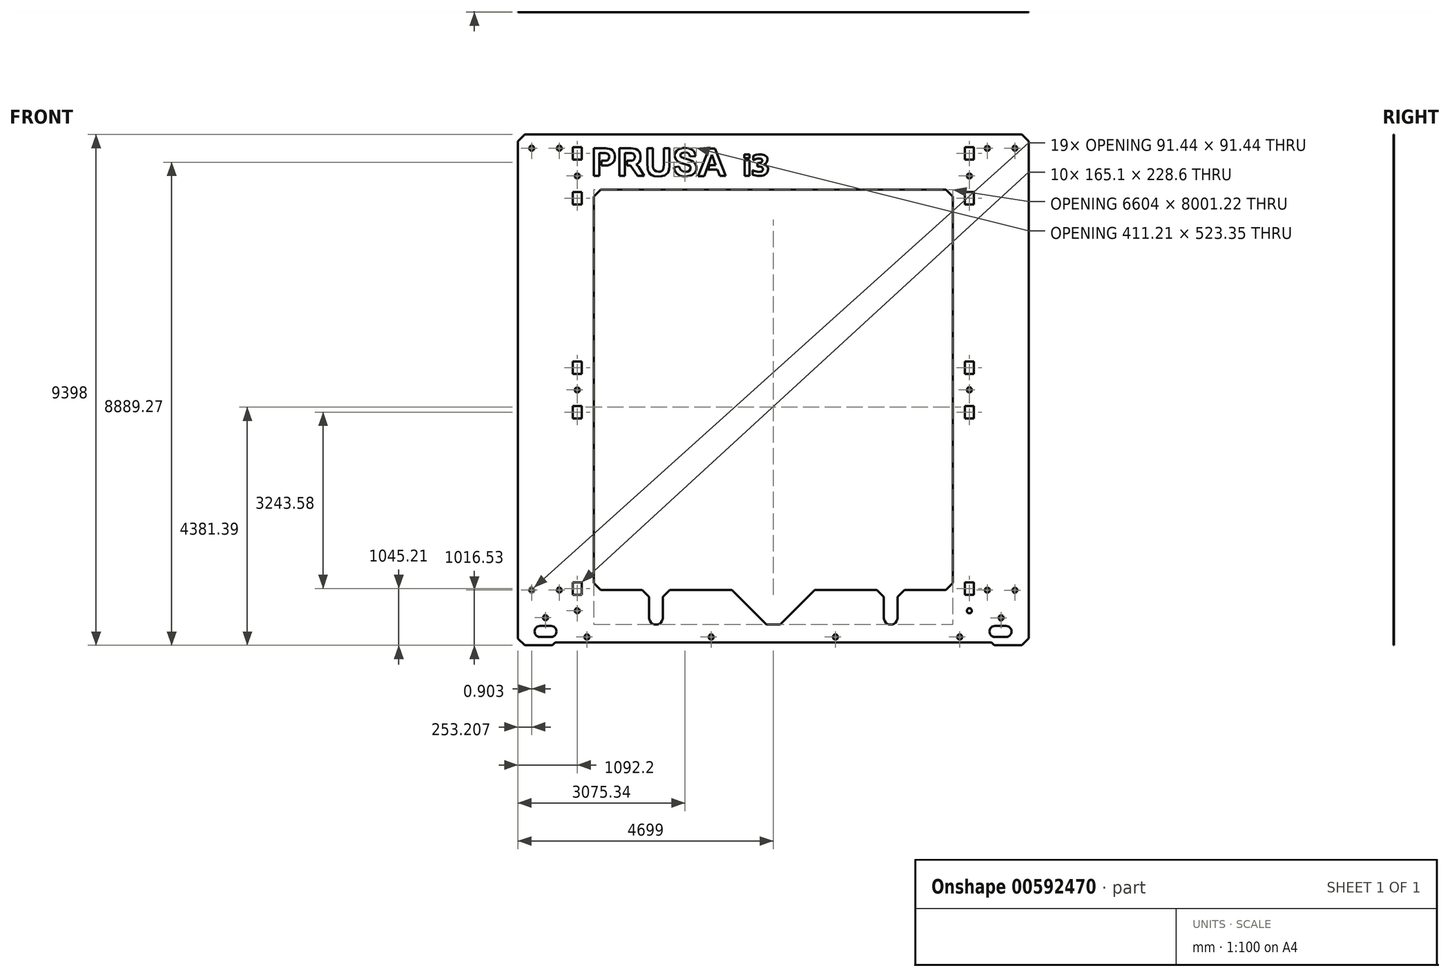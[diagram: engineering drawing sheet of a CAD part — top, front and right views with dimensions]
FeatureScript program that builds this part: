
annotation { "Feature Type Name" : "Feature", "Feature Type Description" : "" }
export const myFeature = defineFeature(function(context is Context, id is Id, definition is map)
    precondition{}
    {
        {
            var Q0;
            Q0=qCreatedBy(makeId("Front.planeOp"),FACE);
            var sketch = newSketch(context, id + "F0", { "sketchPlane" : qUnion([Q0])});
            skLineSegment(sketch, "E0", {"start": v(-2856.77, -127.8) * mm, "end": v(-2858.56, -127.8) * mm});
            skLineSegment(sketch, "E1", {"start": v(-1840.77, -1143.8) * mm, "end": v(-1842.56, -1143.8) * mm});
            skLineSegment(sketch, "E2", {"start": v(-4279.17, -127.8) * mm, "end": v(-5295.17, -1143.8) * mm});
            skLineSegment(sketch, "E3", {"start": v(-2856.77, -127.8) * mm, "end": v(-1840.77, -1143.8) * mm});
            skLineSegment(sketch, "E4", {"start": v(-2858.56, -127.8) * mm, "end": v(-1842.56, -1143.8) * mm});
            skLineSegment(sketch, "E5", {"start": v(-4280.96, -127.8) * mm, "end": v(-5296.96, -1143.8) * mm});
            skLineSegment(sketch, "E6", {"start": v(-5295.17, -1143.8) * mm, "end": v(-5296.96, -1143.8) * mm});
            skLineSegment(sketch, "E7", {"start": v(-4279.17, -127.8) * mm, "end": v(-4280.96, -127.8) * mm});
            skLineSegment(sketch, "E8", {"start": v(-7758.97, -4699.8) * mm, "end": v(-7885.97, -4577.68) * mm});
            skLineSegment(sketch, "E9", {"start": v(-7885.97, 4571.2) * mm, "end": v(-7758.97, 4698.2) * mm});
            skLineSegment(sketch, "E10", {"start": v(-7758.97, 4698.2) * mm, "end": v(1385.03, 4698.2) * mm});
            skLineSegment(sketch, "E11", {"start": v(1385.03, 4698.2) * mm, "end": v(1512.03, 4571.2) * mm});
            skLineSegment(sketch, "E12", {"start": v(1512.03, -4572.8) * mm, "end": v(1385.03, -4699.8) * mm});
            skLineSegment(sketch, "E13", {"start": v(877.03, -4699.8) * mm, "end": v(826.23, -4649) * mm});
            skLineSegment(sketch, "E14", {"start": v(826.23, -4649) * mm, "end": v(-7200.17, -4649) * mm});
            skLineSegment(sketch, "E15", {"start": v(-7200.17, -4649) * mm, "end": v(-7250.97, -4699.8) * mm});
            skLineSegment(sketch, "E16", {"start": v(-5853.97, -3683.8) * mm, "end": v(-6361.97, -3683.8) * mm});
            skLineSegment(sketch, "E17", {"start": v(-6361.97, -3683.8) * mm, "end": v(-6488.97, -3556.8) * mm});
            skLineSegment(sketch, "E18", {"start": v(-6488.97, -3556.8) * mm, "end": v(-6488.97, 3555.2) * mm});
            skLineSegment(sketch, "E19", {"start": v(-6488.97, 3555.2) * mm, "end": v(-6361.97, 3682.2) * mm});
            skLineSegment(sketch, "E20", {"start": v(-6361.97, 3682.2) * mm, "end": v(-11.97, 3682.2) * mm});
            skLineSegment(sketch, "E21", {"start": v(-11.97, 3682.2) * mm, "end": v(115.03, 3555.2) * mm});
            skLineSegment(sketch, "E22", {"start": v(115.03, 3555.2) * mm, "end": v(115.03, -3556.8) * mm});
            skLineSegment(sketch, "E23", {"start": v(115.03, -3556.8) * mm, "end": v(-11.97, -3683.8) * mm});
            skLineSegment(sketch, "E24", {"start": v(-11.97, -3683.8) * mm, "end": v(-519.97, -3683.8) * mm});
            skLineSegment(sketch, "E25", {"start": v(-3313.97, -4318.8) * mm, "end": v(-3059.97, -4318.8) * mm});
            skLineSegment(sketch, "E26", {"start": v(-3059.97, -4318.8) * mm, "end": v(-2424.97, -3683.8) * mm});
            skLineSegment(sketch, "E27", {"start": v(-3313.97, -4318.8) * mm, "end": v(-3948.97, -3683.8) * mm});
            skLineSegment(sketch, "E28", {"start": v(-5091.97, -3683.8) * mm, "end": v(-3948.97, -3683.8) * mm});
            skLineSegment(sketch, "E29", {"start": v(-2424.97, -3683.8) * mm, "end": v(-1281.97, -3683.8) * mm});
            skLineSegment(sketch, "E30", {"start": v(-2043.97, 1142.2) * mm, "end": v(-2043.97, 1140.4) * mm});
            skLineSegment(sketch, "E31", {"start": v(1004.03, -4547.4) * mm, "end": v(1011.13, -4546.47) * mm});
            skLineSegment(sketch, "E32", {"start": v(-7885.97, -4577.68) * mm, "end": v(-7885.97, 4571.2) * mm});
            skLineSegment(sketch, "E33", {"start": v(1512.03, 4571.2) * mm, "end": v(1512.03, -4572.8) * mm});
            skLineSegment(sketch, "E34", {"start": v(1385.03, -4699.8) * mm, "end": v(877.03, -4699.8) * mm});
            skLineSegment(sketch, "E35", {"start": v(-7250.97, -4699.8) * mm, "end": v(-7758.97, -4699.8) * mm});
            skLineSegment(sketch, "E36", {"start": v(803.36, -4394.07) * mm, "end": v(793.21, -4418.58) * mm});
            skLineSegment(sketch, "E37", {"start": v(789.75, -4444.87) * mm, "end": v(793.21, -4471.17) * mm});
            skLineSegment(sketch, "E38", {"start": v(865.06, -4346.74) * mm, "end": v(840.55, -4356.88) * mm});
            skLineSegment(sketch, "E39", {"start": v(1120.75, -4346.74) * mm, "end": v(1094.45, -4343.27) * mm});
            skLineSegment(sketch, "E40", {"start": v(1166.3, -4516.72) * mm, "end": v(1182.44, -4495.67) * mm});
            skLineSegment(sketch, "E41", {"start": v(1145.25, -4532.86) * mm, "end": v(1166.3, -4516.72) * mm});
            skLineSegment(sketch, "E42", {"start": v(1120.75, -4543.01) * mm, "end": v(1145.25, -4532.86) * mm});
            skLineSegment(sketch, "E43", {"start": v(840.55, -4532.86) * mm, "end": v(865.06, -4543.01) * mm});
            skLineSegment(sketch, "E44", {"start": v(865.06, -4543.01) * mm, "end": v(891.35, -4546.47) * mm});
            skLineSegment(sketch, "E45", {"start": v(793.21, -4471.17) * mm, "end": v(803.36, -4495.67) * mm});
            skLineSegment(sketch, "E46", {"start": v(1166.3, -4373.03) * mm, "end": v(1145.25, -4356.88) * mm});
            skLineSegment(sketch, "E47", {"start": v(1182.44, -4394.07) * mm, "end": v(1166.3, -4373.03) * mm});
            skLineSegment(sketch, "E48", {"start": v(891.35, -4343.27) * mm, "end": v(1094.45, -4343.27) * mm});
            skLineSegment(sketch, "E49", {"start": v(840.55, -4356.88) * mm, "end": v(819.51, -4373.03) * mm});
            skLineSegment(sketch, "E50", {"start": v(819.51, -4373.03) * mm, "end": v(803.36, -4394.07) * mm});
            skLineSegment(sketch, "E51", {"start": v(819.51, -4516.72) * mm, "end": v(840.55, -4532.86) * mm});
            skLineSegment(sketch, "E52", {"start": v(1192.59, -4418.58) * mm, "end": v(1182.44, -4394.07) * mm});
            skLineSegment(sketch, "E53", {"start": v(793.21, -4418.58) * mm, "end": v(789.75, -4444.87) * mm});
            skLineSegment(sketch, "E54", {"start": v(803.36, -4495.67) * mm, "end": v(819.51, -4516.72) * mm});
            skLineSegment(sketch, "E55", {"start": v(1192.59, -4471.17) * mm, "end": v(1196.05, -4444.87) * mm});
            skLineSegment(sketch, "E56", {"start": v(1182.44, -4495.67) * mm, "end": v(1192.59, -4471.17) * mm});
            skLineSegment(sketch, "E57", {"start": v(891.35, -4343.27) * mm, "end": v(865.06, -4346.74) * mm});
            skLineSegment(sketch, "E58", {"start": v(1096.15, -4546.47) * mm, "end": v(1120.75, -4543.01) * mm});
            skLineSegment(sketch, "E59", {"start": v(891.35, -4546.47) * mm, "end": v(996.92, -4546.47) * mm});
            skLineSegment(sketch, "E60", {"start": v(1196.05, -4444.87) * mm, "end": v(1192.59, -4418.58) * mm});
            skLineSegment(sketch, "E61", {"start": v(1145.25, -4356.88) * mm, "end": v(1120.75, -4346.74) * mm});
            skLineSegment(sketch, "E62", {"start": v(996.92, -4546.47) * mm, "end": v(1004.03, -4547.4) * mm});
            skLineSegment(sketch, "E63", {"start": v(996.92, -4546.47) * mm, "end": v(1011.13, -4546.47) * mm});
            skLineSegment(sketch, "E64", {"start": v(1011.13, -4546.47) * mm, "end": v(1096.15, -4546.47) * mm});
            skLineSegment(sketch, "E65", {"start": v(-7580.5, -4444.87) * mm, "end": v(-7577.04, -4471.17) * mm});
            skLineSegment(sketch, "E66", {"start": v(-7566.89, -4394.07) * mm, "end": v(-7577.04, -4418.58) * mm});
            skLineSegment(sketch, "E67", {"start": v(-7505.2, -4346.74) * mm, "end": v(-7529.7, -4356.88) * mm});
            skLineSegment(sketch, "E68", {"start": v(-7249.5, -4346.74) * mm, "end": v(-7275.8, -4343.27) * mm});
            skLineSegment(sketch, "E69", {"start": v(-7203.96, -4516.72) * mm, "end": v(-7187.81, -4495.67) * mm});
            skLineSegment(sketch, "E70", {"start": v(-7225, -4532.86) * mm, "end": v(-7203.96, -4516.72) * mm});
            skLineSegment(sketch, "E71", {"start": v(-7249.5, -4543.01) * mm, "end": v(-7225, -4532.86) * mm});
            skLineSegment(sketch, "E72", {"start": v(-7529.7, -4532.86) * mm, "end": v(-7505.2, -4543.01) * mm});
            skLineSegment(sketch, "E73", {"start": v(-7505.2, -4543.01) * mm, "end": v(-7478.9, -4546.47) * mm});
            skLineSegment(sketch, "E74", {"start": v(-7577.04, -4471.17) * mm, "end": v(-7566.89, -4495.67) * mm});
            skLineSegment(sketch, "E75", {"start": v(-7203.96, -4373.03) * mm, "end": v(-7225, -4356.88) * mm});
            skLineSegment(sketch, "E76", {"start": v(-7187.81, -4394.07) * mm, "end": v(-7203.96, -4373.03) * mm});
            skLineSegment(sketch, "E77", {"start": v(-7478.9, -4343.27) * mm, "end": v(-7275.8, -4343.27) * mm});
            skLineSegment(sketch, "E78", {"start": v(-7529.7, -4356.88) * mm, "end": v(-7550.74, -4373.03) * mm});
            skLineSegment(sketch, "E79", {"start": v(-7550.74, -4373.03) * mm, "end": v(-7566.89, -4394.07) * mm});
            skLineSegment(sketch, "E80", {"start": v(-7550.74, -4516.72) * mm, "end": v(-7529.7, -4532.86) * mm});
            skLineSegment(sketch, "E81", {"start": v(-7177.66, -4418.58) * mm, "end": v(-7187.81, -4394.07) * mm});
            skLineSegment(sketch, "E82", {"start": v(-7577.04, -4418.58) * mm, "end": v(-7580.5, -4444.87) * mm});
            skLineSegment(sketch, "E83", {"start": v(-7566.89, -4495.67) * mm, "end": v(-7550.74, -4516.72) * mm});
            skLineSegment(sketch, "E84", {"start": v(-7177.66, -4471.17) * mm, "end": v(-7174.2, -4444.87) * mm});
            skLineSegment(sketch, "E85", {"start": v(-7187.81, -4495.67) * mm, "end": v(-7177.66, -4471.17) * mm});
            skLineSegment(sketch, "E86", {"start": v(-7478.9, -4343.27) * mm, "end": v(-7505.2, -4346.74) * mm});
            skLineSegment(sketch, "E87", {"start": v(-7274.1, -4546.47) * mm, "end": v(-7249.5, -4543.01) * mm});
            skLineSegment(sketch, "E88", {"start": v(-7478.9, -4546.47) * mm, "end": v(-7274.1, -4546.47) * mm});
            skLineSegment(sketch, "E89", {"start": v(-7174.2, -4444.87) * mm, "end": v(-7177.66, -4418.58) * mm});
            skLineSegment(sketch, "E90", {"start": v(-7225, -4356.88) * mm, "end": v(-7249.5, -4346.74) * mm});
            skLineSegment(sketch, "E91", {"start": v(337.28, 4234.46) * mm, "end": v(337.28, 4463.06) * mm});
            skLineSegment(sketch, "E92", {"start": v(337.28, 4463.06) * mm, "end": v(502.38, 4463.06) * mm});
            skLineSegment(sketch, "E93", {"start": v(502.38, 4463.06) * mm, "end": v(502.38, 4234.46) * mm});
            skLineSegment(sketch, "E94", {"start": v(502.38, 4234.46) * mm, "end": v(337.28, 4234.46) * mm});
            skLineSegment(sketch, "E95", {"start": v(337.28, 3414.04) * mm, "end": v(337.28, 3642.64) * mm});
            skLineSegment(sketch, "E96", {"start": v(337.28, 3642.64) * mm, "end": v(502.38, 3642.64) * mm});
            skLineSegment(sketch, "E97", {"start": v(502.38, 3642.64) * mm, "end": v(502.38, 3414.04) * mm});
            skLineSegment(sketch, "E98", {"start": v(502.38, 3414.04) * mm, "end": v(337.28, 3414.04) * mm});
            skLineSegment(sketch, "E99", {"start": v(337.28, 295.1) * mm, "end": v(337.28, 523.7) * mm});
            skLineSegment(sketch, "E100", {"start": v(337.28, 523.7) * mm, "end": v(502.38, 523.7) * mm});
            skLineSegment(sketch, "E101", {"start": v(502.38, 523.7) * mm, "end": v(502.38, 295.1) * mm});
            skLineSegment(sketch, "E102", {"start": v(502.38, 295.1) * mm, "end": v(337.28, 295.1) * mm});
            skLineSegment(sketch, "E103", {"start": v(337.28, -525.32) * mm, "end": v(337.28, -296.72) * mm});
            skLineSegment(sketch, "E104", {"start": v(337.28, -296.72) * mm, "end": v(502.38, -296.72) * mm});
            skLineSegment(sketch, "E105", {"start": v(502.38, -296.72) * mm, "end": v(502.38, -525.32) * mm});
            skLineSegment(sketch, "E106", {"start": v(502.38, -525.32) * mm, "end": v(337.28, -525.32) * mm});
            skLineSegment(sketch, "E107", {"start": v(337.28, -3768.9) * mm, "end": v(337.28, -3540.3) * mm});
            skLineSegment(sketch, "E108", {"start": v(337.28, -3540.3) * mm, "end": v(502.38, -3540.3) * mm});
            skLineSegment(sketch, "E109", {"start": v(502.38, -3540.3) * mm, "end": v(502.38, -3768.9) * mm});
            skLineSegment(sketch, "E110", {"start": v(502.38, -3768.9) * mm, "end": v(337.28, -3768.9) * mm});
            skLineSegment(sketch, "E111", {"start": v(-6876.32, 4234.46) * mm, "end": v(-6876.32, 4463.06) * mm});
            skLineSegment(sketch, "E112", {"start": v(-6876.32, 4463.06) * mm, "end": v(-6711.22, 4463.06) * mm});
            skLineSegment(sketch, "E113", {"start": v(-6711.22, 4463.06) * mm, "end": v(-6711.22, 4234.46) * mm});
            skLineSegment(sketch, "E114", {"start": v(-6711.22, 4234.46) * mm, "end": v(-6876.32, 4234.46) * mm});
            skLineSegment(sketch, "E115", {"start": v(-6876.32, 3414.04) * mm, "end": v(-6876.32, 3642.64) * mm});
            skLineSegment(sketch, "E116", {"start": v(-6876.32, 3642.64) * mm, "end": v(-6711.22, 3642.64) * mm});
            skLineSegment(sketch, "E117", {"start": v(-6711.22, 3642.64) * mm, "end": v(-6711.22, 3414.04) * mm});
            skLineSegment(sketch, "E118", {"start": v(-6711.22, 3414.04) * mm, "end": v(-6876.32, 3414.04) * mm});
            skLineSegment(sketch, "E119", {"start": v(-6876.32, 295.1) * mm, "end": v(-6876.32, 523.7) * mm});
            skLineSegment(sketch, "E120", {"start": v(-6876.32, 523.7) * mm, "end": v(-6711.22, 523.7) * mm});
            skLineSegment(sketch, "E121", {"start": v(-6711.22, 523.7) * mm, "end": v(-6711.22, 295.1) * mm});
            skLineSegment(sketch, "E122", {"start": v(-6711.22, 295.1) * mm, "end": v(-6876.32, 295.1) * mm});
            skLineSegment(sketch, "E123", {"start": v(-6876.32, -525.32) * mm, "end": v(-6876.32, -296.72) * mm});
            skLineSegment(sketch, "E124", {"start": v(-6876.32, -296.72) * mm, "end": v(-6711.22, -296.72) * mm});
            skLineSegment(sketch, "E125", {"start": v(-6711.22, -296.72) * mm, "end": v(-6711.22, -525.32) * mm});
            skLineSegment(sketch, "E126", {"start": v(-6711.22, -525.32) * mm, "end": v(-6876.32, -525.32) * mm});
            skLineSegment(sketch, "E127", {"start": v(-6876.32, -3768.9) * mm, "end": v(-6876.32, -3540.3) * mm});
            skLineSegment(sketch, "E128", {"start": v(-6876.32, -3540.3) * mm, "end": v(-6711.22, -3540.3) * mm});
            skLineSegment(sketch, "E129", {"start": v(-6711.22, -3540.3) * mm, "end": v(-6711.22, -3768.9) * mm});
            skLineSegment(sketch, "E130", {"start": v(-6711.22, -3768.9) * mm, "end": v(-6876.32, -3768.9) * mm});
            skLineSegment(sketch, "E131", {"start": v(465.53, -0.8) * mm, "end": v(463.97, 11.02) * mm});
            skLineSegment(sketch, "E132", {"start": v(463.97, 11.02) * mm, "end": v(459.4, 22.05) * mm});
            skLineSegment(sketch, "E133", {"start": v(459.4, 22.05) * mm, "end": v(452.13, 31.52) * mm});
            skLineSegment(sketch, "E134", {"start": v(452.13, 31.52) * mm, "end": v(442.66, 38.78) * mm});
            skLineSegment(sketch, "E135", {"start": v(442.66, 38.78) * mm, "end": v(431.64, 43.35) * mm});
            skLineSegment(sketch, "E136", {"start": v(431.64, 43.35) * mm, "end": v(419.8, 44.9) * mm});
            skLineSegment(sketch, "E137", {"start": v(419.8, 44.9) * mm, "end": v(407.97, 43.34) * mm});
            skLineSegment(sketch, "E138", {"start": v(407.97, 43.34) * mm, "end": v(396.94, 38.78) * mm});
            skLineSegment(sketch, "E139", {"start": v(396.94, 38.78) * mm, "end": v(387.47, 31.5) * mm});
            skLineSegment(sketch, "E140", {"start": v(387.47, 31.5) * mm, "end": v(380.21, 22.04) * mm});
            skLineSegment(sketch, "E141", {"start": v(380.21, 22.04) * mm, "end": v(375.64, 11.01) * mm});
            skLineSegment(sketch, "E142", {"start": v(375.64, 11.01) * mm, "end": v(374.09, -0.82) * mm});
            skLineSegment(sketch, "E143", {"start": v(374.09, -0.82) * mm, "end": v(375.65, -12.66) * mm});
            skLineSegment(sketch, "E144", {"start": v(375.65, -12.66) * mm, "end": v(380.22, -23.68) * mm});
            skLineSegment(sketch, "E145", {"start": v(380.22, -23.68) * mm, "end": v(387.48, -33.15) * mm});
            skLineSegment(sketch, "E146", {"start": v(387.48, -33.15) * mm, "end": v(396.95, -40.41) * mm});
            skLineSegment(sketch, "E147", {"start": v(396.95, -40.41) * mm, "end": v(407.98, -44.98) * mm});
            skLineSegment(sketch, "E148", {"start": v(407.98, -44.98) * mm, "end": v(419.82, -46.54) * mm});
            skLineSegment(sketch, "E149", {"start": v(419.82, -46.54) * mm, "end": v(431.65, -44.98) * mm});
            skLineSegment(sketch, "E150", {"start": v(431.65, -44.98) * mm, "end": v(442.67, -40.4) * mm});
            skLineSegment(sketch, "E151", {"start": v(442.67, -40.4) * mm, "end": v(452.14, -33.14) * mm});
            skLineSegment(sketch, "E152", {"start": v(452.14, -33.14) * mm, "end": v(459.4, -23.67) * mm});
            skLineSegment(sketch, "E153", {"start": v(459.4, -23.67) * mm, "end": v(463.97, -12.64) * mm});
            skLineSegment(sketch, "E154", {"start": v(463.97, -12.64) * mm, "end": v(465.53, -0.8) * mm});
            skLineSegment(sketch, "E155", {"start": v(465.85, 3936.2) * mm, "end": v(464.22, 3948.02) * mm});
            skLineSegment(sketch, "E156", {"start": v(464.22, 3948.02) * mm, "end": v(459.58, 3959.01) * mm});
            skLineSegment(sketch, "E157", {"start": v(459.58, 3959.01) * mm, "end": v(452.25, 3968.43) * mm});
            skLineSegment(sketch, "E158", {"start": v(452.25, 3968.43) * mm, "end": v(442.74, 3975.64) * mm});
            skLineSegment(sketch, "E159", {"start": v(442.74, 3975.64) * mm, "end": v(431.68, 3980.13) * mm});
            skLineSegment(sketch, "E160", {"start": v(431.68, 3980.13) * mm, "end": v(419.84, 3981.62) * mm});
            skLineSegment(sketch, "E161", {"start": v(419.84, 3981.62) * mm, "end": v(408.01, 3979.98) * mm});
            skLineSegment(sketch, "E162", {"start": v(408.01, 3979.98) * mm, "end": v(397.02, 3975.34) * mm});
            skLineSegment(sketch, "E163", {"start": v(397.02, 3975.34) * mm, "end": v(387.6, 3968.02) * mm});
            skLineSegment(sketch, "E164", {"start": v(387.6, 3968.02) * mm, "end": v(380.4, 3958.5) * mm});
            skLineSegment(sketch, "E165", {"start": v(380.4, 3958.5) * mm, "end": v(375.9, 3947.44) * mm});
            skLineSegment(sketch, "E166", {"start": v(375.9, 3947.44) * mm, "end": v(374.41, 3935.6) * mm});
            skLineSegment(sketch, "E167", {"start": v(374.41, 3935.6) * mm, "end": v(376.05, 3923.78) * mm});
            skLineSegment(sketch, "E168", {"start": v(376.05, 3923.78) * mm, "end": v(380.69, 3912.78) * mm});
            skLineSegment(sketch, "E169", {"start": v(380.69, 3912.78) * mm, "end": v(388.01, 3903.36) * mm});
            skLineSegment(sketch, "E170", {"start": v(388.01, 3903.36) * mm, "end": v(397.53, 3896.15) * mm});
            skLineSegment(sketch, "E171", {"start": v(397.53, 3896.15) * mm, "end": v(408.59, 3891.66) * mm});
            skLineSegment(sketch, "E172", {"start": v(408.59, 3891.66) * mm, "end": v(420.43, 3890.18) * mm});
            skLineSegment(sketch, "E173", {"start": v(420.43, 3890.18) * mm, "end": v(432.25, 3891.81) * mm});
            skLineSegment(sketch, "E174", {"start": v(432.25, 3891.81) * mm, "end": v(443.25, 3896.45) * mm});
            skLineSegment(sketch, "E175", {"start": v(443.25, 3896.45) * mm, "end": v(452.67, 3903.78) * mm});
            skLineSegment(sketch, "E176", {"start": v(452.67, 3903.78) * mm, "end": v(459.87, 3913.3) * mm});
            skLineSegment(sketch, "E177", {"start": v(459.87, 3913.3) * mm, "end": v(464.37, 3924.35) * mm});
            skLineSegment(sketch, "E178", {"start": v(464.37, 3924.35) * mm, "end": v(465.85, 3936.2) * mm});
            skLineSegment(sketch, "E179", {"start": v(750.1, 4489.67) * mm, "end": v(738.27, 4488.1) * mm});
            skLineSegment(sketch, "E180", {"start": v(795.83, 4443.95) * mm, "end": v(794.27, 4455.79) * mm});
            skLineSegment(sketch, "E181", {"start": v(794.27, 4455.79) * mm, "end": v(789.7, 4466.81) * mm});
            skLineSegment(sketch, "E182", {"start": v(789.7, 4466.81) * mm, "end": v(782.43, 4476.28) * mm});
            skLineSegment(sketch, "E183", {"start": v(782.43, 4476.28) * mm, "end": v(772.96, 4483.54) * mm});
            skLineSegment(sketch, "E184", {"start": v(738.27, 4488.1) * mm, "end": v(727.24, 4483.54) * mm});
            skLineSegment(sketch, "E185", {"start": v(727.24, 4483.54) * mm, "end": v(717.78, 4476.27) * mm});
            skLineSegment(sketch, "E186", {"start": v(717.78, 4476.27) * mm, "end": v(710.51, 4466.8) * mm});
            skLineSegment(sketch, "E187", {"start": v(750.12, 4398.23) * mm, "end": v(761.95, 4399.79) * mm});
            skLineSegment(sketch, "E188", {"start": v(761.95, 4399.79) * mm, "end": v(772.98, 4404.35) * mm});
            skLineSegment(sketch, "E189", {"start": v(772.96, 4483.54) * mm, "end": v(761.94, 4488.1) * mm});
            skLineSegment(sketch, "E190", {"start": v(761.94, 4488.1) * mm, "end": v(750.1, 4489.67) * mm});
            skLineSegment(sketch, "E191", {"start": v(710.51, 4466.8) * mm, "end": v(705.95, 4455.77) * mm});
            skLineSegment(sketch, "E192", {"start": v(705.95, 4455.77) * mm, "end": v(704.39, 4443.94) * mm});
            skLineSegment(sketch, "E193", {"start": v(704.39, 4443.94) * mm, "end": v(705.95, 4432.1) * mm});
            skLineSegment(sketch, "E194", {"start": v(705.95, 4432.1) * mm, "end": v(710.52, 4421.08) * mm});
            skLineSegment(sketch, "E195", {"start": v(772.98, 4404.35) * mm, "end": v(782.44, 4411.62) * mm});
            skLineSegment(sketch, "E196", {"start": v(782.44, 4411.62) * mm, "end": v(789.7, 4421.1) * mm});
            skLineSegment(sketch, "E197", {"start": v(789.7, 4421.1) * mm, "end": v(794.27, 4432.12) * mm});
            skLineSegment(sketch, "E198", {"start": v(794.27, 4432.12) * mm, "end": v(795.83, 4443.95) * mm});
            skLineSegment(sketch, "E199", {"start": v(710.52, 4421.08) * mm, "end": v(717.79, 4411.61) * mm});
            skLineSegment(sketch, "E200", {"start": v(717.79, 4411.61) * mm, "end": v(727.26, 4404.35) * mm});
            skLineSegment(sketch, "E201", {"start": v(727.26, 4404.35) * mm, "end": v(738.28, 4399.78) * mm});
            skLineSegment(sketch, "E202", {"start": v(738.28, 4399.78) * mm, "end": v(750.12, 4398.23) * mm});
            skLineSegment(sketch, "E203", {"start": v(1301.62, 4456.62) * mm, "end": v(1297.05, 4467.65) * mm});
            skLineSegment(sketch, "E204", {"start": v(1234.6, 4484.38) * mm, "end": v(1225.12, 4477.1) * mm});
            skLineSegment(sketch, "E205", {"start": v(1225.12, 4477.1) * mm, "end": v(1217.86, 4467.64) * mm});
            skLineSegment(sketch, "E206", {"start": v(1225.13, 4412.45) * mm, "end": v(1234.6, 4405.19) * mm});
            skLineSegment(sketch, "E207", {"start": v(1234.6, 4405.19) * mm, "end": v(1245.63, 4400.62) * mm});
            skLineSegment(sketch, "E208", {"start": v(1245.63, 4400.62) * mm, "end": v(1257.46, 4399.06) * mm});
            skLineSegment(sketch, "E209", {"start": v(1213.3, 4432.95) * mm, "end": v(1217.87, 4421.92) * mm});
            skLineSegment(sketch, "E210", {"start": v(1217.87, 4421.92) * mm, "end": v(1225.13, 4412.45) * mm});
            skLineSegment(sketch, "E211", {"start": v(1217.86, 4467.64) * mm, "end": v(1213.3, 4456.61) * mm});
            skLineSegment(sketch, "E212", {"start": v(1213.3, 4456.61) * mm, "end": v(1211.74, 4444.78) * mm});
            skLineSegment(sketch, "E213", {"start": v(1211.74, 4444.78) * mm, "end": v(1213.3, 4432.95) * mm});
            skLineSegment(sketch, "E214", {"start": v(1280.31, 4484.38) * mm, "end": v(1269.28, 4488.95) * mm});
            skLineSegment(sketch, "E215", {"start": v(1289.78, 4477.12) * mm, "end": v(1280.31, 4484.38) * mm});
            skLineSegment(sketch, "E216", {"start": v(1297.05, 4467.65) * mm, "end": v(1289.78, 4477.12) * mm});
            skLineSegment(sketch, "E217", {"start": v(1269.28, 4488.95) * mm, "end": v(1257.45, 4490.5) * mm});
            skLineSegment(sketch, "E218", {"start": v(1257.45, 4490.5) * mm, "end": v(1245.62, 4488.95) * mm});
            skLineSegment(sketch, "E219", {"start": v(1245.62, 4488.95) * mm, "end": v(1234.6, 4484.38) * mm});
            skLineSegment(sketch, "E220", {"start": v(1303.18, 4444.8) * mm, "end": v(1301.62, 4456.62) * mm});
            skLineSegment(sketch, "E221", {"start": v(1301.62, 4432.96) * mm, "end": v(1303.18, 4444.8) * mm});
            skLineSegment(sketch, "E222", {"start": v(1257.46, 4399.06) * mm, "end": v(1269.3, 4400.62) * mm});
            skLineSegment(sketch, "E223", {"start": v(1269.3, 4400.62) * mm, "end": v(1280.32, 4405.2) * mm});
            skLineSegment(sketch, "E224", {"start": v(1280.32, 4405.2) * mm, "end": v(1289.8, 4412.46) * mm});
            skLineSegment(sketch, "E225", {"start": v(1289.8, 4412.46) * mm, "end": v(1297.06, 4421.93) * mm});
            skLineSegment(sketch, "E226", {"start": v(1297.06, 4421.93) * mm, "end": v(1301.62, 4432.96) * mm});
            skLineSegment(sketch, "E227", {"start": v(738.55, -3639.88) * mm, "end": v(727.52, -3644.44) * mm});
            skLineSegment(sketch, "E228", {"start": v(789.98, -3661.17) * mm, "end": v(782.71, -3651.7) * mm});
            skLineSegment(sketch, "E229", {"start": v(706.22, -3672.2) * mm, "end": v(704.67, -3684.04) * mm});
            skLineSegment(sketch, "E230", {"start": v(794.55, -3672.2) * mm, "end": v(789.98, -3661.17) * mm});
            skLineSegment(sketch, "E231", {"start": v(718.05, -3651.71) * mm, "end": v(710.79, -3661.18) * mm});
            skLineSegment(sketch, "E232", {"start": v(796.1, -3684.03) * mm, "end": v(794.55, -3672.2) * mm});
            skLineSegment(sketch, "E233", {"start": v(727.52, -3644.44) * mm, "end": v(718.05, -3651.71) * mm});
            skLineSegment(sketch, "E234", {"start": v(762.21, -3639.87) * mm, "end": v(750.38, -3638.32) * mm});
            skLineSegment(sketch, "E235", {"start": v(727.53, -3723.63) * mm, "end": v(738.56, -3728.2) * mm});
            skLineSegment(sketch, "E236", {"start": v(762.23, -3728.2) * mm, "end": v(773.25, -3723.63) * mm});
            skLineSegment(sketch, "E237", {"start": v(773.25, -3723.63) * mm, "end": v(782.72, -3716.36) * mm});
            skLineSegment(sketch, "E238", {"start": v(710.8, -3706.9) * mm, "end": v(718.06, -3716.37) * mm});
            skLineSegment(sketch, "E239", {"start": v(718.06, -3716.37) * mm, "end": v(727.53, -3723.63) * mm});
            skLineSegment(sketch, "E240", {"start": v(750.38, -3638.32) * mm, "end": v(738.55, -3639.88) * mm});
            skLineSegment(sketch, "E241", {"start": v(738.56, -3728.2) * mm, "end": v(750.4, -3729.76) * mm});
            skLineSegment(sketch, "E242", {"start": v(750.4, -3729.76) * mm, "end": v(762.23, -3728.2) * mm});
            skLineSegment(sketch, "E243", {"start": v(782.71, -3651.7) * mm, "end": v(773.24, -3644.44) * mm});
            skLineSegment(sketch, "E244", {"start": v(773.24, -3644.44) * mm, "end": v(762.21, -3639.87) * mm});
            skLineSegment(sketch, "E245", {"start": v(789.99, -3706.9) * mm, "end": v(794.55, -3695.86) * mm});
            skLineSegment(sketch, "E246", {"start": v(794.55, -3695.86) * mm, "end": v(796.1, -3684.03) * mm});
            skLineSegment(sketch, "E247", {"start": v(704.67, -3684.04) * mm, "end": v(706.23, -3695.88) * mm});
            skLineSegment(sketch, "E248", {"start": v(706.23, -3695.88) * mm, "end": v(710.8, -3706.9) * mm});
            skLineSegment(sketch, "E249", {"start": v(782.72, -3716.36) * mm, "end": v(789.99, -3706.9) * mm});
            skLineSegment(sketch, "E250", {"start": v(710.79, -3661.18) * mm, "end": v(706.22, -3672.2) * mm});
            skLineSegment(sketch, "E251", {"start": v(1269.69, -3729.33) * mm, "end": v(1280.72, -3724.77) * mm});
            skLineSegment(sketch, "E252", {"start": v(1280.72, -3724.77) * mm, "end": v(1290.18, -3717.5) * mm});
            skLineSegment(sketch, "E253", {"start": v(1290.18, -3717.5) * mm, "end": v(1297.45, -3708.03) * mm});
            skLineSegment(sketch, "E254", {"start": v(1246.01, -3641.01) * mm, "end": v(1234.98, -3645.58) * mm});
            skLineSegment(sketch, "E255", {"start": v(1234.98, -3645.58) * mm, "end": v(1225.52, -3652.85) * mm});
            skLineSegment(sketch, "E256", {"start": v(1218.26, -3708.04) * mm, "end": v(1225.53, -3717.5) * mm});
            skLineSegment(sketch, "E257", {"start": v(1225.53, -3717.5) * mm, "end": v(1235, -3724.77) * mm});
            skLineSegment(sketch, "E258", {"start": v(1212.13, -3685.18) * mm, "end": v(1213.69, -3697.01) * mm});
            skLineSegment(sketch, "E259", {"start": v(1213.69, -3697.01) * mm, "end": v(1218.26, -3708.04) * mm});
            skLineSegment(sketch, "E260", {"start": v(1225.52, -3652.85) * mm, "end": v(1218.25, -3662.32) * mm});
            skLineSegment(sketch, "E261", {"start": v(1218.25, -3662.32) * mm, "end": v(1213.69, -3673.35) * mm});
            skLineSegment(sketch, "E262", {"start": v(1213.69, -3673.35) * mm, "end": v(1212.13, -3685.18) * mm});
            skLineSegment(sketch, "E263", {"start": v(1235, -3724.77) * mm, "end": v(1246.02, -3729.34) * mm});
            skLineSegment(sketch, "E264", {"start": v(1246.02, -3729.34) * mm, "end": v(1257.86, -3730.9) * mm});
            skLineSegment(sketch, "E265", {"start": v(1257.86, -3730.9) * mm, "end": v(1269.69, -3729.33) * mm});
            skLineSegment(sketch, "E266", {"start": v(1269.68, -3641.01) * mm, "end": v(1257.84, -3639.45) * mm});
            skLineSegment(sketch, "E267", {"start": v(1297.44, -3662.3) * mm, "end": v(1290.17, -3652.84) * mm});
            skLineSegment(sketch, "E268", {"start": v(1302.01, -3673.33) * mm, "end": v(1297.44, -3662.3) * mm});
            skLineSegment(sketch, "E269", {"start": v(1290.17, -3652.84) * mm, "end": v(1280.7, -3645.58) * mm});
            skLineSegment(sketch, "E270", {"start": v(1280.7, -3645.58) * mm, "end": v(1269.68, -3641.01) * mm});
            skLineSegment(sketch, "E271", {"start": v(1303.57, -3685.17) * mm, "end": v(1302.01, -3673.33) * mm});
            skLineSegment(sketch, "E272", {"start": v(1257.84, -3639.45) * mm, "end": v(1246.01, -3641.01) * mm});
            skLineSegment(sketch, "E273", {"start": v(1297.45, -3708.03) * mm, "end": v(1302.01, -3697) * mm});
            skLineSegment(sketch, "E274", {"start": v(1302.01, -3697) * mm, "end": v(1303.57, -3685.17) * mm});
            skLineSegment(sketch, "E275", {"start": v(1043.71, -4169.77) * mm, "end": v(1036.44, -4160.3) * mm});
            skLineSegment(sketch, "E276", {"start": v(1048.28, -4204.46) * mm, "end": v(1049.84, -4192.63) * mm});
            skLineSegment(sketch, "E277", {"start": v(971.79, -4160.31) * mm, "end": v(964.52, -4169.78) * mm});
            skLineSegment(sketch, "E278", {"start": v(964.52, -4169.78) * mm, "end": v(959.96, -4180.8) * mm});
            skLineSegment(sketch, "E279", {"start": v(959.96, -4180.8) * mm, "end": v(958.4, -4192.64) * mm});
            skLineSegment(sketch, "E280", {"start": v(971.8, -4224.97) * mm, "end": v(981.26, -4232.23) * mm});
            skLineSegment(sketch, "E281", {"start": v(981.26, -4232.23) * mm, "end": v(992.3, -4236.8) * mm});
            skLineSegment(sketch, "E282", {"start": v(992.3, -4236.8) * mm, "end": v(1004.13, -4238.36) * mm});
            skLineSegment(sketch, "E283", {"start": v(1004.13, -4238.36) * mm, "end": v(1015.96, -4236.8) * mm});
            skLineSegment(sketch, "E284", {"start": v(1015.96, -4236.8) * mm, "end": v(1026.98, -4232.23) * mm});
            skLineSegment(sketch, "E285", {"start": v(1026.98, -4232.23) * mm, "end": v(1036.45, -4224.96) * mm});
            skLineSegment(sketch, "E286", {"start": v(1036.45, -4224.96) * mm, "end": v(1043.72, -4215.5) * mm});
            skLineSegment(sketch, "E287", {"start": v(1043.72, -4215.5) * mm, "end": v(1048.28, -4204.46) * mm});
            skLineSegment(sketch, "E288", {"start": v(1004.11, -4146.92) * mm, "end": v(992.28, -4148.48) * mm});
            skLineSegment(sketch, "E289", {"start": v(992.28, -4148.48) * mm, "end": v(981.25, -4153.05) * mm});
            skLineSegment(sketch, "E290", {"start": v(981.25, -4153.05) * mm, "end": v(971.79, -4160.31) * mm});
            skLineSegment(sketch, "E291", {"start": v(958.4, -4192.64) * mm, "end": v(959.96, -4204.48) * mm});
            skLineSegment(sketch, "E292", {"start": v(959.96, -4204.48) * mm, "end": v(964.53, -4215.5) * mm});
            skLineSegment(sketch, "E293", {"start": v(964.53, -4215.5) * mm, "end": v(971.8, -4224.97) * mm});
            skLineSegment(sketch, "E294", {"start": v(1049.84, -4192.63) * mm, "end": v(1048.28, -4180.8) * mm});
            skLineSegment(sketch, "E295", {"start": v(1048.28, -4180.8) * mm, "end": v(1043.71, -4169.77) * mm});
            skLineSegment(sketch, "E296", {"start": v(1036.44, -4160.3) * mm, "end": v(1026.97, -4153.04) * mm});
            skLineSegment(sketch, "E297", {"start": v(1026.97, -4153.04) * mm, "end": v(1015.95, -4148.47) * mm});
            skLineSegment(sketch, "E298", {"start": v(1015.95, -4148.47) * mm, "end": v(1004.11, -4146.92) * mm});
            skLineSegment(sketch, "E299", {"start": v(465.53, -4064.8) * mm, "end": v(463.97, -4052.98) * mm});
            skLineSegment(sketch, "E300", {"start": v(463.97, -4052.98) * mm, "end": v(459.4, -4041.96) * mm});
            skLineSegment(sketch, "E301", {"start": v(459.4, -4041.96) * mm, "end": v(452.14, -4032.5) * mm});
            skLineSegment(sketch, "E302", {"start": v(452.14, -4032.5) * mm, "end": v(442.68, -4025.23) * mm});
            skLineSegment(sketch, "E303", {"start": v(442.68, -4025.23) * mm, "end": v(431.66, -4020.66) * mm});
            skLineSegment(sketch, "E304", {"start": v(431.66, -4020.66) * mm, "end": v(419.83, -4019.1) * mm});
            skLineSegment(sketch, "E305", {"start": v(419.83, -4019.1) * mm, "end": v(408, -4020.66) * mm});
            skLineSegment(sketch, "E306", {"start": v(408, -4020.66) * mm, "end": v(396.98, -4025.23) * mm});
            skLineSegment(sketch, "E307", {"start": v(396.98, -4025.23) * mm, "end": v(387.51, -4032.5) * mm});
            skLineSegment(sketch, "E308", {"start": v(387.51, -4032.5) * mm, "end": v(380.25, -4041.96) * mm});
            skLineSegment(sketch, "E309", {"start": v(380.25, -4041.96) * mm, "end": v(375.68, -4052.98) * mm});
            skLineSegment(sketch, "E310", {"start": v(375.68, -4052.98) * mm, "end": v(374.13, -4064.8) * mm});
            skLineSegment(sketch, "E311", {"start": v(374.13, -4064.8) * mm, "end": v(375.68, -4076.64) * mm});
            skLineSegment(sketch, "E312", {"start": v(375.68, -4076.64) * mm, "end": v(380.25, -4087.66) * mm});
            skLineSegment(sketch, "E313", {"start": v(380.25, -4087.66) * mm, "end": v(387.51, -4097.12) * mm});
            skLineSegment(sketch, "E314", {"start": v(387.51, -4097.12) * mm, "end": v(396.98, -4104.39) * mm});
            skLineSegment(sketch, "E315", {"start": v(396.98, -4104.39) * mm, "end": v(408, -4108.95) * mm});
            skLineSegment(sketch, "E316", {"start": v(408, -4108.95) * mm, "end": v(419.83, -4110.51) * mm});
            skLineSegment(sketch, "E317", {"start": v(419.83, -4110.51) * mm, "end": v(431.66, -4108.95) * mm});
            skLineSegment(sketch, "E318", {"start": v(431.66, -4108.95) * mm, "end": v(442.68, -4104.39) * mm});
            skLineSegment(sketch, "E319", {"start": v(442.68, -4104.39) * mm, "end": v(452.14, -4097.12) * mm});
            skLineSegment(sketch, "E320", {"start": v(452.14, -4097.12) * mm, "end": v(459.4, -4087.66) * mm});
            skLineSegment(sketch, "E321", {"start": v(459.4, -4087.66) * mm, "end": v(463.97, -4076.64) * mm});
            skLineSegment(sketch, "E322", {"start": v(463.97, -4076.64) * mm, "end": v(465.53, -4064.8) * mm});
            skLineSegment(sketch, "E323", {"start": v(-7620.94, -3639.12) * mm, "end": v(-7632.77, -3637.56) * mm});
            skLineSegment(sketch, "E324", {"start": v(-7632.77, -3637.56) * mm, "end": v(-7644.6, -3639.12) * mm});
            skLineSegment(sketch, "E325", {"start": v(-7644.6, -3639.12) * mm, "end": v(-7655.63, -3643.7) * mm});
            skLineSegment(sketch, "E326", {"start": v(-7655.63, -3643.7) * mm, "end": v(-7665.1, -3650.96) * mm});
            skLineSegment(sketch, "E327", {"start": v(-7665.1, -3650.96) * mm, "end": v(-7672.36, -3660.43) * mm});
            skLineSegment(sketch, "E328", {"start": v(-7672.36, -3660.43) * mm, "end": v(-7676.93, -3671.46) * mm});
            skLineSegment(sketch, "E329", {"start": v(-7600.43, -3715.6) * mm, "end": v(-7593.16, -3706.14) * mm});
            skLineSegment(sketch, "E330", {"start": v(-7593.16, -3706.14) * mm, "end": v(-7588.6, -3695.1) * mm});
            skLineSegment(sketch, "E331", {"start": v(-7588.6, -3695.1) * mm, "end": v(-7587.04, -3683.28) * mm});
            skLineSegment(sketch, "E332", {"start": v(-7676.93, -3671.46) * mm, "end": v(-7678.48, -3683.29) * mm});
            skLineSegment(sketch, "E333", {"start": v(-7678.48, -3683.29) * mm, "end": v(-7676.92, -3695.12) * mm});
            skLineSegment(sketch, "E334", {"start": v(-7676.92, -3695.12) * mm, "end": v(-7672.35, -3706.15) * mm});
            skLineSegment(sketch, "E335", {"start": v(-7588.6, -3671.44) * mm, "end": v(-7593.17, -3660.42) * mm});
            skLineSegment(sketch, "E336", {"start": v(-7587.04, -3683.28) * mm, "end": v(-7588.6, -3671.44) * mm});
            skLineSegment(sketch, "E337", {"start": v(-7672.35, -3706.15) * mm, "end": v(-7665.09, -3715.62) * mm});
            skLineSegment(sketch, "E338", {"start": v(-7665.09, -3715.62) * mm, "end": v(-7655.62, -3722.88) * mm});
            skLineSegment(sketch, "E339", {"start": v(-7655.62, -3722.88) * mm, "end": v(-7644.59, -3727.45) * mm});
            skLineSegment(sketch, "E340", {"start": v(-7644.59, -3727.45) * mm, "end": v(-7632.76, -3729) * mm});
            skLineSegment(sketch, "E341", {"start": v(-7632.76, -3729) * mm, "end": v(-7620.92, -3727.44) * mm});
            skLineSegment(sketch, "E342", {"start": v(-7620.92, -3727.44) * mm, "end": v(-7609.9, -3722.87) * mm});
            skLineSegment(sketch, "E343", {"start": v(-7609.9, -3722.87) * mm, "end": v(-7600.43, -3715.6) * mm});
            skLineSegment(sketch, "E344", {"start": v(-7609.9, -3643.69) * mm, "end": v(-7620.94, -3639.12) * mm});
            skLineSegment(sketch, "E345", {"start": v(-7600.44, -3650.95) * mm, "end": v(-7609.9, -3643.69) * mm});
            skLineSegment(sketch, "E346", {"start": v(-7593.17, -3660.42) * mm, "end": v(-7600.44, -3650.95) * mm});
            skLineSegment(sketch, "E347", {"start": v(-7136.25, -3639.12) * mm, "end": v(-7147.28, -3643.7) * mm});
            skLineSegment(sketch, "E348", {"start": v(-7147.28, -3643.7) * mm, "end": v(-7156.74, -3650.96) * mm});
            skLineSegment(sketch, "E349", {"start": v(-7156.74, -3650.96) * mm, "end": v(-7164, -3660.43) * mm});
            skLineSegment(sketch, "E350", {"start": v(-7078.7, -3683.28) * mm, "end": v(-7080.25, -3671.44) * mm});
            skLineSegment(sketch, "E351", {"start": v(-7080.25, -3671.44) * mm, "end": v(-7084.82, -3660.42) * mm});
            skLineSegment(sketch, "E352", {"start": v(-7084.82, -3660.42) * mm, "end": v(-7092.09, -3650.95) * mm});
            skLineSegment(sketch, "E353", {"start": v(-7112.58, -3639.12) * mm, "end": v(-7124.42, -3637.56) * mm});
            skLineSegment(sketch, "E354", {"start": v(-7124.42, -3637.56) * mm, "end": v(-7136.25, -3639.12) * mm});
            skLineSegment(sketch, "E355", {"start": v(-7156.74, -3715.62) * mm, "end": v(-7147.27, -3722.88) * mm});
            skLineSegment(sketch, "E356", {"start": v(-7147.27, -3722.88) * mm, "end": v(-7136.24, -3727.45) * mm});
            skLineSegment(sketch, "E357", {"start": v(-7136.24, -3727.45) * mm, "end": v(-7124.4, -3729) * mm});
            skLineSegment(sketch, "E358", {"start": v(-7124.4, -3729) * mm, "end": v(-7112.57, -3727.44) * mm});
            skLineSegment(sketch, "E359", {"start": v(-7112.57, -3727.44) * mm, "end": v(-7101.55, -3722.87) * mm});
            skLineSegment(sketch, "E360", {"start": v(-7101.55, -3722.87) * mm, "end": v(-7092.08, -3715.6) * mm});
            skLineSegment(sketch, "E361", {"start": v(-7092.09, -3650.95) * mm, "end": v(-7101.56, -3643.69) * mm});
            skLineSegment(sketch, "E362", {"start": v(-7101.56, -3643.69) * mm, "end": v(-7112.58, -3639.12) * mm});
            skLineSegment(sketch, "E363", {"start": v(-7164, -3660.43) * mm, "end": v(-7168.57, -3671.46) * mm});
            skLineSegment(sketch, "E364", {"start": v(-7168.57, -3671.46) * mm, "end": v(-7170.13, -3683.29) * mm});
            skLineSegment(sketch, "E365", {"start": v(-7170.13, -3683.29) * mm, "end": v(-7168.57, -3695.12) * mm});
            skLineSegment(sketch, "E366", {"start": v(-7168.57, -3695.12) * mm, "end": v(-7164, -3706.15) * mm});
            skLineSegment(sketch, "E367", {"start": v(-7164, -3706.15) * mm, "end": v(-7156.74, -3715.62) * mm});
            skLineSegment(sketch, "E368", {"start": v(-7092.08, -3715.6) * mm, "end": v(-7084.81, -3706.14) * mm});
            skLineSegment(sketch, "E369", {"start": v(-7084.81, -3706.14) * mm, "end": v(-7080.25, -3695.1) * mm});
            skLineSegment(sketch, "E370", {"start": v(-7080.25, -3695.1) * mm, "end": v(-7078.7, -3683.28) * mm});
            skLineSegment(sketch, "E371", {"start": v(-7339, -4168.77) * mm, "end": v(-7346.26, -4159.3) * mm});
            skLineSegment(sketch, "E372", {"start": v(-7334.43, -4179.8) * mm, "end": v(-7339, -4168.77) * mm});
            skLineSegment(sketch, "E373", {"start": v(-7332.87, -4191.63) * mm, "end": v(-7334.43, -4179.8) * mm});
            skLineSegment(sketch, "E374", {"start": v(-7346.26, -4159.3) * mm, "end": v(-7355.73, -4152.04) * mm});
            skLineSegment(sketch, "E375", {"start": v(-7418.18, -4168.78) * mm, "end": v(-7422.75, -4179.8) * mm});
            skLineSegment(sketch, "E376", {"start": v(-7422.75, -4179.8) * mm, "end": v(-7424.3, -4191.64) * mm});
            skLineSegment(sketch, "E377", {"start": v(-7424.3, -4191.64) * mm, "end": v(-7422.75, -4203.47) * mm});
            skLineSegment(sketch, "E378", {"start": v(-7422.75, -4203.47) * mm, "end": v(-7418.18, -4214.5) * mm});
            skLineSegment(sketch, "E379", {"start": v(-7418.18, -4214.5) * mm, "end": v(-7410.91, -4223.97) * mm});
            skLineSegment(sketch, "E380", {"start": v(-7410.91, -4223.97) * mm, "end": v(-7401.44, -4231.23) * mm});
            skLineSegment(sketch, "E381", {"start": v(-7401.44, -4231.23) * mm, "end": v(-7390.41, -4235.8) * mm});
            skLineSegment(sketch, "E382", {"start": v(-7390.41, -4235.8) * mm, "end": v(-7378.58, -4237.35) * mm});
            skLineSegment(sketch, "E383", {"start": v(-7378.58, -4237.35) * mm, "end": v(-7366.75, -4235.8) * mm});
            skLineSegment(sketch, "E384", {"start": v(-7366.75, -4235.8) * mm, "end": v(-7355.72, -4231.23) * mm});
            skLineSegment(sketch, "E385", {"start": v(-7355.72, -4231.23) * mm, "end": v(-7346.25, -4223.96) * mm});
            skLineSegment(sketch, "E386", {"start": v(-7346.25, -4223.96) * mm, "end": v(-7338.99, -4214.49) * mm});
            skLineSegment(sketch, "E387", {"start": v(-7338.99, -4214.49) * mm, "end": v(-7334.42, -4203.46) * mm});
            skLineSegment(sketch, "E388", {"start": v(-7334.42, -4203.46) * mm, "end": v(-7332.87, -4191.63) * mm});
            skLineSegment(sketch, "E389", {"start": v(-7355.73, -4152.04) * mm, "end": v(-7366.76, -4147.47) * mm});
            skLineSegment(sketch, "E390", {"start": v(-7366.76, -4147.47) * mm, "end": v(-7378.6, -4145.91) * mm});
            skLineSegment(sketch, "E391", {"start": v(-7378.6, -4145.91) * mm, "end": v(-7390.43, -4147.47) * mm});
            skLineSegment(sketch, "E392", {"start": v(-7390.43, -4147.47) * mm, "end": v(-7401.45, -4152.04) * mm});
            skLineSegment(sketch, "E393", {"start": v(-7401.45, -4152.04) * mm, "end": v(-7410.92, -4159.31) * mm});
            skLineSegment(sketch, "E394", {"start": v(-7410.92, -4159.31) * mm, "end": v(-7418.18, -4168.78) * mm});
            skLineSegment(sketch, "E395", {"start": v(-6826.52, -4096.88) * mm, "end": v(-6817.05, -4104.14) * mm});
            skLineSegment(sketch, "E396", {"start": v(-6817.05, -4104.14) * mm, "end": v(-6806.03, -4108.71) * mm});
            skLineSegment(sketch, "E397", {"start": v(-6806.03, -4108.71) * mm, "end": v(-6794.2, -4110.27) * mm});
            skLineSegment(sketch, "E398", {"start": v(-6794.2, -4110.27) * mm, "end": v(-6782.36, -4108.7) * mm});
            skLineSegment(sketch, "E399", {"start": v(-6782.36, -4108.7) * mm, "end": v(-6771.33, -4104.14) * mm});
            skLineSegment(sketch, "E400", {"start": v(-6750.04, -4052.7) * mm, "end": v(-6754.6, -4041.68) * mm});
            skLineSegment(sketch, "E401", {"start": v(-6771.35, -4024.95) * mm, "end": v(-6782.37, -4020.38) * mm});
            skLineSegment(sketch, "E402", {"start": v(-6782.37, -4020.38) * mm, "end": v(-6794.2, -4018.83) * mm});
            skLineSegment(sketch, "E403", {"start": v(-6794.2, -4018.83) * mm, "end": v(-6806.04, -4020.39) * mm});
            skLineSegment(sketch, "E404", {"start": v(-6806.04, -4020.39) * mm, "end": v(-6817.07, -4024.96) * mm});
            skLineSegment(sketch, "E405", {"start": v(-6817.07, -4024.96) * mm, "end": v(-6826.53, -4032.22) * mm});
            skLineSegment(sketch, "E406", {"start": v(-6748.48, -4064.54) * mm, "end": v(-6750.04, -4052.7) * mm});
            skLineSegment(sketch, "E407", {"start": v(-6771.33, -4104.14) * mm, "end": v(-6761.87, -4096.87) * mm});
            skLineSegment(sketch, "E408", {"start": v(-6761.87, -4096.87) * mm, "end": v(-6754.6, -4087.4) * mm});
            skLineSegment(sketch, "E409", {"start": v(-6754.6, -4087.4) * mm, "end": v(-6750.04, -4076.37) * mm});
            skLineSegment(sketch, "E410", {"start": v(-6750.04, -4076.37) * mm, "end": v(-6748.48, -4064.54) * mm});
            skLineSegment(sketch, "E411", {"start": v(-6826.53, -4032.22) * mm, "end": v(-6833.8, -4041.7) * mm});
            skLineSegment(sketch, "E412", {"start": v(-6833.8, -4041.7) * mm, "end": v(-6838.36, -4052.72) * mm});
            skLineSegment(sketch, "E413", {"start": v(-6838.36, -4052.72) * mm, "end": v(-6839.92, -4064.55) * mm});
            skLineSegment(sketch, "E414", {"start": v(-6839.92, -4064.55) * mm, "end": v(-6838.36, -4076.39) * mm});
            skLineSegment(sketch, "E415", {"start": v(-6838.36, -4076.39) * mm, "end": v(-6833.8, -4087.41) * mm});
            skLineSegment(sketch, "E416", {"start": v(-6833.8, -4087.41) * mm, "end": v(-6826.52, -4096.88) * mm});
            skLineSegment(sketch, "E417", {"start": v(-6754.6, -4041.68) * mm, "end": v(-6761.88, -4032.21) * mm});
            skLineSegment(sketch, "E418", {"start": v(-6761.88, -4032.21) * mm, "end": v(-6771.35, -4024.95) * mm});
            skLineSegment(sketch, "E419", {"start": v(-6804.96, -45.05) * mm, "end": v(-6793.13, -46.6) * mm});
            skLineSegment(sketch, "E420", {"start": v(-6793.13, -46.6) * mm, "end": v(-6781.3, -45.05) * mm});
            skLineSegment(sketch, "E421", {"start": v(-6781.3, -45.05) * mm, "end": v(-6770.27, -40.48) * mm});
            skLineSegment(sketch, "E422", {"start": v(-6793.14, 44.83) * mm, "end": v(-6804.97, 43.27) * mm});
            skLineSegment(sketch, "E423", {"start": v(-6804.97, 43.27) * mm, "end": v(-6816, 38.7) * mm});
            skLineSegment(sketch, "E424", {"start": v(-6816, 38.7) * mm, "end": v(-6825.47, 31.44) * mm});
            skLineSegment(sketch, "E425", {"start": v(-6748.97, 10.95) * mm, "end": v(-6753.54, 21.98) * mm});
            skLineSegment(sketch, "E426", {"start": v(-6832.73, 21.97) * mm, "end": v(-6837.3, 10.94) * mm});
            skLineSegment(sketch, "E427", {"start": v(-6837.3, 10.94) * mm, "end": v(-6838.85, -0.9) * mm});
            skLineSegment(sketch, "E428", {"start": v(-6770.27, -40.48) * mm, "end": v(-6760.8, -33.21) * mm});
            skLineSegment(sketch, "E429", {"start": v(-6760.8, -33.21) * mm, "end": v(-6753.53, -23.74) * mm});
            skLineSegment(sketch, "E430", {"start": v(-6837.3, -12.73) * mm, "end": v(-6832.72, -23.75) * mm});
            skLineSegment(sketch, "E431", {"start": v(-6832.72, -23.75) * mm, "end": v(-6825.46, -33.22) * mm});
            skLineSegment(sketch, "E432", {"start": v(-6838.85, -0.9) * mm, "end": v(-6837.3, -12.73) * mm});
            skLineSegment(sketch, "E433", {"start": v(-6770.28, 38.7) * mm, "end": v(-6781.3, 43.28) * mm});
            skLineSegment(sketch, "E434", {"start": v(-6825.47, 31.44) * mm, "end": v(-6832.73, 21.97) * mm});
            skLineSegment(sketch, "E435", {"start": v(-6760.8, 31.45) * mm, "end": v(-6770.28, 38.7) * mm});
            skLineSegment(sketch, "E436", {"start": v(-6753.54, 21.98) * mm, "end": v(-6760.8, 31.45) * mm});
            skLineSegment(sketch, "E437", {"start": v(-6781.3, 43.28) * mm, "end": v(-6793.14, 44.83) * mm});
            skLineSegment(sketch, "E438", {"start": v(-6747.41, -0.88) * mm, "end": v(-6748.97, 10.95) * mm});
            skLineSegment(sketch, "E439", {"start": v(-6825.46, -33.22) * mm, "end": v(-6815.99, -40.49) * mm});
            skLineSegment(sketch, "E440", {"start": v(-6815.99, -40.49) * mm, "end": v(-6804.96, -45.05) * mm});
            skLineSegment(sketch, "E441", {"start": v(-6753.53, -23.74) * mm, "end": v(-6748.97, -12.72) * mm});
            skLineSegment(sketch, "E442", {"start": v(-6748.97, -12.72) * mm, "end": v(-6747.41, -0.88) * mm});
            skLineSegment(sketch, "E443", {"start": v(-7631.85, 4398.81) * mm, "end": v(-7620.02, 4400.37) * mm});
            skLineSegment(sketch, "E444", {"start": v(-7620.02, 4400.37) * mm, "end": v(-7609, 4404.94) * mm});
            skLineSegment(sketch, "E445", {"start": v(-7609, 4404.94) * mm, "end": v(-7599.53, 4412.2) * mm});
            skLineSegment(sketch, "E446", {"start": v(-7599.53, 4412.2) * mm, "end": v(-7592.26, 4421.68) * mm});
            skLineSegment(sketch, "E447", {"start": v(-7676.02, 4456.36) * mm, "end": v(-7677.58, 4444.53) * mm});
            skLineSegment(sketch, "E448", {"start": v(-7677.58, 4444.53) * mm, "end": v(-7676.02, 4432.7) * mm});
            skLineSegment(sketch, "E449", {"start": v(-7654.73, 4484.12) * mm, "end": v(-7664.2, 4476.86) * mm});
            skLineSegment(sketch, "E450", {"start": v(-7620.03, 4488.7) * mm, "end": v(-7631.87, 4490.25) * mm});
            skLineSegment(sketch, "E451", {"start": v(-7609, 4484.13) * mm, "end": v(-7620.03, 4488.7) * mm});
            skLineSegment(sketch, "E452", {"start": v(-7592.26, 4421.68) * mm, "end": v(-7587.7, 4432.7) * mm});
            skLineSegment(sketch, "E453", {"start": v(-7587.7, 4432.7) * mm, "end": v(-7586.14, 4444.54) * mm});
            skLineSegment(sketch, "E454", {"start": v(-7676.02, 4432.7) * mm, "end": v(-7671.45, 4421.67) * mm});
            skLineSegment(sketch, "E455", {"start": v(-7671.45, 4421.67) * mm, "end": v(-7664.18, 4412.2) * mm});
            skLineSegment(sketch, "E456", {"start": v(-7631.87, 4490.25) * mm, "end": v(-7643.7, 4488.7) * mm});
            skLineSegment(sketch, "E457", {"start": v(-7643.7, 4488.7) * mm, "end": v(-7654.73, 4484.12) * mm});
            skLineSegment(sketch, "E458", {"start": v(-7664.2, 4476.86) * mm, "end": v(-7671.46, 4467.39) * mm});
            skLineSegment(sketch, "E459", {"start": v(-7671.46, 4467.39) * mm, "end": v(-7676.02, 4456.36) * mm});
            skLineSegment(sketch, "E460", {"start": v(-7599.54, 4476.87) * mm, "end": v(-7609, 4484.13) * mm});
            skLineSegment(sketch, "E461", {"start": v(-7592.27, 4467.4) * mm, "end": v(-7599.54, 4476.87) * mm});
            skLineSegment(sketch, "E462", {"start": v(-7587.7, 4456.37) * mm, "end": v(-7592.27, 4467.4) * mm});
            skLineSegment(sketch, "E463", {"start": v(-7586.14, 4444.54) * mm, "end": v(-7587.7, 4456.37) * mm});
            skLineSegment(sketch, "E464", {"start": v(-7664.18, 4412.2) * mm, "end": v(-7654.71, 4404.94) * mm});
            skLineSegment(sketch, "E465", {"start": v(-7654.71, 4404.94) * mm, "end": v(-7643.69, 4400.37) * mm});
            skLineSegment(sketch, "E466", {"start": v(-7643.69, 4400.37) * mm, "end": v(-7631.85, 4398.81) * mm});
            skLineSegment(sketch, "E467", {"start": v(-7155.72, 4476.86) * mm, "end": v(-7162.99, 4467.39) * mm});
            skLineSegment(sketch, "E468", {"start": v(-7162.99, 4467.39) * mm, "end": v(-7167.55, 4456.36) * mm});
            skLineSegment(sketch, "E469", {"start": v(-7167.55, 4456.36) * mm, "end": v(-7169.11, 4444.53) * mm});
            skLineSegment(sketch, "E470", {"start": v(-7169.11, 4444.53) * mm, "end": v(-7167.55, 4432.7) * mm});
            skLineSegment(sketch, "E471", {"start": v(-7167.55, 4432.7) * mm, "end": v(-7162.98, 4421.67) * mm});
            skLineSegment(sketch, "E472", {"start": v(-7111.56, 4488.7) * mm, "end": v(-7123.4, 4490.25) * mm});
            skLineSegment(sketch, "E473", {"start": v(-7100.53, 4404.94) * mm, "end": v(-7091.06, 4412.2) * mm});
            skLineSegment(sketch, "E474", {"start": v(-7091.06, 4412.2) * mm, "end": v(-7083.8, 4421.68) * mm});
            skLineSegment(sketch, "E475", {"start": v(-7083.8, 4421.68) * mm, "end": v(-7079.23, 4432.7) * mm});
            skLineSegment(sketch, "E476", {"start": v(-7079.23, 4432.7) * mm, "end": v(-7077.67, 4444.54) * mm});
            skLineSegment(sketch, "E477", {"start": v(-7100.54, 4484.13) * mm, "end": v(-7111.56, 4488.7) * mm});
            skLineSegment(sketch, "E478", {"start": v(-7123.4, 4490.25) * mm, "end": v(-7135.23, 4488.7) * mm});
            skLineSegment(sketch, "E479", {"start": v(-7077.67, 4444.54) * mm, "end": v(-7079.23, 4456.37) * mm});
            skLineSegment(sketch, "E480", {"start": v(-7079.23, 4456.37) * mm, "end": v(-7083.8, 4467.4) * mm});
            skLineSegment(sketch, "E481", {"start": v(-7083.8, 4467.4) * mm, "end": v(-7091.07, 4476.87) * mm});
            skLineSegment(sketch, "E482", {"start": v(-7091.07, 4476.87) * mm, "end": v(-7100.54, 4484.13) * mm});
            skLineSegment(sketch, "E483", {"start": v(-7162.98, 4421.67) * mm, "end": v(-7155.72, 4412.2) * mm});
            skLineSegment(sketch, "E484", {"start": v(-7155.72, 4412.2) * mm, "end": v(-7146.25, 4404.94) * mm});
            skLineSegment(sketch, "E485", {"start": v(-7146.25, 4404.94) * mm, "end": v(-7135.22, 4400.37) * mm});
            skLineSegment(sketch, "E486", {"start": v(-7135.22, 4400.37) * mm, "end": v(-7123.38, 4398.81) * mm});
            skLineSegment(sketch, "E487", {"start": v(-7123.38, 4398.81) * mm, "end": v(-7111.55, 4400.37) * mm});
            skLineSegment(sketch, "E488", {"start": v(-7111.55, 4400.37) * mm, "end": v(-7100.53, 4404.94) * mm});
            skLineSegment(sketch, "E489", {"start": v(-7135.23, 4488.7) * mm, "end": v(-7146.26, 4484.12) * mm});
            skLineSegment(sketch, "E490", {"start": v(-7146.26, 4484.12) * mm, "end": v(-7155.72, 4476.86) * mm});
            skLineSegment(sketch, "E491", {"start": v(-6760.8, 3968.4) * mm, "end": v(-6770.28, 3975.66) * mm});
            skLineSegment(sketch, "E492", {"start": v(-6832.72, 3913.2) * mm, "end": v(-6825.46, 3903.73) * mm});
            skLineSegment(sketch, "E493", {"start": v(-6825.46, 3903.73) * mm, "end": v(-6815.99, 3896.47) * mm});
            skLineSegment(sketch, "E494", {"start": v(-6815.99, 3896.47) * mm, "end": v(-6804.96, 3891.9) * mm});
            skLineSegment(sketch, "E495", {"start": v(-6804.96, 3891.9) * mm, "end": v(-6793.13, 3890.34) * mm});
            skLineSegment(sketch, "E496", {"start": v(-6793.13, 3890.34) * mm, "end": v(-6781.3, 3891.9) * mm});
            skLineSegment(sketch, "E497", {"start": v(-6781.3, 3980.23) * mm, "end": v(-6793.14, 3981.78) * mm});
            skLineSegment(sketch, "E498", {"start": v(-6793.14, 3981.78) * mm, "end": v(-6804.97, 3980.23) * mm});
            skLineSegment(sketch, "E499", {"start": v(-6804.97, 3980.23) * mm, "end": v(-6816, 3975.66) * mm});
            skLineSegment(sketch, "E500", {"start": v(-6816, 3975.66) * mm, "end": v(-6825.47, 3968.39) * mm});
            skLineSegment(sketch, "E501", {"start": v(-6825.47, 3968.39) * mm, "end": v(-6832.73, 3958.92) * mm});
            skLineSegment(sketch, "E502", {"start": v(-6832.73, 3958.92) * mm, "end": v(-6837.3, 3947.9) * mm});
            skLineSegment(sketch, "E503", {"start": v(-6837.3, 3947.9) * mm, "end": v(-6838.85, 3936.06) * mm});
            skLineSegment(sketch, "E504", {"start": v(-6838.85, 3936.06) * mm, "end": v(-6837.3, 3924.23) * mm});
            skLineSegment(sketch, "E505", {"start": v(-6837.3, 3924.23) * mm, "end": v(-6832.72, 3913.2) * mm});
            skLineSegment(sketch, "E506", {"start": v(-6753.54, 3958.93) * mm, "end": v(-6760.8, 3968.4) * mm});
            skLineSegment(sketch, "E507", {"start": v(-6748.97, 3947.9) * mm, "end": v(-6753.54, 3958.93) * mm});
            skLineSegment(sketch, "E508", {"start": v(-6747.41, 3936.07) * mm, "end": v(-6748.97, 3947.9) * mm});
            skLineSegment(sketch, "E509", {"start": v(-6781.3, 3891.9) * mm, "end": v(-6770.27, 3896.47) * mm});
            skLineSegment(sketch, "E510", {"start": v(-6770.27, 3896.47) * mm, "end": v(-6760.8, 3903.74) * mm});
            skLineSegment(sketch, "E511", {"start": v(-6760.8, 3903.74) * mm, "end": v(-6753.53, 3913.21) * mm});
            skLineSegment(sketch, "E512", {"start": v(-6753.53, 3913.21) * mm, "end": v(-6748.97, 3924.24) * mm});
            skLineSegment(sketch, "E513", {"start": v(-6748.97, 3924.24) * mm, "end": v(-6747.41, 3936.07) * mm});
            skLineSegment(sketch, "E514", {"start": v(-6770.28, 3975.66) * mm, "end": v(-6781.3, 3980.23) * mm});
            skLineSegment(sketch, "E515", {"start": v(-3545.97, 267.55) * mm, "end": v(-3557, 272.12) * mm});
            skLineSegment(sketch, "E516", {"start": v(-3557, 272.12) * mm, "end": v(-3568.83, 273.67) * mm});
            skLineSegment(sketch, "E517", {"start": v(-3612.98, 216.11) * mm, "end": v(-3608.41, 205.09) * mm});
            skLineSegment(sketch, "E518", {"start": v(-3601.14, 195.62) * mm, "end": v(-3591.67, 188.36) * mm});
            skLineSegment(sketch, "E519", {"start": v(-3523.1, 227.96) * mm, "end": v(-3524.66, 239.8) * mm});
            skLineSegment(sketch, "E520", {"start": v(-3568.83, 273.67) * mm, "end": v(-3569.76, 273.55) * mm});
            skLineSegment(sketch, "E521", {"start": v(-3580.66, 272.11) * mm, "end": v(-3591.69, 267.55) * mm});
            skLineSegment(sketch, "E522", {"start": v(-3601.15, 260.28) * mm, "end": v(-3608.42, 250.8) * mm});
            skLineSegment(sketch, "E523", {"start": v(-3608.42, 250.8) * mm, "end": v(-3612.98, 239.78) * mm});
            skLineSegment(sketch, "E524", {"start": v(-3536.5, 260.29) * mm, "end": v(-3545.97, 267.55) * mm});
            skLineSegment(sketch, "E525", {"start": v(-3524.66, 239.8) * mm, "end": v(-3529.23, 250.82) * mm});
            skLineSegment(sketch, "E526", {"start": v(-3591.67, 188.36) * mm, "end": v(-3580.65, 183.8) * mm});
            skLineSegment(sketch, "E527", {"start": v(-3568.81, 182.23) * mm, "end": v(-3556.98, 183.8) * mm});
            skLineSegment(sketch, "E528", {"start": v(-3556.98, 183.8) * mm, "end": v(-3545.95, 188.36) * mm});
            skLineSegment(sketch, "E529", {"start": v(-3545.95, 188.36) * mm, "end": v(-3536.49, 195.63) * mm});
            skLineSegment(sketch, "E530", {"start": v(-3524.66, 216.13) * mm, "end": v(-3523.1, 227.96) * mm});
            skLineSegment(sketch, "E531", {"start": v(7885.97, 3416.58) * mm, "end": v(7885.97, 3640.1) * mm});
            skLineSegment(sketch, "E532", {"start": v(7731.03, -3766.36) * mm, "end": v(7885.97, -3766.36) * mm});
            skLineSegment(sketch, "E533", {"start": v(7885.97, -3766.36) * mm, "end": v(7885.97, -3542.84) * mm});
            skLineSegment(sketch, "E534", {"start": v(7885.97, -3542.84) * mm, "end": v(7731.03, -3542.84) * mm});
            skLineSegment(sketch, "E535", {"start": v(7731.03, -3542.84) * mm, "end": v(7731.03, -522.78) * mm});
            skLineSegment(sketch, "E536", {"start": v(2241.73, 4496.6) * mm, "end": v(2257.87, 4517.65) * mm});
            skLineSegment(sketch, "E537", {"start": v(2630.95, 4472.1) * mm, "end": v(2634.41, 4445.8) * mm});
            skLineSegment(sketch, "E538", {"start": v(2620.8, 4496.6) * mm, "end": v(2630.95, 4472.1) * mm});
            skLineSegment(sketch, "E539", {"start": v(2128.12, 56.69) * mm, "end": v(1823.32, 56.69) * mm});
            skLineSegment(sketch, "E540", {"start": v(4326.48, 3966.73) * mm, "end": v(4337.65, 3993.69) * mm});
            skLineSegment(sketch, "E541", {"start": v(2329.71, 4344.2) * mm, "end": v(2303.42, 4347.67) * mm});
            skLineSegment(sketch, "E542", {"start": v(2534.5, 4547.4) * mm, "end": v(2559.1, 4543.95) * mm});
            skLineSegment(sketch, "E543", {"start": v(2329.71, 4547.4) * mm, "end": v(2534.5, 4547.4) * mm});
            skLineSegment(sketch, "E544", {"start": v(4355.41, 3858.78) * mm, "end": v(4337.65, 3881.93) * mm});
            skLineSegment(sketch, "E545", {"start": v(4322.68, 3937.8) * mm, "end": v(4326.48, 3966.73) * mm});
            skLineSegment(sketch, "E546", {"start": v(2128.12, -100.8) * mm, "end": v(2257.66, -100.8) * mm});
            skLineSegment(sketch, "E547", {"start": v(5704.44, 4699.8) * mm, "end": v(6212.44, 4699.8) * mm});
            skLineSegment(sketch, "E548", {"start": v(4337.65, 3993.69) * mm, "end": v(4355.41, 4016.83) * mm});
            skLineSegment(sketch, "E549", {"start": v(2257.66, 4120.83) * mm, "end": v(2257.66, 4166.55) * mm});
            skLineSegment(sketch, "E550", {"start": v(2128.12, 4120.83) * mm, "end": v(1823.32, 4120.83) * mm});
            skLineSegment(sketch, "E551", {"start": v(2128.12, 4166.55) * mm, "end": v(2128.12, 4120.83) * mm});
            skLineSegment(sketch, "E552", {"start": v(1823.32, 4009.07) * mm, "end": v(1823.32, 3766.36) * mm});
            skLineSegment(sketch, "E553", {"start": v(2128.12, -3836.75) * mm, "end": v(2128.12, -3882.47) * mm});
            skLineSegment(sketch, "E554", {"start": v(2128.12, -3994.23) * mm, "end": v(2128.12, -4039.95) * mm});
            skLineSegment(sketch, "E555", {"start": v(2359.26, -3994.23) * mm, "end": v(2359.26, -3882.47) * mm});
            skLineSegment(sketch, "E556", {"start": v(2257.66, -3994.23) * mm, "end": v(2359.26, -3994.23) * mm});
            skLineSegment(sketch, "E557", {"start": v(2257.66, -3994.23) * mm, "end": v(2257.66, -4039.95) * mm});
            skLineSegment(sketch, "E558", {"start": v(1823.32, -3994.23) * mm, "end": v(2128.12, -3994.23) * mm});
            skLineSegment(sketch, "E559", {"start": v(2359.26, -3882.47) * mm, "end": v(2257.66, -3882.47) * mm});
            skLineSegment(sketch, "E560", {"start": v(2128.12, -3882.47) * mm, "end": v(1823.32, -3882.47) * mm});
            skLineSegment(sketch, "E561", {"start": v(2257.66, -3836.75) * mm, "end": v(2128.12, -3836.75) * mm});
            skLineSegment(sketch, "E562", {"start": v(7731.03, -4649) * mm, "end": v(3900.71, -4649) * mm});
            skLineSegment(sketch, "E563", {"start": v(6949.7, -4373.97) * mm, "end": v(6970.74, -4357.82) * mm});
            skLineSegment(sketch, "E564", {"start": v(6933.55, -4395) * mm, "end": v(6949.7, -4373.97) * mm});
            skLineSegment(sketch, "E565", {"start": v(7224.64, -4344.2) * mm, "end": v(7021.54, -4344.2) * mm});
            skLineSegment(sketch, "E566", {"start": v(5175.8, -3841.02) * mm, "end": v(5198.94, -3858.78) * mm});
            skLineSegment(sketch, "E567", {"start": v(7195.1, -56.69) * mm, "end": v(7296.7, -56.69) * mm});
            skLineSegment(sketch, "E568", {"start": v(5148.84, -3829.86) * mm, "end": v(5175.8, -3841.02) * mm});
            skLineSegment(sketch, "E569", {"start": v(7296.7, -102.4) * mm, "end": v(7426.23, -102.4) * mm});
            skLineSegment(sketch, "E570", {"start": v(7275.44, -4357.82) * mm, "end": v(7296.48, -4373.97) * mm});
            skLineSegment(sketch, "E571", {"start": v(7731.03, -4009.07) * mm, "end": v(7426.23, -4009.07) * mm});
            skLineSegment(sketch, "E572", {"start": v(7426.23, -4009.07) * mm, "end": v(7426.23, -3963.35) * mm});
            skLineSegment(sketch, "E573", {"start": v(7195.1, -4120.83) * mm, "end": v(7296.7, -4120.83) * mm});
            skLineSegment(sketch, "E574", {"start": v(7296.7, -4166.55) * mm, "end": v(7426.23, -4166.55) * mm});
            skLineSegment(sketch, "E575", {"start": v(7426.23, -3963.35) * mm, "end": v(7296.7, -3963.35) * mm});
            skLineSegment(sketch, "E576", {"start": v(7296.7, -4120.83) * mm, "end": v(7296.7, -4166.55) * mm});
            skLineSegment(sketch, "E577", {"start": v(7426.23, -4120.83) * mm, "end": v(7731.03, -4120.83) * mm});
            skLineSegment(sketch, "E578", {"start": v(7426.23, -4166.55) * mm, "end": v(7426.23, -4120.83) * mm});
            skLineSegment(sketch, "E579", {"start": v(7731.03, -4009.07) * mm, "end": v(7731.03, -3766.36) * mm});
            skLineSegment(sketch, "E580", {"start": v(2630.95, 4419.51) * mm, "end": v(2620.8, 4395) * mm});
            skLineSegment(sketch, "E581", {"start": v(6949.7, -4517.65) * mm, "end": v(6933.55, -4496.6) * mm});
            skLineSegment(sketch, "E582", {"start": v(6970.74, -4533.8) * mm, "end": v(6949.7, -4517.65) * mm});
            skLineSegment(sketch, "E583", {"start": v(6995.24, -4543.95) * mm, "end": v(6970.74, -4533.8) * mm});
            skLineSegment(sketch, "E584", {"start": v(7731.03, 55.07) * mm, "end": v(7426.23, 55.07) * mm});
            skLineSegment(sketch, "E585", {"start": v(7275.44, -4533.8) * mm, "end": v(7250.93, -4543.95) * mm});
            skLineSegment(sketch, "E586", {"start": v(7250.93, -4543.95) * mm, "end": v(7224.64, -4547.4) * mm});
            skLineSegment(sketch, "E587", {"start": v(7322.77, -4472.1) * mm, "end": v(7312.62, -4496.6) * mm});
            skLineSegment(sketch, "E588", {"start": v(5175.8, -4034.6) * mm, "end": v(5148.84, -4045.76) * mm});
            skLineSegment(sketch, "E589", {"start": v(1823.32, -4460.52) * mm, "end": v(1823.32, -4698.2) * mm});
            skLineSegment(sketch, "E590", {"start": v(1668.38, -3640.1) * mm, "end": v(1823.32, -3640.1) * mm});
            skLineSegment(sketch, "E591", {"start": v(1823.32, -3416.58) * mm, "end": v(1668.38, -3416.58) * mm});
            skLineSegment(sketch, "E592", {"start": v(1668.38, -3416.58) * mm, "end": v(1668.38, -3640.1) * mm});
            skLineSegment(sketch, "E593", {"start": v(1823.32, 3766.36) * mm, "end": v(1668.38, 3766.36) * mm});
            skLineSegment(sketch, "E594", {"start": v(1668.38, 3766.36) * mm, "end": v(1668.38, 3542.84) * mm});
            skLineSegment(sketch, "E595", {"start": v(1668.38, 3542.84) * mm, "end": v(1823.32, 3542.84) * mm});
            skLineSegment(sketch, "E596", {"start": v(1823.32, 3542.84) * mm, "end": v(1823.32, 522.78) * mm});
            skLineSegment(sketch, "E597", {"start": v(2128.12, -55.07) * mm, "end": v(2128.12, -100.8) * mm});
            skLineSegment(sketch, "E598", {"start": v(6212.44, 4699.8) * mm, "end": v(6339.44, 4572.8) * mm});
            skLineSegment(sketch, "E599", {"start": v(5653.64, 4649) * mm, "end": v(5704.44, 4699.8) * mm});
            skLineSegment(sketch, "E600", {"start": v(2231.58, 4419.51) * mm, "end": v(2228.11, 4445.8) * mm});
            skLineSegment(sketch, "E601", {"start": v(7885.97, 521.16) * mm, "end": v(7731.03, 521.16) * mm});
            skLineSegment(sketch, "E602", {"start": v(7731.03, 521.16) * mm, "end": v(7731.03, 3416.58) * mm});
            skLineSegment(sketch, "E603", {"start": v(7885.97, -299.26) * mm, "end": v(7731.03, -299.26) * mm});
            skLineSegment(sketch, "E604", {"start": v(7731.03, -522.78) * mm, "end": v(7885.97, -522.78) * mm});
            skLineSegment(sketch, "E605", {"start": v(7885.97, -522.78) * mm, "end": v(7885.97, -299.26) * mm});
            skLineSegment(sketch, "E606", {"start": v(7731.03, 297.64) * mm, "end": v(7731.03, 55.07) * mm});
            skLineSegment(sketch, "E607", {"start": v(7731.03, -56.69) * mm, "end": v(7731.03, -299.26) * mm});
            skLineSegment(sketch, "E608", {"start": v(7731.03, 4237) * mm, "end": v(7885.97, 4237) * mm});
            skLineSegment(sketch, "E609", {"start": v(7885.97, 4237) * mm, "end": v(7885.97, 4460.52) * mm});
            skLineSegment(sketch, "E610", {"start": v(7885.97, 4460.52) * mm, "end": v(7731.03, 4460.52) * mm});
            skLineSegment(sketch, "E611", {"start": v(7731.03, 4460.52) * mm, "end": v(7731.03, 4698.2) * mm});
            skLineSegment(sketch, "E612", {"start": v(7885.97, 3640.1) * mm, "end": v(7731.03, 3640.1) * mm});
            skLineSegment(sketch, "E613", {"start": v(7731.03, 3416.58) * mm, "end": v(7885.97, 3416.58) * mm});
            skLineSegment(sketch, "E614", {"start": v(2359.26, -55.07) * mm, "end": v(2359.26, 56.69) * mm});
            skLineSegment(sketch, "E615", {"start": v(6339.44, 3506) * mm, "end": v(2468.48, -4698.2) * mm});
            skLineSegment(sketch, "E616", {"start": v(2257.66, -55.07) * mm, "end": v(2359.26, -55.07) * mm});
            skLineSegment(sketch, "E617", {"start": v(2257.66, -55.07) * mm, "end": v(2257.66, -100.8) * mm});
            skLineSegment(sketch, "E618", {"start": v(2559.1, 4347.67) * mm, "end": v(2532.81, 4344.2) * mm});
            skLineSegment(sketch, "E619", {"start": v(1823.32, -4698.2) * mm, "end": v(2468.48, -4698.2) * mm});
            skLineSegment(sketch, "E620", {"start": v(1823.32, 56.69) * mm, "end": v(1823.32, 299.26) * mm});
            skLineSegment(sketch, "E621", {"start": v(1823.32, -4237) * mm, "end": v(1668.38, -4237) * mm});
            skLineSegment(sketch, "E622", {"start": v(1668.38, -4237) * mm, "end": v(1668.38, -4460.52) * mm});
            skLineSegment(sketch, "E623", {"start": v(1668.38, -4460.52) * mm, "end": v(1823.32, -4460.52) * mm});
            skLineSegment(sketch, "E624", {"start": v(3214.91, -4572.8) * mm, "end": v(3214.91, -4176.57) * mm});
            skLineSegment(sketch, "E625", {"start": v(7312.62, -4395) * mm, "end": v(7322.77, -4419.51) * mm});
            skLineSegment(sketch, "E626", {"start": v(7326.24, -4445.8) * mm, "end": v(7322.77, -4472.1) * mm});
            skLineSegment(sketch, "E627", {"start": v(7250.93, -4347.67) * mm, "end": v(7275.44, -4357.82) * mm});
            skLineSegment(sketch, "E628", {"start": v(7426.23, -102.4) * mm, "end": v(7426.23, -56.69) * mm});
            skLineSegment(sketch, "E629", {"start": v(2128.12, -4039.95) * mm, "end": v(2257.66, -4039.95) * mm});
            skLineSegment(sketch, "E630", {"start": v(2257.66, -3882.47) * mm, "end": v(2257.66, -3836.75) * mm});
            skLineSegment(sketch, "E631", {"start": v(1823.32, -3994.23) * mm, "end": v(1823.32, -4237) * mm});
            skLineSegment(sketch, "E632", {"start": v(1823.32, -3882.47) * mm, "end": v(1823.32, -3640.1) * mm});
            skLineSegment(sketch, "E633", {"start": v(2359.26, 4009.07) * mm, "end": v(2359.26, 4120.83) * mm});
            skLineSegment(sketch, "E634", {"start": v(2257.66, 4009.07) * mm, "end": v(2359.26, 4009.07) * mm});
            skLineSegment(sketch, "E635", {"start": v(2257.66, 4009.07) * mm, "end": v(2257.66, 3963.35) * mm});
            skLineSegment(sketch, "E636", {"start": v(1823.32, 4009.07) * mm, "end": v(2128.12, 4009.07) * mm});
            skLineSegment(sketch, "E637", {"start": v(2128.12, 4009.07) * mm, "end": v(2128.12, 3963.35) * mm});
            skLineSegment(sketch, "E638", {"start": v(2359.26, 4120.83) * mm, "end": v(2257.66, 4120.83) * mm});
            skLineSegment(sketch, "E639", {"start": v(4434.44, 3826.05) * mm, "end": v(4405.51, 3829.86) * mm});
            skLineSegment(sketch, "E640", {"start": v(2604.65, 4517.65) * mm, "end": v(2620.8, 4496.6) * mm});
            skLineSegment(sketch, "E641", {"start": v(2583.61, 4533.8) * mm, "end": v(2604.65, 4517.65) * mm});
            skLineSegment(sketch, "E642", {"start": v(2559.1, 4543.95) * mm, "end": v(2583.61, 4533.8) * mm});
            skLineSegment(sketch, "E643", {"start": v(1823.32, -55.07) * mm, "end": v(2128.12, -55.07) * mm});
            skLineSegment(sketch, "E644", {"start": v(2278.91, 4533.8) * mm, "end": v(2303.42, 4543.95) * mm});
            skLineSegment(sketch, "E645", {"start": v(2303.42, 4543.95) * mm, "end": v(2329.71, 4547.4) * mm});
            skLineSegment(sketch, "E646", {"start": v(2231.58, 4472.1) * mm, "end": v(2241.73, 4496.6) * mm});
            skLineSegment(sketch, "E647", {"start": v(4378.56, 4034.6) * mm, "end": v(4405.51, 4045.76) * mm});
            skLineSegment(sketch, "E648", {"start": v(7195.1, 55.07) * mm, "end": v(7195.1, -56.69) * mm});
            skLineSegment(sketch, "E649", {"start": v(3214.91, -3506) * mm, "end": v(7085.87, 4698.2) * mm});
            skLineSegment(sketch, "E650", {"start": v(7296.7, 55.07) * mm, "end": v(7195.1, 55.07) * mm});
            skLineSegment(sketch, "E651", {"start": v(7296.7, 55.07) * mm, "end": v(7296.7, 100.8) * mm});
            skLineSegment(sketch, "E652", {"start": v(6995.24, -4347.67) * mm, "end": v(7021.54, -4344.2) * mm});
            skLineSegment(sketch, "E653", {"start": v(7731.03, 4698.2) * mm, "end": v(7085.87, 4698.2) * mm});
            skLineSegment(sketch, "E654", {"start": v(5119.91, -3826.05) * mm, "end": v(5148.84, -3829.86) * mm});
            skLineSegment(sketch, "E655", {"start": v(6933.55, -4496.6) * mm, "end": v(6923.4, -4472.1) * mm});
            skLineSegment(sketch, "E656", {"start": v(7426.23, -56.69) * mm, "end": v(7731.03, -56.69) * mm});
            skLineSegment(sketch, "E657", {"start": v(5227.86, -3966.73) * mm, "end": v(5216.7, -3993.69) * mm});
            skLineSegment(sketch, "E658", {"start": v(7224.64, -4344.2) * mm, "end": v(7250.93, -4347.67) * mm});
            skLineSegment(sketch, "E659", {"start": v(7019.84, -4547.4) * mm, "end": v(6995.24, -4543.95) * mm});
            skLineSegment(sketch, "E660", {"start": v(7224.64, -4547.4) * mm, "end": v(7019.84, -4547.4) * mm});
            skLineSegment(sketch, "E661", {"start": v(5198.94, -3858.78) * mm, "end": v(5216.7, -3881.93) * mm});
            skLineSegment(sketch, "E662", {"start": v(5231.67, -3937.8) * mm, "end": v(5227.86, -3966.73) * mm});
            skLineSegment(sketch, "E663", {"start": v(7426.23, 100.8) * mm, "end": v(7296.7, 100.8) * mm});
            skLineSegment(sketch, "E664", {"start": v(3849.91, -4699.8) * mm, "end": v(3341.91, -4699.8) * mm});
            skLineSegment(sketch, "E665", {"start": v(5216.7, -3993.69) * mm, "end": v(5198.94, -4016.83) * mm});
            skLineSegment(sketch, "E666", {"start": v(7296.7, -56.69) * mm, "end": v(7296.7, -102.4) * mm});
            skLineSegment(sketch, "E667", {"start": v(7195.1, 3994.23) * mm, "end": v(7195.1, 3882.47) * mm});
            skLineSegment(sketch, "E668", {"start": v(7296.7, 3994.23) * mm, "end": v(7195.1, 3994.23) * mm});
            skLineSegment(sketch, "E669", {"start": v(7296.7, 3994.23) * mm, "end": v(7296.7, 4039.95) * mm});
            skLineSegment(sketch, "E670", {"start": v(7731.03, 3994.23) * mm, "end": v(7426.23, 3994.23) * mm});
            skLineSegment(sketch, "E671", {"start": v(7195.1, 3882.47) * mm, "end": v(7296.7, 3882.47) * mm});
            skLineSegment(sketch, "E672", {"start": v(7426.23, 3882.47) * mm, "end": v(7731.03, 3882.47) * mm});
            skLineSegment(sketch, "E673", {"start": v(7296.7, 3836.75) * mm, "end": v(7426.23, 3836.75) * mm});
            skLineSegment(sketch, "E674", {"start": v(7426.23, 4039.95) * mm, "end": v(7296.7, 4039.95) * mm});
            skLineSegment(sketch, "E675", {"start": v(7296.7, 3882.47) * mm, "end": v(7296.7, 3836.75) * mm});
            skLineSegment(sketch, "E676", {"start": v(7731.03, 3994.23) * mm, "end": v(7731.03, 4237) * mm});
            skLineSegment(sketch, "E677", {"start": v(7731.03, 3882.47) * mm, "end": v(7731.03, 3640.1) * mm});
            skLineSegment(sketch, "E678", {"start": v(7195.1, -4009.07) * mm, "end": v(7195.1, -4120.83) * mm});
            skLineSegment(sketch, "E679", {"start": v(7296.7, -4009.07) * mm, "end": v(7195.1, -4009.07) * mm});
            skLineSegment(sketch, "E680", {"start": v(7296.7, -4009.07) * mm, "end": v(7296.7, -3963.35) * mm});
            skLineSegment(sketch, "E681", {"start": v(7426.23, 3836.75) * mm, "end": v(7426.23, 3882.47) * mm});
            skLineSegment(sketch, "E682", {"start": v(7426.23, 3994.23) * mm, "end": v(7426.23, 4039.95) * mm});
            skLineSegment(sketch, "E683", {"start": v(2257.66, 56.69) * mm, "end": v(2257.66, 102.4) * mm});
            skLineSegment(sketch, "E684", {"start": v(4355.41, 4016.83) * mm, "end": v(4378.56, 4034.6) * mm});
            skLineSegment(sketch, "E685", {"start": v(2634.41, 4445.8) * mm, "end": v(2630.95, 4419.51) * mm});
            skLineSegment(sketch, "E686", {"start": v(2583.61, 4357.82) * mm, "end": v(2559.1, 4347.67) * mm});
            skLineSegment(sketch, "E687", {"start": v(6212.44, 4049.57) * mm, "end": v(4434.44, 4049.57) * mm});
            skLineSegment(sketch, "E688", {"start": v(6212.44, 4049.57) * mm, "end": v(6339.44, 4176.57) * mm});
            skLineSegment(sketch, "E689", {"start": v(6212.44, 3826.05) * mm, "end": v(4434.44, 3826.05) * mm});
            skLineSegment(sketch, "E690", {"start": v(6339.44, 3699.05) * mm, "end": v(6339.44, 3506) * mm});
            skLineSegment(sketch, "E691", {"start": v(6212.44, 3826.05) * mm, "end": v(6339.44, 3699.05) * mm});
            skLineSegment(sketch, "E692", {"start": v(1823.32, -297.64) * mm, "end": v(1668.38, -297.64) * mm});
            skLineSegment(sketch, "E693", {"start": v(1668.38, -297.64) * mm, "end": v(1668.38, -521.16) * mm});
            skLineSegment(sketch, "E694", {"start": v(1668.38, -521.16) * mm, "end": v(1823.32, -521.16) * mm});
            skLineSegment(sketch, "E695", {"start": v(1823.32, -521.16) * mm, "end": v(1823.32, -3416.58) * mm});
            skLineSegment(sketch, "E696", {"start": v(1668.38, 299.26) * mm, "end": v(1823.32, 299.26) * mm});
            skLineSegment(sketch, "E697", {"start": v(1823.32, 522.78) * mm, "end": v(1668.38, 522.78) * mm});
            skLineSegment(sketch, "E698", {"start": v(1668.38, 522.78) * mm, "end": v(1668.38, 299.26) * mm});
            skLineSegment(sketch, "E699", {"start": v(1823.32, -297.64) * mm, "end": v(1823.32, -55.07) * mm});
            skLineSegment(sketch, "E700", {"start": v(2257.66, 4166.55) * mm, "end": v(2128.12, 4166.55) * mm});
            skLineSegment(sketch, "E701", {"start": v(2329.71, 4344.2) * mm, "end": v(2532.81, 4344.2) * mm});
            skLineSegment(sketch, "E702", {"start": v(4378.56, 3841.02) * mm, "end": v(4355.41, 3858.78) * mm});
            skLineSegment(sketch, "E703", {"start": v(2359.26, 56.69) * mm, "end": v(2257.66, 56.69) * mm});
            skLineSegment(sketch, "E704", {"start": v(4405.51, 3829.86) * mm, "end": v(4378.56, 3841.02) * mm});
            skLineSegment(sketch, "E705", {"start": v(2257.66, 102.4) * mm, "end": v(2128.12, 102.4) * mm});
            skLineSegment(sketch, "E706", {"start": v(2128.12, 3963.35) * mm, "end": v(2257.66, 3963.35) * mm});
            skLineSegment(sketch, "E707", {"start": v(2278.91, 4357.82) * mm, "end": v(2257.87, 4373.97) * mm});
            skLineSegment(sketch, "E708", {"start": v(2257.87, 4373.97) * mm, "end": v(2241.73, 4395) * mm});
            skLineSegment(sketch, "E709", {"start": v(2257.87, 4517.65) * mm, "end": v(2278.91, 4533.8) * mm});
            skLineSegment(sketch, "E710", {"start": v(4337.65, 3881.93) * mm, "end": v(4326.48, 3908.88) * mm});
            skLineSegment(sketch, "E711", {"start": v(4326.48, 3908.88) * mm, "end": v(4322.68, 3937.8) * mm});
            skLineSegment(sketch, "E712", {"start": v(1823.32, 4649) * mm, "end": v(1823.32, 4120.83) * mm});
            skLineSegment(sketch, "E713", {"start": v(4405.51, 4045.76) * mm, "end": v(4434.44, 4049.57) * mm});
            skLineSegment(sketch, "E714", {"start": v(6339.44, 4572.8) * mm, "end": v(6339.44, 4176.57) * mm});
            skLineSegment(sketch, "E715", {"start": v(2241.73, 4395) * mm, "end": v(2231.58, 4419.51) * mm});
            skLineSegment(sketch, "E716", {"start": v(2228.11, 4445.8) * mm, "end": v(2231.58, 4472.1) * mm});
            skLineSegment(sketch, "E717", {"start": v(2303.42, 4347.67) * mm, "end": v(2278.91, 4357.82) * mm});
            skLineSegment(sketch, "E718", {"start": v(2128.12, 102.4) * mm, "end": v(2128.12, 56.69) * mm});
            skLineSegment(sketch, "E719", {"start": v(5198.94, -4016.83) * mm, "end": v(5175.8, -4034.6) * mm});
            skLineSegment(sketch, "E720", {"start": v(6919.94, -4445.8) * mm, "end": v(6923.4, -4419.51) * mm});
            skLineSegment(sketch, "E721", {"start": v(6970.74, -4357.82) * mm, "end": v(6995.24, -4347.67) * mm});
            skLineSegment(sketch, "E722", {"start": v(3341.91, -4049.57) * mm, "end": v(5119.91, -4049.57) * mm});
            skLineSegment(sketch, "E723", {"start": v(3341.91, -4049.57) * mm, "end": v(3214.91, -4176.57) * mm});
            skLineSegment(sketch, "E724", {"start": v(3341.91, -3826.05) * mm, "end": v(5119.91, -3826.05) * mm});
            skLineSegment(sketch, "E725", {"start": v(3214.91, -3699.05) * mm, "end": v(3214.91, -3506) * mm});
            skLineSegment(sketch, "E726", {"start": v(3341.91, -3826.05) * mm, "end": v(3214.91, -3699.05) * mm});
            skLineSegment(sketch, "E727", {"start": v(7731.03, 297.64) * mm, "end": v(7885.97, 297.64) * mm});
            skLineSegment(sketch, "E728", {"start": v(7885.97, 297.64) * mm, "end": v(7885.97, 521.16) * mm});
            skLineSegment(sketch, "E729", {"start": v(7296.48, -4373.97) * mm, "end": v(7312.62, -4395) * mm});
            skLineSegment(sketch, "E730", {"start": v(7296.48, -4517.65) * mm, "end": v(7275.44, -4533.8) * mm});
            skLineSegment(sketch, "E731", {"start": v(5216.7, -3881.93) * mm, "end": v(5227.86, -3908.88) * mm});
            skLineSegment(sketch, "E732", {"start": v(5227.86, -3908.88) * mm, "end": v(5231.67, -3937.8) * mm});
            skLineSegment(sketch, "E733", {"start": v(6923.4, -4419.51) * mm, "end": v(6933.55, -4395) * mm});
            skLineSegment(sketch, "E734", {"start": v(7426.23, 55.07) * mm, "end": v(7426.23, 100.8) * mm});
            skLineSegment(sketch, "E735", {"start": v(3341.91, -4699.8) * mm, "end": v(3214.91, -4572.8) * mm});
            skLineSegment(sketch, "E736", {"start": v(3900.71, -4649) * mm, "end": v(3849.91, -4699.8) * mm});
            skLineSegment(sketch, "E737", {"start": v(7322.77, -4419.51) * mm, "end": v(7326.24, -4445.8) * mm});
            skLineSegment(sketch, "E738", {"start": v(7312.62, -4496.6) * mm, "end": v(7296.48, -4517.65) * mm});
            skLineSegment(sketch, "E739", {"start": v(6923.4, -4472.1) * mm, "end": v(6919.94, -4445.8) * mm});
            skLineSegment(sketch, "E740", {"start": v(7731.03, -4649) * mm, "end": v(7731.03, -4120.83) * mm});
            skLineSegment(sketch, "E741", {"start": v(5148.84, -4045.76) * mm, "end": v(5119.91, -4049.57) * mm});
            skLineSegment(sketch, "E742", {"start": v(1823.32, 4649) * mm, "end": v(5653.64, 4649) * mm});
            skLineSegment(sketch, "E743", {"start": v(2604.65, 4373.97) * mm, "end": v(2583.61, 4357.82) * mm});
            skLineSegment(sketch, "E744", {"start": v(2620.8, 4395) * mm, "end": v(2604.65, 4373.97) * mm});
            skLineSegment(sketch, "E745", {"start": v(4780.44, -669.66) * mm, "end": v(4778.89, -657.82) * mm});
            skLineSegment(sketch, "E746", {"start": v(7282.21, -3082.14) * mm, "end": v(7283.77, -3093.97) * mm});
            skLineSegment(sketch, "E747", {"start": v(7277.64, -3071.1) * mm, "end": v(7282.21, -3082.14) * mm});
            skLineSegment(sketch, "E748", {"start": v(7270.38, -3061.64) * mm, "end": v(7277.64, -3071.1) * mm});
            skLineSegment(sketch, "E749", {"start": v(4868.77, -669.67) * mm, "end": v(4864.2, -680.7) * mm});
            skLineSegment(sketch, "E750", {"start": v(4857.55, -3125.2) * mm, "end": v(4848.08, -3132.46) * mm});
            skLineSegment(sketch, "E751", {"start": v(4864.81, -3115.72) * mm, "end": v(4857.55, -3125.2) * mm});
            skLineSegment(sketch, "E752", {"start": v(4802.36, -3132.45) * mm, "end": v(4792.89, -3125.18) * mm});
            skLineSegment(sketch, "E753", {"start": v(4785.62, -3115.71) * mm, "end": v(4781.06, -3104.68) * mm});
            skLineSegment(sketch, "E754", {"start": v(4813.4, -3048.7) * mm, "end": v(4823.22, -3047.4) * mm});
            skLineSegment(sketch, "E755", {"start": v(7283.16, -656.68) * mm, "end": v(7281.6, -668.5) * mm});
            skLineSegment(sketch, "E756", {"start": v(7249.26, -700.83) * mm, "end": v(7237.43, -702.39) * mm});
            skLineSegment(sketch, "E757", {"start": v(4785.02, -634.96) * mm, "end": v(4792.28, -625.5) * mm});
            skLineSegment(sketch, "E758", {"start": v(4823.22, -703.37) * mm, "end": v(4812.77, -701.99) * mm});
            skLineSegment(sketch, "E759", {"start": v(7214.57, -696.26) * mm, "end": v(7205.1, -689) * mm});
            skLineSegment(sketch, "E760", {"start": v(7192.43, -3094.78) * mm, "end": v(7192.33, -3093.96) * mm});
            skLineSegment(sketch, "E761", {"start": v(4812.78, -613.66) * mm, "end": v(4824.61, -612.1) * mm});
            skLineSegment(sketch, "E762", {"start": v(7215.18, -3133.56) * mm, "end": v(7205.71, -3126.29) * mm});
            skLineSegment(sketch, "E763", {"start": v(5431.73, -946.66) * mm, "end": v(5443.56, -945.1) * mm});
            skLineSegment(sketch, "E764", {"start": v(5403.96, -967.96) * mm, "end": v(5411.23, -958.5) * mm});
            skLineSegment(sketch, "E765", {"start": v(4801.74, -697.42) * mm, "end": v(4792.27, -690.15) * mm});
            skLineSegment(sketch, "E766", {"start": v(5488.55, -2906.26) * mm, "end": v(5483.98, -2917.28) * mm});
            skLineSegment(sketch, "E767", {"start": v(5483.98, -2917.28) * mm, "end": v(5476.71, -2926.75) * mm});
            skLineSegment(sketch, "E768", {"start": v(4836.45, -613.67) * mm, "end": v(4847.47, -618.24) * mm});
            skLineSegment(sketch, "E769", {"start": v(7249.89, -3049.8) * mm, "end": v(7260.91, -3054.37) * mm});
            skLineSegment(sketch, "E770", {"start": v(7205.72, -3061.63) * mm, "end": v(7215.2, -3054.37) * mm});
            skLineSegment(sketch, "E771", {"start": v(7198.46, -3071.1) * mm, "end": v(7205.72, -3061.63) * mm});
            skLineSegment(sketch, "E772", {"start": v(7193.89, -3082.12) * mm, "end": v(7198.46, -3071.1) * mm});
            skLineSegment(sketch, "E773", {"start": v(4824.61, -612.1) * mm, "end": v(4836.45, -613.67) * mm});
            skLineSegment(sketch, "E774", {"start": v(5412.06, -2926.74) * mm, "end": v(5404.8, -2917.27) * mm});
            skLineSegment(sketch, "E775", {"start": v(5404.8, -2917.27) * mm, "end": v(5400.23, -2906.24) * mm});
            skLineSegment(sketch, "E776", {"start": v(6692.3, -870.39) * mm, "end": v(6681.26, -874.95) * mm});
            skLineSegment(sketch, "E777", {"start": v(6579.65, -2746.34) * mm, "end": v(6579.65, -2802.22) * mm});
            skLineSegment(sketch, "E778", {"start": v(6579.65, -2802.22) * mm, "end": v(6572.03, -2802.22) * mm});
            skLineSegment(sketch, "E779", {"start": v(6579.65, -2802.22) * mm, "end": v(6587.8, -2802.22) * mm});
            skLineSegment(sketch, "E780", {"start": v(4781.06, -3104.68) * mm, "end": v(4779.5, -3092.85) * mm});
            skLineSegment(sketch, "E781", {"start": v(4802.37, -3053.26) * mm, "end": v(4813.4, -3048.7) * mm});
            skLineSegment(sketch, "E782", {"start": v(6629.84, -853.64) * mm, "end": v(6625.27, -842.62) * mm});
            skLineSegment(sketch, "E783", {"start": v(6657.61, -786.63) * mm, "end": v(6669.44, -785.07) * mm});
            skLineSegment(sketch, "E784", {"start": v(6692.3, -791.2) * mm, "end": v(6696.07, -794.09) * mm});
            skLineSegment(sketch, "E785", {"start": v(6709.04, -807.93) * mm, "end": v(6713.6, -818.96) * mm});
            skLineSegment(sketch, "E786", {"start": v(7283.77, -3093.97) * mm, "end": v(7282.2, -3105.8) * mm});
            skLineSegment(sketch, "E787", {"start": v(4836.43, -702) * mm, "end": v(4824.6, -703.55) * mm});
            skLineSegment(sketch, "E788", {"start": v(4824.6, -703.55) * mm, "end": v(4823.22, -703.37) * mm});
            skLineSegment(sketch, "E789", {"start": v(4863.55, -808.02) * mm, "end": v(4892.76, -808.02) * mm});
            skLineSegment(sketch, "E790", {"start": v(4863.55, -808.02) * mm, "end": v(4863.55, -780.08) * mm});
            skLineSegment(sketch, "E791", {"start": v(6657.6, -874.95) * mm, "end": v(6648.44, -871.16) * mm});
            skLineSegment(sketch, "E792", {"start": v(5487.72, -979) * mm, "end": v(5489.27, -990.83) * mm});
            skLineSegment(sketch, "E793", {"start": v(5411.23, -958.5) * mm, "end": v(5420.7, -951.23) * mm});
            skLineSegment(sketch, "E794", {"start": v(5420.7, -951.23) * mm, "end": v(5431.73, -946.66) * mm});
            skLineSegment(sketch, "E795", {"start": v(4837.06, -3048.7) * mm, "end": v(4848.09, -3053.27) * mm});
            skLineSegment(sketch, "E796", {"start": v(4825.23, -3047.14) * mm, "end": v(4837.06, -3048.7) * mm});
            skLineSegment(sketch, "E797", {"start": v(7238.05, -3048.24) * mm, "end": v(7249.89, -3049.8) * mm});
            skLineSegment(sketch, "E798", {"start": v(7193.88, -3105.8) * mm, "end": v(7192.43, -3094.78) * mm});
            skLineSegment(sketch, "E799", {"start": v(5483.14, -1013.7) * mm, "end": v(5475.88, -1023.16) * mm});
            skLineSegment(sketch, "E800", {"start": v(5455.38, -1034.99) * mm, "end": v(5443.55, -1036.55) * mm});
            skLineSegment(sketch, "E801", {"start": v(6583.22, -914.3) * mm, "end": v(6575.6, -922.15) * mm});
            skLineSegment(sketch, "E802", {"start": v(5511.53, -1071.99) * mm, "end": v(5503.91, -1079.84) * mm});
            skLineSegment(sketch, "E803", {"start": v(5511.53, -1127.87) * mm, "end": v(5519.67, -1127.87) * mm});
            skLineSegment(sketch, "E804", {"start": v(5511.53, -1127.87) * mm, "end": v(5503.91, -1127.87) * mm});
            skLineSegment(sketch, "E805", {"start": v(7192.33, -3093.96) * mm, "end": v(7193.89, -3082.12) * mm});
            skLineSegment(sketch, "E806", {"start": v(7226.2, -3138.12) * mm, "end": v(7215.18, -3133.56) * mm});
            skLineSegment(sketch, "E807", {"start": v(7193.28, -644.83) * mm, "end": v(7197.85, -633.8) * mm});
            skLineSegment(sketch, "E808", {"start": v(4870.33, -657.84) * mm, "end": v(4868.77, -669.67) * mm});
            skLineSegment(sketch, "E809", {"start": v(6637.11, -798.46) * mm, "end": v(6646.58, -791.2) * mm});
            skLineSegment(sketch, "E810", {"start": v(6629.85, -807.92) * mm, "end": v(6637.11, -798.46) * mm});
            skLineSegment(sketch, "E811", {"start": v(4780.45, -645.99) * mm, "end": v(4785.02, -634.96) * mm});
            skLineSegment(sketch, "E812", {"start": v(6625.27, -842.62) * mm, "end": v(6623.72, -830.78) * mm});
            skLineSegment(sketch, "E813", {"start": v(4917.04, -2960.2) * mm, "end": v(4946.25, -2960.2) * mm});
            skLineSegment(sketch, "E814", {"start": v(4917.04, -2988.15) * mm, "end": v(4946.25, -2988.15) * mm});
            skLineSegment(sketch, "E815", {"start": v(4946.25, -2932.27) * mm, "end": v(4917.04, -2932.27) * mm});
            skLineSegment(sketch, "E816", {"start": v(4917.04, -2988.15) * mm, "end": v(4917.04, -2960.2) * mm});
            skLineSegment(sketch, "E817", {"start": v(7164.23, -2955.78) * mm, "end": v(7164.23, -2927.84) * mm});
            skLineSegment(sketch, "E818", {"start": v(7135.02, -2955.78) * mm, "end": v(7164.23, -2955.78) * mm});
            skLineSegment(sketch, "E819", {"start": v(7135.02, -2983.72) * mm, "end": v(7135.02, -2955.78) * mm});
            skLineSegment(sketch, "E820", {"start": v(4870.7, -3094.78) * mm, "end": v(4869.38, -3104.7) * mm});
            skLineSegment(sketch, "E821", {"start": v(7197.84, -679.52) * mm, "end": v(7193.27, -668.5) * mm});
            skLineSegment(sketch, "E822", {"start": v(4856.93, -690.16) * mm, "end": v(4847.46, -697.43) * mm});
            skLineSegment(sketch, "E823", {"start": v(6713.6, -842.63) * mm, "end": v(6709.03, -853.65) * mm});
            skLineSegment(sketch, "E824", {"start": v(7260.9, -3133.56) * mm, "end": v(7249.87, -3138.13) * mm});
            skLineSegment(sketch, "E825", {"start": v(7270.37, -3126.3) * mm, "end": v(7260.9, -3133.56) * mm});
            skLineSegment(sketch, "E826", {"start": v(7277.64, -3116.83) * mm, "end": v(7270.37, -3126.3) * mm});
            skLineSegment(sketch, "E827", {"start": v(7282.2, -3105.8) * mm, "end": v(7277.64, -3116.83) * mm});
            skLineSegment(sketch, "E828", {"start": v(6709.03, -853.65) * mm, "end": v(6701.76, -863.12) * mm});
            skLineSegment(sketch, "E829", {"start": v(6681.26, -874.95) * mm, "end": v(6669.43, -876.5) * mm});
            skLineSegment(sketch, "E830", {"start": v(5400.23, -2906.24) * mm, "end": v(5398.67, -2894.41) * mm});
            skLineSegment(sketch, "E831", {"start": v(5483.99, -2871.56) * mm, "end": v(5488.55, -2882.6) * mm});
            skLineSegment(sketch, "E832", {"start": v(6646.58, -791.2) * mm, "end": v(6657.61, -786.63) * mm});
            skLineSegment(sketch, "E833", {"start": v(6646.57, -870.38) * mm, "end": v(6642.74, -866.78) * mm});
            skLineSegment(sketch, "E834", {"start": v(7260.3, -696.27) * mm, "end": v(7249.26, -700.83) * mm});
            skLineSegment(sketch, "E835", {"start": v(7281.6, -668.5) * mm, "end": v(7277.03, -679.53) * mm});
            skLineSegment(sketch, "E836", {"start": v(7197.85, -633.8) * mm, "end": v(7205.11, -624.34) * mm});
            skLineSegment(sketch, "E837", {"start": v(7135.02, -2983.72) * mm, "end": v(7164.23, -2983.72) * mm});
            skLineSegment(sketch, "E838", {"start": v(7164.23, -2927.84) * mm, "end": v(7135.02, -2927.84) * mm});
            skLineSegment(sketch, "E839", {"start": v(6583.22, -970.17) * mm, "end": v(6591.36, -970.17) * mm});
            skLineSegment(sketch, "E840", {"start": v(6583.22, -970.17) * mm, "end": v(6575.6, -970.17) * mm});
            skLineSegment(sketch, "E841", {"start": v(6583.22, -914.3) * mm, "end": v(6583.22, -970.17) * mm});
            skLineSegment(sketch, "E842", {"start": v(5467.26, -2854.83) * mm, "end": v(5470.06, -2856.98) * mm});
            skLineSegment(sketch, "E843", {"start": v(4847.46, -697.43) * mm, "end": v(4836.43, -702) * mm});
            skLineSegment(sketch, "E844", {"start": v(4785.01, -680.68) * mm, "end": v(4780.44, -669.66) * mm});
            skLineSegment(sketch, "E845", {"start": v(4848.09, -3053.27) * mm, "end": v(4857.56, -3060.53) * mm});
            skLineSegment(sketch, "E846", {"start": v(5540.13, -2795.6) * mm, "end": v(5548.27, -2795.6) * mm});
            skLineSegment(sketch, "E847", {"start": v(5540.13, -2739.72) * mm, "end": v(5532.51, -2747.57) * mm});
            skLineSegment(sketch, "E848", {"start": v(5540.13, -2795.6) * mm, "end": v(5532.51, -2795.6) * mm});
            skLineSegment(sketch, "E849", {"start": v(5540.13, -2739.72) * mm, "end": v(5540.13, -2795.6) * mm});
            skLineSegment(sketch, "E850", {"start": v(6579.65, -2746.34) * mm, "end": v(6572.03, -2754.2) * mm});
            skLineSegment(sketch, "E851", {"start": v(6681.28, -786.63) * mm, "end": v(6692.3, -791.2) * mm});
            skLineSegment(sketch, "E852", {"start": v(7198.45, -3116.82) * mm, "end": v(7193.88, -3105.8) * mm});
            skLineSegment(sketch, "E853", {"start": v(7226.22, -3049.8) * mm, "end": v(7236.22, -3048.49) * mm});
            skLineSegment(sketch, "E854", {"start": v(5399.39, -1002.65) * mm, "end": v(5397.83, -990.82) * mm});
            skLineSegment(sketch, "E855", {"start": v(6647.34, -2856.64) * mm, "end": v(6658.37, -2852.07) * mm});
            skLineSegment(sketch, "E856", {"start": v(6626.04, -2908.06) * mm, "end": v(6624.48, -2896.23) * mm});
            skLineSegment(sketch, "E857", {"start": v(5412.07, -2862.08) * mm, "end": v(5421.54, -2854.82) * mm});
            skLineSegment(sketch, "E858", {"start": v(5443.55, -1036.55) * mm, "end": v(5431.71, -1034.99) * mm});
            skLineSegment(sketch, "E859", {"start": v(5431.71, -1034.99) * mm, "end": v(5421.9, -1030.92) * mm});
            skLineSegment(sketch, "E860", {"start": v(6713.6, -818.96) * mm, "end": v(6715.16, -830.8) * mm});
            skLineSegment(sketch, "E861", {"start": v(6658.36, -2940.4) * mm, "end": v(6653.8, -2938.1) * mm});
            skLineSegment(sketch, "E862", {"start": v(6647.33, -2935.82) * mm, "end": v(6637.87, -2928.56) * mm});
            skLineSegment(sketch, "E863", {"start": v(6637.87, -2928.56) * mm, "end": v(6630.6, -2919.09) * mm});
            skLineSegment(sketch, "E864", {"start": v(4847.47, -618.24) * mm, "end": v(4856.94, -625.5) * mm});
            skLineSegment(sketch, "E865", {"start": v(4856.94, -625.5) * mm, "end": v(4864.2, -634.97) * mm});
            skLineSegment(sketch, "E866", {"start": v(5420.69, -1030.42) * mm, "end": v(5417.9, -1027.84) * mm});
            skLineSegment(sketch, "E867", {"start": v(5411.22, -1023.15) * mm, "end": v(5403.95, -1013.68) * mm});
            skLineSegment(sketch, "E868", {"start": v(5403.95, -1013.68) * mm, "end": v(5399.39, -1002.65) * mm});
            skLineSegment(sketch, "E869", {"start": v(4848.08, -3132.46) * mm, "end": v(4837.05, -3137.02) * mm});
            skLineSegment(sketch, "E870", {"start": v(4837.05, -3137.02) * mm, "end": v(4825.22, -3138.58) * mm});
            skLineSegment(sketch, "E871", {"start": v(4825.22, -3138.58) * mm, "end": v(4813.38, -3137.02) * mm});
            skLineSegment(sketch, "E872", {"start": v(7215.2, -3054.37) * mm, "end": v(7226.22, -3049.8) * mm});
            skLineSegment(sketch, "E873", {"start": v(4779.5, -3092.85) * mm, "end": v(4781.06, -3081.02) * mm});
            skLineSegment(sketch, "E874", {"start": v(4813.38, -3137.02) * mm, "end": v(4802.36, -3132.45) * mm});
            skLineSegment(sketch, "E875", {"start": v(4823.22, -3047.4) * mm, "end": v(4825.23, -3047.14) * mm});
            skLineSegment(sketch, "E876", {"start": v(7238.04, -3139.68) * mm, "end": v(7226.2, -3138.12) * mm});
            skLineSegment(sketch, "E877", {"start": v(4778.89, -657.82) * mm, "end": v(4780.45, -645.99) * mm});
            skLineSegment(sketch, "E878", {"start": v(7249.87, -3138.13) * mm, "end": v(7238.04, -3139.68) * mm});
            skLineSegment(sketch, "E879", {"start": v(4792.9, -3060.52) * mm, "end": v(4802.37, -3053.26) * mm});
            skLineSegment(sketch, "E880", {"start": v(4785.63, -3070) * mm, "end": v(4792.9, -3060.52) * mm});
            skLineSegment(sketch, "E881", {"start": v(4781.06, -3081.02) * mm, "end": v(4785.63, -3070) * mm});
            skLineSegment(sketch, "E882", {"start": v(5432.56, -2850.25) * mm, "end": v(5444.4, -2848.7) * mm});
            skLineSegment(sketch, "E883", {"start": v(5444.4, -2848.7) * mm, "end": v(5456.23, -2850.26) * mm});
            skLineSegment(sketch, "E884", {"start": v(5421.54, -2854.82) * mm, "end": v(5432.56, -2850.25) * mm});
            skLineSegment(sketch, "E885", {"start": v(5404.8, -2871.55) * mm, "end": v(5412.07, -2862.08) * mm});
            skLineSegment(sketch, "E886", {"start": v(7225.61, -612.5) * mm, "end": v(7237.44, -610.95) * mm});
            skLineSegment(sketch, "E887", {"start": v(5483.15, -967.97) * mm, "end": v(5487.72, -979) * mm});
            skLineSegment(sketch, "E888", {"start": v(5487.71, -1002.67) * mm, "end": v(5483.14, -1013.7) * mm});
            skLineSegment(sketch, "E889", {"start": v(5456.22, -2938.58) * mm, "end": v(5444.38, -2940.14) * mm});
            skLineSegment(sketch, "E890", {"start": v(5444.38, -2940.14) * mm, "end": v(5432.55, -2938.58) * mm});
            skLineSegment(sketch, "E891", {"start": v(5399.4, -978.99) * mm, "end": v(5403.96, -967.96) * mm});
            skLineSegment(sketch, "E892", {"start": v(5397.83, -990.82) * mm, "end": v(5399.4, -978.99) * mm});
            skLineSegment(sketch, "E893", {"start": v(7132, -815.27) * mm, "end": v(7132, -787.33) * mm});
            skLineSegment(sketch, "E894", {"start": v(7132, -787.33) * mm, "end": v(7161.22, -787.33) * mm});
            skLineSegment(sketch, "E895", {"start": v(7161.22, -759.4) * mm, "end": v(7132, -759.4) * mm});
            skLineSegment(sketch, "E896", {"start": v(7132, -815.27) * mm, "end": v(7161.22, -815.27) * mm});
            skLineSegment(sketch, "E897", {"start": v(4946.25, -2960.2) * mm, "end": v(4946.25, -2932.27) * mm});
            skLineSegment(sketch, "E898", {"start": v(4801.75, -618.23) * mm, "end": v(4812.78, -613.66) * mm});
            skLineSegment(sketch, "E899", {"start": v(6670.2, -2850.51) * mm, "end": v(6682.04, -2852.07) * mm});
            skLineSegment(sketch, "E900", {"start": v(6682.04, -2852.07) * mm, "end": v(6687.1, -2854.17) * mm});
            skLineSegment(sketch, "E901", {"start": v(6693.06, -2856.64) * mm, "end": v(6702.53, -2863.9) * mm});
            skLineSegment(sketch, "E902", {"start": v(6702.53, -2863.9) * mm, "end": v(6709.8, -2873.38) * mm});
            skLineSegment(sketch, "E903", {"start": v(6715.16, -830.8) * mm, "end": v(6713.6, -842.63) * mm});
            skLineSegment(sketch, "E904", {"start": v(6714.36, -2908.07) * mm, "end": v(6709.8, -2919.1) * mm});
            skLineSegment(sketch, "E905", {"start": v(6709.8, -2919.1) * mm, "end": v(6702.52, -2928.57) * mm});
            skLineSegment(sketch, "E906", {"start": v(6702.52, -2928.57) * mm, "end": v(6693.05, -2935.83) * mm});
            skLineSegment(sketch, "E907", {"start": v(6658.37, -2852.07) * mm, "end": v(6670.2, -2850.51) * mm});
            skLineSegment(sketch, "E908", {"start": v(6701.76, -863.12) * mm, "end": v(6692.3, -870.39) * mm});
            skLineSegment(sketch, "E909", {"start": v(5400.23, -2882.58) * mm, "end": v(5404.8, -2871.55) * mm});
            skLineSegment(sketch, "E910", {"start": v(5398.67, -2894.41) * mm, "end": v(5400.23, -2882.58) * mm});
            skLineSegment(sketch, "E911", {"start": v(6669.44, -785.07) * mm, "end": v(6681.28, -786.63) * mm});
            skLineSegment(sketch, "E912", {"start": v(7191.72, -656.66) * mm, "end": v(7193.28, -644.83) * mm});
            skLineSegment(sketch, "E913", {"start": v(7260.3, -617.08) * mm, "end": v(7269.77, -624.34) * mm});
            skLineSegment(sketch, "E914", {"start": v(7214.58, -617.07) * mm, "end": v(7225.61, -612.5) * mm});
            skLineSegment(sketch, "E915", {"start": v(7236.22, -3048.49) * mm, "end": v(7238.05, -3048.24) * mm});
            skLineSegment(sketch, "E916", {"start": v(4792.27, -690.15) * mm, "end": v(4785.01, -680.68) * mm});
            skLineSegment(sketch, "E917", {"start": v(4792.89, -3125.18) * mm, "end": v(4785.62, -3115.71) * mm});
            skLineSegment(sketch, "E918", {"start": v(6693.05, -2935.83) * mm, "end": v(6682.03, -2940.4) * mm});
            skLineSegment(sketch, "E919", {"start": v(6682.03, -2940.4) * mm, "end": v(6670.2, -2941.95) * mm});
            skLineSegment(sketch, "E920", {"start": v(6670.2, -2941.95) * mm, "end": v(6659.76, -2940.58) * mm});
            skLineSegment(sketch, "E921", {"start": v(5476.71, -2926.75) * mm, "end": v(5467.24, -2934.02) * mm});
            skLineSegment(sketch, "E922", {"start": v(5467.24, -2934.02) * mm, "end": v(5456.22, -2938.58) * mm});
            skLineSegment(sketch, "E923", {"start": v(4864.2, -680.7) * mm, "end": v(4856.93, -690.16) * mm});
            skLineSegment(sketch, "E924", {"start": v(7236.22, -702.23) * mm, "end": v(7225.6, -700.83) * mm});
            skLineSegment(sketch, "E925", {"start": v(4812.77, -701.99) * mm, "end": v(4801.74, -697.42) * mm});
            skLineSegment(sketch, "E926", {"start": v(7260.91, -3054.37) * mm, "end": v(7270.38, -3061.64) * mm});
            skLineSegment(sketch, "E927", {"start": v(7249.28, -612.5) * mm, "end": v(7260.3, -617.08) * mm});
            skLineSegment(sketch, "E928", {"start": v(7277.04, -633.81) * mm, "end": v(7281.6, -644.84) * mm});
            skLineSegment(sketch, "E929", {"start": v(4869.38, -3104.7) * mm, "end": v(4864.81, -3115.72) * mm});
            skLineSegment(sketch, "E930", {"start": v(4870.94, -3092.86) * mm, "end": v(4870.7, -3094.78) * mm});
            skLineSegment(sketch, "E931", {"start": v(5432.55, -2938.58) * mm, "end": v(5423.42, -2934.8) * mm});
            skLineSegment(sketch, "E932", {"start": v(5421.52, -2934) * mm, "end": v(5416.75, -2929.68) * mm});
            skLineSegment(sketch, "E933", {"start": v(5443.56, -945.1) * mm, "end": v(5455.4, -946.67) * mm});
            skLineSegment(sketch, "E934", {"start": v(5455.4, -946.67) * mm, "end": v(5466.42, -951.23) * mm});
            skLineSegment(sketch, "E935", {"start": v(5466.42, -951.23) * mm, "end": v(5471.87, -955.42) * mm});
            skLineSegment(sketch, "E936", {"start": v(7237.44, -610.95) * mm, "end": v(7249.28, -612.5) * mm});
            skLineSegment(sketch, "E937", {"start": v(7193.27, -668.5) * mm, "end": v(7191.72, -656.66) * mm});
            skLineSegment(sketch, "E938", {"start": v(7205.11, -624.34) * mm, "end": v(7214.58, -617.07) * mm});
            skLineSegment(sketch, "E939", {"start": v(5488.55, -2882.6) * mm, "end": v(5490.1, -2894.42) * mm});
            skLineSegment(sketch, "E940", {"start": v(5490.1, -2894.42) * mm, "end": v(5488.55, -2906.26) * mm});
            skLineSegment(sketch, "E941", {"start": v(4892.76, -752.14) * mm, "end": v(4863.55, -752.14) * mm});
            skLineSegment(sketch, "E942", {"start": v(4863.55, -780.08) * mm, "end": v(4892.76, -780.08) * mm});
            skLineSegment(sketch, "E943", {"start": v(4892.76, -780.08) * mm, "end": v(4892.76, -752.14) * mm});
            skLineSegment(sketch, "E944", {"start": v(7161.22, -787.33) * mm, "end": v(7161.22, -759.4) * mm});
            skLineSegment(sketch, "E945", {"start": v(6624.48, -2896.23) * mm, "end": v(6626.04, -2884.4) * mm});
            skLineSegment(sketch, "E946", {"start": v(6626.04, -2884.4) * mm, "end": v(6630.6, -2873.37) * mm});
            skLineSegment(sketch, "E947", {"start": v(6630.6, -2873.37) * mm, "end": v(6637.87, -2863.9) * mm});
            skLineSegment(sketch, "E948", {"start": v(6637.87, -2863.9) * mm, "end": v(6647.34, -2856.64) * mm});
            skLineSegment(sketch, "E949", {"start": v(4869.39, -3081.03) * mm, "end": v(4870.94, -3092.86) * mm});
            skLineSegment(sketch, "E950", {"start": v(4864.82, -3070) * mm, "end": v(4869.39, -3081.03) * mm});
            skLineSegment(sketch, "E951", {"start": v(4857.56, -3060.53) * mm, "end": v(4864.82, -3070) * mm});
            skLineSegment(sketch, "E952", {"start": v(7205.71, -3126.29) * mm, "end": v(7198.45, -3116.82) * mm});
            skLineSegment(sketch, "E953", {"start": v(4792.28, -625.5) * mm, "end": v(4801.75, -618.23) * mm});
            skLineSegment(sketch, "E954", {"start": v(4864.2, -634.97) * mm, "end": v(4868.77, -646) * mm});
            skLineSegment(sketch, "E955", {"start": v(4868.77, -646) * mm, "end": v(4870.14, -656.39) * mm});
            skLineSegment(sketch, "E956", {"start": v(4870.14, -656.39) * mm, "end": v(4870.33, -657.84) * mm});
            skLineSegment(sketch, "E957", {"start": v(7269.77, -624.34) * mm, "end": v(7277.04, -633.81) * mm});
            skLineSegment(sketch, "E958", {"start": v(7269.76, -689) * mm, "end": v(7260.3, -696.27) * mm});
            skLineSegment(sketch, "E959", {"start": v(7277.03, -679.53) * mm, "end": v(7269.76, -689) * mm});
            skLineSegment(sketch, "E960", {"start": v(5466.4, -1030.42) * mm, "end": v(5455.38, -1034.99) * mm});
            skLineSegment(sketch, "E961", {"start": v(5475.89, -958.5) * mm, "end": v(5483.15, -967.97) * mm});
            skLineSegment(sketch, "E962", {"start": v(6625.28, -818.95) * mm, "end": v(6629.85, -807.92) * mm});
            skLineSegment(sketch, "E963", {"start": v(6623.72, -830.78) * mm, "end": v(6625.28, -818.95) * mm});
            skLineSegment(sketch, "E964", {"start": v(6630.6, -2919.09) * mm, "end": v(6626.04, -2908.06) * mm});
            skLineSegment(sketch, "E965", {"start": v(6709.8, -2873.38) * mm, "end": v(6714.36, -2884.4) * mm});
            skLineSegment(sketch, "E966", {"start": v(6714.36, -2884.4) * mm, "end": v(6715.92, -2896.24) * mm});
            skLineSegment(sketch, "E967", {"start": v(6715.92, -2896.24) * mm, "end": v(6714.36, -2908.07) * mm});
            skLineSegment(sketch, "E968", {"start": v(6701.77, -798.46) * mm, "end": v(6709.04, -807.93) * mm});
            skLineSegment(sketch, "E969", {"start": v(6637.1, -863.11) * mm, "end": v(6629.84, -853.64) * mm});
            skLineSegment(sketch, "E970", {"start": v(6669.43, -876.5) * mm, "end": v(6657.6, -874.95) * mm});
            skLineSegment(sketch, "E971", {"start": v(5489.27, -990.83) * mm, "end": v(5487.71, -1002.67) * mm});
            skLineSegment(sketch, "E972", {"start": v(5475.88, -1023.16) * mm, "end": v(5466.4, -1030.42) * mm});
            skLineSegment(sketch, "E973", {"start": v(7205.1, -689) * mm, "end": v(7197.84, -679.52) * mm});
            skLineSegment(sketch, "E974", {"start": v(7237.43, -702.39) * mm, "end": v(7236.22, -702.23) * mm});
            skLineSegment(sketch, "E975", {"start": v(7225.6, -700.83) * mm, "end": v(7214.57, -696.26) * mm});
            skLineSegment(sketch, "E976", {"start": v(7281.6, -644.84) * mm, "end": v(7283.16, -656.68) * mm});
            skLineSegment(sketch, "E977", {"start": v(5456.23, -2850.26) * mm, "end": v(5467.26, -2854.83) * mm});
            skLineSegment(sketch, "E978", {"start": v(5476.72, -2862.1) * mm, "end": v(5483.99, -2871.56) * mm});
            skLineSegment(sketch, "E979", {"start": v(6696.07, -794.09) * mm, "end": v(6697.94, -794.86) * mm});
            skLineSegment(sketch, "E980", {"start": v(6648.44, -871.16) * mm, "end": v(6646.57, -870.38) * mm});
            skLineSegment(sketch, "E981", {"start": v(6642.74, -866.78) * mm, "end": v(6637.1, -863.11) * mm});
            skLineSegment(sketch, "E982", {"start": v(5471.95, -2857.76) * mm, "end": v(5476.72, -2862.1) * mm});
            skLineSegment(sketch, "E983", {"start": v(5470.06, -2856.98) * mm, "end": v(5471.95, -2857.76) * mm});
            skLineSegment(sketch, "E984", {"start": v(5421.9, -1030.92) * mm, "end": v(5420.69, -1030.42) * mm});
            skLineSegment(sketch, "E985", {"start": v(6653.8, -2938.1) * mm, "end": v(6647.33, -2935.82) * mm});
            skLineSegment(sketch, "E986", {"start": v(5417.9, -1027.84) * mm, "end": v(5411.22, -1023.15) * mm});
            skLineSegment(sketch, "E987", {"start": v(6688.5, -2854.35) * mm, "end": v(6693.06, -2856.64) * mm});
            skLineSegment(sketch, "E988", {"start": v(6687.1, -2854.17) * mm, "end": v(6688.5, -2854.35) * mm});
            skLineSegment(sketch, "E989", {"start": v(6659.76, -2940.58) * mm, "end": v(6658.36, -2940.4) * mm});
            skLineSegment(sketch, "E990", {"start": v(5423.42, -2934.8) * mm, "end": v(5421.52, -2934) * mm});
            skLineSegment(sketch, "E991", {"start": v(5416.75, -2929.68) * mm, "end": v(5412.06, -2926.74) * mm});
            skLineSegment(sketch, "E992", {"start": v(5473.1, -955.93) * mm, "end": v(5475.89, -958.5) * mm});
            skLineSegment(sketch, "E993", {"start": v(5471.87, -955.42) * mm, "end": v(5473.1, -955.93) * mm});
            skLineSegment(sketch, "E994", {"start": v(6697.94, -794.86) * mm, "end": v(6701.77, -798.46) * mm});
            skLineSegment(sketch, "E995", {"start": v(-3625.47, 3936.2) * mm, "end": v(-3714.89, 3936.2) * mm});
            skLineSegment(sketch, "E996", {"start": v(-3714.89, 3936.2) * mm, "end": v(-3714.89, 4223.08) * mm});
            skLineSegment(sketch, "E997", {"start": v(-3714.89, 4223.08) * mm, "end": v(-3625.47, 4223.08) * mm});
            skLineSegment(sketch, "E998", {"start": v(-3625.47, 4223.08) * mm, "end": v(-3625.47, 3936.2) * mm});
            skLineSegment(sketch, "E999", {"start": v(-3622.92, 4263.96) * mm, "end": v(-3717.44, 4263.96) * mm});
            skLineSegment(sketch, "E1000", {"start": v(-3717.44, 4263.96) * mm, "end": v(-3717.44, 4333.7) * mm});
            skLineSegment(sketch, "E1001", {"start": v(-3717.44, 4333.7) * mm, "end": v(-3622.92, 4333.7) * mm});
            skLineSegment(sketch, "E1002", {"start": v(-3622.92, 4333.7) * mm, "end": v(-3622.92, 4263.96) * mm});
            skLineSegment(sketch, "E1003", {"start": v(-3282.63, 4059.33) * mm, "end": v(-3285.22, 4032.7) * mm});
            skLineSegment(sketch, "E1004", {"start": v(-3285.22, 4032.7) * mm, "end": v(-3292.98, 4008.49) * mm});
            skLineSegment(sketch, "E1005", {"start": v(-3292.98, 4008.49) * mm, "end": v(-3305.72, 3987.22) * mm});
            skLineSegment(sketch, "E1006", {"start": v(-3305.72, 3987.22) * mm, "end": v(-3323.25, 3969.4) * mm});
            skLineSegment(sketch, "E1007", {"start": v(-3323.25, 3969.4) * mm, "end": v(-3345.2, 3955.2) * mm});
            skLineSegment(sketch, "E1008", {"start": v(-3345.2, 3955.2) * mm, "end": v(-3370.64, 3944.75) * mm});
            skLineSegment(sketch, "E1009", {"start": v(-3370.64, 3944.75) * mm, "end": v(-3400.82, 3938.33) * mm});
            skLineSegment(sketch, "E1010", {"start": v(-3400.82, 3938.33) * mm, "end": v(-3436.94, 3936.2) * mm});
            skLineSegment(sketch, "E1011", {"start": v(-3436.94, 3936.2) * mm, "end": v(-3478.23, 3938.04) * mm});
            skLineSegment(sketch, "E1012", {"start": v(-3478.23, 3938.04) * mm, "end": v(-3513.2, 3943.6) * mm});
            skLineSegment(sketch, "E1013", {"start": v(-3513.2, 3943.6) * mm, "end": v(-3564.93, 3960.2) * mm});
            skLineSegment(sketch, "E1014", {"start": v(-3564.93, 3960.2) * mm, "end": v(-3564.93, 4042.72) * mm});
            skLineSegment(sketch, "E1015", {"start": v(-3564.93, 4042.72) * mm, "end": v(-3555.73, 4042.72) * mm});
            skLineSegment(sketch, "E1016", {"start": v(-3555.73, 4042.72) * mm, "end": v(-3532.96, 4030.33) * mm});
            skLineSegment(sketch, "E1017", {"start": v(-3532.96, 4030.33) * mm, "end": v(-3506.55, 4019.73) * mm});
            skLineSegment(sketch, "E1018", {"start": v(-3506.55, 4019.73) * mm, "end": v(-3479.57, 4012.45) * mm});
            skLineSegment(sketch, "E1019", {"start": v(-3479.57, 4012.45) * mm, "end": v(-3455.08, 4010.02) * mm});
            skLineSegment(sketch, "E1020", {"start": v(-3455.08, 4010.02) * mm, "end": v(-3425.06, 4012.45) * mm});
            skLineSegment(sketch, "E1021", {"start": v(-3425.06, 4012.45) * mm, "end": v(-3410.14, 4016.31) * mm});
            skLineSegment(sketch, "E1022", {"start": v(-3410.14, 4016.31) * mm, "end": v(-3397.85, 4023.05) * mm});
            skLineSegment(sketch, "E1023", {"start": v(-3397.85, 4023.05) * mm, "end": v(-3383.93, 4038.76) * mm});
            skLineSegment(sketch, "E1024", {"start": v(-3383.93, 4038.76) * mm, "end": v(-3380, 4050.03) * mm});
            skLineSegment(sketch, "E1025", {"start": v(-3380, 4050.03) * mm, "end": v(-3378.69, 4065.2) * mm});
            skLineSegment(sketch, "E1026", {"start": v(-3378.69, 4065.2) * mm, "end": v(-3380.54, 4080.12) * mm});
            skLineSegment(sketch, "E1027", {"start": v(-3380.54, 4080.12) * mm, "end": v(-3386.1, 4091.13) * mm});
            skLineSegment(sketch, "E1028", {"start": v(-3386.1, 4091.13) * mm, "end": v(-3394.72, 4098.96) * mm});
            skLineSegment(sketch, "E1029", {"start": v(-3394.72, 4098.96) * mm, "end": v(-3405.77, 4104.29) * mm});
            skLineSegment(sketch, "E1030", {"start": v(-3405.77, 4104.29) * mm, "end": v(-3435.15, 4109.14) * mm});
            skLineSegment(sketch, "E1031", {"start": v(-3435.15, 4109.14) * mm, "end": v(-3465.3, 4109.65) * mm});
            skLineSegment(sketch, "E1032", {"start": v(-3465.3, 4109.65) * mm, "end": v(-3481.64, 4109.65) * mm});
            skLineSegment(sketch, "E1033", {"start": v(-3481.64, 4109.65) * mm, "end": v(-3481.64, 4176.59) * mm});
            skLineSegment(sketch, "E1034", {"start": v(-3481.64, 4176.59) * mm, "end": v(-3466.57, 4176.59) * mm});
            skLineSegment(sketch, "E1035", {"start": v(-3466.57, 4176.59) * mm, "end": v(-3434.64, 4178.12) * mm});
            skLineSegment(sketch, "E1036", {"start": v(-3434.64, 4178.12) * mm, "end": v(-3409.86, 4184.25) * mm});
            skLineSegment(sketch, "E1037", {"start": v(-3409.86, 4184.25) * mm, "end": v(-3393.9, 4197.8) * mm});
            skLineSegment(sketch, "E1038", {"start": v(-3393.9, 4197.8) * mm, "end": v(-3389.58, 4208.01) * mm});
            skLineSegment(sketch, "E1039", {"start": v(-3389.58, 4208.01) * mm, "end": v(-3388.14, 4221.3) * mm});
            skLineSegment(sketch, "E1040", {"start": v(-3388.14, 4221.3) * mm, "end": v(-3389.48, 4231.74) * mm});
            skLineSegment(sketch, "E1041", {"start": v(-3389.48, 4231.74) * mm, "end": v(-3393.5, 4240.07) * mm});
            skLineSegment(sketch, "E1042", {"start": v(-3393.5, 4240.07) * mm, "end": v(-3406.8, 4251.44) * mm});
            skLineSegment(sketch, "E1043", {"start": v(-3406.8, 4251.44) * mm, "end": v(-3428.25, 4257.57) * mm});
            skLineSegment(sketch, "E1044", {"start": v(-3428.25, 4257.57) * mm, "end": v(-3449.2, 4259.1) * mm});
            skLineSegment(sketch, "E1045", {"start": v(-3449.2, 4259.1) * mm, "end": v(-3477.81, 4255.78) * mm});
            skLineSegment(sketch, "E1046", {"start": v(-3477.81, 4255.78) * mm, "end": v(-3506.17, 4247.35) * mm});
            skLineSegment(sketch, "E1047", {"start": v(-3506.17, 4247.35) * mm, "end": v(-3528.65, 4236.75) * mm});
            skLineSegment(sketch, "E1048", {"start": v(-3528.65, 4236.75) * mm, "end": v(-3546.02, 4226.92) * mm});
            skLineSegment(sketch, "E1049", {"start": v(-3546.02, 4226.92) * mm, "end": v(-3553.94, 4226.92) * mm});
            skLineSegment(sketch, "E1050", {"start": v(-3553.94, 4226.92) * mm, "end": v(-3553.94, 4308.41) * mm});
            skLineSegment(sketch, "E1051", {"start": v(-3553.94, 4308.41) * mm, "end": v(-3500.93, 4324.63) * mm});
            skLineSegment(sketch, "E1052", {"start": v(-3500.93, 4324.63) * mm, "end": v(-3467.24, 4330.48) * mm});
            skLineSegment(sketch, "E1053", {"start": v(-3467.24, 4330.48) * mm, "end": v(-3432.85, 4332.42) * mm});
            skLineSegment(sketch, "E1054", {"start": v(-3432.85, 4332.42) * mm, "end": v(-3401.14, 4330.96) * mm});
            skLineSegment(sketch, "E1055", {"start": v(-3401.14, 4330.96) * mm, "end": v(-3373.96, 4326.55) * mm});
            skLineSegment(sketch, "E1056", {"start": v(-3373.96, 4326.55) * mm, "end": v(-3350.88, 4319.33) * mm});
            skLineSegment(sketch, "E1057", {"start": v(-3350.88, 4319.33) * mm, "end": v(-3331.43, 4309.43) * mm});
            skLineSegment(sketch, "E1058", {"start": v(-3331.43, 4309.43) * mm, "end": v(-3314.44, 4295.8) * mm});
            skLineSegment(sketch, "E1059", {"start": v(-3314.44, 4295.8) * mm, "end": v(-3302.3, 4278.9) * mm});
            skLineSegment(sketch, "E1060", {"start": v(-3302.3, 4278.9) * mm, "end": v(-3295.02, 4259.2) * mm});
            skLineSegment(sketch, "E1061", {"start": v(-3295.02, 4259.2) * mm, "end": v(-3292.6, 4237.13) * mm});
            skLineSegment(sketch, "E1062", {"start": v(-3292.6, 4237.13) * mm, "end": v(-3297.3, 4206.7) * mm});
            skLineSegment(sketch, "E1063", {"start": v(-3297.3, 4206.7) * mm, "end": v(-3311.37, 4180.3) * mm});
            skLineSegment(sketch, "E1064", {"start": v(-3311.37, 4180.3) * mm, "end": v(-3333.12, 4160.2) * mm});
            skLineSegment(sketch, "E1065", {"start": v(-3333.12, 4160.2) * mm, "end": v(-3360.8, 4148.74) * mm});
            skLineSegment(sketch, "E1066", {"start": v(-3360.8, 4148.74) * mm, "end": v(-3360.8, 4145.17) * mm});
            skLineSegment(sketch, "E1067", {"start": v(-3360.8, 4145.17) * mm, "end": v(-3334.37, 4138.27) * mm});
            skLineSegment(sketch, "E1068", {"start": v(-3334.37, 4138.27) * mm, "end": v(-3309.2, 4122.43) * mm});
            skLineSegment(sketch, "E1069", {"start": v(-3309.2, 4122.43) * mm, "end": v(-3298.7, 4111.03) * mm});
            skLineSegment(sketch, "E1070", {"start": v(-3298.7, 4111.03) * mm, "end": v(-3290.17, 4096.75) * mm});
            skLineSegment(sketch, "E1071", {"start": v(-3290.17, 4096.75) * mm, "end": v(-3284.52, 4079.54) * mm});
            skLineSegment(sketch, "E1072", {"start": v(-3284.52, 4079.54) * mm, "end": v(-3282.63, 4059.33) * mm});
            skLineSegment(sketch, "E1073", {"start": v(5511.53, -1071.99) * mm, "end": v(5511.53, -1127.87) * mm});
            skLineSegment(sketch, "E1074", {"start": v(5457.5, -700.63) * mm, "end": v(5455.94, -688.8) * mm});
            skLineSegment(sketch, "E1075", {"start": v(5478.8, -649.2) * mm, "end": v(5489.83, -644.63) * mm});
            skLineSegment(sketch, "E1076", {"start": v(5469.33, -721.12) * mm, "end": v(5462.06, -711.65) * mm});
            skLineSegment(sketch, "E1077", {"start": v(5541.25, -711.66) * mm, "end": v(5533.99, -721.13) * mm});
            skLineSegment(sketch, "E1078", {"start": v(5489.82, -732.96) * mm, "end": v(5478.8, -728.4) * mm});
            skLineSegment(sketch, "E1079", {"start": v(5469.34, -656.47) * mm, "end": v(5478.8, -649.2) * mm});
            skLineSegment(sketch, "E1080", {"start": v(5513.49, -732.96) * mm, "end": v(5501.65, -734.52) * mm});
            skLineSegment(sketch, "E1081", {"start": v(5501.65, -734.52) * mm, "end": v(5500.27, -734.34) * mm});
            skLineSegment(sketch, "E1082", {"start": v(5547.38, -688.8) * mm, "end": v(5545.82, -700.64) * mm});
            skLineSegment(sketch, "E1083", {"start": v(5457.5, -676.96) * mm, "end": v(5462.07, -665.93) * mm});
            skLineSegment(sketch, "E1084", {"start": v(5533.99, -721.13) * mm, "end": v(5524.52, -728.4) * mm});
            skLineSegment(sketch, "E1085", {"start": v(5541.26, -665.94) * mm, "end": v(5545.83, -676.97) * mm});
            skLineSegment(sketch, "E1086", {"start": v(5545.83, -676.97) * mm, "end": v(5547.2, -687.36) * mm});
            skLineSegment(sketch, "E1087", {"start": v(5547.2, -687.36) * mm, "end": v(5547.38, -688.8) * mm});
            skLineSegment(sketch, "E1088", {"start": v(5524.52, -728.4) * mm, "end": v(5513.49, -732.96) * mm});
            skLineSegment(sketch, "E1089", {"start": v(5462.06, -711.65) * mm, "end": v(5457.5, -700.63) * mm});
            skLineSegment(sketch, "E1090", {"start": v(5524.53, -649.2) * mm, "end": v(5534, -656.47) * mm});
            skLineSegment(sketch, "E1091", {"start": v(5534, -656.47) * mm, "end": v(5541.26, -665.94) * mm});
            skLineSegment(sketch, "E1092", {"start": v(5455.94, -688.8) * mm, "end": v(5457.5, -676.96) * mm});
            skLineSegment(sketch, "E1093", {"start": v(5500.27, -734.34) * mm, "end": v(5489.82, -732.96) * mm});
            skLineSegment(sketch, "E1094", {"start": v(5489.83, -644.63) * mm, "end": v(5501.67, -643.08) * mm});
            skLineSegment(sketch, "E1095", {"start": v(5478.8, -728.4) * mm, "end": v(5469.33, -721.12) * mm});
            skLineSegment(sketch, "E1096", {"start": v(5513.5, -644.64) * mm, "end": v(5524.53, -649.2) * mm});
            skLineSegment(sketch, "E1097", {"start": v(5501.67, -643.08) * mm, "end": v(5513.5, -644.64) * mm});
            skLineSegment(sketch, "E1098", {"start": v(5462.07, -665.93) * mm, "end": v(5469.34, -656.47) * mm});
            skLineSegment(sketch, "E1099", {"start": v(5545.82, -700.64) * mm, "end": v(5541.25, -711.66) * mm});
            skLineSegment(sketch, "E1100", {"start": v(6613.66, -732) * mm, "end": v(6603.21, -730.62) * mm});
            skLineSegment(sketch, "E1101", {"start": v(6569.33, -686.45) * mm, "end": v(6570.89, -674.62) * mm});
            skLineSegment(sketch, "E1102", {"start": v(6592.2, -646.86) * mm, "end": v(6603.22, -642.3) * mm});
            skLineSegment(sketch, "E1103", {"start": v(6582.72, -718.78) * mm, "end": v(6575.45, -709.31) * mm});
            skLineSegment(sketch, "E1104", {"start": v(6654.64, -709.32) * mm, "end": v(6647.37, -718.79) * mm});
            skLineSegment(sketch, "E1105", {"start": v(6603.21, -730.62) * mm, "end": v(6592.18, -726.05) * mm});
            skLineSegment(sketch, "E1106", {"start": v(6582.73, -654.12) * mm, "end": v(6592.2, -646.86) * mm});
            skLineSegment(sketch, "E1107", {"start": v(6647.37, -718.79) * mm, "end": v(6637.9, -726.05) * mm});
            skLineSegment(sketch, "E1108", {"start": v(6570.89, -674.62) * mm, "end": v(6575.46, -663.6) * mm});
            skLineSegment(sketch, "E1109", {"start": v(6637.9, -726.05) * mm, "end": v(6626.88, -730.62) * mm});
            skLineSegment(sketch, "E1110", {"start": v(6575.45, -709.31) * mm, "end": v(6570.89, -698.28) * mm});
            skLineSegment(sketch, "E1111", {"start": v(6637.92, -646.87) * mm, "end": v(6647.38, -654.13) * mm});
            skLineSegment(sketch, "E1112", {"start": v(6647.38, -654.13) * mm, "end": v(6654.65, -663.6) * mm});
            skLineSegment(sketch, "E1113", {"start": v(6660.77, -686.46) * mm, "end": v(6659.21, -698.3) * mm});
            skLineSegment(sketch, "E1114", {"start": v(6615.04, -732.18) * mm, "end": v(6613.66, -732) * mm});
            skLineSegment(sketch, "E1115", {"start": v(6626.88, -730.62) * mm, "end": v(6617.78, -731.82) * mm});
            skLineSegment(sketch, "E1116", {"start": v(6615.06, -640.74) * mm, "end": v(6626.89, -642.3) * mm});
            skLineSegment(sketch, "E1117", {"start": v(6626.89, -642.3) * mm, "end": v(6637.92, -646.87) * mm});
            skLineSegment(sketch, "E1118", {"start": v(6575.46, -663.6) * mm, "end": v(6582.73, -654.12) * mm});
            skLineSegment(sketch, "E1119", {"start": v(6659.21, -698.3) * mm, "end": v(6654.64, -709.32) * mm});
            skLineSegment(sketch, "E1120", {"start": v(6570.89, -698.28) * mm, "end": v(6569.52, -687.87) * mm});
            skLineSegment(sketch, "E1121", {"start": v(6603.22, -642.3) * mm, "end": v(6615.06, -640.74) * mm});
            skLineSegment(sketch, "E1122", {"start": v(6654.65, -663.6) * mm, "end": v(6659.21, -674.63) * mm});
            skLineSegment(sketch, "E1123", {"start": v(6659.21, -674.63) * mm, "end": v(6660.58, -685.01) * mm});
            skLineSegment(sketch, "E1124", {"start": v(6660.58, -685.01) * mm, "end": v(6660.77, -686.46) * mm});
            skLineSegment(sketch, "E1125", {"start": v(6592.18, -726.05) * mm, "end": v(6582.72, -718.78) * mm});
            skLineSegment(sketch, "E1126", {"start": v(6617.78, -731.82) * mm, "end": v(6615.04, -732.18) * mm});
            skLineSegment(sketch, "E1127", {"start": v(6569.52, -687.87) * mm, "end": v(6569.33, -686.45) * mm});
            skLineSegment(sketch, "E1128", {"start": v(5477.13, -3114.07) * mm, "end": v(5467.66, -3106.8) * mm});
            skLineSegment(sketch, "E1129", {"start": v(5460.4, -3051.61) * mm, "end": v(5467.67, -3042.15) * mm});
            skLineSegment(sketch, "E1130", {"start": v(5544.16, -3062.65) * mm, "end": v(5545.52, -3073.04) * mm});
            skLineSegment(sketch, "E1131", {"start": v(5545.52, -3073.04) * mm, "end": v(5545.71, -3074.49) * mm});
            skLineSegment(sketch, "E1132", {"start": v(5511.83, -3030.32) * mm, "end": v(5522.86, -3034.89) * mm});
            skLineSegment(sketch, "E1133", {"start": v(5454.27, -3074.47) * mm, "end": v(5455.83, -3062.64) * mm});
            skLineSegment(sketch, "E1134", {"start": v(5477.14, -3034.88) * mm, "end": v(5488.17, -3030.32) * mm});
            skLineSegment(sketch, "E1135", {"start": v(5467.66, -3106.8) * mm, "end": v(5460.4, -3097.33) * mm});
            skLineSegment(sketch, "E1136", {"start": v(5539.58, -3097.35) * mm, "end": v(5532.32, -3106.81) * mm});
            skLineSegment(sketch, "E1137", {"start": v(5488.15, -3118.64) * mm, "end": v(5477.13, -3114.07) * mm});
            skLineSegment(sketch, "E1138", {"start": v(5467.67, -3042.15) * mm, "end": v(5477.14, -3034.88) * mm});
            skLineSegment(sketch, "E1139", {"start": v(5539.6, -3051.63) * mm, "end": v(5544.16, -3062.65) * mm});
            skLineSegment(sketch, "E1140", {"start": v(5455.83, -3086.3) * mm, "end": v(5454.27, -3074.47) * mm});
            skLineSegment(sketch, "E1141", {"start": v(5455.83, -3062.64) * mm, "end": v(5460.4, -3051.61) * mm});
            skLineSegment(sketch, "E1142", {"start": v(5500, -3028.76) * mm, "end": v(5511.83, -3030.32) * mm});
            skLineSegment(sketch, "E1143", {"start": v(5511.82, -3118.64) * mm, "end": v(5499.99, -3120.2) * mm});
            skLineSegment(sketch, "E1144", {"start": v(5488.17, -3030.32) * mm, "end": v(5500, -3028.76) * mm});
            skLineSegment(sketch, "E1145", {"start": v(5532.32, -3106.81) * mm, "end": v(5522.85, -3114.08) * mm});
            skLineSegment(sketch, "E1146", {"start": v(5522.85, -3114.08) * mm, "end": v(5511.82, -3118.64) * mm});
            skLineSegment(sketch, "E1147", {"start": v(5460.4, -3097.33) * mm, "end": v(5455.83, -3086.3) * mm});
            skLineSegment(sketch, "E1148", {"start": v(5544.15, -3086.32) * mm, "end": v(5539.58, -3097.35) * mm});
            skLineSegment(sketch, "E1149", {"start": v(5498.6, -3120.02) * mm, "end": v(5488.15, -3118.64) * mm});
            skLineSegment(sketch, "E1150", {"start": v(5522.86, -3034.89) * mm, "end": v(5532.33, -3042.16) * mm});
            skLineSegment(sketch, "E1151", {"start": v(5532.33, -3042.16) * mm, "end": v(5539.6, -3051.63) * mm});
            skLineSegment(sketch, "E1152", {"start": v(5499.99, -3120.2) * mm, "end": v(5498.6, -3120.02) * mm});
            skLineSegment(sketch, "E1153", {"start": v(5545.71, -3074.49) * mm, "end": v(5545.58, -3075.5) * mm});
            skLineSegment(sketch, "E1154", {"start": v(5545.58, -3075.5) * mm, "end": v(5544.15, -3086.32) * mm});
            skLineSegment(sketch, "E1155", {"start": v(6638.72, -3114.08) * mm, "end": v(6627.7, -3118.64) * mm});
            skLineSegment(sketch, "E1156", {"start": v(6576.27, -3097.33) * mm, "end": v(6571.7, -3086.3) * mm});
            skLineSegment(sketch, "E1157", {"start": v(6638.73, -3034.89) * mm, "end": v(6648.2, -3042.16) * mm});
            skLineSegment(sketch, "E1158", {"start": v(6648.2, -3042.16) * mm, "end": v(6655.46, -3051.63) * mm});
            skLineSegment(sketch, "E1159", {"start": v(6570.14, -3074.47) * mm, "end": v(6571.7, -3062.64) * mm});
            skLineSegment(sketch, "E1160", {"start": v(6593, -3034.88) * mm, "end": v(6604.04, -3030.32) * mm});
            skLineSegment(sketch, "E1161", {"start": v(6583.53, -3106.8) * mm, "end": v(6576.27, -3097.33) * mm});
            skLineSegment(sketch, "E1162", {"start": v(6655.46, -3097.35) * mm, "end": v(6648.19, -3106.81) * mm});
            skLineSegment(sketch, "E1163", {"start": v(6604.02, -3118.64) * mm, "end": v(6593, -3114.07) * mm});
            skLineSegment(sketch, "E1164", {"start": v(6583.54, -3042.15) * mm, "end": v(6593, -3034.88) * mm});
            skLineSegment(sketch, "E1165", {"start": v(6655.46, -3051.63) * mm, "end": v(6660.03, -3062.65) * mm});
            skLineSegment(sketch, "E1166", {"start": v(6660.03, -3062.65) * mm, "end": v(6661.4, -3073.04) * mm});
            skLineSegment(sketch, "E1167", {"start": v(6661.4, -3073.04) * mm, "end": v(6661.58, -3074.49) * mm});
            skLineSegment(sketch, "E1168", {"start": v(6627.7, -3030.32) * mm, "end": v(6638.73, -3034.89) * mm});
            skLineSegment(sketch, "E1169", {"start": v(6615.87, -3028.76) * mm, "end": v(6617.78, -3029.01) * mm});
            skLineSegment(sketch, "E1170", {"start": v(6627.7, -3118.64) * mm, "end": v(6615.86, -3120.2) * mm});
            skLineSegment(sketch, "E1171", {"start": v(6593, -3114.07) * mm, "end": v(6583.53, -3106.8) * mm});
            skLineSegment(sketch, "E1172", {"start": v(6571.7, -3086.3) * mm, "end": v(6570.28, -3075.5) * mm});
            skLineSegment(sketch, "E1173", {"start": v(6660.02, -3086.32) * mm, "end": v(6655.46, -3097.35) * mm});
            skLineSegment(sketch, "E1174", {"start": v(6604.04, -3030.32) * mm, "end": v(6615.87, -3028.76) * mm});
            skLineSegment(sketch, "E1175", {"start": v(6615.86, -3120.2) * mm, "end": v(6614.47, -3120.02) * mm});
            skLineSegment(sketch, "E1176", {"start": v(6661.58, -3074.49) * mm, "end": v(6660.02, -3086.32) * mm});
            skLineSegment(sketch, "E1177", {"start": v(6571.7, -3062.64) * mm, "end": v(6576.27, -3051.61) * mm});
            skLineSegment(sketch, "E1178", {"start": v(6648.19, -3106.81) * mm, "end": v(6638.72, -3114.08) * mm});
            skLineSegment(sketch, "E1179", {"start": v(6576.27, -3051.61) * mm, "end": v(6583.54, -3042.15) * mm});
            skLineSegment(sketch, "E1180", {"start": v(6614.47, -3120.02) * mm, "end": v(6604.02, -3118.64) * mm});
            skLineSegment(sketch, "E1181", {"start": v(6617.78, -3029.01) * mm, "end": v(6627.7, -3030.32) * mm});
            skLineSegment(sketch, "E1182", {"start": v(6570.28, -3075.5) * mm, "end": v(6570.14, -3074.47) * mm});
            skLineSegment(sketch, "E1183", {"start": v(5542.26, -827.76) * mm, "end": v(5571.47, -827.76) * mm});
            skLineSegment(sketch, "E1184", {"start": v(5542.26, -799.82) * mm, "end": v(5571.47, -799.82) * mm});
            skLineSegment(sketch, "E1185", {"start": v(5571.47, -771.88) * mm, "end": v(5542.26, -771.88) * mm});
            skLineSegment(sketch, "E1186", {"start": v(5571.47, -771.88) * mm, "end": v(5571.47, -799.82) * mm});
            skLineSegment(sketch, "E1187", {"start": v(5571.47, -799.82) * mm, "end": v(5571.47, -827.76) * mm});
            skLineSegment(sketch, "E1188", {"start": v(6549.66, -783.3) * mm, "end": v(6549.66, -811.24) * mm});
            skLineSegment(sketch, "E1189", {"start": v(6549.66, -783.3) * mm, "end": v(6520.45, -783.3) * mm});
            skLineSegment(sketch, "E1190", {"start": v(6549.66, -811.24) * mm, "end": v(6549.66, -839.18) * mm});
            skLineSegment(sketch, "E1191", {"start": v(6520.45, -839.18) * mm, "end": v(6549.66, -839.18) * mm});
            skLineSegment(sketch, "E1192", {"start": v(6520.45, -811.24) * mm, "end": v(6549.66, -811.24) * mm});
            skLineSegment(sketch, "E1193", {"start": v(6499.1, -2953.14) * mm, "end": v(6528.32, -2953.14) * mm});
            skLineSegment(sketch, "E1194", {"start": v(6528.32, -2925.2) * mm, "end": v(6528.32, -2953.14) * mm});
            skLineSegment(sketch, "E1195", {"start": v(6499.1, -2981.08) * mm, "end": v(6528.32, -2981.08) * mm});
            skLineSegment(sketch, "E1196", {"start": v(6528.32, -2925.2) * mm, "end": v(6499.1, -2925.2) * mm});
            skLineSegment(sketch, "E1197", {"start": v(6528.32, -2953.14) * mm, "end": v(6528.32, -2981.08) * mm});
            skLineSegment(sketch, "E1198", {"start": v(5615.71, -2915.96) * mm, "end": v(5615.71, -2943.9) * mm});
            skLineSegment(sketch, "E1199", {"start": v(5615.71, -2915.96) * mm, "end": v(5586.5, -2915.96) * mm});
            skLineSegment(sketch, "E1200", {"start": v(5615.71, -2943.9) * mm, "end": v(5615.71, -2971.84) * mm});
            skLineSegment(sketch, "E1201", {"start": v(5586.5, -2971.84) * mm, "end": v(5615.71, -2971.84) * mm});
            skLineSegment(sketch, "E1202", {"start": v(5586.5, -2943.9) * mm, "end": v(5615.71, -2943.9) * mm});
            skLineSegment(sketch, "E1203", {"start": v(-5572.34, -2020.04) * mm, "end": v(-5572.34, -2157.66) * mm});
            skLineSegment(sketch, "E1204", {"start": v(-5572.34, -2157.66) * mm, "end": v(-5571.25, -2164.12) * mm});
            skLineSegment(sketch, "E1205", {"start": v(-5571.25, -2164.12) * mm, "end": v(-5567.96, -2168.74) * mm});
            skLineSegment(sketch, "E1206", {"start": v(-5567.96, -2168.74) * mm, "end": v(-5562.47, -2171.51) * mm});
            skLineSegment(sketch, "E1207", {"start": v(-5562.47, -2171.51) * mm, "end": v(-5554.8, -2172.44) * mm});
            skLineSegment(sketch, "E1208", {"start": v(-5554.8, -2172.44) * mm, "end": v(-5545.56, -2172.44) * mm});
            skLineSegment(sketch, "E1209", {"start": v(-5545.56, -2172.44) * mm, "end": v(-5545.56, -2177.98) * mm});
            skLineSegment(sketch, "E1210", {"start": v(-5545.56, -2177.98) * mm, "end": v(-5612.98, -2177.98) * mm});
            skLineSegment(sketch, "E1211", {"start": v(-5612.98, -2177.98) * mm, "end": v(-5612.98, -2172.44) * mm});
            skLineSegment(sketch, "E1212", {"start": v(-5612.98, -2172.44) * mm, "end": v(-5604.67, -2172.44) * mm});
            skLineSegment(sketch, "E1213", {"start": v(-5604.67, -2172.44) * mm, "end": v(-5597, -2171.51) * mm});
            skLineSegment(sketch, "E1214", {"start": v(-5597, -2171.51) * mm, "end": v(-5591.51, -2168.74) * mm});
            skLineSegment(sketch, "E1215", {"start": v(-5591.51, -2168.74) * mm, "end": v(-5588.22, -2164.12) * mm});
            skLineSegment(sketch, "E1216", {"start": v(-5588.22, -2164.12) * mm, "end": v(-5587.12, -2157.66) * mm});
            skLineSegment(sketch, "E1217", {"start": v(-5587.12, -2157.66) * mm, "end": v(-5587.12, -2048.67) * mm});
            skLineSegment(sketch, "E1218", {"start": v(-5587.12, -2048.67) * mm, "end": v(-5589.43, -2042.44) * mm});
            skLineSegment(sketch, "E1219", {"start": v(-5589.43, -2042.44) * mm, "end": v(-5596.36, -2040.36) * mm});
            skLineSegment(sketch, "E1220", {"start": v(-5596.36, -2040.36) * mm, "end": v(-5612.98, -2040.36) * mm});
            skLineSegment(sketch, "E1221", {"start": v(-5612.98, -2040.36) * mm, "end": v(-5612.98, -2034.82) * mm});
            skLineSegment(sketch, "E1222", {"start": v(-5612.98, -2034.82) * mm, "end": v(-5604.67, -2034.82) * mm});
            skLineSegment(sketch, "E1223", {"start": v(-5604.67, -2034.82) * mm, "end": v(-5594.92, -2033.9) * mm});
            skLineSegment(sketch, "E1224", {"start": v(-5594.92, -2033.9) * mm, "end": v(-5586.9, -2031.12) * mm});
            skLineSegment(sketch, "E1225", {"start": v(-5586.9, -2031.12) * mm, "end": v(-5580.6, -2026.5) * mm});
            skLineSegment(sketch, "E1226", {"start": v(-5580.6, -2026.5) * mm, "end": v(-5576.04, -2020.04) * mm});
            skLineSegment(sketch, "E1227", {"start": v(-5576.04, -2020.04) * mm, "end": v(-5572.34, -2020.04) * mm});
            skLineSegment(sketch, "E1228", {"start": v(-5395.93, -2077.3) * mm, "end": v(-5395.93, -2068.99) * mm});
            skLineSegment(sketch, "E1229", {"start": v(-5395.93, -2068.99) * mm, "end": v(-5293.4, -2068.99) * mm});
            skLineSegment(sketch, "E1230", {"start": v(-5293.4, -2068.99) * mm, "end": v(-5293.4, -2077.3) * mm});
            skLineSegment(sketch, "E1231", {"start": v(-5293.4, -2077.3) * mm, "end": v(-5395.93, -2077.3) * mm});
            skLineSegment(sketch, "E1232", {"start": v(-5395.93, -2124.4) * mm, "end": v(-5395.93, -2116.1) * mm});
            skLineSegment(sketch, "E1233", {"start": v(-5395.93, -2116.1) * mm, "end": v(-5293.4, -2116.1) * mm});
            skLineSegment(sketch, "E1234", {"start": v(-5293.4, -2116.1) * mm, "end": v(-5293.4, -2124.4) * mm});
            skLineSegment(sketch, "E1235", {"start": v(-5293.4, -2124.4) * mm, "end": v(-5395.93, -2124.4) * mm});
            skLineSegment(sketch, "E1236", {"start": v(-5106.83, -2020.04) * mm, "end": v(-5095.98, -2020.73) * mm});
            skLineSegment(sketch, "E1237", {"start": v(-5095.98, -2020.73) * mm, "end": v(-5086.51, -2022.8) * mm});
            skLineSegment(sketch, "E1238", {"start": v(-5086.51, -2022.8) * mm, "end": v(-5078.43, -2026.27) * mm});
            skLineSegment(sketch, "E1239", {"start": v(-5078.43, -2026.27) * mm, "end": v(-5071.73, -2031.12) * mm});
            skLineSegment(sketch, "E1240", {"start": v(-5071.73, -2031.12) * mm, "end": v(-5064.8, -2042.2) * mm});
            skLineSegment(sketch, "E1241", {"start": v(-5064.8, -2042.2) * mm, "end": v(-5062.5, -2056.98) * mm});
            skLineSegment(sketch, "E1242", {"start": v(-5062.5, -2056.98) * mm, "end": v(-5065.04, -2072.68) * mm});
            skLineSegment(sketch, "E1243", {"start": v(-5065.04, -2072.68) * mm, "end": v(-5068.21, -2079.15) * mm});
            skLineSegment(sketch, "E1244", {"start": v(-5068.21, -2079.15) * mm, "end": v(-5072.66, -2084.7) * mm});
            skLineSegment(sketch, "E1245", {"start": v(-5072.66, -2084.7) * mm, "end": v(-5083.51, -2093) * mm});
            skLineSegment(sketch, "E1246", {"start": v(-5083.51, -2093) * mm, "end": v(-5095.75, -2097.62) * mm});
            skLineSegment(sketch, "E1247", {"start": v(-5095.75, -2097.62) * mm, "end": v(-5068.04, -2165.97) * mm});
            skLineSegment(sketch, "E1248", {"start": v(-5068.04, -2165.97) * mm, "end": v(-5063.88, -2170.82) * mm});
            skLineSegment(sketch, "E1249", {"start": v(-5063.88, -2170.82) * mm, "end": v(-5058.8, -2172.44) * mm});
            skLineSegment(sketch, "E1250", {"start": v(-5058.8, -2172.44) * mm, "end": v(-5053.26, -2172.44) * mm});
            skLineSegment(sketch, "E1251", {"start": v(-5053.26, -2172.44) * mm, "end": v(-5053.26, -2177.98) * mm});
            skLineSegment(sketch, "E1252", {"start": v(-5053.26, -2177.98) * mm, "end": v(-5079.12, -2177.98) * mm});
            skLineSegment(sketch, "E1253", {"start": v(-5079.12, -2177.98) * mm, "end": v(-5109.6, -2098.55) * mm});
            skLineSegment(sketch, "E1254", {"start": v(-5109.6, -2098.55) * mm, "end": v(-5130.85, -2098.55) * mm});
            skLineSegment(sketch, "E1255", {"start": v(-5130.85, -2098.55) * mm, "end": v(-5130.85, -2165.05) * mm});
            skLineSegment(sketch, "E1256", {"start": v(-5130.85, -2165.05) * mm, "end": v(-5128.77, -2170.59) * mm});
            skLineSegment(sketch, "E1257", {"start": v(-5128.77, -2170.59) * mm, "end": v(-5122.53, -2172.44) * mm});
            skLineSegment(sketch, "E1258", {"start": v(-5122.53, -2172.44) * mm, "end": v(-5117, -2172.44) * mm});
            skLineSegment(sketch, "E1259", {"start": v(-5117, -2172.44) * mm, "end": v(-5117, -2177.98) * mm});
            skLineSegment(sketch, "E1260", {"start": v(-5117, -2177.98) * mm, "end": v(-5159.48, -2177.98) * mm});
            skLineSegment(sketch, "E1261", {"start": v(-5159.48, -2177.98) * mm, "end": v(-5159.48, -2172.44) * mm});
            skLineSegment(sketch, "E1262", {"start": v(-5159.48, -2172.44) * mm, "end": v(-5153.94, -2172.44) * mm});
            skLineSegment(sketch, "E1263", {"start": v(-5153.94, -2172.44) * mm, "end": v(-5147.7, -2170.59) * mm});
            skLineSegment(sketch, "E1264", {"start": v(-5147.7, -2170.59) * mm, "end": v(-5145.62, -2165.05) * mm});
            skLineSegment(sketch, "E1265", {"start": v(-5145.62, -2165.05) * mm, "end": v(-5145.62, -2032.97) * mm});
            skLineSegment(sketch, "E1266", {"start": v(-5145.62, -2032.97) * mm, "end": v(-5147.7, -2027.43) * mm});
            skLineSegment(sketch, "E1267", {"start": v(-5147.7, -2027.43) * mm, "end": v(-5153.94, -2025.58) * mm});
            skLineSegment(sketch, "E1268", {"start": v(-5153.94, -2025.58) * mm, "end": v(-5159.48, -2025.58) * mm});
            skLineSegment(sketch, "E1269", {"start": v(-5159.48, -2025.58) * mm, "end": v(-5159.48, -2020.04) * mm});
            skLineSegment(sketch, "E1270", {"start": v(-5159.48, -2020.04) * mm, "end": v(-5106.83, -2020.04) * mm});
            skLineSegment(sketch, "E1271", {"start": v(-5130.85, -2093) * mm, "end": v(-5110.53, -2093) * mm});
            skLineSegment(sketch, "E1272", {"start": v(-5110.53, -2093) * mm, "end": v(-5097.13, -2090.7) * mm});
            skLineSegment(sketch, "E1273", {"start": v(-5097.13, -2090.7) * mm, "end": v(-5086.51, -2083.77) * mm});
            skLineSegment(sketch, "E1274", {"start": v(-5086.51, -2083.77) * mm, "end": v(-5080.28, -2073.38) * mm});
            skLineSegment(sketch, "E1275", {"start": v(-5080.28, -2073.38) * mm, "end": v(-5078.2, -2058.83) * mm});
            skLineSegment(sketch, "E1276", {"start": v(-5078.2, -2058.83) * mm, "end": v(-5080.28, -2044.28) * mm});
            skLineSegment(sketch, "E1277", {"start": v(-5080.28, -2044.28) * mm, "end": v(-5086.51, -2033.9) * mm});
            skLineSegment(sketch, "E1278", {"start": v(-5086.51, -2033.9) * mm, "end": v(-5097.6, -2027.66) * mm});
            skLineSegment(sketch, "E1279", {"start": v(-5097.6, -2027.66) * mm, "end": v(-5112.37, -2025.58) * mm});
            skLineSegment(sketch, "E1280", {"start": v(-5112.37, -2025.58) * mm, "end": v(-5122.53, -2025.58) * mm});
            skLineSegment(sketch, "E1281", {"start": v(-5122.53, -2025.58) * mm, "end": v(-5128.77, -2027.43) * mm});
            skLineSegment(sketch, "E1282", {"start": v(-5128.77, -2027.43) * mm, "end": v(-5130.85, -2032.97) * mm});
            skLineSegment(sketch, "E1283", {"start": v(-5130.85, -2032.97) * mm, "end": v(-5130.85, -2093) * mm});
            skLineSegment(sketch, "E1284", {"start": v(-4973.83, -2120.71) * mm, "end": v(-5015.4, -2120.71) * mm});
            skLineSegment(sketch, "E1285", {"start": v(-5015.4, -2120.71) * mm, "end": v(-5023.7, -2153.96) * mm});
            skLineSegment(sketch, "E1286", {"start": v(-5023.7, -2153.96) * mm, "end": v(-5024.92, -2162.05) * mm});
            skLineSegment(sketch, "E1287", {"start": v(-5024.92, -2162.05) * mm, "end": v(-5023.94, -2167.82) * mm});
            skLineSegment(sketch, "E1288", {"start": v(-5023.94, -2167.82) * mm, "end": v(-5020.76, -2171.28) * mm});
            skLineSegment(sketch, "E1289", {"start": v(-5020.76, -2171.28) * mm, "end": v(-5015.4, -2172.44) * mm});
            skLineSegment(sketch, "E1290", {"start": v(-5015.4, -2172.44) * mm, "end": v(-5012.62, -2172.44) * mm});
            skLineSegment(sketch, "E1291", {"start": v(-5012.62, -2172.44) * mm, "end": v(-5012.62, -2177.98) * mm});
            skLineSegment(sketch, "E1292", {"start": v(-5012.62, -2177.98) * mm, "end": v(-5046.8, -2177.98) * mm});
            skLineSegment(sketch, "E1293", {"start": v(-5046.8, -2177.98) * mm, "end": v(-5046.8, -2172.44) * mm});
            skLineSegment(sketch, "E1294", {"start": v(-5046.8, -2172.44) * mm, "end": v(-5044.02, -2172.44) * mm});
            skLineSegment(sketch, "E1295", {"start": v(-5044.02, -2172.44) * mm, "end": v(-5038.25, -2169.9) * mm});
            skLineSegment(sketch, "E1296", {"start": v(-5038.25, -2169.9) * mm, "end": v(-5033.86, -2162.28) * mm});
            skLineSegment(sketch, "E1297", {"start": v(-5033.86, -2162.28) * mm, "end": v(-4997.84, -2024.66) * mm});
            skLineSegment(sketch, "E1298", {"start": v(-4997.84, -2024.66) * mm, "end": v(-4983.99, -2020.04) * mm});
            skLineSegment(sketch, "E1299", {"start": v(-4983.99, -2020.04) * mm, "end": v(-4948.9, -2162.28) * mm});
            skLineSegment(sketch, "E1300", {"start": v(-4948.9, -2162.28) * mm, "end": v(-4944.27, -2169.9) * mm});
            skLineSegment(sketch, "E1301", {"start": v(-4944.27, -2169.9) * mm, "end": v(-4937.8, -2172.44) * mm});
            skLineSegment(sketch, "E1302", {"start": v(-4937.8, -2172.44) * mm, "end": v(-4935.04, -2172.44) * mm});
            skLineSegment(sketch, "E1303", {"start": v(-4935.04, -2172.44) * mm, "end": v(-4935.04, -2177.98) * mm});
            skLineSegment(sketch, "E1304", {"start": v(-4935.04, -2177.98) * mm, "end": v(-4974.75, -2177.98) * mm});
            skLineSegment(sketch, "E1305", {"start": v(-4974.75, -2177.98) * mm, "end": v(-4974.75, -2172.44) * mm});
            skLineSegment(sketch, "E1306", {"start": v(-4974.75, -2172.44) * mm, "end": v(-4971.06, -2172.44) * mm});
            skLineSegment(sketch, "E1307", {"start": v(-4971.06, -2172.44) * mm, "end": v(-4966.84, -2171.63) * mm});
            skLineSegment(sketch, "E1308", {"start": v(-4966.84, -2171.63) * mm, "end": v(-4964.36, -2169.2) * mm});
            skLineSegment(sketch, "E1309", {"start": v(-4964.36, -2169.2) * mm, "end": v(-4963.61, -2165.16) * mm});
            skLineSegment(sketch, "E1310", {"start": v(-4963.61, -2165.16) * mm, "end": v(-4964.6, -2159.5) * mm});
            skLineSegment(sketch, "E1311", {"start": v(-4964.6, -2159.5) * mm, "end": v(-4973.83, -2120.71) * mm});
            skLineSegment(sketch, "E1312", {"start": v(-4993.22, -2038.5) * mm, "end": v(-4994.15, -2038.5) * mm});
            skLineSegment(sketch, "E1313", {"start": v(-4994.15, -2038.5) * mm, "end": v(-5013.54, -2115.17) * mm});
            skLineSegment(sketch, "E1314", {"start": v(-5013.54, -2115.17) * mm, "end": v(-4974.75, -2115.17) * mm});
            skLineSegment(sketch, "E1315", {"start": v(-4974.75, -2115.17) * mm, "end": v(-4993.22, -2038.5) * mm});
            skLineSegment(sketch, "E1316", {"start": v(-4826.97, -2165.05) * mm, "end": v(-4824.9, -2170.59) * mm});
            skLineSegment(sketch, "E1317", {"start": v(-4824.9, -2170.59) * mm, "end": v(-4818.66, -2172.44) * mm});
            skLineSegment(sketch, "E1318", {"start": v(-4818.66, -2172.44) * mm, "end": v(-4814.96, -2172.44) * mm});
            skLineSegment(sketch, "E1319", {"start": v(-4814.96, -2172.44) * mm, "end": v(-4814.96, -2177.98) * mm});
            skLineSegment(sketch, "E1320", {"start": v(-4814.96, -2177.98) * mm, "end": v(-4854.68, -2177.98) * mm});
            skLineSegment(sketch, "E1321", {"start": v(-4854.68, -2177.98) * mm, "end": v(-4854.68, -2172.44) * mm});
            skLineSegment(sketch, "E1322", {"start": v(-4854.68, -2172.44) * mm, "end": v(-4850.06, -2172.44) * mm});
            skLineSegment(sketch, "E1323", {"start": v(-4850.06, -2172.44) * mm, "end": v(-4843.83, -2170.59) * mm});
            skLineSegment(sketch, "E1324", {"start": v(-4843.83, -2170.59) * mm, "end": v(-4841.75, -2165.05) * mm});
            skLineSegment(sketch, "E1325", {"start": v(-4841.75, -2165.05) * mm, "end": v(-4841.75, -2044.05) * mm});
            skLineSegment(sketch, "E1326", {"start": v(-4841.75, -2044.05) * mm, "end": v(-4843.6, -2044.05) * mm});
            skLineSegment(sketch, "E1327", {"start": v(-4843.6, -2044.05) * mm, "end": v(-4875, -2177.98) * mm});
            skLineSegment(sketch, "E1328", {"start": v(-4875, -2177.98) * mm, "end": v(-4880.54, -2177.98) * mm});
            skLineSegment(sketch, "E1329", {"start": v(-4880.54, -2177.98) * mm, "end": v(-4909.17, -2046.82) * mm});
            skLineSegment(sketch, "E1330", {"start": v(-4909.17, -2046.82) * mm, "end": v(-4911.02, -2046.82) * mm});
            skLineSegment(sketch, "E1331", {"start": v(-4911.02, -2046.82) * mm, "end": v(-4911.02, -2165.05) * mm});
            skLineSegment(sketch, "E1332", {"start": v(-4911.02, -2165.05) * mm, "end": v(-4908.94, -2170.59) * mm});
            skLineSegment(sketch, "E1333", {"start": v(-4908.94, -2170.59) * mm, "end": v(-4902.7, -2172.44) * mm});
            skLineSegment(sketch, "E1334", {"start": v(-4902.7, -2172.44) * mm, "end": v(-4899.94, -2172.44) * mm});
            skLineSegment(sketch, "E1335", {"start": v(-4899.94, -2172.44) * mm, "end": v(-4899.94, -2177.98) * mm});
            skLineSegment(sketch, "E1336", {"start": v(-4899.94, -2177.98) * mm, "end": v(-4927.65, -2177.98) * mm});
            skLineSegment(sketch, "E1337", {"start": v(-4927.65, -2177.98) * mm, "end": v(-4927.65, -2172.44) * mm});
            skLineSegment(sketch, "E1338", {"start": v(-4927.65, -2172.44) * mm, "end": v(-4924.88, -2172.44) * mm});
            skLineSegment(sketch, "E1339", {"start": v(-4924.88, -2172.44) * mm, "end": v(-4918.64, -2170.59) * mm});
            skLineSegment(sketch, "E1340", {"start": v(-4918.64, -2170.59) * mm, "end": v(-4916.56, -2165.05) * mm});
            skLineSegment(sketch, "E1341", {"start": v(-4916.56, -2165.05) * mm, "end": v(-4916.56, -2032.97) * mm});
            skLineSegment(sketch, "E1342", {"start": v(-4916.56, -2032.97) * mm, "end": v(-4918.64, -2027.43) * mm});
            skLineSegment(sketch, "E1343", {"start": v(-4918.64, -2027.43) * mm, "end": v(-4924.88, -2025.58) * mm});
            skLineSegment(sketch, "E1344", {"start": v(-4924.88, -2025.58) * mm, "end": v(-4928.57, -2025.58) * mm});
            skLineSegment(sketch, "E1345", {"start": v(-4928.57, -2025.58) * mm, "end": v(-4928.57, -2020.04) * mm});
            skLineSegment(sketch, "E1346", {"start": v(-4928.57, -2020.04) * mm, "end": v(-4901.78, -2020.04) * mm});
            skLineSegment(sketch, "E1347", {"start": v(-4901.78, -2020.04) * mm, "end": v(-4875, -2143.8) * mm});
            skLineSegment(sketch, "E1348", {"start": v(-4875, -2143.8) * mm, "end": v(-4873.15, -2143.8) * mm});
            skLineSegment(sketch, "E1349", {"start": v(-4873.15, -2143.8) * mm, "end": v(-4844.52, -2020.04) * mm});
            skLineSegment(sketch, "E1350", {"start": v(-4844.52, -2020.04) * mm, "end": v(-4814.96, -2020.04) * mm});
            skLineSegment(sketch, "E1351", {"start": v(-4814.96, -2020.04) * mm, "end": v(-4814.96, -2025.58) * mm});
            skLineSegment(sketch, "E1352", {"start": v(-4814.96, -2025.58) * mm, "end": v(-4818.66, -2025.58) * mm});
            skLineSegment(sketch, "E1353", {"start": v(-4818.66, -2025.58) * mm, "end": v(-4824.9, -2027.43) * mm});
            skLineSegment(sketch, "E1354", {"start": v(-4824.9, -2027.43) * mm, "end": v(-4826.97, -2032.97) * mm});
            skLineSegment(sketch, "E1355", {"start": v(-4826.97, -2032.97) * mm, "end": v(-4826.97, -2165.05) * mm});
            skLineSegment(sketch, "E1356", {"start": v(-4777.1, -2104.09) * mm, "end": v(-4777.1, -2165.05) * mm});
            skLineSegment(sketch, "E1357", {"start": v(-4777.1, -2165.05) * mm, "end": v(-4775.02, -2170.59) * mm});
            skLineSegment(sketch, "E1358", {"start": v(-4775.02, -2170.59) * mm, "end": v(-4768.78, -2172.44) * mm});
            skLineSegment(sketch, "E1359", {"start": v(-4768.78, -2172.44) * mm, "end": v(-4762.32, -2172.44) * mm});
            skLineSegment(sketch, "E1360", {"start": v(-4762.32, -2172.44) * mm, "end": v(-4762.32, -2177.98) * mm});
            skLineSegment(sketch, "E1361", {"start": v(-4762.32, -2177.98) * mm, "end": v(-4806.65, -2177.98) * mm});
            skLineSegment(sketch, "E1362", {"start": v(-4806.65, -2177.98) * mm, "end": v(-4806.65, -2172.44) * mm});
            skLineSegment(sketch, "E1363", {"start": v(-4806.65, -2172.44) * mm, "end": v(-4800.18, -2172.44) * mm});
            skLineSegment(sketch, "E1364", {"start": v(-4800.18, -2172.44) * mm, "end": v(-4793.95, -2170.59) * mm});
            skLineSegment(sketch, "E1365", {"start": v(-4793.95, -2170.59) * mm, "end": v(-4791.87, -2165.05) * mm});
            skLineSegment(sketch, "E1366", {"start": v(-4791.87, -2165.05) * mm, "end": v(-4791.87, -2032.97) * mm});
            skLineSegment(sketch, "E1367", {"start": v(-4791.87, -2032.97) * mm, "end": v(-4793.95, -2027.43) * mm});
            skLineSegment(sketch, "E1368", {"start": v(-4793.95, -2027.43) * mm, "end": v(-4800.18, -2025.58) * mm});
            skLineSegment(sketch, "E1369", {"start": v(-4800.18, -2025.58) * mm, "end": v(-4805.73, -2025.58) * mm});
            skLineSegment(sketch, "E1370", {"start": v(-4805.73, -2025.58) * mm, "end": v(-4805.73, -2020.04) * mm});
            skLineSegment(sketch, "E1371", {"start": v(-4805.73, -2020.04) * mm, "end": v(-4751.23, -2020.04) * mm});
            skLineSegment(sketch, "E1372", {"start": v(-4751.23, -2020.04) * mm, "end": v(-4739.92, -2020.79) * mm});
            skLineSegment(sketch, "E1373", {"start": v(-4739.92, -2020.79) * mm, "end": v(-4729.99, -2023.04) * mm});
            skLineSegment(sketch, "E1374", {"start": v(-4729.99, -2023.04) * mm, "end": v(-4721.44, -2026.8) * mm});
            skLineSegment(sketch, "E1375", {"start": v(-4721.44, -2026.8) * mm, "end": v(-4714.29, -2032.04) * mm});
            skLineSegment(sketch, "E1376", {"start": v(-4714.29, -2032.04) * mm, "end": v(-4709.44, -2038) * mm});
            skLineSegment(sketch, "E1377", {"start": v(-4709.44, -2038) * mm, "end": v(-4705.97, -2044.74) * mm});
            skLineSegment(sketch, "E1378", {"start": v(-4705.97, -2044.74) * mm, "end": v(-4703.2, -2060.68) * mm});
            skLineSegment(sketch, "E1379", {"start": v(-4703.2, -2060.68) * mm, "end": v(-4705.97, -2077.3) * mm});
            skLineSegment(sketch, "E1380", {"start": v(-4705.97, -2077.3) * mm, "end": v(-4709.44, -2084.23) * mm});
            skLineSegment(sketch, "E1381", {"start": v(-4709.44, -2084.23) * mm, "end": v(-4714.29, -2090.23) * mm});
            skLineSegment(sketch, "E1382", {"start": v(-4714.29, -2090.23) * mm, "end": v(-4721.62, -2096.3) * mm});
            skLineSegment(sketch, "E1383", {"start": v(-4721.62, -2096.3) * mm, "end": v(-4729.76, -2100.62) * mm});
            skLineSegment(sketch, "E1384", {"start": v(-4729.76, -2100.62) * mm, "end": v(-4738.7, -2103.22) * mm});
            skLineSegment(sketch, "E1385", {"start": v(-4738.7, -2103.22) * mm, "end": v(-4748.46, -2104.09) * mm});
            skLineSegment(sketch, "E1386", {"start": v(-4748.46, -2104.09) * mm, "end": v(-4777.1, -2104.09) * mm});
            skLineSegment(sketch, "E1387", {"start": v(-4754, -2098.55) * mm, "end": v(-4739.92, -2096.24) * mm});
            skLineSegment(sketch, "E1388", {"start": v(-4739.92, -2096.24) * mm, "end": v(-4729.06, -2089.3) * mm});
            skLineSegment(sketch, "E1389", {"start": v(-4729.06, -2089.3) * mm, "end": v(-4724.62, -2084.11) * mm});
            skLineSegment(sketch, "E1390", {"start": v(-4724.62, -2084.11) * mm, "end": v(-4721.44, -2077.76) * mm});
            skLineSegment(sketch, "E1391", {"start": v(-4721.44, -2077.76) * mm, "end": v(-4718.9, -2061.6) * mm});
            skLineSegment(sketch, "E1392", {"start": v(-4718.9, -2061.6) * mm, "end": v(-4721.44, -2045.44) * mm});
            skLineSegment(sketch, "E1393", {"start": v(-4721.44, -2045.44) * mm, "end": v(-4724.62, -2039.09) * mm});
            skLineSegment(sketch, "E1394", {"start": v(-4724.62, -2039.09) * mm, "end": v(-4729.06, -2033.9) * mm});
            skLineSegment(sketch, "E1395", {"start": v(-4729.06, -2033.9) * mm, "end": v(-4733.86, -2030.25) * mm});
            skLineSegment(sketch, "E1396", {"start": v(-4733.86, -2030.25) * mm, "end": v(-4739.92, -2027.66) * mm});
            skLineSegment(sketch, "E1397", {"start": v(-4739.92, -2027.66) * mm, "end": v(-4755.85, -2025.58) * mm});
            skLineSegment(sketch, "E1398", {"start": v(-4755.85, -2025.58) * mm, "end": v(-4768.78, -2025.58) * mm});
            skLineSegment(sketch, "E1399", {"start": v(-4768.78, -2025.58) * mm, "end": v(-4775.02, -2027.43) * mm});
            skLineSegment(sketch, "E1400", {"start": v(-4775.02, -2027.43) * mm, "end": v(-4777.1, -2032.97) * mm});
            skLineSegment(sketch, "E1401", {"start": v(-4777.1, -2032.97) * mm, "end": v(-4777.1, -2098.55) * mm});
            skLineSegment(sketch, "E1402", {"start": v(-4777.1, -2098.55) * mm, "end": v(-4754, -2098.55) * mm});
            skLineSegment(sketch, "E1403", {"start": v(-4602.53, -2137.34) * mm, "end": v(-4604.6, -2129.03) * mm});
            skLineSegment(sketch, "E1404", {"start": v(-4604.6, -2129.03) * mm, "end": v(-4610.84, -2120.71) * mm});
            skLineSegment(sketch, "E1405", {"start": v(-4610.84, -2120.71) * mm, "end": v(-4625.39, -2108.94) * mm});
            skLineSegment(sketch, "E1406", {"start": v(-4625.39, -2108.94) * mm, "end": v(-4643.17, -2099.47) * mm});
            skLineSegment(sketch, "E1407", {"start": v(-4643.17, -2099.47) * mm, "end": v(-4660.02, -2091.39) * mm});
            skLineSegment(sketch, "E1408", {"start": v(-4660.02, -2091.39) * mm, "end": v(-4671.8, -2083.77) * mm});
            skLineSegment(sketch, "E1409", {"start": v(-4671.8, -2083.77) * mm, "end": v(-4676.24, -2079.1) * mm});
            skLineSegment(sketch, "E1410", {"start": v(-4676.24, -2079.1) * mm, "end": v(-4679.42, -2073.38) * mm});
            skLineSegment(sketch, "E1411", {"start": v(-4679.42, -2073.38) * mm, "end": v(-4681.96, -2058.83) * mm});
            skLineSegment(sketch, "E1412", {"start": v(-4681.96, -2058.83) * mm, "end": v(-4681.2, -2051.2) * mm});
            skLineSegment(sketch, "E1413", {"start": v(-4681.2, -2051.2) * mm, "end": v(-4678.96, -2044.05) * mm});
            skLineSegment(sketch, "E1414", {"start": v(-4678.96, -2044.05) * mm, "end": v(-4669.95, -2031.12) * mm});
            skLineSegment(sketch, "E1415", {"start": v(-4669.95, -2031.12) * mm, "end": v(-4663.78, -2026.27) * mm});
            skLineSegment(sketch, "E1416", {"start": v(-4663.78, -2026.27) * mm, "end": v(-4656.33, -2022.8) * mm});
            skLineSegment(sketch, "E1417", {"start": v(-4656.33, -2022.8) * mm, "end": v(-4647.61, -2020.73) * mm});
            skLineSegment(sketch, "E1418", {"start": v(-4647.61, -2020.73) * mm, "end": v(-4637.62, -2020.04) * mm});
            skLineSegment(sketch, "E1419", {"start": v(-4637.62, -2020.04) * mm, "end": v(-4627.93, -2020.96) * mm});
            skLineSegment(sketch, "E1420", {"start": v(-4627.93, -2020.96) * mm, "end": v(-4619.15, -2023.73) * mm});
            skLineSegment(sketch, "E1421", {"start": v(-4619.15, -2023.73) * mm, "end": v(-4608.07, -2026.5) * mm});
            skLineSegment(sketch, "E1422", {"start": v(-4608.07, -2026.5) * mm, "end": v(-4603.45, -2024.89) * mm});
            skLineSegment(sketch, "E1423", {"start": v(-4603.45, -2024.89) * mm, "end": v(-4598.83, -2020.04) * mm});
            skLineSegment(sketch, "E1424", {"start": v(-4598.83, -2020.04) * mm, "end": v(-4595.14, -2057.9) * mm});
            skLineSegment(sketch, "E1425", {"start": v(-4595.14, -2057.9) * mm, "end": v(-4600.68, -2060.68) * mm});
            skLineSegment(sketch, "E1426", {"start": v(-4600.68, -2060.68) * mm, "end": v(-4608.07, -2044.51) * mm});
            skLineSegment(sketch, "E1427", {"start": v(-4608.07, -2044.51) * mm, "end": v(-4615.46, -2034.82) * mm});
            skLineSegment(sketch, "E1428", {"start": v(-4615.46, -2034.82) * mm, "end": v(-4626.08, -2028.58) * mm});
            skLineSegment(sketch, "E1429", {"start": v(-4626.08, -2028.58) * mm, "end": v(-4639.47, -2026.5) * mm});
            skLineSegment(sketch, "E1430", {"start": v(-4639.47, -2026.5) * mm, "end": v(-4652.17, -2028.12) * mm});
            skLineSegment(sketch, "E1431", {"start": v(-4652.17, -2028.12) * mm, "end": v(-4660.72, -2032.97) * mm});
            skLineSegment(sketch, "E1432", {"start": v(-4660.72, -2032.97) * mm, "end": v(-4667.64, -2042.67) * mm});
            skLineSegment(sketch, "E1433", {"start": v(-4667.64, -2042.67) * mm, "end": v(-4669.95, -2055.14) * mm});
            skLineSegment(sketch, "E1434", {"start": v(-4669.95, -2055.14) * mm, "end": v(-4667.64, -2066.45) * mm});
            skLineSegment(sketch, "E1435", {"start": v(-4667.64, -2066.45) * mm, "end": v(-4660.72, -2074.53) * mm});
            skLineSegment(sketch, "E1436", {"start": v(-4660.72, -2074.53) * mm, "end": v(-4635.78, -2086.54) * mm});
            skLineSegment(sketch, "E1437", {"start": v(-4635.78, -2086.54) * mm, "end": v(-4615.23, -2097.62) * mm});
            skLineSegment(sketch, "E1438", {"start": v(-4615.23, -2097.62) * mm, "end": v(-4599.76, -2110.55) * mm});
            skLineSegment(sketch, "E1439", {"start": v(-4599.76, -2110.55) * mm, "end": v(-4592.14, -2122.8) * mm});
            skLineSegment(sketch, "E1440", {"start": v(-4592.14, -2122.8) * mm, "end": v(-4589.6, -2137.34) * mm});
            skLineSegment(sketch, "E1441", {"start": v(-4589.6, -2137.34) * mm, "end": v(-4590.35, -2145.36) * mm});
            skLineSegment(sketch, "E1442", {"start": v(-4590.35, -2145.36) * mm, "end": v(-4592.6, -2152.8) * mm});
            skLineSegment(sketch, "E1443", {"start": v(-4592.6, -2152.8) * mm, "end": v(-4596.35, -2159.68) * mm});
            skLineSegment(sketch, "E1444", {"start": v(-4596.35, -2159.68) * mm, "end": v(-4601.6, -2165.97) * mm});
            skLineSegment(sketch, "E1445", {"start": v(-4601.6, -2165.97) * mm, "end": v(-4608.18, -2171.22) * mm});
            skLineSegment(sketch, "E1446", {"start": v(-4608.18, -2171.22) * mm, "end": v(-4615.92, -2174.98) * mm});
            skLineSegment(sketch, "E1447", {"start": v(-4615.92, -2174.98) * mm, "end": v(-4624.8, -2177.23) * mm});
            skLineSegment(sketch, "E1448", {"start": v(-4624.8, -2177.23) * mm, "end": v(-4634.85, -2177.98) * mm});
            skLineSegment(sketch, "E1449", {"start": v(-4634.85, -2177.98) * mm, "end": v(-4645.24, -2177.06) * mm});
            skLineSegment(sketch, "E1450", {"start": v(-4645.24, -2177.06) * mm, "end": v(-4654.25, -2174.28) * mm});
            skLineSegment(sketch, "E1451", {"start": v(-4654.25, -2174.28) * mm, "end": v(-4664.41, -2171.51) * mm});
            skLineSegment(sketch, "E1452", {"start": v(-4664.41, -2171.51) * mm, "end": v(-4670.18, -2173.13) * mm});
            skLineSegment(sketch, "E1453", {"start": v(-4670.18, -2173.13) * mm, "end": v(-4676.42, -2177.98) * mm});
            skLineSegment(sketch, "E1454", {"start": v(-4676.42, -2177.98) * mm, "end": v(-4683.8, -2132.72) * mm});
            skLineSegment(sketch, "E1455", {"start": v(-4683.8, -2132.72) * mm, "end": v(-4678.26, -2129.95) * mm});
            skLineSegment(sketch, "E1456", {"start": v(-4678.26, -2129.95) * mm, "end": v(-4670.88, -2150.27) * mm});
            skLineSegment(sketch, "E1457", {"start": v(-4670.88, -2150.27) * mm, "end": v(-4663.49, -2161.35) * mm});
            skLineSegment(sketch, "E1458", {"start": v(-4663.49, -2161.35) * mm, "end": v(-4657.48, -2165.8) * mm});
            skLineSegment(sketch, "E1459", {"start": v(-4657.48, -2165.8) * mm, "end": v(-4650.56, -2168.97) * mm});
            skLineSegment(sketch, "E1460", {"start": v(-4650.56, -2168.97) * mm, "end": v(-4633.93, -2171.51) * mm});
            skLineSegment(sketch, "E1461", {"start": v(-4633.93, -2171.51) * mm, "end": v(-4621, -2169.67) * mm});
            skLineSegment(sketch, "E1462", {"start": v(-4621, -2169.67) * mm, "end": v(-4611.76, -2164.12) * mm});
            skLineSegment(sketch, "E1463", {"start": v(-4611.76, -2164.12) * mm, "end": v(-4607.72, -2159.33) * mm});
            skLineSegment(sketch, "E1464", {"start": v(-4607.72, -2159.33) * mm, "end": v(-4604.84, -2153.27) * mm});
            skLineSegment(sketch, "E1465", {"start": v(-4604.84, -2153.27) * mm, "end": v(-4602.53, -2137.34) * mm});
            skLineSegment(sketch, "E1466", {"start": v(-4390.1, -2020.04) * mm, "end": v(-4390.1, -2157.66) * mm});
            skLineSegment(sketch, "E1467", {"start": v(-4390.1, -2157.66) * mm, "end": v(-4389, -2164.12) * mm});
            skLineSegment(sketch, "E1468", {"start": v(-4389, -2164.12) * mm, "end": v(-4385.7, -2168.74) * mm});
            skLineSegment(sketch, "E1469", {"start": v(-4385.7, -2168.74) * mm, "end": v(-4380.22, -2171.51) * mm});
            skLineSegment(sketch, "E1470", {"start": v(-4380.22, -2171.51) * mm, "end": v(-4372.54, -2172.44) * mm});
            skLineSegment(sketch, "E1471", {"start": v(-4372.54, -2172.44) * mm, "end": v(-4363.3, -2172.44) * mm});
            skLineSegment(sketch, "E1472", {"start": v(-4363.3, -2172.44) * mm, "end": v(-4363.3, -2177.98) * mm});
            skLineSegment(sketch, "E1473", {"start": v(-4363.3, -2177.98) * mm, "end": v(-4430.73, -2177.98) * mm});
            skLineSegment(sketch, "E1474", {"start": v(-4430.73, -2177.98) * mm, "end": v(-4430.73, -2172.44) * mm});
            skLineSegment(sketch, "E1475", {"start": v(-4430.73, -2172.44) * mm, "end": v(-4422.42, -2172.44) * mm});
            skLineSegment(sketch, "E1476", {"start": v(-4422.42, -2172.44) * mm, "end": v(-4414.74, -2171.51) * mm});
            skLineSegment(sketch, "E1477", {"start": v(-4414.74, -2171.51) * mm, "end": v(-4409.26, -2168.74) * mm});
            skLineSegment(sketch, "E1478", {"start": v(-4409.26, -2168.74) * mm, "end": v(-4405.97, -2164.12) * mm});
            skLineSegment(sketch, "E1479", {"start": v(-4405.97, -2164.12) * mm, "end": v(-4404.87, -2157.66) * mm});
            skLineSegment(sketch, "E1480", {"start": v(-4404.87, -2157.66) * mm, "end": v(-4404.87, -2048.67) * mm});
            skLineSegment(sketch, "E1481", {"start": v(-4404.87, -2048.67) * mm, "end": v(-4407.18, -2042.44) * mm});
            skLineSegment(sketch, "E1482", {"start": v(-4407.18, -2042.44) * mm, "end": v(-4414.1, -2040.36) * mm});
            skLineSegment(sketch, "E1483", {"start": v(-4414.1, -2040.36) * mm, "end": v(-4430.73, -2040.36) * mm});
            skLineSegment(sketch, "E1484", {"start": v(-4430.73, -2040.36) * mm, "end": v(-4430.73, -2034.82) * mm});
            skLineSegment(sketch, "E1485", {"start": v(-4430.73, -2034.82) * mm, "end": v(-4422.42, -2034.82) * mm});
            skLineSegment(sketch, "E1486", {"start": v(-4422.42, -2034.82) * mm, "end": v(-4412.66, -2033.9) * mm});
            skLineSegment(sketch, "E1487", {"start": v(-4412.66, -2033.9) * mm, "end": v(-4404.64, -2031.12) * mm});
            skLineSegment(sketch, "E1488", {"start": v(-4404.64, -2031.12) * mm, "end": v(-4398.35, -2026.5) * mm});
            skLineSegment(sketch, "E1489", {"start": v(-4398.35, -2026.5) * mm, "end": v(-4393.78, -2020.04) * mm});
            skLineSegment(sketch, "E1490", {"start": v(-4393.78, -2020.04) * mm, "end": v(-4390.1, -2020.04) * mm});
            skLineSegment(sketch, "E1491", {"start": v(-4299.57, -2176.13) * mm, "end": v(-4304.42, -2179.6) * mm});
            skLineSegment(sketch, "E1492", {"start": v(-4304.42, -2179.6) * mm, "end": v(-4309.73, -2180.75) * mm});
            skLineSegment(sketch, "E1493", {"start": v(-4309.73, -2180.75) * mm, "end": v(-4315.04, -2179.6) * mm});
            skLineSegment(sketch, "E1494", {"start": v(-4315.04, -2179.6) * mm, "end": v(-4319.9, -2176.13) * mm});
            skLineSegment(sketch, "E1495", {"start": v(-4319.9, -2176.13) * mm, "end": v(-4322.66, -2171.98) * mm});
            skLineSegment(sketch, "E1496", {"start": v(-4322.66, -2171.98) * mm, "end": v(-4323.59, -2166.9) * mm});
            skLineSegment(sketch, "E1497", {"start": v(-4323.59, -2166.9) * mm, "end": v(-4322.66, -2161.82) * mm});
            skLineSegment(sketch, "E1498", {"start": v(-4322.66, -2161.82) * mm, "end": v(-4319.9, -2157.66) * mm});
            skLineSegment(sketch, "E1499", {"start": v(-4319.9, -2157.66) * mm, "end": v(-4315.04, -2154.2) * mm});
            skLineSegment(sketch, "E1500", {"start": v(-4315.04, -2154.2) * mm, "end": v(-4309.73, -2153.04) * mm});
            skLineSegment(sketch, "E1501", {"start": v(-4309.73, -2153.04) * mm, "end": v(-4304.42, -2154.2) * mm});
            skLineSegment(sketch, "E1502", {"start": v(-4304.42, -2154.2) * mm, "end": v(-4299.57, -2157.66) * mm});
            skLineSegment(sketch, "E1503", {"start": v(-4299.57, -2157.66) * mm, "end": v(-4296.8, -2161.82) * mm});
            skLineSegment(sketch, "E1504", {"start": v(-4296.8, -2161.82) * mm, "end": v(-4295.88, -2166.9) * mm});
            skLineSegment(sketch, "E1505", {"start": v(-4295.88, -2166.9) * mm, "end": v(-4296.8, -2171.98) * mm});
            skLineSegment(sketch, "E1506", {"start": v(-4296.8, -2171.98) * mm, "end": v(-4299.57, -2176.13) * mm});
            skLineSegment(sketch, "E1507", {"start": v(-4136.1, -2160.43) * mm, "end": v(-4135.22, -2165.68) * mm});
            skLineSegment(sketch, "E1508", {"start": v(-4135.22, -2165.68) * mm, "end": v(-4132.63, -2169.44) * mm});
            skLineSegment(sketch, "E1509", {"start": v(-4132.63, -2169.44) * mm, "end": v(-4128.3, -2171.69) * mm});
            skLineSegment(sketch, "E1510", {"start": v(-4128.3, -2171.69) * mm, "end": v(-4122.24, -2172.44) * mm});
            skLineSegment(sketch, "E1511", {"start": v(-4122.24, -2172.44) * mm, "end": v(-4113.92, -2172.44) * mm});
            skLineSegment(sketch, "E1512", {"start": v(-4113.92, -2172.44) * mm, "end": v(-4113.92, -2177.98) * mm});
            skLineSegment(sketch, "E1513", {"start": v(-4113.92, -2177.98) * mm, "end": v(-4174.88, -2177.98) * mm});
            skLineSegment(sketch, "E1514", {"start": v(-4174.88, -2177.98) * mm, "end": v(-4174.88, -2172.44) * mm});
            skLineSegment(sketch, "E1515", {"start": v(-4174.88, -2172.44) * mm, "end": v(-4164.72, -2172.44) * mm});
            skLineSegment(sketch, "E1516", {"start": v(-4164.72, -2172.44) * mm, "end": v(-4158.66, -2171.69) * mm});
            skLineSegment(sketch, "E1517", {"start": v(-4158.66, -2171.69) * mm, "end": v(-4154.33, -2169.44) * mm});
            skLineSegment(sketch, "E1518", {"start": v(-4154.33, -2169.44) * mm, "end": v(-4151.73, -2165.68) * mm});
            skLineSegment(sketch, "E1519", {"start": v(-4151.73, -2165.68) * mm, "end": v(-4150.87, -2160.43) * mm});
            skLineSegment(sketch, "E1520", {"start": v(-4150.87, -2160.43) * mm, "end": v(-4150.87, -2131.8) * mm});
            skLineSegment(sketch, "E1521", {"start": v(-4150.87, -2131.8) * mm, "end": v(-4212.75, -2131.8) * mm});
            skLineSegment(sketch, "E1522", {"start": v(-4212.75, -2131.8) * mm, "end": v(-4212.75, -2127.18) * mm});
            skLineSegment(sketch, "E1523", {"start": v(-4212.75, -2127.18) * mm, "end": v(-4145.33, -2020.04) * mm});
            skLineSegment(sketch, "E1524", {"start": v(-4145.33, -2020.04) * mm, "end": v(-4136.1, -2020.04) * mm});
            skLineSegment(sketch, "E1525", {"start": v(-4136.1, -2020.04) * mm, "end": v(-4136.1, -2126.26) * mm});
            skLineSegment(sketch, "E1526", {"start": v(-4136.1, -2126.26) * mm, "end": v(-4111.15, -2126.26) * mm});
            skLineSegment(sketch, "E1527", {"start": v(-4111.15, -2126.26) * mm, "end": v(-4111.15, -2131.8) * mm});
            skLineSegment(sketch, "E1528", {"start": v(-4111.15, -2131.8) * mm, "end": v(-4136.1, -2131.8) * mm});
            skLineSegment(sketch, "E1529", {"start": v(-4136.1, -2131.8) * mm, "end": v(-4136.1, -2160.43) * mm});
            skLineSegment(sketch, "E1530", {"start": v(-4151.8, -2043.13) * mm, "end": v(-4204.44, -2126.26) * mm});
            skLineSegment(sketch, "E1531", {"start": v(-4204.44, -2126.26) * mm, "end": v(-4150.87, -2126.26) * mm});
            skLineSegment(sketch, "E1532", {"start": v(-4150.87, -2126.26) * mm, "end": v(-4150.87, -2043.13) * mm});
            skLineSegment(sketch, "E1533", {"start": v(-4150.87, -2043.13) * mm, "end": v(-4151.8, -2043.13) * mm});
            skLineSegment(sketch, "E1534", {"start": v(-5584.35, -2350.7) * mm, "end": v(-5571.02, -2336.27) * mm});
            skLineSegment(sketch, "E1535", {"start": v(-5571.02, -2336.27) * mm, "end": v(-5561.5, -2322.53) * mm});
            skLineSegment(sketch, "E1536", {"start": v(-5561.5, -2322.53) * mm, "end": v(-5555.78, -2309.48) * mm});
            skLineSegment(sketch, "E1537", {"start": v(-5555.78, -2309.48) * mm, "end": v(-5553.87, -2297.13) * mm});
            skLineSegment(sketch, "E1538", {"start": v(-5553.87, -2297.13) * mm, "end": v(-5556.18, -2281.2) * mm});
            skLineSegment(sketch, "E1539", {"start": v(-5556.18, -2281.2) * mm, "end": v(-5559.07, -2275.13) * mm});
            skLineSegment(sketch, "E1540", {"start": v(-5559.07, -2275.13) * mm, "end": v(-5563.1, -2270.34) * mm});
            skLineSegment(sketch, "E1541", {"start": v(-5563.1, -2270.34) * mm, "end": v(-5571.88, -2264.8) * mm});
            skLineSegment(sketch, "E1542", {"start": v(-5571.88, -2264.8) * mm, "end": v(-5583.43, -2262.95) * mm});
            skLineSegment(sketch, "E1543", {"start": v(-5583.43, -2262.95) * mm, "end": v(-5595.2, -2264.8) * mm});
            skLineSegment(sketch, "E1544", {"start": v(-5595.2, -2264.8) * mm, "end": v(-5604.67, -2270.34) * mm});
            skLineSegment(sketch, "E1545", {"start": v(-5604.67, -2270.34) * mm, "end": v(-5608.83, -2276.58) * mm});
            skLineSegment(sketch, "E1546", {"start": v(-5608.83, -2276.58) * mm, "end": v(-5610.21, -2284.2) * mm});
            skLineSegment(sketch, "E1547", {"start": v(-5610.21, -2284.2) * mm, "end": v(-5609.3, -2289.28) * mm});
            skLineSegment(sketch, "E1548", {"start": v(-5609.3, -2289.28) * mm, "end": v(-5606.52, -2293.43) * mm});
            skLineSegment(sketch, "E1549", {"start": v(-5606.52, -2293.43) * mm, "end": v(-5604.44, -2296.67) * mm});
            skLineSegment(sketch, "E1550", {"start": v(-5604.44, -2296.67) * mm, "end": v(-5603.75, -2300.82) * mm});
            skLineSegment(sketch, "E1551", {"start": v(-5603.75, -2300.82) * mm, "end": v(-5606.06, -2307.75) * mm});
            skLineSegment(sketch, "E1552", {"start": v(-5606.06, -2307.75) * mm, "end": v(-5612.98, -2310.06) * mm});
            skLineSegment(sketch, "E1553", {"start": v(-5612.98, -2310.06) * mm, "end": v(-5617.83, -2309.37) * mm});
            skLineSegment(sketch, "E1554", {"start": v(-5617.83, -2309.37) * mm, "end": v(-5621.3, -2307.29) * mm});
            skLineSegment(sketch, "E1555", {"start": v(-5621.3, -2307.29) * mm, "end": v(-5624.07, -2302.67) * mm});
            skLineSegment(sketch, "E1556", {"start": v(-5624.07, -2302.67) * mm, "end": v(-5625, -2296.2) * mm});
            skLineSegment(sketch, "E1557", {"start": v(-5625, -2296.2) * mm, "end": v(-5622.45, -2281.2) * mm});
            skLineSegment(sketch, "E1558", {"start": v(-5622.45, -2281.2) * mm, "end": v(-5614.83, -2269.42) * mm});
            skLineSegment(sketch, "E1559", {"start": v(-5614.83, -2269.42) * mm, "end": v(-5607.56, -2263.76) * mm});
            skLineSegment(sketch, "E1560", {"start": v(-5607.56, -2263.76) * mm, "end": v(-5599.6, -2259.72) * mm});
            skLineSegment(sketch, "E1561", {"start": v(-5599.6, -2259.72) * mm, "end": v(-5590.93, -2257.3) * mm});
            skLineSegment(sketch, "E1562", {"start": v(-5590.93, -2257.3) * mm, "end": v(-5581.58, -2256.49) * mm});
            skLineSegment(sketch, "E1563", {"start": v(-5581.58, -2256.49) * mm, "end": v(-5571.6, -2257.18) * mm});
            skLineSegment(sketch, "E1564", {"start": v(-5571.6, -2257.18) * mm, "end": v(-5562.88, -2259.26) * mm});
            skLineSegment(sketch, "E1565", {"start": v(-5562.88, -2259.26) * mm, "end": v(-5555.43, -2262.72) * mm});
            skLineSegment(sketch, "E1566", {"start": v(-5555.43, -2262.72) * mm, "end": v(-5549.25, -2267.57) * mm});
            skLineSegment(sketch, "E1567", {"start": v(-5549.25, -2267.57) * mm, "end": v(-5544.4, -2273.46) * mm});
            skLineSegment(sketch, "E1568", {"start": v(-5544.4, -2273.46) * mm, "end": v(-5540.94, -2280.04) * mm});
            skLineSegment(sketch, "E1569", {"start": v(-5540.94, -2280.04) * mm, "end": v(-5538.17, -2295.28) * mm});
            skLineSegment(sketch, "E1570", {"start": v(-5538.17, -2295.28) * mm, "end": v(-5539.5, -2305.84) * mm});
            skLineSegment(sketch, "E1571", {"start": v(-5539.5, -2305.84) * mm, "end": v(-5543.48, -2316.3) * mm});
            skLineSegment(sketch, "E1572", {"start": v(-5543.48, -2316.3) * mm, "end": v(-5550.12, -2326.63) * mm});
            skLineSegment(sketch, "E1573", {"start": v(-5550.12, -2326.63) * mm, "end": v(-5559.41, -2336.84) * mm});
            skLineSegment(sketch, "E1574", {"start": v(-5559.41, -2336.84) * mm, "end": v(-5600.75, -2378.64) * mm});
            skLineSegment(sketch, "E1575", {"start": v(-5600.75, -2378.64) * mm, "end": v(-5612.23, -2392.09) * mm});
            skLineSegment(sketch, "E1576", {"start": v(-5612.23, -2392.09) * mm, "end": v(-5617.6, -2400.58) * mm});
            skLineSegment(sketch, "E1577", {"start": v(-5617.6, -2400.58) * mm, "end": v(-5563.1, -2400.58) * mm});
            skLineSegment(sketch, "E1578", {"start": v(-5563.1, -2400.58) * mm, "end": v(-5555.55, -2398.96) * mm});
            skLineSegment(sketch, "E1579", {"start": v(-5555.55, -2398.96) * mm, "end": v(-5549.48, -2394.1) * mm});
            skLineSegment(sketch, "E1580", {"start": v(-5549.48, -2394.1) * mm, "end": v(-5544.92, -2386.03) * mm});
            skLineSegment(sketch, "E1581", {"start": v(-5544.92, -2386.03) * mm, "end": v(-5541.86, -2374.71) * mm});
            skLineSegment(sketch, "E1582", {"start": v(-5541.86, -2374.71) * mm, "end": v(-5536.32, -2374.71) * mm});
            skLineSegment(sketch, "E1583", {"start": v(-5536.32, -2374.71) * mm, "end": v(-5541.86, -2414.43) * mm});
            skLineSegment(sketch, "E1584", {"start": v(-5541.86, -2414.43) * mm, "end": v(-5627.76, -2414.43) * mm});
            skLineSegment(sketch, "E1585", {"start": v(-5627.76, -2414.43) * mm, "end": v(-5627.76, -2402.42) * mm});
            skLineSegment(sketch, "E1586", {"start": v(-5627.76, -2402.42) * mm, "end": v(-5621.93, -2392.6) * mm});
            skLineSegment(sketch, "E1587", {"start": v(-5621.93, -2392.6) * mm, "end": v(-5612.75, -2380.72) * mm});
            skLineSegment(sketch, "E1588", {"start": v(-5612.75, -2380.72) * mm, "end": v(-5584.35, -2350.7) * mm});
            skLineSegment(sketch, "E1589", {"start": v(-5395.93, -2313.75) * mm, "end": v(-5395.93, -2305.44) * mm});
            skLineSegment(sketch, "E1590", {"start": v(-5395.93, -2305.44) * mm, "end": v(-5293.4, -2305.44) * mm});
            skLineSegment(sketch, "E1591", {"start": v(-5293.4, -2305.44) * mm, "end": v(-5293.4, -2313.75) * mm});
            skLineSegment(sketch, "E1592", {"start": v(-5293.4, -2313.75) * mm, "end": v(-5395.93, -2313.75) * mm});
            skLineSegment(sketch, "E1593", {"start": v(-5395.93, -2360.86) * mm, "end": v(-5395.93, -2352.55) * mm});
            skLineSegment(sketch, "E1594", {"start": v(-5395.93, -2352.55) * mm, "end": v(-5293.4, -2352.55) * mm});
            skLineSegment(sketch, "E1595", {"start": v(-5293.4, -2352.55) * mm, "end": v(-5293.4, -2360.86) * mm});
            skLineSegment(sketch, "E1596", {"start": v(-5293.4, -2360.86) * mm, "end": v(-5395.93, -2360.86) * mm});
            skLineSegment(sketch, "E1597", {"start": v(-5106.83, -2256.49) * mm, "end": v(-5095.98, -2257.18) * mm});
            skLineSegment(sketch, "E1598", {"start": v(-5095.98, -2257.18) * mm, "end": v(-5086.51, -2259.26) * mm});
            skLineSegment(sketch, "E1599", {"start": v(-5086.51, -2259.26) * mm, "end": v(-5078.43, -2262.72) * mm});
            skLineSegment(sketch, "E1600", {"start": v(-5078.43, -2262.72) * mm, "end": v(-5071.73, -2267.57) * mm});
            skLineSegment(sketch, "E1601", {"start": v(-5071.73, -2267.57) * mm, "end": v(-5064.8, -2278.66) * mm});
            skLineSegment(sketch, "E1602", {"start": v(-5064.8, -2278.66) * mm, "end": v(-5062.5, -2293.43) * mm});
            skLineSegment(sketch, "E1603", {"start": v(-5062.5, -2293.43) * mm, "end": v(-5065.04, -2309.14) * mm});
            skLineSegment(sketch, "E1604", {"start": v(-5065.04, -2309.14) * mm, "end": v(-5068.21, -2315.6) * mm});
            skLineSegment(sketch, "E1605", {"start": v(-5068.21, -2315.6) * mm, "end": v(-5072.66, -2321.14) * mm});
            skLineSegment(sketch, "E1606", {"start": v(-5072.66, -2321.14) * mm, "end": v(-5083.51, -2329.46) * mm});
            skLineSegment(sketch, "E1607", {"start": v(-5083.51, -2329.46) * mm, "end": v(-5095.75, -2334.07) * mm});
            skLineSegment(sketch, "E1608", {"start": v(-5095.75, -2334.07) * mm, "end": v(-5068.04, -2402.42) * mm});
            skLineSegment(sketch, "E1609", {"start": v(-5068.04, -2402.42) * mm, "end": v(-5063.88, -2407.27) * mm});
            skLineSegment(sketch, "E1610", {"start": v(-5063.88, -2407.27) * mm, "end": v(-5058.8, -2408.89) * mm});
            skLineSegment(sketch, "E1611", {"start": v(-5058.8, -2408.89) * mm, "end": v(-5053.26, -2408.89) * mm});
            skLineSegment(sketch, "E1612", {"start": v(-5053.26, -2408.89) * mm, "end": v(-5053.26, -2414.43) * mm});
            skLineSegment(sketch, "E1613", {"start": v(-5053.26, -2414.43) * mm, "end": v(-5079.12, -2414.43) * mm});
            skLineSegment(sketch, "E1614", {"start": v(-5079.12, -2414.43) * mm, "end": v(-5109.6, -2335) * mm});
            skLineSegment(sketch, "E1615", {"start": v(-5109.6, -2335) * mm, "end": v(-5130.85, -2335) * mm});
            skLineSegment(sketch, "E1616", {"start": v(-5130.85, -2335) * mm, "end": v(-5130.85, -2401.5) * mm});
            skLineSegment(sketch, "E1617", {"start": v(-5130.85, -2401.5) * mm, "end": v(-5128.77, -2407.04) * mm});
            skLineSegment(sketch, "E1618", {"start": v(-5128.77, -2407.04) * mm, "end": v(-5122.53, -2408.89) * mm});
            skLineSegment(sketch, "E1619", {"start": v(-5122.53, -2408.89) * mm, "end": v(-5117, -2408.89) * mm});
            skLineSegment(sketch, "E1620", {"start": v(-5117, -2408.89) * mm, "end": v(-5117, -2414.43) * mm});
            skLineSegment(sketch, "E1621", {"start": v(-5117, -2414.43) * mm, "end": v(-5159.48, -2414.43) * mm});
            skLineSegment(sketch, "E1622", {"start": v(-5159.48, -2414.43) * mm, "end": v(-5159.48, -2408.89) * mm});
            skLineSegment(sketch, "E1623", {"start": v(-5159.48, -2408.89) * mm, "end": v(-5153.94, -2408.89) * mm});
            skLineSegment(sketch, "E1624", {"start": v(-5153.94, -2408.89) * mm, "end": v(-5147.7, -2407.04) * mm});
            skLineSegment(sketch, "E1625", {"start": v(-5147.7, -2407.04) * mm, "end": v(-5145.62, -2401.5) * mm});
            skLineSegment(sketch, "E1626", {"start": v(-5145.62, -2401.5) * mm, "end": v(-5145.62, -2269.42) * mm});
            skLineSegment(sketch, "E1627", {"start": v(-5145.62, -2269.42) * mm, "end": v(-5147.7, -2263.88) * mm});
            skLineSegment(sketch, "E1628", {"start": v(-5147.7, -2263.88) * mm, "end": v(-5153.94, -2262.03) * mm});
            skLineSegment(sketch, "E1629", {"start": v(-5153.94, -2262.03) * mm, "end": v(-5159.48, -2262.03) * mm});
            skLineSegment(sketch, "E1630", {"start": v(-5159.48, -2262.03) * mm, "end": v(-5159.48, -2256.49) * mm});
            skLineSegment(sketch, "E1631", {"start": v(-5159.48, -2256.49) * mm, "end": v(-5106.83, -2256.49) * mm});
            skLineSegment(sketch, "E1632", {"start": v(-5130.85, -2329.46) * mm, "end": v(-5110.53, -2329.46) * mm});
            skLineSegment(sketch, "E1633", {"start": v(-5110.53, -2329.46) * mm, "end": v(-5097.13, -2327.15) * mm});
            skLineSegment(sketch, "E1634", {"start": v(-5097.13, -2327.15) * mm, "end": v(-5086.51, -2320.22) * mm});
            skLineSegment(sketch, "E1635", {"start": v(-5086.51, -2320.22) * mm, "end": v(-5080.28, -2309.83) * mm});
            skLineSegment(sketch, "E1636", {"start": v(-5080.28, -2309.83) * mm, "end": v(-5078.2, -2295.28) * mm});
            skLineSegment(sketch, "E1637", {"start": v(-5078.2, -2295.28) * mm, "end": v(-5080.28, -2280.73) * mm});
            skLineSegment(sketch, "E1638", {"start": v(-5080.28, -2280.73) * mm, "end": v(-5086.51, -2270.34) * mm});
            skLineSegment(sketch, "E1639", {"start": v(-5086.51, -2270.34) * mm, "end": v(-5097.6, -2264.1) * mm});
            skLineSegment(sketch, "E1640", {"start": v(-5097.6, -2264.1) * mm, "end": v(-5112.37, -2262.03) * mm});
            skLineSegment(sketch, "E1641", {"start": v(-5112.37, -2262.03) * mm, "end": v(-5122.53, -2262.03) * mm});
            skLineSegment(sketch, "E1642", {"start": v(-5122.53, -2262.03) * mm, "end": v(-5128.77, -2263.88) * mm});
            skLineSegment(sketch, "E1643", {"start": v(-5128.77, -2263.88) * mm, "end": v(-5130.85, -2269.42) * mm});
            skLineSegment(sketch, "E1644", {"start": v(-5130.85, -2269.42) * mm, "end": v(-5130.85, -2329.46) * mm});
            skLineSegment(sketch, "E1645", {"start": v(-4973.83, -2357.16) * mm, "end": v(-5015.4, -2357.16) * mm});
            skLineSegment(sketch, "E1646", {"start": v(-5015.4, -2357.16) * mm, "end": v(-5023.7, -2390.42) * mm});
            skLineSegment(sketch, "E1647", {"start": v(-5023.7, -2390.42) * mm, "end": v(-5024.92, -2398.5) * mm});
            skLineSegment(sketch, "E1648", {"start": v(-5024.92, -2398.5) * mm, "end": v(-5023.94, -2404.27) * mm});
            skLineSegment(sketch, "E1649", {"start": v(-5023.94, -2404.27) * mm, "end": v(-5020.76, -2407.73) * mm});
            skLineSegment(sketch, "E1650", {"start": v(-5020.76, -2407.73) * mm, "end": v(-5015.4, -2408.89) * mm});
            skLineSegment(sketch, "E1651", {"start": v(-5015.4, -2408.89) * mm, "end": v(-5012.62, -2408.89) * mm});
            skLineSegment(sketch, "E1652", {"start": v(-5012.62, -2408.89) * mm, "end": v(-5012.62, -2414.43) * mm});
            skLineSegment(sketch, "E1653", {"start": v(-5012.62, -2414.43) * mm, "end": v(-5046.8, -2414.43) * mm});
            skLineSegment(sketch, "E1654", {"start": v(-5046.8, -2414.43) * mm, "end": v(-5046.8, -2408.89) * mm});
            skLineSegment(sketch, "E1655", {"start": v(-5046.8, -2408.89) * mm, "end": v(-5044.02, -2408.89) * mm});
            skLineSegment(sketch, "E1656", {"start": v(-5044.02, -2408.89) * mm, "end": v(-5038.25, -2406.35) * mm});
            skLineSegment(sketch, "E1657", {"start": v(-5038.25, -2406.35) * mm, "end": v(-5033.86, -2398.73) * mm});
            skLineSegment(sketch, "E1658", {"start": v(-5033.86, -2398.73) * mm, "end": v(-4997.84, -2261.1) * mm});
            skLineSegment(sketch, "E1659", {"start": v(-4997.84, -2261.1) * mm, "end": v(-4983.99, -2256.49) * mm});
            skLineSegment(sketch, "E1660", {"start": v(-4983.99, -2256.49) * mm, "end": v(-4948.9, -2398.73) * mm});
            skLineSegment(sketch, "E1661", {"start": v(-4948.9, -2398.73) * mm, "end": v(-4944.27, -2406.35) * mm});
            skLineSegment(sketch, "E1662", {"start": v(-4944.27, -2406.35) * mm, "end": v(-4937.8, -2408.89) * mm});
            skLineSegment(sketch, "E1663", {"start": v(-4937.8, -2408.89) * mm, "end": v(-4935.04, -2408.89) * mm});
            skLineSegment(sketch, "E1664", {"start": v(-4935.04, -2408.89) * mm, "end": v(-4935.04, -2414.43) * mm});
            skLineSegment(sketch, "E1665", {"start": v(-4935.04, -2414.43) * mm, "end": v(-4974.75, -2414.43) * mm});
            skLineSegment(sketch, "E1666", {"start": v(-4974.75, -2414.43) * mm, "end": v(-4974.75, -2408.89) * mm});
            skLineSegment(sketch, "E1667", {"start": v(-4974.75, -2408.89) * mm, "end": v(-4971.06, -2408.89) * mm});
            skLineSegment(sketch, "E1668", {"start": v(-4971.06, -2408.89) * mm, "end": v(-4966.84, -2408.08) * mm});
            skLineSegment(sketch, "E1669", {"start": v(-4966.84, -2408.08) * mm, "end": v(-4964.36, -2405.66) * mm});
            skLineSegment(sketch, "E1670", {"start": v(-4964.36, -2405.66) * mm, "end": v(-4963.61, -2401.61) * mm});
            skLineSegment(sketch, "E1671", {"start": v(-4963.61, -2401.61) * mm, "end": v(-4964.6, -2395.96) * mm});
            skLineSegment(sketch, "E1672", {"start": v(-4964.6, -2395.96) * mm, "end": v(-4973.83, -2357.16) * mm});
            skLineSegment(sketch, "E1673", {"start": v(-4993.22, -2274.96) * mm, "end": v(-4994.15, -2274.96) * mm});
            skLineSegment(sketch, "E1674", {"start": v(-4994.15, -2274.96) * mm, "end": v(-5013.54, -2351.62) * mm});
            skLineSegment(sketch, "E1675", {"start": v(-5013.54, -2351.62) * mm, "end": v(-4974.75, -2351.62) * mm});
            skLineSegment(sketch, "E1676", {"start": v(-4974.75, -2351.62) * mm, "end": v(-4993.22, -2274.96) * mm});
            skLineSegment(sketch, "E1677", {"start": v(-4826.97, -2401.5) * mm, "end": v(-4824.9, -2407.04) * mm});
            skLineSegment(sketch, "E1678", {"start": v(-4824.9, -2407.04) * mm, "end": v(-4818.66, -2408.89) * mm});
            skLineSegment(sketch, "E1679", {"start": v(-4818.66, -2408.89) * mm, "end": v(-4814.96, -2408.89) * mm});
            skLineSegment(sketch, "E1680", {"start": v(-4814.96, -2408.89) * mm, "end": v(-4814.96, -2414.43) * mm});
            skLineSegment(sketch, "E1681", {"start": v(-4814.96, -2414.43) * mm, "end": v(-4854.68, -2414.43) * mm});
            skLineSegment(sketch, "E1682", {"start": v(-4854.68, -2414.43) * mm, "end": v(-4854.68, -2408.89) * mm});
            skLineSegment(sketch, "E1683", {"start": v(-4854.68, -2408.89) * mm, "end": v(-4850.06, -2408.89) * mm});
            skLineSegment(sketch, "E1684", {"start": v(-4850.06, -2408.89) * mm, "end": v(-4843.83, -2407.04) * mm});
            skLineSegment(sketch, "E1685", {"start": v(-4843.83, -2407.04) * mm, "end": v(-4841.75, -2401.5) * mm});
            skLineSegment(sketch, "E1686", {"start": v(-4841.75, -2401.5) * mm, "end": v(-4841.75, -2280.5) * mm});
            skLineSegment(sketch, "E1687", {"start": v(-4841.75, -2280.5) * mm, "end": v(-4843.6, -2280.5) * mm});
            skLineSegment(sketch, "E1688", {"start": v(-4843.6, -2280.5) * mm, "end": v(-4875, -2414.43) * mm});
            skLineSegment(sketch, "E1689", {"start": v(-4875, -2414.43) * mm, "end": v(-4880.54, -2414.43) * mm});
            skLineSegment(sketch, "E1690", {"start": v(-4880.54, -2414.43) * mm, "end": v(-4909.17, -2283.27) * mm});
            skLineSegment(sketch, "E1691", {"start": v(-4909.17, -2283.27) * mm, "end": v(-4911.02, -2283.27) * mm});
            skLineSegment(sketch, "E1692", {"start": v(-4911.02, -2283.27) * mm, "end": v(-4911.02, -2401.5) * mm});
            skLineSegment(sketch, "E1693", {"start": v(-4911.02, -2401.5) * mm, "end": v(-4908.94, -2407.04) * mm});
            skLineSegment(sketch, "E1694", {"start": v(-4908.94, -2407.04) * mm, "end": v(-4902.7, -2408.89) * mm});
            skLineSegment(sketch, "E1695", {"start": v(-4902.7, -2408.89) * mm, "end": v(-4899.94, -2408.89) * mm});
            skLineSegment(sketch, "E1696", {"start": v(-4899.94, -2408.89) * mm, "end": v(-4899.94, -2414.43) * mm});
            skLineSegment(sketch, "E1697", {"start": v(-4899.94, -2414.43) * mm, "end": v(-4927.65, -2414.43) * mm});
            skLineSegment(sketch, "E1698", {"start": v(-4927.65, -2414.43) * mm, "end": v(-4927.65, -2408.89) * mm});
            skLineSegment(sketch, "E1699", {"start": v(-4927.65, -2408.89) * mm, "end": v(-4924.88, -2408.89) * mm});
            skLineSegment(sketch, "E1700", {"start": v(-4924.88, -2408.89) * mm, "end": v(-4918.64, -2407.04) * mm});
            skLineSegment(sketch, "E1701", {"start": v(-4918.64, -2407.04) * mm, "end": v(-4916.56, -2401.5) * mm});
            skLineSegment(sketch, "E1702", {"start": v(-4916.56, -2401.5) * mm, "end": v(-4916.56, -2269.42) * mm});
            skLineSegment(sketch, "E1703", {"start": v(-4916.56, -2269.42) * mm, "end": v(-4918.64, -2263.88) * mm});
            skLineSegment(sketch, "E1704", {"start": v(-4918.64, -2263.88) * mm, "end": v(-4924.88, -2262.03) * mm});
            skLineSegment(sketch, "E1705", {"start": v(-4924.88, -2262.03) * mm, "end": v(-4928.57, -2262.03) * mm});
            skLineSegment(sketch, "E1706", {"start": v(-4928.57, -2262.03) * mm, "end": v(-4928.57, -2256.49) * mm});
            skLineSegment(sketch, "E1707", {"start": v(-4928.57, -2256.49) * mm, "end": v(-4901.78, -2256.49) * mm});
            skLineSegment(sketch, "E1708", {"start": v(-4901.78, -2256.49) * mm, "end": v(-4875, -2380.26) * mm});
            skLineSegment(sketch, "E1709", {"start": v(-4875, -2380.26) * mm, "end": v(-4873.15, -2380.26) * mm});
            skLineSegment(sketch, "E1710", {"start": v(-4873.15, -2380.26) * mm, "end": v(-4844.52, -2256.49) * mm});
            skLineSegment(sketch, "E1711", {"start": v(-4844.52, -2256.49) * mm, "end": v(-4814.96, -2256.49) * mm});
            skLineSegment(sketch, "E1712", {"start": v(-4814.96, -2256.49) * mm, "end": v(-4814.96, -2262.03) * mm});
            skLineSegment(sketch, "E1713", {"start": v(-4814.96, -2262.03) * mm, "end": v(-4818.66, -2262.03) * mm});
            skLineSegment(sketch, "E1714", {"start": v(-4818.66, -2262.03) * mm, "end": v(-4824.9, -2263.88) * mm});
            skLineSegment(sketch, "E1715", {"start": v(-4824.9, -2263.88) * mm, "end": v(-4826.97, -2269.42) * mm});
            skLineSegment(sketch, "E1716", {"start": v(-4826.97, -2269.42) * mm, "end": v(-4826.97, -2401.5) * mm});
            skLineSegment(sketch, "E1717", {"start": v(-4808.5, -2414.43) * mm, "end": v(-4808.5, -2408.89) * mm});
            skLineSegment(sketch, "E1718", {"start": v(-4808.5, -2408.89) * mm, "end": v(-4801.1, -2408.89) * mm});
            skLineSegment(sketch, "E1719", {"start": v(-4801.1, -2408.89) * mm, "end": v(-4794.87, -2407.04) * mm});
            skLineSegment(sketch, "E1720", {"start": v(-4794.87, -2407.04) * mm, "end": v(-4792.8, -2401.5) * mm});
            skLineSegment(sketch, "E1721", {"start": v(-4792.8, -2401.5) * mm, "end": v(-4792.8, -2269.42) * mm});
            skLineSegment(sketch, "E1722", {"start": v(-4792.8, -2269.42) * mm, "end": v(-4794.87, -2263.88) * mm});
            skLineSegment(sketch, "E1723", {"start": v(-4794.87, -2263.88) * mm, "end": v(-4801.1, -2262.03) * mm});
            skLineSegment(sketch, "E1724", {"start": v(-4801.1, -2262.03) * mm, "end": v(-4806.65, -2262.03) * mm});
            skLineSegment(sketch, "E1725", {"start": v(-4806.65, -2262.03) * mm, "end": v(-4806.65, -2256.49) * mm});
            skLineSegment(sketch, "E1726", {"start": v(-4806.65, -2256.49) * mm, "end": v(-4753.08, -2256.49) * mm});
            skLineSegment(sketch, "E1727", {"start": v(-4753.08, -2256.49) * mm, "end": v(-4742.23, -2257.18) * mm});
            skLineSegment(sketch, "E1728", {"start": v(-4742.23, -2257.18) * mm, "end": v(-4732.76, -2259.26) * mm});
            skLineSegment(sketch, "E1729", {"start": v(-4732.76, -2259.26) * mm, "end": v(-4724.68, -2262.72) * mm});
            skLineSegment(sketch, "E1730", {"start": v(-4724.68, -2262.72) * mm, "end": v(-4717.98, -2267.57) * mm});
            skLineSegment(sketch, "E1731", {"start": v(-4717.98, -2267.57) * mm, "end": v(-4711.75, -2277.96) * mm});
            skLineSegment(sketch, "E1732", {"start": v(-4711.75, -2277.96) * mm, "end": v(-4709.67, -2292.5) * mm});
            skLineSegment(sketch, "E1733", {"start": v(-4709.67, -2292.5) * mm, "end": v(-4712.2, -2306.6) * mm});
            skLineSegment(sketch, "E1734", {"start": v(-4712.2, -2306.6) * mm, "end": v(-4719.83, -2317.45) * mm});
            skLineSegment(sketch, "E1735", {"start": v(-4719.83, -2317.45) * mm, "end": v(-4727.22, -2322.99) * mm});
            skLineSegment(sketch, "E1736", {"start": v(-4727.22, -2322.99) * mm, "end": v(-4738.3, -2328.53) * mm});
            skLineSegment(sketch, "E1737", {"start": v(-4738.3, -2328.53) * mm, "end": v(-4724.45, -2335) * mm});
            skLineSegment(sketch, "E1738", {"start": v(-4724.45, -2335) * mm, "end": v(-4714.29, -2343.3) * mm});
            skLineSegment(sketch, "E1739", {"start": v(-4714.29, -2343.3) * mm, "end": v(-4709.03, -2349.72) * mm});
            skLineSegment(sketch, "E1740", {"start": v(-4709.03, -2349.72) * mm, "end": v(-4705.28, -2356.93) * mm});
            skLineSegment(sketch, "E1741", {"start": v(-4705.28, -2356.93) * mm, "end": v(-4703.03, -2364.96) * mm});
            skLineSegment(sketch, "E1742", {"start": v(-4703.03, -2364.96) * mm, "end": v(-4702.28, -2373.79) * mm});
            skLineSegment(sketch, "E1743", {"start": v(-4702.28, -2373.79) * mm, "end": v(-4703.03, -2382.16) * mm});
            skLineSegment(sketch, "E1744", {"start": v(-4703.03, -2382.16) * mm, "end": v(-4705.28, -2389.72) * mm});
            skLineSegment(sketch, "E1745", {"start": v(-4705.28, -2389.72) * mm, "end": v(-4709.03, -2396.48) * mm});
            skLineSegment(sketch, "E1746", {"start": v(-4709.03, -2396.48) * mm, "end": v(-4714.29, -2402.42) * mm});
            skLineSegment(sketch, "E1747", {"start": v(-4714.29, -2402.42) * mm, "end": v(-4720.8, -2407.68) * mm});
            skLineSegment(sketch, "E1748", {"start": v(-4720.8, -2407.68) * mm, "end": v(-4728.37, -2411.43) * mm});
            skLineSegment(sketch, "E1749", {"start": v(-4728.37, -2411.43) * mm, "end": v(-4736.97, -2413.68) * mm});
            skLineSegment(sketch, "E1750", {"start": v(-4736.97, -2413.68) * mm, "end": v(-4746.61, -2414.43) * mm});
            skLineSegment(sketch, "E1751", {"start": v(-4746.61, -2414.43) * mm, "end": v(-4808.5, -2414.43) * mm});
            skLineSegment(sketch, "E1752", {"start": v(-4753.08, -2408.89) * mm, "end": v(-4740.38, -2406.8) * mm});
            skLineSegment(sketch, "E1753", {"start": v(-4740.38, -2406.8) * mm, "end": v(-4729.99, -2400.58) * mm});
            skLineSegment(sketch, "E1754", {"start": v(-4729.99, -2400.58) * mm, "end": v(-4725.54, -2394.98) * mm});
            skLineSegment(sketch, "E1755", {"start": v(-4725.54, -2394.98) * mm, "end": v(-4722.37, -2388.34) * mm});
            skLineSegment(sketch, "E1756", {"start": v(-4722.37, -2388.34) * mm, "end": v(-4719.83, -2371.94) * mm});
            skLineSegment(sketch, "E1757", {"start": v(-4719.83, -2371.94) * mm, "end": v(-4722.14, -2354.4) * mm});
            skLineSegment(sketch, "E1758", {"start": v(-4722.14, -2354.4) * mm, "end": v(-4725.02, -2347.7) * mm});
            skLineSegment(sketch, "E1759", {"start": v(-4725.02, -2347.7) * mm, "end": v(-4729.06, -2342.39) * mm});
            skLineSegment(sketch, "E1760", {"start": v(-4729.06, -2342.39) * mm, "end": v(-4734.6, -2337.94) * mm});
            skLineSegment(sketch, "E1761", {"start": v(-4734.6, -2337.94) * mm, "end": v(-4741.07, -2334.77) * mm});
            skLineSegment(sketch, "E1762", {"start": v(-4741.07, -2334.77) * mm, "end": v(-4756.77, -2332.23) * mm});
            skLineSegment(sketch, "E1763", {"start": v(-4756.77, -2332.23) * mm, "end": v(-4778.02, -2332.23) * mm});
            skLineSegment(sketch, "E1764", {"start": v(-4778.02, -2332.23) * mm, "end": v(-4778.02, -2401.5) * mm});
            skLineSegment(sketch, "E1765", {"start": v(-4778.02, -2401.5) * mm, "end": v(-4775.94, -2407.04) * mm});
            skLineSegment(sketch, "E1766", {"start": v(-4775.94, -2407.04) * mm, "end": v(-4769.7, -2408.89) * mm});
            skLineSegment(sketch, "E1767", {"start": v(-4769.7, -2408.89) * mm, "end": v(-4753.08, -2408.89) * mm});
            skLineSegment(sketch, "E1768", {"start": v(-4754, -2326.68) * mm, "end": v(-4743.84, -2324.14) * mm});
            skLineSegment(sketch, "E1769", {"start": v(-4743.84, -2324.14) * mm, "end": v(-4733.68, -2316.52) * mm});
            skLineSegment(sketch, "E1770", {"start": v(-4733.68, -2316.52) * mm, "end": v(-4727.45, -2306.83) * mm});
            skLineSegment(sketch, "E1771", {"start": v(-4727.45, -2306.83) * mm, "end": v(-4725.37, -2292.5) * mm});
            skLineSegment(sketch, "E1772", {"start": v(-4725.37, -2292.5) * mm, "end": v(-4726.99, -2279.8) * mm});
            skLineSegment(sketch, "E1773", {"start": v(-4726.99, -2279.8) * mm, "end": v(-4731.84, -2271.27) * mm});
            skLineSegment(sketch, "E1774", {"start": v(-4731.84, -2271.27) * mm, "end": v(-4743.61, -2264.34) * mm});
            skLineSegment(sketch, "E1775", {"start": v(-4743.61, -2264.34) * mm, "end": v(-4758.62, -2262.03) * mm});
            skLineSegment(sketch, "E1776", {"start": v(-4758.62, -2262.03) * mm, "end": v(-4769.7, -2262.03) * mm});
            skLineSegment(sketch, "E1777", {"start": v(-4769.7, -2262.03) * mm, "end": v(-4775.94, -2263.88) * mm});
            skLineSegment(sketch, "E1778", {"start": v(-4775.94, -2263.88) * mm, "end": v(-4778.02, -2269.42) * mm});
            skLineSegment(sketch, "E1779", {"start": v(-4778.02, -2269.42) * mm, "end": v(-4778.02, -2326.68) * mm});
            skLineSegment(sketch, "E1780", {"start": v(-4778.02, -2326.68) * mm, "end": v(-4754, -2326.68) * mm});
            skLineSegment(sketch, "E1781", {"start": v(-4635.78, -2310.98) * mm, "end": v(-4626.95, -2311.73) * mm});
            skLineSegment(sketch, "E1782", {"start": v(-4626.95, -2311.73) * mm, "end": v(-4618.92, -2313.98) * mm});
            skLineSegment(sketch, "E1783", {"start": v(-4618.92, -2313.98) * mm, "end": v(-4611.7, -2317.74) * mm});
            skLineSegment(sketch, "E1784", {"start": v(-4611.7, -2317.74) * mm, "end": v(-4605.3, -2322.99) * mm});
            skLineSegment(sketch, "E1785", {"start": v(-4605.3, -2322.99) * mm, "end": v(-4597.62, -2332.05) * mm});
            skLineSegment(sketch, "E1786", {"start": v(-4597.62, -2332.05) * mm, "end": v(-4592.14, -2341.7) * mm});
            skLineSegment(sketch, "E1787", {"start": v(-4592.14, -2341.7) * mm, "end": v(-4588.85, -2351.91) * mm});
            skLineSegment(sketch, "E1788", {"start": v(-4588.85, -2351.91) * mm, "end": v(-4587.75, -2362.7) * mm});
            skLineSegment(sketch, "E1789", {"start": v(-4587.75, -2362.7) * mm, "end": v(-4588.79, -2374.2) * mm});
            skLineSegment(sketch, "E1790", {"start": v(-4588.79, -2374.2) * mm, "end": v(-4591.9, -2384.64) * mm});
            skLineSegment(sketch, "E1791", {"start": v(-4591.9, -2384.64) * mm, "end": v(-4597.1, -2394.05) * mm});
            skLineSegment(sketch, "E1792", {"start": v(-4597.1, -2394.05) * mm, "end": v(-4604.37, -2402.42) * mm});
            skLineSegment(sketch, "E1793", {"start": v(-4604.37, -2402.42) * mm, "end": v(-4610.84, -2407.68) * mm});
            skLineSegment(sketch, "E1794", {"start": v(-4610.84, -2407.68) * mm, "end": v(-4618.23, -2411.43) * mm});
            skLineSegment(sketch, "E1795", {"start": v(-4618.23, -2411.43) * mm, "end": v(-4626.54, -2413.68) * mm});
            skLineSegment(sketch, "E1796", {"start": v(-4626.54, -2413.68) * mm, "end": v(-4635.78, -2414.43) * mm});
            skLineSegment(sketch, "E1797", {"start": v(-4635.78, -2414.43) * mm, "end": v(-4644.6, -2413.68) * mm});
            skLineSegment(sketch, "E1798", {"start": v(-4644.6, -2413.68) * mm, "end": v(-4652.63, -2411.43) * mm});
            skLineSegment(sketch, "E1799", {"start": v(-4652.63, -2411.43) * mm, "end": v(-4659.85, -2407.68) * mm});
            skLineSegment(sketch, "E1800", {"start": v(-4659.85, -2407.68) * mm, "end": v(-4666.26, -2402.42) * mm});
            skLineSegment(sketch, "E1801", {"start": v(-4666.26, -2402.42) * mm, "end": v(-4673.94, -2393.7) * mm});
            skLineSegment(sketch, "E1802", {"start": v(-4673.94, -2393.7) * mm, "end": v(-4679.42, -2384.18) * mm});
            skLineSegment(sketch, "E1803", {"start": v(-4679.42, -2384.18) * mm, "end": v(-4682.7, -2373.85) * mm});
            skLineSegment(sketch, "E1804", {"start": v(-4682.7, -2373.85) * mm, "end": v(-4683.8, -2362.7) * mm});
            skLineSegment(sketch, "E1805", {"start": v(-4683.8, -2362.7) * mm, "end": v(-4682.77, -2351.97) * mm});
            skLineSegment(sketch, "E1806", {"start": v(-4682.77, -2351.97) * mm, "end": v(-4679.65, -2341.92) * mm});
            skLineSegment(sketch, "E1807", {"start": v(-4679.65, -2341.92) * mm, "end": v(-4674.45, -2332.57) * mm});
            skLineSegment(sketch, "E1808", {"start": v(-4674.45, -2332.57) * mm, "end": v(-4667.18, -2323.91) * mm});
            skLineSegment(sketch, "E1809", {"start": v(-4667.18, -2323.91) * mm, "end": v(-4660.37, -2318.26) * mm});
            skLineSegment(sketch, "E1810", {"start": v(-4660.37, -2318.26) * mm, "end": v(-4652.86, -2314.22) * mm});
            skLineSegment(sketch, "E1811", {"start": v(-4652.86, -2314.22) * mm, "end": v(-4644.67, -2311.8) * mm});
            skLineSegment(sketch, "E1812", {"start": v(-4644.67, -2311.8) * mm, "end": v(-4635.78, -2310.98) * mm});
            skLineSegment(sketch, "E1813", {"start": v(-4635.78, -2317.45) * mm, "end": v(-4647.1, -2319.76) * mm});
            skLineSegment(sketch, "E1814", {"start": v(-4647.1, -2319.76) * mm, "end": v(-4657.02, -2326.68) * mm});
            skLineSegment(sketch, "E1815", {"start": v(-4657.02, -2326.68) * mm, "end": v(-4662.27, -2333.15) * mm});
            skLineSegment(sketch, "E1816", {"start": v(-4662.27, -2333.15) * mm, "end": v(-4666.03, -2341.46) * mm});
            skLineSegment(sketch, "E1817", {"start": v(-4666.03, -2341.46) * mm, "end": v(-4668.28, -2351.62) * mm});
            skLineSegment(sketch, "E1818", {"start": v(-4668.28, -2351.62) * mm, "end": v(-4669.03, -2363.63) * mm});
            skLineSegment(sketch, "E1819", {"start": v(-4669.03, -2363.63) * mm, "end": v(-4668.28, -2375.64) * mm});
            skLineSegment(sketch, "E1820", {"start": v(-4668.28, -2375.64) * mm, "end": v(-4666.03, -2385.8) * mm});
            skLineSegment(sketch, "E1821", {"start": v(-4666.03, -2385.8) * mm, "end": v(-4662.27, -2394.1) * mm});
            skLineSegment(sketch, "E1822", {"start": v(-4662.27, -2394.1) * mm, "end": v(-4657.02, -2400.58) * mm});
            skLineSegment(sketch, "E1823", {"start": v(-4657.02, -2400.58) * mm, "end": v(-4647.55, -2406.8) * mm});
            skLineSegment(sketch, "E1824", {"start": v(-4647.55, -2406.8) * mm, "end": v(-4635.78, -2408.89) * mm});
            skLineSegment(sketch, "E1825", {"start": v(-4635.78, -2408.89) * mm, "end": v(-4624, -2406.8) * mm});
            skLineSegment(sketch, "E1826", {"start": v(-4624, -2406.8) * mm, "end": v(-4614.53, -2400.58) * mm});
            skLineSegment(sketch, "E1827", {"start": v(-4614.53, -2400.58) * mm, "end": v(-4609.28, -2394.1) * mm});
            skLineSegment(sketch, "E1828", {"start": v(-4609.28, -2394.1) * mm, "end": v(-4605.53, -2385.8) * mm});
            skLineSegment(sketch, "E1829", {"start": v(-4605.53, -2385.8) * mm, "end": v(-4603.28, -2375.64) * mm});
            skLineSegment(sketch, "E1830", {"start": v(-4603.28, -2375.64) * mm, "end": v(-4602.53, -2363.63) * mm});
            skLineSegment(sketch, "E1831", {"start": v(-4602.53, -2363.63) * mm, "end": v(-4603.28, -2351.62) * mm});
            skLineSegment(sketch, "E1832", {"start": v(-4603.28, -2351.62) * mm, "end": v(-4605.53, -2341.46) * mm});
            skLineSegment(sketch, "E1833", {"start": v(-4605.53, -2341.46) * mm, "end": v(-4609.28, -2333.15) * mm});
            skLineSegment(sketch, "E1834", {"start": v(-4609.28, -2333.15) * mm, "end": v(-4614.53, -2326.68) * mm});
            skLineSegment(sketch, "E1835", {"start": v(-4614.53, -2326.68) * mm, "end": v(-4624.46, -2319.76) * mm});
            skLineSegment(sketch, "E1836", {"start": v(-4624.46, -2319.76) * mm, "end": v(-4635.78, -2317.45) * mm});
            skLineSegment(sketch, "E1837", {"start": v(-5571.42, -2565.9) * mm, "end": v(-5558.5, -2571.22) * mm});
            skLineSegment(sketch, "E1838", {"start": v(-5558.5, -2571.22) * mm, "end": v(-5549.25, -2577.91) * mm});
            skLineSegment(sketch, "E1839", {"start": v(-5549.25, -2577.91) * mm, "end": v(-5539.56, -2591.54) * mm});
            skLineSegment(sketch, "E1840", {"start": v(-5539.56, -2591.54) * mm, "end": v(-5537.13, -2598.87) * mm});
            skLineSegment(sketch, "E1841", {"start": v(-5537.13, -2598.87) * mm, "end": v(-5536.32, -2606.55) * mm});
            skLineSegment(sketch, "E1842", {"start": v(-5536.32, -2606.55) * mm, "end": v(-5537.19, -2615.44) * mm});
            skLineSegment(sketch, "E1843", {"start": v(-5537.19, -2615.44) * mm, "end": v(-5539.79, -2623.63) * mm});
            skLineSegment(sketch, "E1844", {"start": v(-5539.79, -2623.63) * mm, "end": v(-5544.12, -2631.14) * mm});
            skLineSegment(sketch, "E1845", {"start": v(-5544.12, -2631.14) * mm, "end": v(-5550.18, -2637.95) * mm});
            skLineSegment(sketch, "E1846", {"start": v(-5550.18, -2637.95) * mm, "end": v(-5557.22, -2643.6) * mm});
            skLineSegment(sketch, "E1847", {"start": v(-5557.22, -2643.6) * mm, "end": v(-5565.42, -2647.65) * mm});
            skLineSegment(sketch, "E1848", {"start": v(-5565.42, -2647.65) * mm, "end": v(-5574.77, -2650.07) * mm});
            skLineSegment(sketch, "E1849", {"start": v(-5574.77, -2650.07) * mm, "end": v(-5585.28, -2650.88) * mm});
            skLineSegment(sketch, "E1850", {"start": v(-5585.28, -2650.88) * mm, "end": v(-5602.6, -2648.34) * mm});
            skLineSegment(sketch, "E1851", {"start": v(-5602.6, -2648.34) * mm, "end": v(-5609.7, -2645.17) * mm});
            skLineSegment(sketch, "E1852", {"start": v(-5609.7, -2645.17) * mm, "end": v(-5615.76, -2640.72) * mm});
            skLineSegment(sketch, "E1853", {"start": v(-5615.76, -2640.72) * mm, "end": v(-5623.38, -2631.02) * mm});
            skLineSegment(sketch, "E1854", {"start": v(-5623.38, -2631.02) * mm, "end": v(-5625.92, -2620.4) * mm});
            skLineSegment(sketch, "E1855", {"start": v(-5625.92, -2620.4) * mm, "end": v(-5625, -2614.63) * mm});
            skLineSegment(sketch, "E1856", {"start": v(-5625, -2614.63) * mm, "end": v(-5622.22, -2610.24) * mm});
            skLineSegment(sketch, "E1857", {"start": v(-5622.22, -2610.24) * mm, "end": v(-5618.53, -2607.47) * mm});
            skLineSegment(sketch, "E1858", {"start": v(-5618.53, -2607.47) * mm, "end": v(-5614.83, -2606.55) * mm});
            skLineSegment(sketch, "E1859", {"start": v(-5614.83, -2606.55) * mm, "end": v(-5608.37, -2609.32) * mm});
            skLineSegment(sketch, "E1860", {"start": v(-5608.37, -2609.32) * mm, "end": v(-5605.6, -2613.24) * mm});
            skLineSegment(sketch, "E1861", {"start": v(-5605.6, -2613.24) * mm, "end": v(-5604.67, -2617.63) * mm});
            skLineSegment(sketch, "E1862", {"start": v(-5604.67, -2617.63) * mm, "end": v(-5605.6, -2623.17) * mm});
            skLineSegment(sketch, "E1863", {"start": v(-5605.6, -2623.17) * mm, "end": v(-5608.37, -2631.48) * mm});
            skLineSegment(sketch, "E1864", {"start": v(-5608.37, -2631.48) * mm, "end": v(-5607.44, -2635.18) * mm});
            skLineSegment(sketch, "E1865", {"start": v(-5607.44, -2635.18) * mm, "end": v(-5604.67, -2638.87) * mm});
            skLineSegment(sketch, "E1866", {"start": v(-5604.67, -2638.87) * mm, "end": v(-5596.82, -2643.03) * mm});
            skLineSegment(sketch, "E1867", {"start": v(-5596.82, -2643.03) * mm, "end": v(-5586.2, -2644.42) * mm});
            skLineSegment(sketch, "E1868", {"start": v(-5586.2, -2644.42) * mm, "end": v(-5573.04, -2642.34) * mm});
            skLineSegment(sketch, "E1869", {"start": v(-5573.04, -2642.34) * mm, "end": v(-5563.1, -2636.1) * mm});
            skLineSegment(sketch, "E1870", {"start": v(-5563.1, -2636.1) * mm, "end": v(-5558.66, -2630.68) * mm});
            skLineSegment(sketch, "E1871", {"start": v(-5558.66, -2630.68) * mm, "end": v(-5555.49, -2623.63) * mm});
            skLineSegment(sketch, "E1872", {"start": v(-5555.49, -2623.63) * mm, "end": v(-5552.95, -2604.7) * mm});
            skLineSegment(sketch, "E1873", {"start": v(-5552.95, -2604.7) * mm, "end": v(-5555.26, -2589.92) * mm});
            skLineSegment(sketch, "E1874", {"start": v(-5555.26, -2589.92) * mm, "end": v(-5562.18, -2578.84) * mm});
            skLineSegment(sketch, "E1875", {"start": v(-5562.18, -2578.84) * mm, "end": v(-5567.67, -2574.8) * mm});
            skLineSegment(sketch, "E1876", {"start": v(-5567.67, -2574.8) * mm, "end": v(-5574.88, -2571.9) * mm});
            skLineSegment(sketch, "E1877", {"start": v(-5574.88, -2571.9) * mm, "end": v(-5594.51, -2569.6) * mm});
            skLineSegment(sketch, "E1878", {"start": v(-5594.51, -2569.6) * mm, "end": v(-5594.51, -2563.14) * mm});
            skLineSegment(sketch, "E1879", {"start": v(-5594.51, -2563.14) * mm, "end": v(-5578.75, -2561.17) * mm});
            skLineSegment(sketch, "E1880", {"start": v(-5578.75, -2561.17) * mm, "end": v(-5567.5, -2555.28) * mm});
            skLineSegment(sketch, "E1881", {"start": v(-5567.5, -2555.28) * mm, "end": v(-5560.74, -2545.47) * mm});
            skLineSegment(sketch, "E1882", {"start": v(-5560.74, -2545.47) * mm, "end": v(-5558.5, -2531.73) * mm});
            skLineSegment(sketch, "E1883", {"start": v(-5558.5, -2531.73) * mm, "end": v(-5560.57, -2517.65) * mm});
            skLineSegment(sketch, "E1884", {"start": v(-5560.57, -2517.65) * mm, "end": v(-5566.8, -2506.8) * mm});
            skLineSegment(sketch, "E1885", {"start": v(-5566.8, -2506.8) * mm, "end": v(-5575.58, -2501.25) * mm});
            skLineSegment(sketch, "E1886", {"start": v(-5575.58, -2501.25) * mm, "end": v(-5587.12, -2499.4) * mm});
            skLineSegment(sketch, "E1887", {"start": v(-5587.12, -2499.4) * mm, "end": v(-5596.82, -2501.25) * mm});
            skLineSegment(sketch, "E1888", {"start": v(-5596.82, -2501.25) * mm, "end": v(-5605.6, -2506.8) * mm});
            skLineSegment(sketch, "E1889", {"start": v(-5605.6, -2506.8) * mm, "end": v(-5608.37, -2513.26) * mm});
            skLineSegment(sketch, "E1890", {"start": v(-5608.37, -2513.26) * mm, "end": v(-5606.52, -2520.65) * mm});
            skLineSegment(sketch, "E1891", {"start": v(-5606.52, -2520.65) * mm, "end": v(-5604.67, -2527.11) * mm});
            skLineSegment(sketch, "E1892", {"start": v(-5604.67, -2527.11) * mm, "end": v(-5606.75, -2534.73) * mm});
            skLineSegment(sketch, "E1893", {"start": v(-5606.75, -2534.73) * mm, "end": v(-5609.35, -2536.64) * mm});
            skLineSegment(sketch, "E1894", {"start": v(-5609.35, -2536.64) * mm, "end": v(-5612.98, -2537.27) * mm});
            skLineSegment(sketch, "E1895", {"start": v(-5612.98, -2537.27) * mm, "end": v(-5619.45, -2534.5) * mm});
            skLineSegment(sketch, "E1896", {"start": v(-5619.45, -2534.5) * mm, "end": v(-5622.22, -2530.12) * mm});
            skLineSegment(sketch, "E1897", {"start": v(-5622.22, -2530.12) * mm, "end": v(-5623.14, -2524.34) * mm});
            skLineSegment(sketch, "E1898", {"start": v(-5623.14, -2524.34) * mm, "end": v(-5621.07, -2513.26) * mm});
            skLineSegment(sketch, "E1899", {"start": v(-5621.07, -2513.26) * mm, "end": v(-5614.83, -2504.02) * mm});
            skLineSegment(sketch, "E1900", {"start": v(-5614.83, -2504.02) * mm, "end": v(-5608.37, -2499.17) * mm});
            skLineSegment(sketch, "E1901", {"start": v(-5608.37, -2499.17) * mm, "end": v(-5600.98, -2495.7) * mm});
            skLineSegment(sketch, "E1902", {"start": v(-5600.98, -2495.7) * mm, "end": v(-5583.43, -2492.94) * mm});
            skLineSegment(sketch, "E1903", {"start": v(-5583.43, -2492.94) * mm, "end": v(-5566.8, -2495.7) * mm});
            skLineSegment(sketch, "E1904", {"start": v(-5566.8, -2495.7) * mm, "end": v(-5559.88, -2499.17) * mm});
            skLineSegment(sketch, "E1905", {"start": v(-5559.88, -2499.17) * mm, "end": v(-5553.87, -2504.02) * mm});
            skLineSegment(sketch, "E1906", {"start": v(-5553.87, -2504.02) * mm, "end": v(-5545.56, -2515.8) * mm});
            skLineSegment(sketch, "E1907", {"start": v(-5545.56, -2515.8) * mm, "end": v(-5542.79, -2528.96) * mm});
            skLineSegment(sketch, "E1908", {"start": v(-5542.79, -2528.96) * mm, "end": v(-5544.58, -2541.31) * mm});
            skLineSegment(sketch, "E1909", {"start": v(-5544.58, -2541.31) * mm, "end": v(-5549.95, -2551.59) * mm});
            skLineSegment(sketch, "E1910", {"start": v(-5549.95, -2551.59) * mm, "end": v(-5558.9, -2559.79) * mm});
            skLineSegment(sketch, "E1911", {"start": v(-5558.9, -2559.79) * mm, "end": v(-5571.42, -2565.9) * mm});
            skLineSegment(sketch, "E1912", {"start": v(-5395.93, -2550.2) * mm, "end": v(-5395.93, -2541.9) * mm});
            skLineSegment(sketch, "E1913", {"start": v(-5395.93, -2541.9) * mm, "end": v(-5293.4, -2541.9) * mm});
            skLineSegment(sketch, "E1914", {"start": v(-5293.4, -2541.9) * mm, "end": v(-5293.4, -2550.2) * mm});
            skLineSegment(sketch, "E1915", {"start": v(-5293.4, -2550.2) * mm, "end": v(-5395.93, -2550.2) * mm});
            skLineSegment(sketch, "E1916", {"start": v(-5395.93, -2597.3) * mm, "end": v(-5395.93, -2589) * mm});
            skLineSegment(sketch, "E1917", {"start": v(-5395.93, -2589) * mm, "end": v(-5293.4, -2589) * mm});
            skLineSegment(sketch, "E1918", {"start": v(-5293.4, -2589) * mm, "end": v(-5293.4, -2597.3) * mm});
            skLineSegment(sketch, "E1919", {"start": v(-5293.4, -2597.3) * mm, "end": v(-5395.93, -2597.3) * mm});
            skLineSegment(sketch, "E1920", {"start": v(-5075.43, -2610.24) * mm, "end": v(-5077.5, -2601.93) * mm});
            skLineSegment(sketch, "E1921", {"start": v(-5077.5, -2601.93) * mm, "end": v(-5083.74, -2593.62) * mm});
            skLineSegment(sketch, "E1922", {"start": v(-5083.74, -2593.62) * mm, "end": v(-5098.29, -2581.84) * mm});
            skLineSegment(sketch, "E1923", {"start": v(-5098.29, -2581.84) * mm, "end": v(-5116.07, -2572.37) * mm});
            skLineSegment(sketch, "E1924", {"start": v(-5116.07, -2572.37) * mm, "end": v(-5132.92, -2564.29) * mm});
            skLineSegment(sketch, "E1925", {"start": v(-5132.92, -2564.29) * mm, "end": v(-5144.7, -2556.67) * mm});
            skLineSegment(sketch, "E1926", {"start": v(-5144.7, -2556.67) * mm, "end": v(-5149.15, -2552) * mm});
            skLineSegment(sketch, "E1927", {"start": v(-5149.15, -2552) * mm, "end": v(-5152.32, -2546.28) * mm});
            skLineSegment(sketch, "E1928", {"start": v(-5152.32, -2546.28) * mm, "end": v(-5154.86, -2531.73) * mm});
            skLineSegment(sketch, "E1929", {"start": v(-5154.86, -2531.73) * mm, "end": v(-5154.11, -2524.11) * mm});
            skLineSegment(sketch, "E1930", {"start": v(-5154.11, -2524.11) * mm, "end": v(-5151.86, -2516.95) * mm});
            skLineSegment(sketch, "E1931", {"start": v(-5151.86, -2516.95) * mm, "end": v(-5142.85, -2504.02) * mm});
            skLineSegment(sketch, "E1932", {"start": v(-5142.85, -2504.02) * mm, "end": v(-5136.68, -2499.17) * mm});
            skLineSegment(sketch, "E1933", {"start": v(-5136.68, -2499.17) * mm, "end": v(-5129.23, -2495.7) * mm});
            skLineSegment(sketch, "E1934", {"start": v(-5129.23, -2495.7) * mm, "end": v(-5120.51, -2493.63) * mm});
            skLineSegment(sketch, "E1935", {"start": v(-5120.51, -2493.63) * mm, "end": v(-5110.53, -2492.94) * mm});
            skLineSegment(sketch, "E1936", {"start": v(-5110.53, -2492.94) * mm, "end": v(-5100.83, -2493.86) * mm});
            skLineSegment(sketch, "E1937", {"start": v(-5100.83, -2493.86) * mm, "end": v(-5092.05, -2496.63) * mm});
            skLineSegment(sketch, "E1938", {"start": v(-5092.05, -2496.63) * mm, "end": v(-5080.97, -2499.4) * mm});
            skLineSegment(sketch, "E1939", {"start": v(-5080.97, -2499.4) * mm, "end": v(-5076.35, -2497.79) * mm});
            skLineSegment(sketch, "E1940", {"start": v(-5076.35, -2497.79) * mm, "end": v(-5071.73, -2492.94) * mm});
            skLineSegment(sketch, "E1941", {"start": v(-5071.73, -2492.94) * mm, "end": v(-5068.04, -2530.8) * mm});
            skLineSegment(sketch, "E1942", {"start": v(-5068.04, -2530.8) * mm, "end": v(-5073.58, -2533.58) * mm});
            skLineSegment(sketch, "E1943", {"start": v(-5073.58, -2533.58) * mm, "end": v(-5080.97, -2517.42) * mm});
            skLineSegment(sketch, "E1944", {"start": v(-5080.97, -2517.42) * mm, "end": v(-5088.36, -2507.72) * mm});
            skLineSegment(sketch, "E1945", {"start": v(-5088.36, -2507.72) * mm, "end": v(-5098.98, -2501.48) * mm});
            skLineSegment(sketch, "E1946", {"start": v(-5098.98, -2501.48) * mm, "end": v(-5112.37, -2499.4) * mm});
            skLineSegment(sketch, "E1947", {"start": v(-5112.37, -2499.4) * mm, "end": v(-5125.07, -2501.02) * mm});
            skLineSegment(sketch, "E1948", {"start": v(-5125.07, -2501.02) * mm, "end": v(-5133.62, -2505.87) * mm});
            skLineSegment(sketch, "E1949", {"start": v(-5133.62, -2505.87) * mm, "end": v(-5140.54, -2515.57) * mm});
            skLineSegment(sketch, "E1950", {"start": v(-5140.54, -2515.57) * mm, "end": v(-5142.85, -2528.04) * mm});
            skLineSegment(sketch, "E1951", {"start": v(-5142.85, -2528.04) * mm, "end": v(-5140.54, -2539.35) * mm});
            skLineSegment(sketch, "E1952", {"start": v(-5140.54, -2539.35) * mm, "end": v(-5133.62, -2547.43) * mm});
            skLineSegment(sketch, "E1953", {"start": v(-5133.62, -2547.43) * mm, "end": v(-5108.68, -2559.44) * mm});
            skLineSegment(sketch, "E1954", {"start": v(-5108.68, -2559.44) * mm, "end": v(-5088.13, -2570.52) * mm});
            skLineSegment(sketch, "E1955", {"start": v(-5088.13, -2570.52) * mm, "end": v(-5072.66, -2583.46) * mm});
            skLineSegment(sketch, "E1956", {"start": v(-5072.66, -2583.46) * mm, "end": v(-5065.04, -2595.7) * mm});
            skLineSegment(sketch, "E1957", {"start": v(-5065.04, -2595.7) * mm, "end": v(-5062.5, -2610.24) * mm});
            skLineSegment(sketch, "E1958", {"start": v(-5062.5, -2610.24) * mm, "end": v(-5063.25, -2618.26) * mm});
            skLineSegment(sketch, "E1959", {"start": v(-5063.25, -2618.26) * mm, "end": v(-5065.5, -2625.71) * mm});
            skLineSegment(sketch, "E1960", {"start": v(-5065.5, -2625.71) * mm, "end": v(-5069.25, -2632.58) * mm});
            skLineSegment(sketch, "E1961", {"start": v(-5069.25, -2632.58) * mm, "end": v(-5074.5, -2638.87) * mm});
            skLineSegment(sketch, "E1962", {"start": v(-5074.5, -2638.87) * mm, "end": v(-5081.09, -2644.13) * mm});
            skLineSegment(sketch, "E1963", {"start": v(-5081.09, -2644.13) * mm, "end": v(-5088.82, -2647.88) * mm});
            skLineSegment(sketch, "E1964", {"start": v(-5088.82, -2647.88) * mm, "end": v(-5097.71, -2650.13) * mm});
            skLineSegment(sketch, "E1965", {"start": v(-5097.71, -2650.13) * mm, "end": v(-5107.76, -2650.88) * mm});
            skLineSegment(sketch, "E1966", {"start": v(-5107.76, -2650.88) * mm, "end": v(-5118.15, -2649.96) * mm});
            skLineSegment(sketch, "E1967", {"start": v(-5118.15, -2649.96) * mm, "end": v(-5127.15, -2647.19) * mm});
            skLineSegment(sketch, "E1968", {"start": v(-5127.15, -2647.19) * mm, "end": v(-5137.31, -2644.42) * mm});
            skLineSegment(sketch, "E1969", {"start": v(-5137.31, -2644.42) * mm, "end": v(-5143.08, -2646.03) * mm});
            skLineSegment(sketch, "E1970", {"start": v(-5143.08, -2646.03) * mm, "end": v(-5149.32, -2650.88) * mm});
            skLineSegment(sketch, "E1971", {"start": v(-5149.32, -2650.88) * mm, "end": v(-5156.7, -2605.62) * mm});
            skLineSegment(sketch, "E1972", {"start": v(-5156.7, -2605.62) * mm, "end": v(-5151.17, -2602.85) * mm});
            skLineSegment(sketch, "E1973", {"start": v(-5151.17, -2602.85) * mm, "end": v(-5143.78, -2623.17) * mm});
            skLineSegment(sketch, "E1974", {"start": v(-5143.78, -2623.17) * mm, "end": v(-5136.39, -2634.26) * mm});
            skLineSegment(sketch, "E1975", {"start": v(-5136.39, -2634.26) * mm, "end": v(-5130.38, -2638.7) * mm});
            skLineSegment(sketch, "E1976", {"start": v(-5130.38, -2638.7) * mm, "end": v(-5123.46, -2641.88) * mm});
            skLineSegment(sketch, "E1977", {"start": v(-5123.46, -2641.88) * mm, "end": v(-5106.83, -2644.42) * mm});
            skLineSegment(sketch, "E1978", {"start": v(-5106.83, -2644.42) * mm, "end": v(-5093.9, -2642.57) * mm});
            skLineSegment(sketch, "E1979", {"start": v(-5093.9, -2642.57) * mm, "end": v(-5084.66, -2637.03) * mm});
            skLineSegment(sketch, "E1980", {"start": v(-5084.66, -2637.03) * mm, "end": v(-5080.62, -2632.23) * mm});
            skLineSegment(sketch, "E1981", {"start": v(-5080.62, -2632.23) * mm, "end": v(-5077.74, -2626.17) * mm});
            skLineSegment(sketch, "E1982", {"start": v(-5077.74, -2626.17) * mm, "end": v(-5075.43, -2610.24) * mm});
            skLineSegment(sketch, "E1983", {"start": v(-4967.36, -2638.87) * mm, "end": v(-4985.6, -2647.88) * mm});
            skLineSegment(sketch, "E1984", {"start": v(-4985.6, -2647.88) * mm, "end": v(-5003.38, -2650.88) * mm});
            skLineSegment(sketch, "E1985", {"start": v(-5003.38, -2650.88) * mm, "end": v(-5018.86, -2648.8) * mm});
            skLineSegment(sketch, "E1986", {"start": v(-5018.86, -2648.8) * mm, "end": v(-5030.17, -2642.57) * mm});
            skLineSegment(sketch, "E1987", {"start": v(-5030.17, -2642.57) * mm, "end": v(-5036.4, -2634.72) * mm});
            skLineSegment(sketch, "E1988", {"start": v(-5036.4, -2634.72) * mm, "end": v(-5038.48, -2625.94) * mm});
            skLineSegment(sketch, "E1989", {"start": v(-5038.48, -2625.94) * mm, "end": v(-5035.94, -2616.48) * mm});
            skLineSegment(sketch, "E1990", {"start": v(-5035.94, -2616.48) * mm, "end": v(-5028.32, -2606.55) * mm});
            skLineSegment(sketch, "E1991", {"start": v(-5028.32, -2606.55) * mm, "end": v(-5019.32, -2599.9) * mm});
            skLineSegment(sketch, "E1992", {"start": v(-5019.32, -2599.9) * mm, "end": v(-5006.16, -2593.85) * mm});
            skLineSegment(sketch, "E1993", {"start": v(-5006.16, -2593.85) * mm, "end": v(-4988.84, -2588.36) * mm});
            skLineSegment(sketch, "E1994", {"start": v(-4988.84, -2588.36) * mm, "end": v(-4967.36, -2583.46) * mm});
            skLineSegment(sketch, "E1995", {"start": v(-4967.36, -2583.46) * mm, "end": v(-4967.36, -2570.52) * mm});
            skLineSegment(sketch, "E1996", {"start": v(-4967.36, -2570.52) * mm, "end": v(-4968.52, -2563.14) * mm});
            skLineSegment(sketch, "E1997", {"start": v(-4968.52, -2563.14) * mm, "end": v(-4971.98, -2557.6) * mm});
            skLineSegment(sketch, "E1998", {"start": v(-4971.98, -2557.6) * mm, "end": v(-4978.9, -2554.13) * mm});
            skLineSegment(sketch, "E1999", {"start": v(-4978.9, -2554.13) * mm, "end": v(-4990.45, -2552.98) * mm});
            skLineSegment(sketch, "E2000", {"start": v(-4990.45, -2552.98) * mm, "end": v(-5002.7, -2554.13) * mm});
            skLineSegment(sketch, "E2001", {"start": v(-5002.7, -2554.13) * mm, "end": v(-5011.7, -2557.6) * mm});
            skLineSegment(sketch, "E2002", {"start": v(-5011.7, -2557.6) * mm, "end": v(-5017.24, -2563.14) * mm});
            skLineSegment(sketch, "E2003", {"start": v(-5017.24, -2563.14) * mm, "end": v(-5017.24, -2568.68) * mm});
            skLineSegment(sketch, "E2004", {"start": v(-5017.24, -2568.68) * mm, "end": v(-5016.32, -2571.9) * mm});
            skLineSegment(sketch, "E2005", {"start": v(-5016.32, -2571.9) * mm, "end": v(-5017.24, -2576.07) * mm});
            skLineSegment(sketch, "E2006", {"start": v(-5017.24, -2576.07) * mm, "end": v(-5020.01, -2578.84) * mm});
            skLineSegment(sketch, "E2007", {"start": v(-5020.01, -2578.84) * mm, "end": v(-5024.63, -2579.76) * mm});
            skLineSegment(sketch, "E2008", {"start": v(-5024.63, -2579.76) * mm, "end": v(-5030.86, -2577.45) * mm});
            skLineSegment(sketch, "E2009", {"start": v(-5030.86, -2577.45) * mm, "end": v(-5032.94, -2570.52) * mm});
            skLineSegment(sketch, "E2010", {"start": v(-5032.94, -2570.52) * mm, "end": v(-5031.56, -2564.29) * mm});
            skLineSegment(sketch, "E2011", {"start": v(-5031.56, -2564.29) * mm, "end": v(-5027.4, -2558.52) * mm});
            skLineSegment(sketch, "E2012", {"start": v(-5027.4, -2558.52) * mm, "end": v(-5021, -2553.67) * mm});
            skLineSegment(sketch, "E2013", {"start": v(-5021, -2553.67) * mm, "end": v(-5012.85, -2550.2) * mm});
            skLineSegment(sketch, "E2014", {"start": v(-5012.85, -2550.2) * mm, "end": v(-5002.98, -2548.13) * mm});
            skLineSegment(sketch, "E2015", {"start": v(-5002.98, -2548.13) * mm, "end": v(-4991.38, -2547.43) * mm});
            skLineSegment(sketch, "E2016", {"start": v(-4991.38, -2547.43) * mm, "end": v(-4972.67, -2549.51) * mm});
            skLineSegment(sketch, "E2017", {"start": v(-4972.67, -2549.51) * mm, "end": v(-4965.92, -2552.1) * mm});
            skLineSegment(sketch, "E2018", {"start": v(-4965.92, -2552.1) * mm, "end": v(-4960.9, -2555.75) * mm});
            skLineSegment(sketch, "E2019", {"start": v(-4960.9, -2555.75) * mm, "end": v(-4956.05, -2563.14) * mm});
            skLineSegment(sketch, "E2020", {"start": v(-4956.05, -2563.14) * mm, "end": v(-4954.43, -2572.37) * mm});
            skLineSegment(sketch, "E2021", {"start": v(-4954.43, -2572.37) * mm, "end": v(-4954.43, -2640.72) * mm});
            skLineSegment(sketch, "E2022", {"start": v(-4954.43, -2640.72) * mm, "end": v(-4953.5, -2643.5) * mm});
            skLineSegment(sketch, "E2023", {"start": v(-4953.5, -2643.5) * mm, "end": v(-4950.74, -2644.42) * mm});
            skLineSegment(sketch, "E2024", {"start": v(-4950.74, -2644.42) * mm, "end": v(-4947.74, -2641.64) * mm});
            skLineSegment(sketch, "E2025", {"start": v(-4947.74, -2641.64) * mm, "end": v(-4944.27, -2633.33) * mm});
            skLineSegment(sketch, "E2026", {"start": v(-4944.27, -2633.33) * mm, "end": v(-4939.65, -2631.48) * mm});
            skLineSegment(sketch, "E2027", {"start": v(-4939.65, -2631.48) * mm, "end": v(-4942.37, -2639.97) * mm});
            skLineSegment(sketch, "E2028", {"start": v(-4942.37, -2639.97) * mm, "end": v(-4945.89, -2646.03) * mm});
            skLineSegment(sketch, "E2029", {"start": v(-4945.89, -2646.03) * mm, "end": v(-4950.22, -2649.67) * mm});
            skLineSegment(sketch, "E2030", {"start": v(-4950.22, -2649.67) * mm, "end": v(-4955.36, -2650.88) * mm});
            skLineSegment(sketch, "E2031", {"start": v(-4955.36, -2650.88) * mm, "end": v(-4959.57, -2650.13) * mm});
            skLineSegment(sketch, "E2032", {"start": v(-4959.57, -2650.13) * mm, "end": v(-4962.98, -2647.88) * mm});
            skLineSegment(sketch, "E2033", {"start": v(-4962.98, -2647.88) * mm, "end": v(-4967.36, -2638.87) * mm});
            skLineSegment(sketch, "E2034", {"start": v(-4967.36, -2589.92) * mm, "end": v(-4996.46, -2598.23) * mm});
            skLineSegment(sketch, "E2035", {"start": v(-4996.46, -2598.23) * mm, "end": v(-5006.5, -2603.08) * mm});
            skLineSegment(sketch, "E2036", {"start": v(-5006.5, -2603.08) * mm, "end": v(-5013.54, -2608.4) * mm});
            skLineSegment(sketch, "E2037", {"start": v(-5013.54, -2608.4) * mm, "end": v(-5020.47, -2617.4) * mm});
            skLineSegment(sketch, "E2038", {"start": v(-5020.47, -2617.4) * mm, "end": v(-5022.78, -2625.94) * mm});
            skLineSegment(sketch, "E2039", {"start": v(-5022.78, -2625.94) * mm, "end": v(-5021.16, -2632.87) * mm});
            skLineSegment(sketch, "E2040", {"start": v(-5021.16, -2632.87) * mm, "end": v(-5016.32, -2638.87) * mm});
            skLineSegment(sketch, "E2041", {"start": v(-5016.32, -2638.87) * mm, "end": v(-5009.39, -2643.03) * mm});
            skLineSegment(sketch, "E2042", {"start": v(-5009.39, -2643.03) * mm, "end": v(-5001.54, -2644.42) * mm});
            skLineSegment(sketch, "E2043", {"start": v(-5001.54, -2644.42) * mm, "end": v(-4985.14, -2641.41) * mm});
            skLineSegment(sketch, "E2044", {"start": v(-4985.14, -2641.41) * mm, "end": v(-4967.36, -2632.4) * mm});
            skLineSegment(sketch, "E2045", {"start": v(-4967.36, -2632.4) * mm, "end": v(-4967.36, -2589.92) * mm});
            skLineSegment(sketch, "E2046", {"start": v(-4910.1, -2558.52) * mm, "end": v(-4911.25, -2554.36) * mm});
            skLineSegment(sketch, "E2047", {"start": v(-4911.25, -2554.36) * mm, "end": v(-4914.72, -2552.98) * mm});
            skLineSegment(sketch, "E2048", {"start": v(-4914.72, -2552.98) * mm, "end": v(-4922.1, -2552.98) * mm});
            skLineSegment(sketch, "E2049", {"start": v(-4922.1, -2552.98) * mm, "end": v(-4922.1, -2547.43) * mm});
            skLineSegment(sketch, "E2050", {"start": v(-4922.1, -2547.43) * mm, "end": v(-4915.64, -2547.43) * mm});
            skLineSegment(sketch, "E2051", {"start": v(-4915.64, -2547.43) * mm, "end": v(-4907.33, -2546.28) * mm});
            skLineSegment(sketch, "E2052", {"start": v(-4907.33, -2546.28) * mm, "end": v(-4899.01, -2542.82) * mm});
            skLineSegment(sketch, "E2053", {"start": v(-4899.01, -2542.82) * mm, "end": v(-4897.17, -2542.82) * mm});
            skLineSegment(sketch, "E2054", {"start": v(-4897.17, -2542.82) * mm, "end": v(-4897.17, -2565.9) * mm});
            skLineSegment(sketch, "E2055", {"start": v(-4897.17, -2565.9) * mm, "end": v(-4889.14, -2557.82) * mm});
            skLineSegment(sketch, "E2056", {"start": v(-4889.14, -2557.82) * mm, "end": v(-4880.77, -2552.05) * mm});
            skLineSegment(sketch, "E2057", {"start": v(-4880.77, -2552.05) * mm, "end": v(-4872.06, -2548.59) * mm});
            skLineSegment(sketch, "E2058", {"start": v(-4872.06, -2548.59) * mm, "end": v(-4863, -2547.43) * mm});
            skLineSegment(sketch, "E2059", {"start": v(-4863, -2547.43) * mm, "end": v(-4849.66, -2549.51) * mm});
            skLineSegment(sketch, "E2060", {"start": v(-4849.66, -2549.51) * mm, "end": v(-4840.13, -2555.75) * mm});
            skLineSegment(sketch, "E2061", {"start": v(-4840.13, -2555.75) * mm, "end": v(-4834.42, -2566.14) * mm});
            skLineSegment(sketch, "E2062", {"start": v(-4834.42, -2566.14) * mm, "end": v(-4832.51, -2580.68) * mm});
            skLineSegment(sketch, "E2063", {"start": v(-4832.51, -2580.68) * mm, "end": v(-4832.51, -2637.95) * mm});
            skLineSegment(sketch, "E2064", {"start": v(-4832.51, -2637.95) * mm, "end": v(-4830.43, -2643.5) * mm});
            skLineSegment(sketch, "E2065", {"start": v(-4830.43, -2643.5) * mm, "end": v(-4824.2, -2645.34) * mm});
            skLineSegment(sketch, "E2066", {"start": v(-4824.2, -2645.34) * mm, "end": v(-4819.58, -2645.34) * mm});
            skLineSegment(sketch, "E2067", {"start": v(-4819.58, -2645.34) * mm, "end": v(-4819.58, -2650.88) * mm});
            skLineSegment(sketch, "E2068", {"start": v(-4819.58, -2650.88) * mm, "end": v(-4858.37, -2650.88) * mm});
            skLineSegment(sketch, "E2069", {"start": v(-4858.37, -2650.88) * mm, "end": v(-4858.37, -2645.34) * mm});
            skLineSegment(sketch, "E2070", {"start": v(-4858.37, -2645.34) * mm, "end": v(-4853.76, -2645.34) * mm});
            skLineSegment(sketch, "E2071", {"start": v(-4853.76, -2645.34) * mm, "end": v(-4847.52, -2643.5) * mm});
            skLineSegment(sketch, "E2072", {"start": v(-4847.52, -2643.5) * mm, "end": v(-4845.44, -2637.95) * mm});
            skLineSegment(sketch, "E2073", {"start": v(-4845.44, -2637.95) * mm, "end": v(-4845.44, -2577.91) * mm});
            skLineSegment(sketch, "E2074", {"start": v(-4845.44, -2577.91) * mm, "end": v(-4846.77, -2567.81) * mm});
            skLineSegment(sketch, "E2075", {"start": v(-4846.77, -2567.81) * mm, "end": v(-4850.75, -2560.6) * mm});
            skLineSegment(sketch, "E2076", {"start": v(-4850.75, -2560.6) * mm, "end": v(-4857.4, -2556.27) * mm});
            skLineSegment(sketch, "E2077", {"start": v(-4857.4, -2556.27) * mm, "end": v(-4866.69, -2554.82) * mm});
            skLineSegment(sketch, "E2078", {"start": v(-4866.69, -2554.82) * mm, "end": v(-4874.83, -2556.15) * mm});
            skLineSegment(sketch, "E2079", {"start": v(-4874.83, -2556.15) * mm, "end": v(-4882.62, -2560.13) * mm});
            skLineSegment(sketch, "E2080", {"start": v(-4882.62, -2560.13) * mm, "end": v(-4890.07, -2566.77) * mm});
            skLineSegment(sketch, "E2081", {"start": v(-4890.07, -2566.77) * mm, "end": v(-4897.17, -2576.07) * mm});
            skLineSegment(sketch, "E2082", {"start": v(-4897.17, -2576.07) * mm, "end": v(-4897.17, -2637.95) * mm});
            skLineSegment(sketch, "E2083", {"start": v(-4897.17, -2637.95) * mm, "end": v(-4895.09, -2643.5) * mm});
            skLineSegment(sketch, "E2084", {"start": v(-4895.09, -2643.5) * mm, "end": v(-4888.85, -2645.34) * mm});
            skLineSegment(sketch, "E2085", {"start": v(-4888.85, -2645.34) * mm, "end": v(-4884.24, -2645.34) * mm});
            skLineSegment(sketch, "E2086", {"start": v(-4884.24, -2645.34) * mm, "end": v(-4884.24, -2650.88) * mm});
            skLineSegment(sketch, "E2087", {"start": v(-4884.24, -2650.88) * mm, "end": v(-4923.03, -2650.88) * mm});
            skLineSegment(sketch, "E2088", {"start": v(-4923.03, -2650.88) * mm, "end": v(-4923.03, -2645.34) * mm});
            skLineSegment(sketch, "E2089", {"start": v(-4923.03, -2645.34) * mm, "end": v(-4918.41, -2645.34) * mm});
            skLineSegment(sketch, "E2090", {"start": v(-4918.41, -2645.34) * mm, "end": v(-4912.18, -2643.5) * mm});
            skLineSegment(sketch, "E2091", {"start": v(-4912.18, -2643.5) * mm, "end": v(-4910.1, -2637.95) * mm});
            skLineSegment(sketch, "E2092", {"start": v(-4910.1, -2637.95) * mm, "end": v(-4910.1, -2558.52) * mm});
            skLineSegment(sketch, "E2093", {"start": v(-4755.85, -2552.98) * mm, "end": v(-4764.62, -2554.82) * mm});
            skLineSegment(sketch, "E2094", {"start": v(-4764.62, -2554.82) * mm, "end": v(-4772.48, -2560.36) * mm});
            skLineSegment(sketch, "E2095", {"start": v(-4772.48, -2560.36) * mm, "end": v(-4778.02, -2569.6) * mm});
            skLineSegment(sketch, "E2096", {"start": v(-4778.02, -2569.6) * mm, "end": v(-4779.86, -2582.53) * mm});
            skLineSegment(sketch, "E2097", {"start": v(-4779.86, -2582.53) * mm, "end": v(-4778.02, -2592.7) * mm});
            skLineSegment(sketch, "E2098", {"start": v(-4778.02, -2592.7) * mm, "end": v(-4772.48, -2601) * mm});
            skLineSegment(sketch, "E2099", {"start": v(-4772.48, -2601) * mm, "end": v(-4764.62, -2606.55) * mm});
            skLineSegment(sketch, "E2100", {"start": v(-4764.62, -2606.55) * mm, "end": v(-4755.85, -2608.4) * mm});
            skLineSegment(sketch, "E2101", {"start": v(-4755.85, -2608.4) * mm, "end": v(-4747.08, -2606.55) * mm});
            skLineSegment(sketch, "E2102", {"start": v(-4747.08, -2606.55) * mm, "end": v(-4739.22, -2601) * mm});
            skLineSegment(sketch, "E2103", {"start": v(-4739.22, -2601) * mm, "end": v(-4733.68, -2592.7) * mm});
            skLineSegment(sketch, "E2104", {"start": v(-4733.68, -2592.7) * mm, "end": v(-4731.84, -2582.53) * mm});
            skLineSegment(sketch, "E2105", {"start": v(-4731.84, -2582.53) * mm, "end": v(-4733.68, -2569.6) * mm});
            skLineSegment(sketch, "E2106", {"start": v(-4733.68, -2569.6) * mm, "end": v(-4739.22, -2560.36) * mm});
            skLineSegment(sketch, "E2107", {"start": v(-4739.22, -2560.36) * mm, "end": v(-4747.08, -2554.82) * mm});
            skLineSegment(sketch, "E2108", {"start": v(-4747.08, -2554.82) * mm, "end": v(-4755.85, -2552.98) * mm});
            skLineSegment(sketch, "E2109", {"start": v(-4773.4, -2626.87) * mm, "end": v(-4734.6, -2632.4) * mm});
            skLineSegment(sketch, "E2110", {"start": v(-4734.6, -2632.4) * mm, "end": v(-4722.89, -2635.35) * mm});
            skLineSegment(sketch, "E2111", {"start": v(-4722.89, -2635.35) * mm, "end": v(-4714.52, -2640.49) * mm});
            skLineSegment(sketch, "E2112", {"start": v(-4714.52, -2640.49) * mm, "end": v(-4709.5, -2647.82) * mm});
            skLineSegment(sketch, "E2113", {"start": v(-4709.5, -2647.82) * mm, "end": v(-4707.82, -2657.35) * mm});
            skLineSegment(sketch, "E2114", {"start": v(-4707.82, -2657.35) * mm, "end": v(-4709.67, -2665.43) * mm});
            skLineSegment(sketch, "E2115", {"start": v(-4709.67, -2665.43) * mm, "end": v(-4715.21, -2673.05) * mm});
            skLineSegment(sketch, "E2116", {"start": v(-4715.21, -2673.05) * mm, "end": v(-4721.9, -2677.9) * mm});
            skLineSegment(sketch, "E2117", {"start": v(-4721.9, -2677.9) * mm, "end": v(-4730.91, -2681.36) * mm});
            skLineSegment(sketch, "E2118", {"start": v(-4730.91, -2681.36) * mm, "end": v(-4742.23, -2683.44) * mm});
            skLineSegment(sketch, "E2119", {"start": v(-4742.23, -2683.44) * mm, "end": v(-4755.85, -2684.13) * mm});
            skLineSegment(sketch, "E2120", {"start": v(-4755.85, -2684.13) * mm, "end": v(-4767.86, -2683.44) * mm});
            skLineSegment(sketch, "E2121", {"start": v(-4767.86, -2683.44) * mm, "end": v(-4778.02, -2681.36) * mm});
            skLineSegment(sketch, "E2122", {"start": v(-4778.02, -2681.36) * mm, "end": v(-4786.33, -2677.9) * mm});
            skLineSegment(sketch, "E2123", {"start": v(-4786.33, -2677.9) * mm, "end": v(-4792.8, -2673.05) * mm});
            skLineSegment(sketch, "E2124", {"start": v(-4792.8, -2673.05) * mm, "end": v(-4797.64, -2666.35) * mm});
            skLineSegment(sketch, "E2125", {"start": v(-4797.64, -2666.35) * mm, "end": v(-4799.26, -2659.2) * mm});
            skLineSegment(sketch, "E2126", {"start": v(-4799.26, -2659.2) * mm, "end": v(-4798.05, -2653.36) * mm});
            skLineSegment(sketch, "E2127", {"start": v(-4798.05, -2653.36) * mm, "end": v(-4794.41, -2647.88) * mm});
            skLineSegment(sketch, "E2128", {"start": v(-4794.41, -2647.88) * mm, "end": v(-4788.35, -2642.74) * mm});
            skLineSegment(sketch, "E2129", {"start": v(-4788.35, -2642.74) * mm, "end": v(-4779.86, -2637.95) * mm});
            skLineSegment(sketch, "E2130", {"start": v(-4779.86, -2637.95) * mm, "end": v(-4788.87, -2630.8) * mm});
            skLineSegment(sketch, "E2131", {"start": v(-4788.87, -2630.8) * mm, "end": v(-4791.12, -2626.7) * mm});
            skLineSegment(sketch, "E2132", {"start": v(-4791.12, -2626.7) * mm, "end": v(-4791.87, -2622.25) * mm});
            skLineSegment(sketch, "E2133", {"start": v(-4791.87, -2622.25) * mm, "end": v(-4788.64, -2615.78) * mm});
            skLineSegment(sketch, "E2134", {"start": v(-4788.64, -2615.78) * mm, "end": v(-4778.94, -2607.47) * mm});
            skLineSegment(sketch, "E2135", {"start": v(-4778.94, -2607.47) * mm, "end": v(-4785, -2601.75) * mm});
            skLineSegment(sketch, "E2136", {"start": v(-4785, -2601.75) * mm, "end": v(-4789.33, -2595.7) * mm});
            skLineSegment(sketch, "E2137", {"start": v(-4789.33, -2595.7) * mm, "end": v(-4791.93, -2589.29) * mm});
            skLineSegment(sketch, "E2138", {"start": v(-4791.93, -2589.29) * mm, "end": v(-4792.8, -2582.53) * mm});
            skLineSegment(sketch, "E2139", {"start": v(-4792.8, -2582.53) * mm, "end": v(-4790.02, -2569.37) * mm});
            skLineSegment(sketch, "E2140", {"start": v(-4790.02, -2569.37) * mm, "end": v(-4781.71, -2557.6) * mm});
            skLineSegment(sketch, "E2141", {"start": v(-4781.71, -2557.6) * mm, "end": v(-4770.17, -2549.97) * mm});
            skLineSegment(sketch, "E2142", {"start": v(-4770.17, -2549.97) * mm, "end": v(-4755.85, -2547.43) * mm});
            skLineSegment(sketch, "E2143", {"start": v(-4755.85, -2547.43) * mm, "end": v(-4742, -2549.51) * mm});
            skLineSegment(sketch, "E2144", {"start": v(-4742, -2549.51) * mm, "end": v(-4729.99, -2555.75) * mm});
            skLineSegment(sketch, "E2145", {"start": v(-4729.99, -2555.75) * mm, "end": v(-4718.9, -2549.51) * mm});
            skLineSegment(sketch, "E2146", {"start": v(-4718.9, -2549.51) * mm, "end": v(-4711.52, -2547.43) * mm});
            skLineSegment(sketch, "E2147", {"start": v(-4711.52, -2547.43) * mm, "end": v(-4704.13, -2549.28) * mm});
            skLineSegment(sketch, "E2148", {"start": v(-4704.13, -2549.28) * mm, "end": v(-4701.36, -2555.75) * mm});
            skLineSegment(sketch, "E2149", {"start": v(-4701.36, -2555.75) * mm, "end": v(-4702.97, -2561.29) * mm});
            skLineSegment(sketch, "E2150", {"start": v(-4702.97, -2561.29) * mm, "end": v(-4707.82, -2563.14) * mm});
            skLineSegment(sketch, "E2151", {"start": v(-4707.82, -2563.14) * mm, "end": v(-4712.44, -2561.98) * mm});
            skLineSegment(sketch, "E2152", {"start": v(-4712.44, -2561.98) * mm, "end": v(-4715.21, -2558.52) * mm});
            skLineSegment(sketch, "E2153", {"start": v(-4715.21, -2558.52) * mm, "end": v(-4716.6, -2556.9) * mm});
            skLineSegment(sketch, "E2154", {"start": v(-4716.6, -2556.9) * mm, "end": v(-4718.9, -2556.67) * mm});
            skLineSegment(sketch, "E2155", {"start": v(-4718.9, -2556.67) * mm, "end": v(-4726.3, -2560.36) * mm});
            skLineSegment(sketch, "E2156", {"start": v(-4726.3, -2560.36) * mm, "end": v(-4720.75, -2570.99) * mm});
            skLineSegment(sketch, "E2157", {"start": v(-4720.75, -2570.99) * mm, "end": v(-4718.9, -2582.53) * mm});
            skLineSegment(sketch, "E2158", {"start": v(-4718.9, -2582.53) * mm, "end": v(-4721.68, -2593.62) * mm});
            skLineSegment(sketch, "E2159", {"start": v(-4721.68, -2593.62) * mm, "end": v(-4729.99, -2604.7) * mm});
            skLineSegment(sketch, "E2160", {"start": v(-4729.99, -2604.7) * mm, "end": v(-4741.07, -2611.63) * mm});
            skLineSegment(sketch, "E2161", {"start": v(-4741.07, -2611.63) * mm, "end": v(-4755.85, -2613.94) * mm});
            skLineSegment(sketch, "E2162", {"start": v(-4755.85, -2613.94) * mm, "end": v(-4765.78, -2613.01) * mm});
            skLineSegment(sketch, "E2163", {"start": v(-4765.78, -2613.01) * mm, "end": v(-4773.4, -2610.24) * mm});
            skLineSegment(sketch, "E2164", {"start": v(-4773.4, -2610.24) * mm, "end": v(-4778.94, -2614.63) * mm});
            skLineSegment(sketch, "E2165", {"start": v(-4778.94, -2614.63) * mm, "end": v(-4780.79, -2618.55) * mm});
            skLineSegment(sketch, "E2166", {"start": v(-4780.79, -2618.55) * mm, "end": v(-4778.94, -2624.33) * mm});
            skLineSegment(sketch, "E2167", {"start": v(-4778.94, -2624.33) * mm, "end": v(-4773.4, -2626.87) * mm});
            skLineSegment(sketch, "E2168", {"start": v(-4729.06, -2646.26) * mm, "end": v(-4770.63, -2639.8) * mm});
            skLineSegment(sketch, "E2169", {"start": v(-4770.63, -2639.8) * mm, "end": v(-4777.9, -2643.43) * mm});
            skLineSegment(sketch, "E2170", {"start": v(-4777.9, -2643.43) * mm, "end": v(-4783.1, -2647.88) * mm});
            skLineSegment(sketch, "E2171", {"start": v(-4783.1, -2647.88) * mm, "end": v(-4786.21, -2653.13) * mm});
            skLineSegment(sketch, "E2172", {"start": v(-4786.21, -2653.13) * mm, "end": v(-4787.25, -2659.2) * mm});
            skLineSegment(sketch, "E2173", {"start": v(-4787.25, -2659.2) * mm, "end": v(-4785.87, -2664.74) * mm});
            skLineSegment(sketch, "E2174", {"start": v(-4785.87, -2664.74) * mm, "end": v(-4781.71, -2670.28) * mm});
            skLineSegment(sketch, "E2175", {"start": v(-4781.71, -2670.28) * mm, "end": v(-4776.75, -2673.91) * mm});
            skLineSegment(sketch, "E2176", {"start": v(-4776.75, -2673.91) * mm, "end": v(-4770.17, -2676.51) * mm});
            skLineSegment(sketch, "E2177", {"start": v(-4770.17, -2676.51) * mm, "end": v(-4752.16, -2678.59) * mm});
            skLineSegment(sketch, "E2178", {"start": v(-4752.16, -2678.59) * mm, "end": v(-4735.3, -2676.28) * mm});
            skLineSegment(sketch, "E2179", {"start": v(-4735.3, -2676.28) * mm, "end": v(-4728.78, -2673.4) * mm});
            skLineSegment(sketch, "E2180", {"start": v(-4728.78, -2673.4) * mm, "end": v(-4723.52, -2669.35) * mm});
            skLineSegment(sketch, "E2181", {"start": v(-4723.52, -2669.35) * mm, "end": v(-4720.75, -2664.97) * mm});
            skLineSegment(sketch, "E2182", {"start": v(-4720.75, -2664.97) * mm, "end": v(-4719.83, -2659.2) * mm});
            skLineSegment(sketch, "E2183", {"start": v(-4719.83, -2659.2) * mm, "end": v(-4722.14, -2650.42) * mm});
            skLineSegment(sketch, "E2184", {"start": v(-4722.14, -2650.42) * mm, "end": v(-4725.02, -2647.76) * mm});
            skLineSegment(sketch, "E2185", {"start": v(-4725.02, -2647.76) * mm, "end": v(-4729.06, -2646.26) * mm});
            skLineSegment(sketch, "E2186", {"start": v(-4661.64, -2618.55) * mm, "end": v(-4660.48, -2630.1) * mm});
            skLineSegment(sketch, "E2187", {"start": v(-4660.48, -2630.1) * mm, "end": v(-4657.02, -2637.03) * mm});
            skLineSegment(sketch, "E2188", {"start": v(-4657.02, -2637.03) * mm, "end": v(-4650.56, -2640.49) * mm});
            skLineSegment(sketch, "E2189", {"start": v(-4650.56, -2640.49) * mm, "end": v(-4642.24, -2641.64) * mm});
            skLineSegment(sketch, "E2190", {"start": v(-4642.24, -2641.64) * mm, "end": v(-4629.08, -2639.8) * mm});
            skLineSegment(sketch, "E2191", {"start": v(-4629.08, -2639.8) * mm, "end": v(-4619.15, -2634.26) * mm});
            skLineSegment(sketch, "E2192", {"start": v(-4619.15, -2634.26) * mm, "end": v(-4614.07, -2628.25) * mm});
            skLineSegment(sketch, "E2193", {"start": v(-4614.07, -2628.25) * mm, "end": v(-4609.92, -2619.48) * mm});
            skLineSegment(sketch, "E2194", {"start": v(-4609.92, -2619.48) * mm, "end": v(-4609.92, -2561.29) * mm});
            skLineSegment(sketch, "E2195", {"start": v(-4609.92, -2561.29) * mm, "end": v(-4612, -2555.05) * mm});
            skLineSegment(sketch, "E2196", {"start": v(-4612, -2555.05) * mm, "end": v(-4618.23, -2552.98) * mm});
            skLineSegment(sketch, "E2197", {"start": v(-4618.23, -2552.98) * mm, "end": v(-4622.85, -2552.98) * mm});
            skLineSegment(sketch, "E2198", {"start": v(-4622.85, -2552.98) * mm, "end": v(-4622.85, -2547.43) * mm});
            skLineSegment(sketch, "E2199", {"start": v(-4622.85, -2547.43) * mm, "end": v(-4618.23, -2547.43) * mm});
            skLineSegment(sketch, "E2200", {"start": v(-4618.23, -2547.43) * mm, "end": v(-4608.3, -2545.82) * mm});
            skLineSegment(sketch, "E2201", {"start": v(-4608.3, -2545.82) * mm, "end": v(-4598.83, -2540.97) * mm});
            skLineSegment(sketch, "E2202", {"start": v(-4598.83, -2540.97) * mm, "end": v(-4596.98, -2540.97) * mm});
            skLineSegment(sketch, "E2203", {"start": v(-4596.98, -2540.97) * mm, "end": v(-4596.98, -2632.4) * mm});
            skLineSegment(sketch, "E2204", {"start": v(-4596.98, -2632.4) * mm, "end": v(-4594.9, -2637.95) * mm});
            skLineSegment(sketch, "E2205", {"start": v(-4594.9, -2637.95) * mm, "end": v(-4588.67, -2639.8) * mm});
            skLineSegment(sketch, "E2206", {"start": v(-4588.67, -2639.8) * mm, "end": v(-4583.13, -2639.8) * mm});
            skLineSegment(sketch, "E2207", {"start": v(-4583.13, -2639.8) * mm, "end": v(-4583.13, -2645.34) * mm});
            skLineSegment(sketch, "E2208", {"start": v(-4583.13, -2645.34) * mm, "end": v(-4588.67, -2645.34) * mm});
            skLineSegment(sketch, "E2209", {"start": v(-4588.67, -2645.34) * mm, "end": v(-4598.14, -2646.72) * mm});
            skLineSegment(sketch, "E2210", {"start": v(-4598.14, -2646.72) * mm, "end": v(-4608.07, -2650.88) * mm});
            skLineSegment(sketch, "E2211", {"start": v(-4608.07, -2650.88) * mm, "end": v(-4609.92, -2650.88) * mm});
            skLineSegment(sketch, "E2212", {"start": v(-4609.92, -2650.88) * mm, "end": v(-4609.92, -2631.48) * mm});
            skLineSegment(sketch, "E2213", {"start": v(-4609.92, -2631.48) * mm, "end": v(-4616.27, -2639.97) * mm});
            skLineSegment(sketch, "E2214", {"start": v(-4616.27, -2639.97) * mm, "end": v(-4624.23, -2646.03) * mm});
            skLineSegment(sketch, "E2215", {"start": v(-4624.23, -2646.03) * mm, "end": v(-4633.81, -2649.67) * mm});
            skLineSegment(sketch, "E2216", {"start": v(-4633.81, -2649.67) * mm, "end": v(-4645.01, -2650.88) * mm});
            skLineSegment(sketch, "E2217", {"start": v(-4645.01, -2650.88) * mm, "end": v(-4656.8, -2649.03) * mm});
            skLineSegment(sketch, "E2218", {"start": v(-4656.8, -2649.03) * mm, "end": v(-4666.26, -2643.5) * mm});
            skLineSegment(sketch, "E2219", {"start": v(-4666.26, -2643.5) * mm, "end": v(-4672.5, -2633.8) * mm});
            skLineSegment(sketch, "E2220", {"start": v(-4672.5, -2633.8) * mm, "end": v(-4674.57, -2619.48) * mm});
            skLineSegment(sketch, "E2221", {"start": v(-4674.57, -2619.48) * mm, "end": v(-4674.57, -2561.29) * mm});
            skLineSegment(sketch, "E2222", {"start": v(-4674.57, -2561.29) * mm, "end": v(-4676.65, -2555.05) * mm});
            skLineSegment(sketch, "E2223", {"start": v(-4676.65, -2555.05) * mm, "end": v(-4682.88, -2552.98) * mm});
            skLineSegment(sketch, "E2224", {"start": v(-4682.88, -2552.98) * mm, "end": v(-4687.5, -2552.98) * mm});
            skLineSegment(sketch, "E2225", {"start": v(-4687.5, -2552.98) * mm, "end": v(-4687.5, -2547.43) * mm});
            skLineSegment(sketch, "E2226", {"start": v(-4687.5, -2547.43) * mm, "end": v(-4682.88, -2547.43) * mm});
            skLineSegment(sketch, "E2227", {"start": v(-4682.88, -2547.43) * mm, "end": v(-4672.95, -2545.82) * mm});
            skLineSegment(sketch, "E2228", {"start": v(-4672.95, -2545.82) * mm, "end": v(-4663.49, -2540.97) * mm});
            skLineSegment(sketch, "E2229", {"start": v(-4663.49, -2540.97) * mm, "end": v(-4661.64, -2540.97) * mm});
            skLineSegment(sketch, "E2230", {"start": v(-4661.64, -2540.97) * mm, "end": v(-4661.64, -2618.55) * mm});
            skLineSegment(sketch, "E2231", {"start": v(-4507.4, -2494.79) * mm, "end": v(-4504.62, -2498.48) * mm});
            skLineSegment(sketch, "E2232", {"start": v(-4504.62, -2498.48) * mm, "end": v(-4503.7, -2502.18) * mm});
            skLineSegment(sketch, "E2233", {"start": v(-4503.7, -2502.18) * mm, "end": v(-4504.62, -2506.56) * mm});
            skLineSegment(sketch, "E2234", {"start": v(-4504.62, -2506.56) * mm, "end": v(-4507.4, -2510.49) * mm});
            skLineSegment(sketch, "E2235", {"start": v(-4507.4, -2510.49) * mm, "end": v(-4511.32, -2513.26) * mm});
            skLineSegment(sketch, "E2236", {"start": v(-4511.32, -2513.26) * mm, "end": v(-4515.7, -2514.18) * mm});
            skLineSegment(sketch, "E2237", {"start": v(-4515.7, -2514.18) * mm, "end": v(-4520.1, -2513.26) * mm});
            skLineSegment(sketch, "E2238", {"start": v(-4520.1, -2513.26) * mm, "end": v(-4524.02, -2510.49) * mm});
            skLineSegment(sketch, "E2239", {"start": v(-4524.02, -2510.49) * mm, "end": v(-4526.79, -2506.56) * mm});
            skLineSegment(sketch, "E2240", {"start": v(-4526.79, -2506.56) * mm, "end": v(-4527.71, -2502.18) * mm});
            skLineSegment(sketch, "E2241", {"start": v(-4527.71, -2502.18) * mm, "end": v(-4526.79, -2498.48) * mm});
            skLineSegment(sketch, "E2242", {"start": v(-4526.79, -2498.48) * mm, "end": v(-4524.02, -2494.79) * mm});
            skLineSegment(sketch, "E2243", {"start": v(-4524.02, -2494.79) * mm, "end": v(-4520.1, -2492.02) * mm});
            skLineSegment(sketch, "E2244", {"start": v(-4520.1, -2492.02) * mm, "end": v(-4515.7, -2491.1) * mm});
            skLineSegment(sketch, "E2245", {"start": v(-4515.7, -2491.1) * mm, "end": v(-4511.32, -2492.02) * mm});
            skLineSegment(sketch, "E2246", {"start": v(-4511.32, -2492.02) * mm, "end": v(-4507.4, -2494.79) * mm});
            skLineSegment(sketch, "E2247", {"start": v(-4523.1, -2561.29) * mm, "end": v(-4525.17, -2555.05) * mm});
            skLineSegment(sketch, "E2248", {"start": v(-4525.17, -2555.05) * mm, "end": v(-4531.4, -2552.98) * mm});
            skLineSegment(sketch, "E2249", {"start": v(-4531.4, -2552.98) * mm, "end": v(-4550.8, -2552.98) * mm});
            skLineSegment(sketch, "E2250", {"start": v(-4550.8, -2552.98) * mm, "end": v(-4550.8, -2547.43) * mm});
            skLineSegment(sketch, "E2251", {"start": v(-4550.8, -2547.43) * mm, "end": v(-4541.57, -2547.43) * mm});
            skLineSegment(sketch, "E2252", {"start": v(-4541.57, -2547.43) * mm, "end": v(-4526.33, -2545.82) * mm});
            skLineSegment(sketch, "E2253", {"start": v(-4526.33, -2545.82) * mm, "end": v(-4512.01, -2540.97) * mm});
            skLineSegment(sketch, "E2254", {"start": v(-4512.01, -2540.97) * mm, "end": v(-4510.16, -2540.97) * mm});
            skLineSegment(sketch, "E2255", {"start": v(-4510.16, -2540.97) * mm, "end": v(-4510.16, -2637.95) * mm});
            skLineSegment(sketch, "E2256", {"start": v(-4510.16, -2637.95) * mm, "end": v(-4508.08, -2643.5) * mm});
            skLineSegment(sketch, "E2257", {"start": v(-4508.08, -2643.5) * mm, "end": v(-4501.85, -2645.34) * mm});
            skLineSegment(sketch, "E2258", {"start": v(-4501.85, -2645.34) * mm, "end": v(-4482.45, -2645.34) * mm});
            skLineSegment(sketch, "E2259", {"start": v(-4482.45, -2645.34) * mm, "end": v(-4482.45, -2650.88) * mm});
            skLineSegment(sketch, "E2260", {"start": v(-4482.45, -2650.88) * mm, "end": v(-4550.8, -2650.88) * mm});
            skLineSegment(sketch, "E2261", {"start": v(-4550.8, -2650.88) * mm, "end": v(-4550.8, -2645.34) * mm});
            skLineSegment(sketch, "E2262", {"start": v(-4550.8, -2645.34) * mm, "end": v(-4531.4, -2645.34) * mm});
            skLineSegment(sketch, "E2263", {"start": v(-4531.4, -2645.34) * mm, "end": v(-4525.17, -2643.5) * mm});
            skLineSegment(sketch, "E2264", {"start": v(-4525.17, -2643.5) * mm, "end": v(-4523.1, -2637.95) * mm});
            skLineSegment(sketch, "E2265", {"start": v(-4523.1, -2637.95) * mm, "end": v(-4523.1, -2561.29) * mm});
            skLineSegment(sketch, "E2266", {"start": v(-4437.2, -2558.52) * mm, "end": v(-4438.35, -2554.36) * mm});
            skLineSegment(sketch, "E2267", {"start": v(-4438.35, -2554.36) * mm, "end": v(-4441.81, -2552.98) * mm});
            skLineSegment(sketch, "E2268", {"start": v(-4441.81, -2552.98) * mm, "end": v(-4449.2, -2552.98) * mm});
            skLineSegment(sketch, "E2269", {"start": v(-4449.2, -2552.98) * mm, "end": v(-4449.2, -2547.43) * mm});
            skLineSegment(sketch, "E2270", {"start": v(-4449.2, -2547.43) * mm, "end": v(-4442.74, -2547.43) * mm});
            skLineSegment(sketch, "E2271", {"start": v(-4442.74, -2547.43) * mm, "end": v(-4434.42, -2546.28) * mm});
            skLineSegment(sketch, "E2272", {"start": v(-4434.42, -2546.28) * mm, "end": v(-4426.11, -2542.82) * mm});
            skLineSegment(sketch, "E2273", {"start": v(-4426.11, -2542.82) * mm, "end": v(-4424.26, -2542.82) * mm});
            skLineSegment(sketch, "E2274", {"start": v(-4424.26, -2542.82) * mm, "end": v(-4424.26, -2565.9) * mm});
            skLineSegment(sketch, "E2275", {"start": v(-4424.26, -2565.9) * mm, "end": v(-4416.24, -2557.82) * mm});
            skLineSegment(sketch, "E2276", {"start": v(-4416.24, -2557.82) * mm, "end": v(-4407.87, -2552.05) * mm});
            skLineSegment(sketch, "E2277", {"start": v(-4407.87, -2552.05) * mm, "end": v(-4399.15, -2548.59) * mm});
            skLineSegment(sketch, "E2278", {"start": v(-4399.15, -2548.59) * mm, "end": v(-4390.1, -2547.43) * mm});
            skLineSegment(sketch, "E2279", {"start": v(-4390.1, -2547.43) * mm, "end": v(-4376.76, -2549.51) * mm});
            skLineSegment(sketch, "E2280", {"start": v(-4376.76, -2549.51) * mm, "end": v(-4367.23, -2555.75) * mm});
            skLineSegment(sketch, "E2281", {"start": v(-4367.23, -2555.75) * mm, "end": v(-4361.52, -2566.14) * mm});
            skLineSegment(sketch, "E2282", {"start": v(-4361.52, -2566.14) * mm, "end": v(-4359.61, -2580.68) * mm});
            skLineSegment(sketch, "E2283", {"start": v(-4359.61, -2580.68) * mm, "end": v(-4359.61, -2637.95) * mm});
            skLineSegment(sketch, "E2284", {"start": v(-4359.61, -2637.95) * mm, "end": v(-4357.53, -2643.5) * mm});
            skLineSegment(sketch, "E2285", {"start": v(-4357.53, -2643.5) * mm, "end": v(-4351.3, -2645.34) * mm});
            skLineSegment(sketch, "E2286", {"start": v(-4351.3, -2645.34) * mm, "end": v(-4346.68, -2645.34) * mm});
            skLineSegment(sketch, "E2287", {"start": v(-4346.68, -2645.34) * mm, "end": v(-4346.68, -2650.88) * mm});
            skLineSegment(sketch, "E2288", {"start": v(-4346.68, -2650.88) * mm, "end": v(-4385.47, -2650.88) * mm});
            skLineSegment(sketch, "E2289", {"start": v(-4385.47, -2650.88) * mm, "end": v(-4385.47, -2645.34) * mm});
            skLineSegment(sketch, "E2290", {"start": v(-4385.47, -2645.34) * mm, "end": v(-4380.85, -2645.34) * mm});
            skLineSegment(sketch, "E2291", {"start": v(-4380.85, -2645.34) * mm, "end": v(-4374.62, -2643.5) * mm});
            skLineSegment(sketch, "E2292", {"start": v(-4374.62, -2643.5) * mm, "end": v(-4372.54, -2637.95) * mm});
            skLineSegment(sketch, "E2293", {"start": v(-4372.54, -2637.95) * mm, "end": v(-4372.54, -2577.91) * mm});
            skLineSegment(sketch, "E2294", {"start": v(-4372.54, -2577.91) * mm, "end": v(-4373.87, -2567.81) * mm});
            skLineSegment(sketch, "E2295", {"start": v(-4373.87, -2567.81) * mm, "end": v(-4377.85, -2560.6) * mm});
            skLineSegment(sketch, "E2296", {"start": v(-4377.85, -2560.6) * mm, "end": v(-4384.5, -2556.27) * mm});
            skLineSegment(sketch, "E2297", {"start": v(-4384.5, -2556.27) * mm, "end": v(-4393.78, -2554.82) * mm});
            skLineSegment(sketch, "E2298", {"start": v(-4393.78, -2554.82) * mm, "end": v(-4401.92, -2556.15) * mm});
            skLineSegment(sketch, "E2299", {"start": v(-4401.92, -2556.15) * mm, "end": v(-4409.72, -2560.13) * mm});
            skLineSegment(sketch, "E2300", {"start": v(-4409.72, -2560.13) * mm, "end": v(-4417.16, -2566.77) * mm});
            skLineSegment(sketch, "E2301", {"start": v(-4417.16, -2566.77) * mm, "end": v(-4424.26, -2576.07) * mm});
            skLineSegment(sketch, "E2302", {"start": v(-4424.26, -2576.07) * mm, "end": v(-4424.26, -2637.95) * mm});
            skLineSegment(sketch, "E2303", {"start": v(-4424.26, -2637.95) * mm, "end": v(-4422.19, -2643.5) * mm});
            skLineSegment(sketch, "E2304", {"start": v(-4422.19, -2643.5) * mm, "end": v(-4415.95, -2645.34) * mm});
            skLineSegment(sketch, "E2305", {"start": v(-4415.95, -2645.34) * mm, "end": v(-4411.33, -2645.34) * mm});
            skLineSegment(sketch, "E2306", {"start": v(-4411.33, -2645.34) * mm, "end": v(-4411.33, -2650.88) * mm});
            skLineSegment(sketch, "E2307", {"start": v(-4411.33, -2650.88) * mm, "end": v(-4450.13, -2650.88) * mm});
            skLineSegment(sketch, "E2308", {"start": v(-4450.13, -2650.88) * mm, "end": v(-4450.13, -2645.34) * mm});
            skLineSegment(sketch, "E2309", {"start": v(-4450.13, -2645.34) * mm, "end": v(-4445.5, -2645.34) * mm});
            skLineSegment(sketch, "E2310", {"start": v(-4445.5, -2645.34) * mm, "end": v(-4439.27, -2643.5) * mm});
            skLineSegment(sketch, "E2311", {"start": v(-4439.27, -2643.5) * mm, "end": v(-4437.2, -2637.95) * mm});
            skLineSegment(sketch, "E2312", {"start": v(-4437.2, -2637.95) * mm, "end": v(-4437.2, -2558.52) * mm});
            skLineSegment(sketch, "E2313", {"start": v(-4281.1, -2547.43) * mm, "end": v(-4272.27, -2548.18) * mm});
            skLineSegment(sketch, "E2314", {"start": v(-4272.27, -2548.18) * mm, "end": v(-4264.24, -2550.44) * mm});
            skLineSegment(sketch, "E2315", {"start": v(-4264.24, -2550.44) * mm, "end": v(-4257.03, -2554.19) * mm});
            skLineSegment(sketch, "E2316", {"start": v(-4257.03, -2554.19) * mm, "end": v(-4250.62, -2559.44) * mm});
            skLineSegment(sketch, "E2317", {"start": v(-4250.62, -2559.44) * mm, "end": v(-4242.94, -2568.5) * mm});
            skLineSegment(sketch, "E2318", {"start": v(-4242.94, -2568.5) * mm, "end": v(-4237.46, -2578.14) * mm});
            skLineSegment(sketch, "E2319", {"start": v(-4237.46, -2578.14) * mm, "end": v(-4234.17, -2588.36) * mm});
            skLineSegment(sketch, "E2320", {"start": v(-4234.17, -2588.36) * mm, "end": v(-4233.07, -2599.16) * mm});
            skLineSegment(sketch, "E2321", {"start": v(-4233.07, -2599.16) * mm, "end": v(-4234.11, -2610.64) * mm});
            skLineSegment(sketch, "E2322", {"start": v(-4234.11, -2610.64) * mm, "end": v(-4237.23, -2621.1) * mm});
            skLineSegment(sketch, "E2323", {"start": v(-4237.23, -2621.1) * mm, "end": v(-4242.42, -2630.5) * mm});
            skLineSegment(sketch, "E2324", {"start": v(-4242.42, -2630.5) * mm, "end": v(-4249.7, -2638.87) * mm});
            skLineSegment(sketch, "E2325", {"start": v(-4249.7, -2638.87) * mm, "end": v(-4256.16, -2644.13) * mm});
            skLineSegment(sketch, "E2326", {"start": v(-4256.16, -2644.13) * mm, "end": v(-4263.55, -2647.88) * mm});
            skLineSegment(sketch, "E2327", {"start": v(-4263.55, -2647.88) * mm, "end": v(-4271.86, -2650.13) * mm});
            skLineSegment(sketch, "E2328", {"start": v(-4271.86, -2650.13) * mm, "end": v(-4281.1, -2650.88) * mm});
            skLineSegment(sketch, "E2329", {"start": v(-4281.1, -2650.88) * mm, "end": v(-4289.93, -2650.13) * mm});
            skLineSegment(sketch, "E2330", {"start": v(-4289.93, -2650.13) * mm, "end": v(-4297.96, -2647.88) * mm});
            skLineSegment(sketch, "E2331", {"start": v(-4297.96, -2647.88) * mm, "end": v(-4305.17, -2644.13) * mm});
            skLineSegment(sketch, "E2332", {"start": v(-4305.17, -2644.13) * mm, "end": v(-4311.58, -2638.87) * mm});
            skLineSegment(sketch, "E2333", {"start": v(-4311.58, -2638.87) * mm, "end": v(-4319.26, -2630.16) * mm});
            skLineSegment(sketch, "E2334", {"start": v(-4319.26, -2630.16) * mm, "end": v(-4324.74, -2620.63) * mm});
            skLineSegment(sketch, "E2335", {"start": v(-4324.74, -2620.63) * mm, "end": v(-4328.03, -2610.3) * mm});
            skLineSegment(sketch, "E2336", {"start": v(-4328.03, -2610.3) * mm, "end": v(-4329.13, -2599.16) * mm});
            skLineSegment(sketch, "E2337", {"start": v(-4329.13, -2599.16) * mm, "end": v(-4328.1, -2588.42) * mm});
            skLineSegment(sketch, "E2338", {"start": v(-4328.1, -2588.42) * mm, "end": v(-4324.97, -2578.38) * mm});
            skLineSegment(sketch, "E2339", {"start": v(-4324.97, -2578.38) * mm, "end": v(-4319.78, -2569.02) * mm});
            skLineSegment(sketch, "E2340", {"start": v(-4319.78, -2569.02) * mm, "end": v(-4312.5, -2560.36) * mm});
            skLineSegment(sketch, "E2341", {"start": v(-4312.5, -2560.36) * mm, "end": v(-4305.7, -2554.7) * mm});
            skLineSegment(sketch, "E2342", {"start": v(-4305.7, -2554.7) * mm, "end": v(-4298.19, -2550.67) * mm});
            skLineSegment(sketch, "E2343", {"start": v(-4298.19, -2550.67) * mm, "end": v(-4290, -2548.24) * mm});
            skLineSegment(sketch, "E2344", {"start": v(-4290, -2548.24) * mm, "end": v(-4281.1, -2547.43) * mm});
            skLineSegment(sketch, "E2345", {"start": v(-4281.1, -2553.9) * mm, "end": v(-4292.42, -2556.2) * mm});
            skLineSegment(sketch, "E2346", {"start": v(-4292.42, -2556.2) * mm, "end": v(-4302.34, -2563.14) * mm});
            skLineSegment(sketch, "E2347", {"start": v(-4302.34, -2563.14) * mm, "end": v(-4307.6, -2569.6) * mm});
            skLineSegment(sketch, "E2348", {"start": v(-4307.6, -2569.6) * mm, "end": v(-4311.35, -2577.91) * mm});
            skLineSegment(sketch, "E2349", {"start": v(-4311.35, -2577.91) * mm, "end": v(-4313.6, -2588.07) * mm});
            skLineSegment(sketch, "E2350", {"start": v(-4313.6, -2588.07) * mm, "end": v(-4314.35, -2600.08) * mm});
            skLineSegment(sketch, "E2351", {"start": v(-4314.35, -2600.08) * mm, "end": v(-4313.6, -2612.09) * mm});
            skLineSegment(sketch, "E2352", {"start": v(-4313.6, -2612.09) * mm, "end": v(-4311.35, -2622.25) * mm});
            skLineSegment(sketch, "E2353", {"start": v(-4311.35, -2622.25) * mm, "end": v(-4307.6, -2630.56) * mm});
            skLineSegment(sketch, "E2354", {"start": v(-4307.6, -2630.56) * mm, "end": v(-4302.34, -2637.03) * mm});
            skLineSegment(sketch, "E2355", {"start": v(-4302.34, -2637.03) * mm, "end": v(-4292.88, -2643.26) * mm});
            skLineSegment(sketch, "E2356", {"start": v(-4292.88, -2643.26) * mm, "end": v(-4281.1, -2645.34) * mm});
            skLineSegment(sketch, "E2357", {"start": v(-4281.1, -2645.34) * mm, "end": v(-4269.32, -2643.26) * mm});
            skLineSegment(sketch, "E2358", {"start": v(-4269.32, -2643.26) * mm, "end": v(-4259.86, -2637.03) * mm});
            skLineSegment(sketch, "E2359", {"start": v(-4259.86, -2637.03) * mm, "end": v(-4254.6, -2630.56) * mm});
            skLineSegment(sketch, "E2360", {"start": v(-4254.6, -2630.56) * mm, "end": v(-4250.85, -2622.25) * mm});
            skLineSegment(sketch, "E2361", {"start": v(-4250.85, -2622.25) * mm, "end": v(-4248.6, -2612.09) * mm});
            skLineSegment(sketch, "E2362", {"start": v(-4248.6, -2612.09) * mm, "end": v(-4247.85, -2600.08) * mm});
            skLineSegment(sketch, "E2363", {"start": v(-4247.85, -2600.08) * mm, "end": v(-4248.6, -2588.07) * mm});
            skLineSegment(sketch, "E2364", {"start": v(-4248.6, -2588.07) * mm, "end": v(-4250.85, -2577.91) * mm});
            skLineSegment(sketch, "E2365", {"start": v(-4250.85, -2577.91) * mm, "end": v(-4254.6, -2569.6) * mm});
            skLineSegment(sketch, "E2366", {"start": v(-4254.6, -2569.6) * mm, "end": v(-4259.86, -2563.14) * mm});
            skLineSegment(sketch, "E2367", {"start": v(-4259.86, -2563.14) * mm, "end": v(-4269.79, -2556.2) * mm});
            skLineSegment(sketch, "E2368", {"start": v(-4269.79, -2556.2) * mm, "end": v(-4281.1, -2553.9) * mm});
            skLineSegment(sketch, "E2369", {"start": v(-4186.9, -2492.94) * mm, "end": v(-4171.65, -2491.1) * mm});
            skLineSegment(sketch, "E2370", {"start": v(-4171.65, -2491.1) * mm, "end": v(-4157.33, -2485.55) * mm});
            skLineSegment(sketch, "E2371", {"start": v(-4157.33, -2485.55) * mm, "end": v(-4155.49, -2485.55) * mm});
            skLineSegment(sketch, "E2372", {"start": v(-4155.49, -2485.55) * mm, "end": v(-4155.49, -2637.95) * mm});
            skLineSegment(sketch, "E2373", {"start": v(-4155.49, -2637.95) * mm, "end": v(-4153.4, -2643.5) * mm});
            skLineSegment(sketch, "E2374", {"start": v(-4153.4, -2643.5) * mm, "end": v(-4147.17, -2645.34) * mm});
            skLineSegment(sketch, "E2375", {"start": v(-4147.17, -2645.34) * mm, "end": v(-4125.93, -2645.34) * mm});
            skLineSegment(sketch, "E2376", {"start": v(-4125.93, -2645.34) * mm, "end": v(-4125.93, -2650.88) * mm});
            skLineSegment(sketch, "E2377", {"start": v(-4125.93, -2650.88) * mm, "end": v(-4197.97, -2650.88) * mm});
            skLineSegment(sketch, "E2378", {"start": v(-4197.97, -2650.88) * mm, "end": v(-4197.97, -2645.34) * mm});
            skLineSegment(sketch, "E2379", {"start": v(-4197.97, -2645.34) * mm, "end": v(-4176.73, -2645.34) * mm});
            skLineSegment(sketch, "E2380", {"start": v(-4176.73, -2645.34) * mm, "end": v(-4170.5, -2643.5) * mm});
            skLineSegment(sketch, "E2381", {"start": v(-4170.5, -2643.5) * mm, "end": v(-4168.42, -2637.95) * mm});
            skLineSegment(sketch, "E2382", {"start": v(-4168.42, -2637.95) * mm, "end": v(-4168.42, -2505.87) * mm});
            skLineSegment(sketch, "E2383", {"start": v(-4168.42, -2505.87) * mm, "end": v(-4170.5, -2500.33) * mm});
            skLineSegment(sketch, "E2384", {"start": v(-4170.5, -2500.33) * mm, "end": v(-4176.73, -2498.48) * mm});
            skLineSegment(sketch, "E2385", {"start": v(-4176.73, -2498.48) * mm, "end": v(-4197.05, -2498.48) * mm});
            skLineSegment(sketch, "E2386", {"start": v(-4197.05, -2498.48) * mm, "end": v(-4197.05, -2492.94) * mm});
            skLineSegment(sketch, "E2387", {"start": v(-4197.05, -2492.94) * mm, "end": v(-4186.9, -2492.94) * mm});
            skLineSegment(sketch, "E2388", {"start": v(-4044.65, -2547.43) * mm, "end": v(-4035.82, -2548.18) * mm});
            skLineSegment(sketch, "E2389", {"start": v(-4035.82, -2548.18) * mm, "end": v(-4027.8, -2550.44) * mm});
            skLineSegment(sketch, "E2390", {"start": v(-4027.8, -2550.44) * mm, "end": v(-4020.58, -2554.19) * mm});
            skLineSegment(sketch, "E2391", {"start": v(-4020.58, -2554.19) * mm, "end": v(-4014.17, -2559.44) * mm});
            skLineSegment(sketch, "E2392", {"start": v(-4014.17, -2559.44) * mm, "end": v(-4006.5, -2568.5) * mm});
            skLineSegment(sketch, "E2393", {"start": v(-4006.5, -2568.5) * mm, "end": v(-4001, -2578.14) * mm});
            skLineSegment(sketch, "E2394", {"start": v(-4001, -2578.14) * mm, "end": v(-3997.72, -2588.36) * mm});
            skLineSegment(sketch, "E2395", {"start": v(-3997.72, -2588.36) * mm, "end": v(-3996.62, -2599.16) * mm});
            skLineSegment(sketch, "E2396", {"start": v(-3996.62, -2599.16) * mm, "end": v(-3997.66, -2610.64) * mm});
            skLineSegment(sketch, "E2397", {"start": v(-3997.66, -2610.64) * mm, "end": v(-4000.78, -2621.1) * mm});
            skLineSegment(sketch, "E2398", {"start": v(-4000.78, -2621.1) * mm, "end": v(-4005.97, -2630.5) * mm});
            skLineSegment(sketch, "E2399", {"start": v(-4005.97, -2630.5) * mm, "end": v(-4013.25, -2638.87) * mm});
            skLineSegment(sketch, "E2400", {"start": v(-4013.25, -2638.87) * mm, "end": v(-4019.71, -2644.13) * mm});
            skLineSegment(sketch, "E2401", {"start": v(-4019.71, -2644.13) * mm, "end": v(-4027.1, -2647.88) * mm});
            skLineSegment(sketch, "E2402", {"start": v(-4027.1, -2647.88) * mm, "end": v(-4035.41, -2650.13) * mm});
            skLineSegment(sketch, "E2403", {"start": v(-4035.41, -2650.13) * mm, "end": v(-4044.65, -2650.88) * mm});
            skLineSegment(sketch, "E2404", {"start": v(-4044.65, -2650.88) * mm, "end": v(-4053.48, -2650.13) * mm});
            skLineSegment(sketch, "E2405", {"start": v(-4053.48, -2650.13) * mm, "end": v(-4061.5, -2647.88) * mm});
            skLineSegment(sketch, "E2406", {"start": v(-4061.5, -2647.88) * mm, "end": v(-4068.72, -2644.13) * mm});
            skLineSegment(sketch, "E2407", {"start": v(-4068.72, -2644.13) * mm, "end": v(-4075.13, -2638.87) * mm});
            skLineSegment(sketch, "E2408", {"start": v(-4075.13, -2638.87) * mm, "end": v(-4082.8, -2630.16) * mm});
            skLineSegment(sketch, "E2409", {"start": v(-4082.8, -2630.16) * mm, "end": v(-4088.3, -2620.63) * mm});
            skLineSegment(sketch, "E2410", {"start": v(-4088.3, -2620.63) * mm, "end": v(-4091.58, -2610.3) * mm});
            skLineSegment(sketch, "E2411", {"start": v(-4091.58, -2610.3) * mm, "end": v(-4092.68, -2599.16) * mm});
            skLineSegment(sketch, "E2412", {"start": v(-4092.68, -2599.16) * mm, "end": v(-4091.64, -2588.42) * mm});
            skLineSegment(sketch, "E2413", {"start": v(-4091.64, -2588.42) * mm, "end": v(-4088.52, -2578.38) * mm});
            skLineSegment(sketch, "E2414", {"start": v(-4088.52, -2578.38) * mm, "end": v(-4083.33, -2569.02) * mm});
            skLineSegment(sketch, "E2415", {"start": v(-4083.33, -2569.02) * mm, "end": v(-4076.05, -2560.36) * mm});
            skLineSegment(sketch, "E2416", {"start": v(-4076.05, -2560.36) * mm, "end": v(-4069.24, -2554.7) * mm});
            skLineSegment(sketch, "E2417", {"start": v(-4069.24, -2554.7) * mm, "end": v(-4061.74, -2550.67) * mm});
            skLineSegment(sketch, "E2418", {"start": v(-4061.74, -2550.67) * mm, "end": v(-4053.54, -2548.24) * mm});
            skLineSegment(sketch, "E2419", {"start": v(-4053.54, -2548.24) * mm, "end": v(-4044.65, -2547.43) * mm});
            skLineSegment(sketch, "E2420", {"start": v(-4044.65, -2553.9) * mm, "end": v(-4055.96, -2556.2) * mm});
            skLineSegment(sketch, "E2421", {"start": v(-4055.96, -2556.2) * mm, "end": v(-4065.9, -2563.14) * mm});
            skLineSegment(sketch, "E2422", {"start": v(-4065.9, -2563.14) * mm, "end": v(-4071.15, -2569.6) * mm});
            skLineSegment(sketch, "E2423", {"start": v(-4071.15, -2569.6) * mm, "end": v(-4074.9, -2577.91) * mm});
            skLineSegment(sketch, "E2424", {"start": v(-4074.9, -2577.91) * mm, "end": v(-4077.15, -2588.07) * mm});
            skLineSegment(sketch, "E2425", {"start": v(-4077.15, -2588.07) * mm, "end": v(-4077.9, -2600.08) * mm});
            skLineSegment(sketch, "E2426", {"start": v(-4077.9, -2600.08) * mm, "end": v(-4077.15, -2612.09) * mm});
            skLineSegment(sketch, "E2427", {"start": v(-4077.15, -2612.09) * mm, "end": v(-4074.9, -2622.25) * mm});
            skLineSegment(sketch, "E2428", {"start": v(-4074.9, -2622.25) * mm, "end": v(-4071.15, -2630.56) * mm});
            skLineSegment(sketch, "E2429", {"start": v(-4071.15, -2630.56) * mm, "end": v(-4065.9, -2637.03) * mm});
            skLineSegment(sketch, "E2430", {"start": v(-4065.9, -2637.03) * mm, "end": v(-4056.43, -2643.26) * mm});
            skLineSegment(sketch, "E2431", {"start": v(-4056.43, -2643.26) * mm, "end": v(-4044.65, -2645.34) * mm});
            skLineSegment(sketch, "E2432", {"start": v(-4044.65, -2645.34) * mm, "end": v(-4032.87, -2643.26) * mm});
            skLineSegment(sketch, "E2433", {"start": v(-4032.87, -2643.26) * mm, "end": v(-4023.4, -2637.03) * mm});
            skLineSegment(sketch, "E2434", {"start": v(-4023.4, -2637.03) * mm, "end": v(-4018.15, -2630.56) * mm});
            skLineSegment(sketch, "E2435", {"start": v(-4018.15, -2630.56) * mm, "end": v(-4014.4, -2622.25) * mm});
            skLineSegment(sketch, "E2436", {"start": v(-4014.4, -2622.25) * mm, "end": v(-4012.15, -2612.09) * mm});
            skLineSegment(sketch, "E2437", {"start": v(-4012.15, -2612.09) * mm, "end": v(-4011.4, -2600.08) * mm});
            skLineSegment(sketch, "E2438", {"start": v(-4011.4, -2600.08) * mm, "end": v(-4012.15, -2588.07) * mm});
            skLineSegment(sketch, "E2439", {"start": v(-4012.15, -2588.07) * mm, "end": v(-4014.4, -2577.91) * mm});
            skLineSegment(sketch, "E2440", {"start": v(-4014.4, -2577.91) * mm, "end": v(-4018.15, -2569.6) * mm});
            skLineSegment(sketch, "E2441", {"start": v(-4018.15, -2569.6) * mm, "end": v(-4023.4, -2563.14) * mm});
            skLineSegment(sketch, "E2442", {"start": v(-4023.4, -2563.14) * mm, "end": v(-4033.34, -2556.2) * mm});
            skLineSegment(sketch, "E2443", {"start": v(-4033.34, -2556.2) * mm, "end": v(-4044.65, -2553.9) * mm});
            skLineSegment(sketch, "E2444", {"start": v(-3950.44, -2492.94) * mm, "end": v(-3935.2, -2491.1) * mm});
            skLineSegment(sketch, "E2445", {"start": v(-3935.2, -2491.1) * mm, "end": v(-3920.88, -2485.55) * mm});
            skLineSegment(sketch, "E2446", {"start": v(-3920.88, -2485.55) * mm, "end": v(-3919.04, -2485.55) * mm});
            skLineSegment(sketch, "E2447", {"start": v(-3919.04, -2485.55) * mm, "end": v(-3919.04, -2637.95) * mm});
            skLineSegment(sketch, "E2448", {"start": v(-3919.04, -2637.95) * mm, "end": v(-3916.96, -2643.5) * mm});
            skLineSegment(sketch, "E2449", {"start": v(-3916.96, -2643.5) * mm, "end": v(-3910.72, -2645.34) * mm});
            skLineSegment(sketch, "E2450", {"start": v(-3910.72, -2645.34) * mm, "end": v(-3889.48, -2645.34) * mm});
            skLineSegment(sketch, "E2451", {"start": v(-3889.48, -2645.34) * mm, "end": v(-3889.48, -2650.88) * mm});
            skLineSegment(sketch, "E2452", {"start": v(-3889.48, -2650.88) * mm, "end": v(-3961.52, -2650.88) * mm});
            skLineSegment(sketch, "E2453", {"start": v(-3961.52, -2650.88) * mm, "end": v(-3961.52, -2645.34) * mm});
            skLineSegment(sketch, "E2454", {"start": v(-3961.52, -2645.34) * mm, "end": v(-3940.28, -2645.34) * mm});
            skLineSegment(sketch, "E2455", {"start": v(-3940.28, -2645.34) * mm, "end": v(-3934.04, -2643.5) * mm});
            skLineSegment(sketch, "E2456", {"start": v(-3934.04, -2643.5) * mm, "end": v(-3931.97, -2637.95) * mm});
            skLineSegment(sketch, "E2457", {"start": v(-3931.97, -2637.95) * mm, "end": v(-3931.97, -2505.87) * mm});
            skLineSegment(sketch, "E2458", {"start": v(-3931.97, -2505.87) * mm, "end": v(-3934.04, -2500.33) * mm});
            skLineSegment(sketch, "E2459", {"start": v(-3934.04, -2500.33) * mm, "end": v(-3940.28, -2498.48) * mm});
            skLineSegment(sketch, "E2460", {"start": v(-3940.28, -2498.48) * mm, "end": v(-3960.6, -2498.48) * mm});
            skLineSegment(sketch, "E2461", {"start": v(-3960.6, -2498.48) * mm, "end": v(-3960.6, -2492.94) * mm});
            skLineSegment(sketch, "E2462", {"start": v(-3960.6, -2492.94) * mm, "end": v(-3950.44, -2492.94) * mm});
            skLineSegment(sketch, "E2463", {"start": v(-3834.06, -2618.55) * mm, "end": v(-3832.9, -2630.1) * mm});
            skLineSegment(sketch, "E2464", {"start": v(-3832.9, -2630.1) * mm, "end": v(-3829.44, -2637.03) * mm});
            skLineSegment(sketch, "E2465", {"start": v(-3829.44, -2637.03) * mm, "end": v(-3822.98, -2640.49) * mm});
            skLineSegment(sketch, "E2466", {"start": v(-3822.98, -2640.49) * mm, "end": v(-3814.66, -2641.64) * mm});
            skLineSegment(sketch, "E2467", {"start": v(-3814.66, -2641.64) * mm, "end": v(-3801.5, -2639.8) * mm});
            skLineSegment(sketch, "E2468", {"start": v(-3801.5, -2639.8) * mm, "end": v(-3791.57, -2634.26) * mm});
            skLineSegment(sketch, "E2469", {"start": v(-3791.57, -2634.26) * mm, "end": v(-3786.5, -2628.25) * mm});
            skLineSegment(sketch, "E2470", {"start": v(-3786.5, -2628.25) * mm, "end": v(-3782.34, -2619.48) * mm});
            skLineSegment(sketch, "E2471", {"start": v(-3782.34, -2619.48) * mm, "end": v(-3782.34, -2561.29) * mm});
            skLineSegment(sketch, "E2472", {"start": v(-3782.34, -2561.29) * mm, "end": v(-3784.42, -2555.05) * mm});
            skLineSegment(sketch, "E2473", {"start": v(-3784.42, -2555.05) * mm, "end": v(-3790.65, -2552.98) * mm});
            skLineSegment(sketch, "E2474", {"start": v(-3790.65, -2552.98) * mm, "end": v(-3795.27, -2552.98) * mm});
            skLineSegment(sketch, "E2475", {"start": v(-3795.27, -2552.98) * mm, "end": v(-3795.27, -2547.43) * mm});
            skLineSegment(sketch, "E2476", {"start": v(-3795.27, -2547.43) * mm, "end": v(-3790.65, -2547.43) * mm});
            skLineSegment(sketch, "E2477", {"start": v(-3790.65, -2547.43) * mm, "end": v(-3780.72, -2545.82) * mm});
            skLineSegment(sketch, "E2478", {"start": v(-3780.72, -2545.82) * mm, "end": v(-3771.25, -2540.97) * mm});
            skLineSegment(sketch, "E2479", {"start": v(-3771.25, -2540.97) * mm, "end": v(-3769.4, -2540.97) * mm});
            skLineSegment(sketch, "E2480", {"start": v(-3769.4, -2540.97) * mm, "end": v(-3769.4, -2632.4) * mm});
            skLineSegment(sketch, "E2481", {"start": v(-3769.4, -2632.4) * mm, "end": v(-3767.33, -2637.95) * mm});
            skLineSegment(sketch, "E2482", {"start": v(-3767.33, -2637.95) * mm, "end": v(-3761.1, -2639.8) * mm});
            skLineSegment(sketch, "E2483", {"start": v(-3761.1, -2639.8) * mm, "end": v(-3755.55, -2639.8) * mm});
            skLineSegment(sketch, "E2484", {"start": v(-3755.55, -2639.8) * mm, "end": v(-3755.55, -2645.34) * mm});
            skLineSegment(sketch, "E2485", {"start": v(-3755.55, -2645.34) * mm, "end": v(-3761.1, -2645.34) * mm});
            skLineSegment(sketch, "E2486", {"start": v(-3761.1, -2645.34) * mm, "end": v(-3770.56, -2646.72) * mm});
            skLineSegment(sketch, "E2487", {"start": v(-3770.56, -2646.72) * mm, "end": v(-3780.5, -2650.88) * mm});
            skLineSegment(sketch, "E2488", {"start": v(-3780.5, -2650.88) * mm, "end": v(-3782.34, -2650.88) * mm});
            skLineSegment(sketch, "E2489", {"start": v(-3782.34, -2650.88) * mm, "end": v(-3782.34, -2631.48) * mm});
            skLineSegment(sketch, "E2490", {"start": v(-3782.34, -2631.48) * mm, "end": v(-3788.69, -2639.97) * mm});
            skLineSegment(sketch, "E2491", {"start": v(-3788.69, -2639.97) * mm, "end": v(-3796.65, -2646.03) * mm});
            skLineSegment(sketch, "E2492", {"start": v(-3796.65, -2646.03) * mm, "end": v(-3806.24, -2649.67) * mm});
            skLineSegment(sketch, "E2493", {"start": v(-3806.24, -2649.67) * mm, "end": v(-3817.44, -2650.88) * mm});
            skLineSegment(sketch, "E2494", {"start": v(-3817.44, -2650.88) * mm, "end": v(-3829.21, -2649.03) * mm});
            skLineSegment(sketch, "E2495", {"start": v(-3829.21, -2649.03) * mm, "end": v(-3838.68, -2643.5) * mm});
            skLineSegment(sketch, "E2496", {"start": v(-3838.68, -2643.5) * mm, "end": v(-3844.91, -2633.8) * mm});
            skLineSegment(sketch, "E2497", {"start": v(-3844.91, -2633.8) * mm, "end": v(-3847, -2619.48) * mm});
            skLineSegment(sketch, "E2498", {"start": v(-3847, -2619.48) * mm, "end": v(-3847, -2561.29) * mm});
            skLineSegment(sketch, "E2499", {"start": v(-3847, -2561.29) * mm, "end": v(-3849.07, -2555.05) * mm});
            skLineSegment(sketch, "E2500", {"start": v(-3849.07, -2555.05) * mm, "end": v(-3855.3, -2552.98) * mm});
            skLineSegment(sketch, "E2501", {"start": v(-3855.3, -2552.98) * mm, "end": v(-3859.92, -2552.98) * mm});
            skLineSegment(sketch, "E2502", {"start": v(-3859.92, -2552.98) * mm, "end": v(-3859.92, -2547.43) * mm});
            skLineSegment(sketch, "E2503", {"start": v(-3859.92, -2547.43) * mm, "end": v(-3855.3, -2547.43) * mm});
            skLineSegment(sketch, "E2504", {"start": v(-3855.3, -2547.43) * mm, "end": v(-3845.38, -2545.82) * mm});
            skLineSegment(sketch, "E2505", {"start": v(-3845.38, -2545.82) * mm, "end": v(-3835.9, -2540.97) * mm});
            skLineSegment(sketch, "E2506", {"start": v(-3835.9, -2540.97) * mm, "end": v(-3834.06, -2540.97) * mm});
            skLineSegment(sketch, "E2507", {"start": v(-3834.06, -2540.97) * mm, "end": v(-3834.06, -2618.55) * mm});
            skLineSegment(sketch, "E2508", {"start": v(-5982.76, -165.9) * mm, "end": v(-5972.9, -164.61) * mm});
            skLineSegment(sketch, "E2509", {"start": v(-5855.76, 2869.4) * mm, "end": v(-5855.76, 2361.4) * mm});
            skLineSegment(sketch, "E2510", {"start": v(-1029.76, 431) * mm, "end": v(-1283.76, 177) * mm});
            skLineSegment(sketch, "E2511", {"start": v(-5601.76, 1955.17) * mm, "end": v(-5601.76, 1370.97) * mm});
            skLineSegment(sketch, "E2512", {"start": v(-5512.86, 1650.2) * mm, "end": v(-5511.56, 1640.33) * mm});
            skLineSegment(sketch, "E2513", {"start": v(-5493.8, 1617.2) * mm, "end": v(-5484.62, 1613.39) * mm});
            skLineSegment(sketch, "E2514", {"start": v(-5484.62, 1613.39) * mm, "end": v(-5474.76, 1612.1) * mm});
            skLineSegment(sketch, "E2515", {"start": v(-5780.46, 275.13) * mm, "end": v(-5793.04, 270.86) * mm});
            skLineSegment(sketch, "E2516", {"start": v(-5703.36, 1269.37) * mm, "end": v(-5754.16, 1269.37) * mm});
            skLineSegment(sketch, "E2517", {"start": v(-5780.46, 2053.3) * mm, "end": v(-5793.04, 2049.04) * mm});
            skLineSegment(sketch, "E2518", {"start": v(-5793.04, 270.86) * mm, "end": v(-5804.96, 264.98) * mm});
            skLineSegment(sketch, "E2519", {"start": v(-5816, 257.6) * mm, "end": v(-5826, 248.83) * mm});
            skLineSegment(sketch, "E2520", {"start": v(-5804.96, 264.98) * mm, "end": v(-5816, 257.6) * mm});
            skLineSegment(sketch, "E2521", {"start": v(-6185.96, -2032.8) * mm, "end": v(-5550.96, -1397.8) * mm});
            skLineSegment(sketch, "E2522", {"start": v(-5754.16, 2056.77) * mm, "end": v(-5767.42, 2055.9) * mm});
            skLineSegment(sketch, "E2523", {"start": v(-5664.48, 1277.1) * mm, "end": v(-5652.56, 1282.98) * mm});
            skLineSegment(sketch, "E2524", {"start": v(-6109.76, -585) * mm, "end": v(-5855.76, -839) * mm});
            skLineSegment(sketch, "E2525", {"start": v(-5855.76, 2361.4) * mm, "end": v(-6109.76, 2107.4) * mm});
            skLineSegment(sketch, "E2526", {"start": v(-5507.76, -108.76) * mm, "end": v(-5511.56, -117.95) * mm});
            skLineSegment(sketch, "E2527", {"start": v(-6363.76, -1855) * mm, "end": v(-6363.76, -1956.6) * mm});
            skLineSegment(sketch, "E2528", {"start": v(-5296.96, 2666.2) * mm, "end": v(-1842.56, 2666.2) * mm});
            skLineSegment(sketch, "E2529", {"start": v(-5834.76, 238.84) * mm, "end": v(-5842.15, 227.8) * mm});
            skLineSegment(sketch, "E2530", {"start": v(-5826, 248.83) * mm, "end": v(-5834.76, 238.84) * mm});
            skLineSegment(sketch, "E2531", {"start": v(-1697.76, 742.14) * mm, "end": v(-1691.7, 734.25) * mm});
            skLineSegment(sketch, "E2532", {"start": v(-6363.76, 3428.2) * mm, "end": v(-6363.76, 3377.4) * mm});
            skLineSegment(sketch, "E2533", {"start": v(-1534.3, 426.61) * mm, "end": v(-1530.03, 414.03) * mm});
            skLineSegment(sketch, "E2534", {"start": v(-1701.56, 751.33) * mm, "end": v(-1697.76, 742.14) * mm});
            skLineSegment(sketch, "E2535", {"start": v(-1536.9, 439.65) * mm, "end": v(-1534.3, 426.61) * mm});
            skLineSegment(sketch, "E2536", {"start": v(-1645.7, 794.19) * mm, "end": v(-1654.9, 798) * mm});
            skLineSegment(sketch, "E2537", {"start": v(-5664.48, 2049.04) * mm, "end": v(-5677.06, 2053.3) * mm});
            skLineSegment(sketch, "E2538", {"start": v(-5512.86, -127.8) * mm, "end": v(-5511.56, -137.67) * mm});
            skLineSegment(sketch, "E2539", {"start": v(-5511.56, -137.67) * mm, "end": v(-5507.76, -146.86) * mm});
            skLineSegment(sketch, "E2540", {"start": v(-5955.82, -154.75) * mm, "end": v(-5949.76, -146.86) * mm});
            skLineSegment(sketch, "E2541", {"start": v(-5622.75, 238.84) * mm, "end": v(-5631.52, 248.83) * mm});
            skLineSegment(sketch, "E2542", {"start": v(-5437.96, 1660.05) * mm, "end": v(-5441.76, 1669.24) * mm});
            skLineSegment(sketch, "E2543", {"start": v(-5441.76, 1669.24) * mm, "end": v(-5447.82, 1677.13) * mm});
            skLineSegment(sketch, "E2544", {"start": v(-1475.04, 359.04) * mm, "end": v(-1462.46, 354.77) * mm});
            skLineSegment(sketch, "E2545", {"start": v(-5949.76, 1669.24) * mm, "end": v(-5955.82, 1677.13) * mm});
            skLineSegment(sketch, "E2546", {"start": v(-5982.76, 1612.1) * mm, "end": v(-5972.9, 1613.39) * mm});
            skLineSegment(sketch, "E2547", {"start": v(-5972.9, 1613.39) * mm, "end": v(-5963.7, 1617.2) * mm});
            skLineSegment(sketch, "E2548", {"start": v(-5501.7, 1677.13) * mm, "end": v(-5507.76, 1669.24) * mm});
            skLineSegment(sketch, "E2549", {"start": v(-5507.76, 1669.24) * mm, "end": v(-5511.56, 1660.05) * mm});
            skLineSegment(sketch, "E2550", {"start": v(-5511.56, 1660.05) * mm, "end": v(-5512.86, 1650.2) * mm});
            skLineSegment(sketch, "E2551", {"start": v(-5441.76, -146.86) * mm, "end": v(-5437.96, -137.67) * mm});
            skLineSegment(sketch, "E2552", {"start": v(-5848.03, 1332.09) * mm, "end": v(-5842.15, 1320.17) * mm});
            skLineSegment(sketch, "E2553", {"start": v(-5842.15, 1320.17) * mm, "end": v(-5834.76, 1309.12) * mm});
            skLineSegment(sketch, "E2554", {"start": v(-5834.76, 1309.12) * mm, "end": v(-5826, 1299.13) * mm});
            skLineSegment(sketch, "E2555", {"start": v(-5826, 1299.13) * mm, "end": v(-5816, 1290.37) * mm});
            skLineSegment(sketch, "E2556", {"start": v(-6363.76, -1855) * mm, "end": v(-5855.76, -1347) * mm});
            skLineSegment(sketch, "E2557", {"start": v(-1637.82, 734.25) * mm, "end": v(-1631.76, 742.14) * mm});
            skLineSegment(sketch, "E2558", {"start": v(-1631.76, 742.14) * mm, "end": v(-1627.96, 751.33) * mm});
            skLineSegment(sketch, "E2559", {"start": v(-5447.82, 1623.25) * mm, "end": v(-5441.76, 1631.14) * mm});
            skLineSegment(sketch, "E2560", {"start": v(-5441.76, 1631.14) * mm, "end": v(-5437.96, 1640.33) * mm});
            skLineSegment(sketch, "E2561", {"start": v(-1359.06, 354.77) * mm, "end": v(-1346.48, 359.04) * mm});
            skLineSegment(sketch, "E2562", {"start": v(-1372.1, 352.18) * mm, "end": v(-1359.06, 354.77) * mm});
            skLineSegment(sketch, "E2563", {"start": v(-1385.36, 351.3) * mm, "end": v(-1372.1, 352.18) * mm});
            skLineSegment(sketch, "E2564", {"start": v(-5474.76, -165.9) * mm, "end": v(-5464.9, -164.61) * mm});
            skLineSegment(sketch, "E2565", {"start": v(-4077.76, 888.2) * mm, "end": v(-4077.76, 634.2) * mm});
            skLineSegment(sketch, "E2566", {"start": v(-1664.76, 799.3) * mm, "end": v(-1674.62, 798) * mm});
            skLineSegment(sketch, "E2567", {"start": v(-5855.76, 888.2) * mm, "end": v(-5855.76, 634.2) * mm});
            skLineSegment(sketch, "E2568", {"start": v(-1189.76, 742.14) * mm, "end": v(-1183.7, 734.25) * mm});
            skLineSegment(sketch, "E2569", {"start": v(-6001.8, -160.8) * mm, "end": v(-5992.62, -164.61) * mm});
            skLineSegment(sketch, "E2570", {"start": v(-5484.62, -164.61) * mm, "end": v(-5474.76, -165.9) * mm});
            skLineSegment(sketch, "E2571", {"start": v(-5855.76, 1370.97) * mm, "end": v(-5855.76, 1955.17) * mm});
            skLineSegment(sketch, "E2572", {"start": v(-953.56, -2032.8) * mm, "end": v(-900.97, -2032.8) * mm});
            skLineSegment(sketch, "E2573", {"start": v(-5992.62, 1613.39) * mm, "end": v(-5982.76, 1612.1) * mm});
            skLineSegment(sketch, "E2574", {"start": v(-5804.96, 1282.98) * mm, "end": v(-5793.04, 1277.1) * mm});
            skLineSegment(sketch, "E2575", {"start": v(-5816, 1290.37) * mm, "end": v(-5804.96, 1282.98) * mm});
            skLineSegment(sketch, "E2576", {"start": v(-5852.3, 1344.67) * mm, "end": v(-5848.03, 1332.09) * mm});
            skLineSegment(sketch, "E2577", {"start": v(-5855.76, 1370.97) * mm, "end": v(-5854.9, 1357.7) * mm});
            skLineSegment(sketch, "E2578", {"start": v(-5690.1, 2055.9) * mm, "end": v(-5703.36, 2056.77) * mm});
            skLineSegment(sketch, "E2579", {"start": v(-5677.06, 2053.3) * mm, "end": v(-5690.1, 2055.9) * mm});
            skLineSegment(sketch, "E2580", {"start": v(-5641.5, 2035.77) * mm, "end": v(-5652.56, 2043.16) * mm});
            skLineSegment(sketch, "E2581", {"start": v(-5631.52, 2027.01) * mm, "end": v(-5641.5, 2035.77) * mm});
            skLineSegment(sketch, "E2582", {"start": v(-5615.37, 2005.97) * mm, "end": v(-5622.75, 2017.02) * mm});
            skLineSegment(sketch, "E2583", {"start": v(-5949.76, -146.86) * mm, "end": v(-5945.96, -137.67) * mm});
            skLineSegment(sketch, "E2584", {"start": v(-5945.96, -137.67) * mm, "end": v(-5944.66, -127.8) * mm});
            skLineSegment(sketch, "E2585", {"start": v(-5677.06, -505.35) * mm, "end": v(-5664.48, -501.07) * mm});
            skLineSegment(sketch, "E2586", {"start": v(-851.96, -2032.8) * mm, "end": v(-775.76, -1956.6) * mm});
            skLineSegment(sketch, "E2587", {"start": v(-5609.5, -446.09) * mm, "end": v(-5605.22, -433.5) * mm});
            skLineSegment(sketch, "E2588", {"start": v(-5605.22, -433.5) * mm, "end": v(-5602.63, -420.47) * mm});
            skLineSegment(sketch, "E2589", {"start": v(-5602.63, -420.47) * mm, "end": v(-5601.76, -407.2) * mm});
            skLineSegment(sketch, "E2590", {"start": v(-5455.7, 1683.19) * mm, "end": v(-5464.9, 1687) * mm});
            skLineSegment(sketch, "E2591", {"start": v(-1156.76, 723.1) * mm, "end": v(-1146.9, 724.39) * mm});
            skLineSegment(sketch, "E2592", {"start": v(-5550.96, 2920.2) * mm, "end": v(-1588.56, 2920.2) * mm});
            skLineSegment(sketch, "E2593", {"start": v(-5501.7, 1623.25) * mm, "end": v(-5493.8, 1617.2) * mm});
            skLineSegment(sketch, "E2594", {"start": v(-5982.76, -89.7) * mm, "end": v(-5992.62, -91) * mm});
            skLineSegment(sketch, "E2595", {"start": v(-5992.62, -91) * mm, "end": v(-6001.8, -94.81) * mm});
            skLineSegment(sketch, "E2596", {"start": v(-5664.48, -501.07) * mm, "end": v(-5652.56, -495.2) * mm});
            skLineSegment(sketch, "E2597", {"start": v(-5652.56, -495.2) * mm, "end": v(-5641.5, -487.81) * mm});
            skLineSegment(sketch, "E2598", {"start": v(-5641.5, -487.81) * mm, "end": v(-5631.52, -479.05) * mm});
            skLineSegment(sketch, "E2599", {"start": v(-1123.76, 742.14) * mm, "end": v(-1122.43, 745.36) * mm});
            skLineSegment(sketch, "E2600", {"start": v(-1119.96, 751.33) * mm, "end": v(-1118.66, 761.2) * mm});
            skLineSegment(sketch, "E2601", {"start": v(-1626.66, 761.2) * mm, "end": v(-1627.96, 771.05) * mm});
            skLineSegment(sketch, "E2602", {"start": v(-6020.86, 1650.2) * mm, "end": v(-6019.56, 1640.33) * mm});
            skLineSegment(sketch, "E2603", {"start": v(-6019.56, 1640.33) * mm, "end": v(-6015.76, 1631.14) * mm});
            skLineSegment(sketch, "E2604", {"start": v(-5601.76, 634.2) * mm, "end": v(-5601.76, 888.2) * mm});
            skLineSegment(sketch, "E2605", {"start": v(-1193.56, 751.33) * mm, "end": v(-1189.76, 742.14) * mm});
            skLineSegment(sketch, "E2606", {"start": v(-5855.76, 634.2) * mm, "end": v(-6109.76, 380.2) * mm});
            skLineSegment(sketch, "E2607", {"start": v(-5992.62, -164.61) * mm, "end": v(-5982.76, -165.9) * mm});
            skLineSegment(sketch, "E2608", {"start": v(-1462.46, 354.77) * mm, "end": v(-1449.42, 352.18) * mm});
            skLineSegment(sketch, "E2609", {"start": v(-1449.42, 352.18) * mm, "end": v(-1436.16, 351.3) * mm});
            skLineSegment(sketch, "E2610", {"start": v(-1385.36, 351.3) * mm, "end": v(-1436.16, 351.3) * mm});
            skLineSegment(sketch, "E2611", {"start": v(-5631.52, -479.05) * mm, "end": v(-5622.75, -469.06) * mm});
            skLineSegment(sketch, "E2612", {"start": v(-5622.75, -469.06) * mm, "end": v(-5615.37, -458) * mm});
            skLineSegment(sketch, "E2613", {"start": v(-5615.37, -458) * mm, "end": v(-5609.5, -446.09) * mm});
            skLineSegment(sketch, "E2614", {"start": v(-4585.76, 1396.2) * mm, "end": v(-4077.76, 888.2) * mm});
            skLineSegment(sketch, "E2615", {"start": v(-5852.3, -433.5) * mm, "end": v(-5848.03, -446.09) * mm});
            skLineSegment(sketch, "E2616", {"start": v(-1516.76, 391.06) * mm, "end": v(-1508, 381.07) * mm});
            skLineSegment(sketch, "E2617", {"start": v(-6109.76, 1142.2) * mm, "end": v(-5855.76, 888.2) * mm});
            skLineSegment(sketch, "E2618", {"start": v(-5664.48, 270.86) * mm, "end": v(-5677.06, 275.13) * mm});
            skLineSegment(sketch, "E2619", {"start": v(-5677.06, 275.13) * mm, "end": v(-5690.1, 277.72) * mm});
            skLineSegment(sketch, "E2620", {"start": v(-5690.1, 277.72) * mm, "end": v(-5703.36, 278.6) * mm});
            skLineSegment(sketch, "E2621", {"start": v(-6363.76, 3479) * mm, "end": v(-6363.76, 3428.2) * mm});
            skLineSegment(sketch, "E2622", {"start": v(-6363.76, -1956.6) * mm, "end": v(-6287.56, -2032.8) * mm});
            skLineSegment(sketch, "E2623", {"start": v(-1537.76, 452.9) * mm, "end": v(-1536.9, 439.65) * mm});
            skLineSegment(sketch, "E2624", {"start": v(-6020.86, -127.8) * mm, "end": v(-6019.56, -137.67) * mm});
            skLineSegment(sketch, "E2625", {"start": v(-5754.16, 278.6) * mm, "end": v(-5767.42, 277.72) * mm});
            skLineSegment(sketch, "E2626", {"start": v(-5767.42, 277.72) * mm, "end": v(-5780.46, 275.13) * mm});
            skLineSegment(sketch, "E2627", {"start": v(-5455.7, 1617.2) * mm, "end": v(-5447.82, 1623.25) * mm});
            skLineSegment(sketch, "E2628", {"start": v(-5855.76, -407.2) * mm, "end": v(-5855.76, 177) * mm});
            skLineSegment(sketch, "E2629", {"start": v(-5855.76, -407.2) * mm, "end": v(-5854.9, -420.47) * mm});
            skLineSegment(sketch, "E2630", {"start": v(-5854.9, -420.47) * mm, "end": v(-5852.3, -433.5) * mm});
            skLineSegment(sketch, "E2631", {"start": v(-1283.76, 177) * mm, "end": v(-1791.76, -331) * mm});
            skLineSegment(sketch, "E2632", {"start": v(-1118.66, 761.2) * mm, "end": v(-1119.96, 771.05) * mm});
            skLineSegment(sketch, "E2633", {"start": v(-775.76, 3479) * mm, "end": v(-851.96, 3555.2) * mm});
            skLineSegment(sketch, "E2634", {"start": v(-6109.76, 2107.4) * mm, "end": v(-6109.76, 1142.2) * mm});
            skLineSegment(sketch, "E2635", {"start": v(-5972.9, 1687) * mm, "end": v(-5982.76, 1688.3) * mm});
            skLineSegment(sketch, "E2636", {"start": v(-5982.76, 1688.3) * mm, "end": v(-5992.62, 1687) * mm});
            skLineSegment(sketch, "E2637", {"start": v(-5703.36, -508.8) * mm, "end": v(-5690.1, -507.94) * mm});
            skLineSegment(sketch, "E2638", {"start": v(-5780.46, -505.35) * mm, "end": v(-5767.42, -507.94) * mm});
            skLineSegment(sketch, "E2639", {"start": v(-5767.42, -507.94) * mm, "end": v(-5754.16, -508.8) * mm});
            skLineSegment(sketch, "E2640", {"start": v(-775.76, -1855) * mm, "end": v(-1283.76, -1347) * mm});
            skLineSegment(sketch, "E2641", {"start": v(-5493.8, -160.8) * mm, "end": v(-5484.62, -164.61) * mm});
            skLineSegment(sketch, "E2642", {"start": v(-1283.76, -1347) * mm, "end": v(-1791.76, -839) * mm});
            skLineSegment(sketch, "E2643", {"start": v(-1791.76, -839) * mm, "end": v(-1791.76, -331) * mm});
            skLineSegment(sketch, "E2644", {"start": v(-1284.63, 1050.37) * mm, "end": v(-1287.22, 1063.4) * mm});
            skLineSegment(sketch, "E2645", {"start": v(-1283.76, 1037.1) * mm, "end": v(-1284.63, 1050.37) * mm});
            skLineSegment(sketch, "E2646", {"start": v(-5652.56, 264.98) * mm, "end": v(-5664.48, 270.86) * mm});
            skLineSegment(sketch, "E2647", {"start": v(-5641.5, 257.6) * mm, "end": v(-5652.56, 264.98) * mm});
            skLineSegment(sketch, "E2648", {"start": v(-5631.52, 248.83) * mm, "end": v(-5641.5, 257.6) * mm});
            skLineSegment(sketch, "E2649", {"start": v(-5437.96, -117.95) * mm, "end": v(-5441.76, -108.76) * mm});
            skLineSegment(sketch, "E2650", {"start": v(-953.56, 3555.2) * mm, "end": v(-1537.76, 2971) * mm});
            skLineSegment(sketch, "E2651", {"start": v(-5955.82, -100.87) * mm, "end": v(-5963.7, -94.81) * mm});
            skLineSegment(sketch, "E2652", {"start": v(-5963.7, -94.81) * mm, "end": v(-5972.9, -91) * mm});
            skLineSegment(sketch, "E2653", {"start": v(-5972.9, -91) * mm, "end": v(-5982.76, -89.7) * mm});
            skLineSegment(sketch, "E2654", {"start": v(-5437.96, 1640.33) * mm, "end": v(-5436.66, 1650.2) * mm});
            skLineSegment(sketch, "E2655", {"start": v(-5944.66, -127.8) * mm, "end": v(-5945.96, -117.95) * mm});
            skLineSegment(sketch, "E2656", {"start": v(-4585.76, 126.2) * mm, "end": v(-5093.76, 126.2) * mm});
            skLineSegment(sketch, "E2657", {"start": v(-5511.56, -117.95) * mm, "end": v(-5512.86, -127.8) * mm});
            skLineSegment(sketch, "E2658", {"start": v(-5963.7, -160.8) * mm, "end": v(-5955.82, -154.75) * mm});
            skLineSegment(sketch, "E2659", {"start": v(-6287.56, 3555.2) * mm, "end": v(-6363.76, 3479) * mm});
            skLineSegment(sketch, "E2660", {"start": v(-851.96, 3555.2) * mm, "end": v(-953.56, 3555.2) * mm});
            skLineSegment(sketch, "E2661", {"start": v(-6236.76, 3555.2) * mm, "end": v(-6234.97, 3555.2) * mm});
            skLineSegment(sketch, "E2662", {"start": v(-6009.7, -154.75) * mm, "end": v(-6001.8, -160.8) * mm});
            skLineSegment(sketch, "E2663", {"start": v(-5464.9, -164.61) * mm, "end": v(-5455.7, -160.8) * mm});
            skLineSegment(sketch, "E2664", {"start": v(-5455.7, -160.8) * mm, "end": v(-5447.82, -154.75) * mm});
            skLineSegment(sketch, "E2665", {"start": v(-5447.82, -154.75) * mm, "end": v(-5441.76, -146.86) * mm});
            skLineSegment(sketch, "E2666", {"start": v(-6185.96, -2032.8) * mm, "end": v(-6234.97, -2032.8) * mm});
            skLineSegment(sketch, "E2667", {"start": v(-1627.96, 771.05) * mm, "end": v(-1631.76, 780.24) * mm});
            skLineSegment(sketch, "E2668", {"start": v(-775.76, 3377.4) * mm, "end": v(-1791.76, 2361.4) * mm});
            skLineSegment(sketch, "E2669", {"start": v(-1508, 1108.95) * mm, "end": v(-1516.76, 1098.96) * mm});
            skLineSegment(sketch, "E2670", {"start": v(-1498.01, 1117.71) * mm, "end": v(-1508, 1108.95) * mm});
            skLineSegment(sketch, "E2671", {"start": v(-1475.04, 1130.97) * mm, "end": v(-1486.96, 1125.1) * mm});
            skLineSegment(sketch, "E2672", {"start": v(-1462.46, 1135.25) * mm, "end": v(-1475.04, 1130.97) * mm});
            skLineSegment(sketch, "E2673", {"start": v(-1323.5, 372.3) * mm, "end": v(-1313.52, 381.07) * mm});
            skLineSegment(sketch, "E2674", {"start": v(-5609.5, 215.87) * mm, "end": v(-5615.37, 227.8) * mm});
            skLineSegment(sketch, "E2675", {"start": v(-5615.37, 227.8) * mm, "end": v(-5622.75, 238.84) * mm});
            skLineSegment(sketch, "E2676", {"start": v(-775.76, -1855) * mm, "end": v(-775.76, -1956.6) * mm});
            skLineSegment(sketch, "E2677", {"start": v(-5855.76, -1347) * mm, "end": v(-5855.76, -839) * mm});
            skLineSegment(sketch, "E2678", {"start": v(-5501.7, -154.75) * mm, "end": v(-5493.8, -160.8) * mm});
            skLineSegment(sketch, "E2679", {"start": v(-6236.76, 3555.2) * mm, "end": v(-6287.56, 3555.2) * mm});
            skLineSegment(sketch, "E2680", {"start": v(-1791.76, 1853.4) * mm, "end": v(-1791.76, 2361.4) * mm});
            skLineSegment(sketch, "E2681", {"start": v(-1283.76, 1345.4) * mm, "end": v(-1791.76, 1853.4) * mm});
            skLineSegment(sketch, "E2682", {"start": v(-5436.66, -127.8) * mm, "end": v(-5437.96, -117.95) * mm});
            skLineSegment(sketch, "E2683", {"start": v(-5447.82, -100.87) * mm, "end": v(-5455.7, -94.81) * mm});
            skLineSegment(sketch, "E2684", {"start": v(-1284.63, 439.65) * mm, "end": v(-1283.76, 452.9) * mm});
            skLineSegment(sketch, "E2685", {"start": v(-5464.9, -91) * mm, "end": v(-5474.76, -89.7) * mm});
            skLineSegment(sketch, "E2686", {"start": v(-5963.7, 1617.2) * mm, "end": v(-5955.82, 1623.25) * mm});
            skLineSegment(sketch, "E2687", {"start": v(-1283.76, 1037.1) * mm, "end": v(-1283.76, 452.9) * mm});
            skLineSegment(sketch, "E2688", {"start": v(-1372.1, 1137.84) * mm, "end": v(-1385.36, 1138.7) * mm});
            skLineSegment(sketch, "E2689", {"start": v(-1359.06, 1135.25) * mm, "end": v(-1372.1, 1137.84) * mm});
            skLineSegment(sketch, "E2690", {"start": v(-1189.76, 780.24) * mm, "end": v(-1193.56, 771.05) * mm});
            skLineSegment(sketch, "E2691", {"start": v(-1183.7, 788.13) * mm, "end": v(-1189.76, 780.24) * mm});
            skLineSegment(sketch, "E2692", {"start": v(-5550.96, -1397.8) * mm, "end": v(-1588.56, -1397.8) * mm});
            skLineSegment(sketch, "E2693", {"start": v(-5848.03, 215.87) * mm, "end": v(-5852.3, 203.29) * mm});
            skLineSegment(sketch, "E2694", {"start": v(-5852.3, 203.29) * mm, "end": v(-5854.9, 190.25) * mm});
            skLineSegment(sketch, "E2695", {"start": v(-5854.9, 190.25) * mm, "end": v(-5855.76, 177) * mm});
            skLineSegment(sketch, "E2696", {"start": v(-5754.16, 278.6) * mm, "end": v(-5703.36, 278.6) * mm});
            skLineSegment(sketch, "E2697", {"start": v(-953.56, -2032.8) * mm, "end": v(-1588.56, -1397.8) * mm});
            skLineSegment(sketch, "E2698", {"start": v(-1146.9, 798) * mm, "end": v(-1156.76, 799.3) * mm});
            skLineSegment(sketch, "E2699", {"start": v(-5484.62, -91) * mm, "end": v(-5493.8, -94.81) * mm});
            skLineSegment(sketch, "E2700", {"start": v(-5493.8, -94.81) * mm, "end": v(-5501.7, -100.87) * mm});
            skLineSegment(sketch, "E2701", {"start": v(-1029.76, 1091.4) * mm, "end": v(-1283.76, 1345.4) * mm});
            skLineSegment(sketch, "E2702", {"start": v(-775.76, 3453.6) * mm, "end": v(-775.76, 3479) * mm});
            skLineSegment(sketch, "E2703", {"start": v(-6185.96, 3555.2) * mm, "end": v(-5550.96, 2920.2) * mm});
            skLineSegment(sketch, "E2704", {"start": v(-3569.76, 182.36) * mm, "end": v(-3568.81, 182.23) * mm});
            skLineSegment(sketch, "E2705", {"start": v(-1029.76, 1091.4) * mm, "end": v(-1029.76, 431) * mm});
            skLineSegment(sketch, "E2706", {"start": v(-900.97, -2032.8) * mm, "end": v(-851.96, -2032.8) * mm});
            skLineSegment(sketch, "E2707", {"start": v(-6109.76, 380.2) * mm, "end": v(-6109.76, -585) * mm});
            skLineSegment(sketch, "E2708", {"start": v(-6234.97, 3555.2) * mm, "end": v(-6185.96, 3555.2) * mm});
            skLineSegment(sketch, "E2709", {"start": v(-6234.97, -2032.8) * mm, "end": v(-6287.56, -2032.8) * mm});
            skLineSegment(sketch, "E2710", {"start": v(-3580.65, 1224.68) * mm, "end": v(-3569.76, 1223.25) * mm});
            skLineSegment(sketch, "E2711", {"start": v(-3524.66, 1257.01) * mm, "end": v(-3523.1, 1268.85) * mm});
            skLineSegment(sketch, "E2712", {"start": v(-3601.15, 1301.16) * mm, "end": v(-3608.42, 1291.7) * mm});
            skLineSegment(sketch, "E2713", {"start": v(-3608.42, 1291.7) * mm, "end": v(-3612.98, 1280.67) * mm});
            skLineSegment(sketch, "E2714", {"start": v(-3608.41, 1245.98) * mm, "end": v(-3601.14, 1236.5) * mm});
            skLineSegment(sketch, "E2715", {"start": v(-3557, 1313) * mm, "end": v(-3568.83, 1314.56) * mm});
            skLineSegment(sketch, "E2716", {"start": v(-3569.76, 1314.44) * mm, "end": v(-3580.66, 1313) * mm});
            skLineSegment(sketch, "E2717", {"start": v(-6268.49, 3403.92) * mm, "end": v(-6263.92, 3392.9) * mm});
            skLineSegment(sketch, "E2718", {"start": v(-6263.92, 3392.9) * mm, "end": v(-6256.65, 3383.43) * mm});
            skLineSegment(sketch, "E2719", {"start": v(-6247.18, 3376.16) * mm, "end": v(-6236.16, 3371.6) * mm});
            skLineSegment(sketch, "E2720", {"start": v(-6234.97, 3459.94) * mm, "end": v(-6236.16, 3459.92) * mm});
            skLineSegment(sketch, "E2721", {"start": v(-892.34, 3455.35) * mm, "end": v(-903.36, 3459.92) * mm});
            skLineSegment(sketch, "E2722", {"start": v(-903.36, 3459.92) * mm, "end": v(-915.2, 3461.47) * mm});
            skLineSegment(sketch, "E2723", {"start": v(-954.8, 3438.61) * mm, "end": v(-959.36, 3427.59) * mm});
            skLineSegment(sketch, "E2724", {"start": v(-959.36, 3403.92) * mm, "end": v(-954.8, 3392.9) * mm});
            skLineSegment(sketch, "E2725", {"start": v(-927.03, 3371.6) * mm, "end": v(-915.2, 3370.03) * mm});
            skLineSegment(sketch, "E2726", {"start": v(-882.87, 3383.43) * mm, "end": v(-875.6, 3392.9) * mm});
            skLineSegment(sketch, "E2727", {"start": v(-871.03, 3403.92) * mm, "end": v(-869.48, 3415.75) * mm});
            skLineSegment(sketch, "E2728", {"start": v(-869.48, 3415.75) * mm, "end": v(-871.03, 3427.59) * mm});
            skLineSegment(sketch, "E2729", {"start": v(-871.03, 3427.59) * mm, "end": v(-875.6, 3438.61) * mm});
            skLineSegment(sketch, "E2730", {"start": v(-875.6, 3438.61) * mm, "end": v(-882.87, 3448.08) * mm});
            skLineSegment(sketch, "E2731", {"start": v(-954.8, -1916.23) * mm, "end": v(-947.53, -1925.7) * mm});
            skLineSegment(sketch, "E2732", {"start": v(-947.53, -1925.7) * mm, "end": v(-938.06, -1932.97) * mm});
            skLineSegment(sketch, "E2733", {"start": v(-903.36, -1937.53) * mm, "end": v(-892.34, -1932.97) * mm});
            skLineSegment(sketch, "E2734", {"start": v(-6256.29, -1860.16) * mm, "end": v(-6263.66, -1869.54) * mm});
            skLineSegment(sketch, "E2735", {"start": v(-6180.3, -1905.17) * mm, "end": v(-6178.6, -1893.36) * mm});
            skLineSegment(sketch, "E2736", {"start": v(-6180.03, -1881.5) * mm, "end": v(-6184.48, -1870.43) * mm});
            skLineSegment(sketch, "E2737", {"start": v(-6570.25, -4547.4) * mm, "end": v(-6571.81, -4535.58) * mm});
            skLineSegment(sketch, "E2738", {"start": v(-6571.81, -4535.58) * mm, "end": v(-6576.38, -4524.55) * mm});
            skLineSegment(sketch, "E2739", {"start": v(-6576.38, -4524.55) * mm, "end": v(-6583.64, -4515.08) * mm});
            skLineSegment(sketch, "E2740", {"start": v(-6583.64, -4515.08) * mm, "end": v(-6593.11, -4507.81) * mm});
            skLineSegment(sketch, "E2741", {"start": v(-6593.11, -4507.81) * mm, "end": v(-6604.14, -4503.25) * mm});
            skLineSegment(sketch, "E2742", {"start": v(-6604.14, -4503.25) * mm, "end": v(-6615.97, -4501.69) * mm});
            skLineSegment(sketch, "E2743", {"start": v(-6615.97, -4501.69) * mm, "end": v(-6627.8, -4503.25) * mm});
            skLineSegment(sketch, "E2744", {"start": v(-6627.8, -4503.25) * mm, "end": v(-6638.83, -4507.81) * mm});
            skLineSegment(sketch, "E2745", {"start": v(-6638.83, -4507.81) * mm, "end": v(-6648.3, -4515.08) * mm});
            skLineSegment(sketch, "E2746", {"start": v(-6648.3, -4515.08) * mm, "end": v(-6655.57, -4524.55) * mm});
            skLineSegment(sketch, "E2747", {"start": v(-6655.57, -4524.55) * mm, "end": v(-6660.13, -4535.58) * mm});
            skLineSegment(sketch, "E2748", {"start": v(-6660.13, -4535.58) * mm, "end": v(-6661.7, -4547.4) * mm});
            skLineSegment(sketch, "E2749", {"start": v(-6661.7, -4547.4) * mm, "end": v(-6660.13, -4559.24) * mm});
            skLineSegment(sketch, "E2750", {"start": v(-6660.13, -4559.24) * mm, "end": v(-6655.57, -4570.27) * mm});
            skLineSegment(sketch, "E2751", {"start": v(-6655.57, -4570.27) * mm, "end": v(-6648.3, -4579.74) * mm});
            skLineSegment(sketch, "E2752", {"start": v(-6648.3, -4579.74) * mm, "end": v(-6638.83, -4587) * mm});
            skLineSegment(sketch, "E2753", {"start": v(-6638.83, -4587) * mm, "end": v(-6627.8, -4591.57) * mm});
            skLineSegment(sketch, "E2754", {"start": v(-6627.8, -4591.57) * mm, "end": v(-6615.97, -4593.13) * mm});
            skLineSegment(sketch, "E2755", {"start": v(-6615.97, -4593.13) * mm, "end": v(-6604.14, -4591.57) * mm});
            skLineSegment(sketch, "E2756", {"start": v(-6604.14, -4591.57) * mm, "end": v(-6593.11, -4587) * mm});
            skLineSegment(sketch, "E2757", {"start": v(-6593.11, -4587) * mm, "end": v(-6583.64, -4579.74) * mm});
            skLineSegment(sketch, "E2758", {"start": v(-6583.64, -4579.74) * mm, "end": v(-6576.38, -4570.27) * mm});
            skLineSegment(sketch, "E2759", {"start": v(-6576.38, -4570.27) * mm, "end": v(-6571.81, -4559.24) * mm});
            skLineSegment(sketch, "E2760", {"start": v(-6571.81, -4559.24) * mm, "end": v(-6570.25, -4547.4) * mm});
            skLineSegment(sketch, "E2761", {"start": v(-4284.25, -4547.4) * mm, "end": v(-4285.81, -4535.58) * mm});
            skLineSegment(sketch, "E2762", {"start": v(-4285.81, -4535.58) * mm, "end": v(-4290.38, -4524.55) * mm});
            skLineSegment(sketch, "E2763", {"start": v(-4290.38, -4524.55) * mm, "end": v(-4297.64, -4515.08) * mm});
            skLineSegment(sketch, "E2764", {"start": v(-4297.64, -4515.08) * mm, "end": v(-4307.11, -4507.81) * mm});
            skLineSegment(sketch, "E2765", {"start": v(-4307.11, -4507.81) * mm, "end": v(-4318.14, -4503.25) * mm});
            skLineSegment(sketch, "E2766", {"start": v(-4318.14, -4503.25) * mm, "end": v(-4329.97, -4501.69) * mm});
            skLineSegment(sketch, "E2767", {"start": v(-4329.97, -4501.69) * mm, "end": v(-4341.8, -4503.25) * mm});
            skLineSegment(sketch, "E2768", {"start": v(-4341.8, -4503.25) * mm, "end": v(-4352.83, -4507.81) * mm});
            skLineSegment(sketch, "E2769", {"start": v(-4352.83, -4507.81) * mm, "end": v(-4362.3, -4515.08) * mm});
            skLineSegment(sketch, "E2770", {"start": v(-4362.3, -4515.08) * mm, "end": v(-4369.57, -4524.55) * mm});
            skLineSegment(sketch, "E2771", {"start": v(-4369.57, -4524.55) * mm, "end": v(-4374.13, -4535.58) * mm});
            skLineSegment(sketch, "E2772", {"start": v(-4374.13, -4535.58) * mm, "end": v(-4375.7, -4547.4) * mm});
            skLineSegment(sketch, "E2773", {"start": v(-4375.7, -4547.4) * mm, "end": v(-4374.13, -4559.24) * mm});
            skLineSegment(sketch, "E2774", {"start": v(-4374.13, -4559.24) * mm, "end": v(-4369.57, -4570.27) * mm});
            skLineSegment(sketch, "E2775", {"start": v(-4369.57, -4570.27) * mm, "end": v(-4362.3, -4579.74) * mm});
            skLineSegment(sketch, "E2776", {"start": v(-4362.3, -4579.74) * mm, "end": v(-4352.83, -4587) * mm});
            skLineSegment(sketch, "E2777", {"start": v(-4352.83, -4587) * mm, "end": v(-4341.8, -4591.57) * mm});
            skLineSegment(sketch, "E2778", {"start": v(-4341.8, -4591.57) * mm, "end": v(-4329.97, -4593.13) * mm});
            skLineSegment(sketch, "E2779", {"start": v(-4329.97, -4593.13) * mm, "end": v(-4318.14, -4591.57) * mm});
            skLineSegment(sketch, "E2780", {"start": v(-4318.14, -4591.57) * mm, "end": v(-4307.11, -4587) * mm});
            skLineSegment(sketch, "E2781", {"start": v(-4307.11, -4587) * mm, "end": v(-4297.64, -4579.74) * mm});
            skLineSegment(sketch, "E2782", {"start": v(-4297.64, -4579.74) * mm, "end": v(-4290.38, -4570.27) * mm});
            skLineSegment(sketch, "E2783", {"start": v(-4290.38, -4570.27) * mm, "end": v(-4285.81, -4559.24) * mm});
            skLineSegment(sketch, "E2784", {"start": v(-4285.81, -4559.24) * mm, "end": v(-4284.25, -4547.4) * mm});
            skLineSegment(sketch, "E2785", {"start": v(-1998.25, -4547.4) * mm, "end": v(-1999.81, -4535.58) * mm});
            skLineSegment(sketch, "E2786", {"start": v(-1999.81, -4535.58) * mm, "end": v(-2004.38, -4524.55) * mm});
            skLineSegment(sketch, "E2787", {"start": v(-2004.38, -4524.55) * mm, "end": v(-2011.64, -4515.08) * mm});
            skLineSegment(sketch, "E2788", {"start": v(-2011.64, -4515.08) * mm, "end": v(-2021.11, -4507.81) * mm});
            skLineSegment(sketch, "E2789", {"start": v(-2021.11, -4507.81) * mm, "end": v(-2032.14, -4503.25) * mm});
            skLineSegment(sketch, "E2790", {"start": v(-2032.14, -4503.25) * mm, "end": v(-2043.97, -4501.69) * mm});
            skLineSegment(sketch, "E2791", {"start": v(-2043.97, -4501.69) * mm, "end": v(-2055.8, -4503.25) * mm});
            skLineSegment(sketch, "E2792", {"start": v(-2055.8, -4503.25) * mm, "end": v(-2066.83, -4507.81) * mm});
            skLineSegment(sketch, "E2793", {"start": v(-2066.83, -4507.81) * mm, "end": v(-2076.3, -4515.08) * mm});
            skLineSegment(sketch, "E2794", {"start": v(-2076.3, -4515.08) * mm, "end": v(-2083.57, -4524.55) * mm});
            skLineSegment(sketch, "E2795", {"start": v(-2083.57, -4524.55) * mm, "end": v(-2088.14, -4535.58) * mm});
            skLineSegment(sketch, "E2796", {"start": v(-2088.14, -4535.58) * mm, "end": v(-2089.7, -4547.4) * mm});
            skLineSegment(sketch, "E2797", {"start": v(-2089.7, -4547.4) * mm, "end": v(-2088.14, -4559.24) * mm});
            skLineSegment(sketch, "E2798", {"start": v(-2088.14, -4559.24) * mm, "end": v(-2083.57, -4570.27) * mm});
            skLineSegment(sketch, "E2799", {"start": v(-2083.57, -4570.27) * mm, "end": v(-2076.3, -4579.74) * mm});
            skLineSegment(sketch, "E2800", {"start": v(-2076.3, -4579.74) * mm, "end": v(-2066.83, -4587) * mm});
            skLineSegment(sketch, "E2801", {"start": v(-2066.83, -4587) * mm, "end": v(-2055.8, -4591.57) * mm});
            skLineSegment(sketch, "E2802", {"start": v(-2055.8, -4591.57) * mm, "end": v(-2043.97, -4593.13) * mm});
            skLineSegment(sketch, "E2803", {"start": v(-2043.97, -4593.13) * mm, "end": v(-2032.14, -4591.57) * mm});
            skLineSegment(sketch, "E2804", {"start": v(-2032.14, -4591.57) * mm, "end": v(-2021.11, -4587) * mm});
            skLineSegment(sketch, "E2805", {"start": v(-2021.11, -4587) * mm, "end": v(-2011.64, -4579.74) * mm});
            skLineSegment(sketch, "E2806", {"start": v(-2011.64, -4579.74) * mm, "end": v(-2004.38, -4570.27) * mm});
            skLineSegment(sketch, "E2807", {"start": v(-2004.38, -4570.27) * mm, "end": v(-1999.81, -4559.24) * mm});
            skLineSegment(sketch, "E2808", {"start": v(-1999.81, -4559.24) * mm, "end": v(-1998.25, -4547.4) * mm});
            skLineSegment(sketch, "E2809", {"start": v(196.3, -4547.4) * mm, "end": v(197.86, -4559.24) * mm});
            skLineSegment(sketch, "E2810", {"start": v(197.86, -4559.24) * mm, "end": v(202.43, -4570.27) * mm});
            skLineSegment(sketch, "E2811", {"start": v(202.43, -4570.27) * mm, "end": v(209.7, -4579.74) * mm});
            skLineSegment(sketch, "E2812", {"start": v(209.7, -4579.74) * mm, "end": v(219.17, -4587) * mm});
            skLineSegment(sketch, "E2813", {"start": v(219.17, -4587) * mm, "end": v(230.2, -4591.57) * mm});
            skLineSegment(sketch, "E2814", {"start": v(230.2, -4591.57) * mm, "end": v(242.03, -4593.13) * mm});
            skLineSegment(sketch, "E2815", {"start": v(242.03, -4593.13) * mm, "end": v(253.86, -4591.57) * mm});
            skLineSegment(sketch, "E2816", {"start": v(253.86, -4591.57) * mm, "end": v(264.89, -4587) * mm});
            skLineSegment(sketch, "E2817", {"start": v(264.89, -4587) * mm, "end": v(274.36, -4579.74) * mm});
            skLineSegment(sketch, "E2818", {"start": v(274.36, -4579.74) * mm, "end": v(281.62, -4570.27) * mm});
            skLineSegment(sketch, "E2819", {"start": v(281.62, -4570.27) * mm, "end": v(286.19, -4559.24) * mm});
            skLineSegment(sketch, "E2820", {"start": v(286.19, -4559.24) * mm, "end": v(287.75, -4547.4) * mm});
            skLineSegment(sketch, "E2821", {"start": v(287.75, -4547.4) * mm, "end": v(286.19, -4535.58) * mm});
            skLineSegment(sketch, "E2822", {"start": v(286.19, -4535.58) * mm, "end": v(281.62, -4524.55) * mm});
            skLineSegment(sketch, "E2823", {"start": v(281.62, -4524.55) * mm, "end": v(274.36, -4515.08) * mm});
            skLineSegment(sketch, "E2824", {"start": v(274.36, -4515.08) * mm, "end": v(264.89, -4507.81) * mm});
            skLineSegment(sketch, "E2825", {"start": v(264.89, -4507.81) * mm, "end": v(253.86, -4503.25) * mm});
            skLineSegment(sketch, "E2826", {"start": v(253.86, -4503.25) * mm, "end": v(242.03, -4501.69) * mm});
            skLineSegment(sketch, "E2827", {"start": v(242.03, -4501.69) * mm, "end": v(230.2, -4503.25) * mm});
            skLineSegment(sketch, "E2828", {"start": v(230.2, -4503.25) * mm, "end": v(219.17, -4507.81) * mm});
            skLineSegment(sketch, "E2829", {"start": v(219.17, -4507.81) * mm, "end": v(209.7, -4515.08) * mm});
            skLineSegment(sketch, "E2830", {"start": v(209.7, -4515.08) * mm, "end": v(202.43, -4524.55) * mm});
            skLineSegment(sketch, "E2831", {"start": v(202.43, -4524.55) * mm, "end": v(197.86, -4535.58) * mm});
            skLineSegment(sketch, "E2832", {"start": v(197.86, -4535.58) * mm, "end": v(196.3, -4547.4) * mm});
            skLineSegment(sketch, "E2833", {"start": v(-775.76, 3453.6) * mm, "end": v(-775.76, 3377.4) * mm});
            skLineSegment(sketch, "E2834", {"start": v(-6363.76, 3377.4) * mm, "end": v(-5855.76, 2869.4) * mm});
            skLineSegment(sketch, "E2835", {"start": v(-1537.76, 2971) * mm, "end": v(-1588.56, 2920.2) * mm});
            skLineSegment(sketch, "E2836", {"start": v(-2553.76, 1955) * mm, "end": v(-2604.56, 1904.2) * mm});
            skLineSegment(sketch, "E2837", {"start": v(-2604.56, 1904.2) * mm, "end": v(-2858.56, 1650.2) * mm});
            skLineSegment(sketch, "E2838", {"start": v(-1842.56, 2666.2) * mm, "end": v(-2553.76, 1955) * mm});
            skLineSegment(sketch, "E2839", {"start": v(-2856.77, 1650.2) * mm, "end": v(-2858.56, 1650.2) * mm});
            skLineSegment(sketch, "E2840", {"start": v(-2858.56, 1650.2) * mm, "end": v(-4280.96, 1650.2) * mm});
            skLineSegment(sketch, "E2841", {"start": v(-5296.96, 2666.2) * mm, "end": v(-4280.96, 1650.2) * mm});
            skLineSegment(sketch, "E2842", {"start": v(-4077.76, 634.2) * mm, "end": v(-4585.76, 126.2) * mm});
            skLineSegment(sketch, "E2843", {"start": v(-4585.76, 1396.2) * mm, "end": v(-4583.97, 1396.2) * mm});
            skLineSegment(sketch, "E2844", {"start": v(-5601.76, 888.2) * mm, "end": v(-5093.76, 1396.2) * mm});
            skLineSegment(sketch, "E2845", {"start": v(-5093.76, 1396.2) * mm, "end": v(-4585.76, 1396.2) * mm});
            skLineSegment(sketch, "E2846", {"start": v(-5093.76, 126.2) * mm, "end": v(-5601.76, 634.2) * mm});
            skLineSegment(sketch, "E2847", {"start": v(-1791.76, 888.2) * mm, "end": v(-1791.76, 634.2) * mm});
            skLineSegment(sketch, "E2848", {"start": v(-3061.76, 634.2) * mm, "end": v(-3061.76, 888.2) * mm});
            skLineSegment(sketch, "E2849", {"start": v(-2043.97, 1140.4) * mm, "end": v(-1791.76, 888.2) * mm});
            skLineSegment(sketch, "E2850", {"start": v(-2299.76, 1396.2) * mm, "end": v(-2043.97, 1140.4) * mm});
            skLineSegment(sketch, "E2851", {"start": v(-1791.76, 634.2) * mm, "end": v(-2043.97, 381.98) * mm});
            skLineSegment(sketch, "E2852", {"start": v(-2553.76, 126.2) * mm, "end": v(-3061.76, 634.2) * mm});
            skLineSegment(sketch, "E2853", {"start": v(-3061.76, 888.2) * mm, "end": v(-2553.76, 1396.2) * mm});
            skLineSegment(sketch, "E2854", {"start": v(-2043.97, 381.98) * mm, "end": v(-2299.76, 126.2) * mm});
            skLineSegment(sketch, "E2855", {"start": v(-2553.76, 1396.2) * mm, "end": v(-2299.76, 1396.2) * mm});
            skLineSegment(sketch, "E2856", {"start": v(-2043.97, 381.98) * mm, "end": v(-2043.97, 380.2) * mm});
            skLineSegment(sketch, "E2857", {"start": v(-2299.76, 126.2) * mm, "end": v(-2553.76, 126.2) * mm});
            skLineSegment(sketch, "E2858", {"start": v(-1842.56, -1143.8) * mm, "end": v(-5295.17, -1143.8) * mm});
            skLineSegment(sketch, "E2859", {"start": v(-2858.56, -127.8) * mm, "end": v(-4279.17, -127.8) * mm});
            skLineSegment(sketch, "E2860", {"start": v(-1842.56, 2666.2) * mm, "end": v(-1840.77, 2666.2) * mm});
            skLineSegment(sketch, "E2861", {"start": v(-1287.22, 1063.4) * mm, "end": v(-1291.5, 1075.99) * mm});
            skLineSegment(sketch, "E2862", {"start": v(-1194.86, 761.2) * mm, "end": v(-1193.56, 751.33) * mm});
            skLineSegment(sketch, "E2863", {"start": v(-1674.62, 724.39) * mm, "end": v(-1664.76, 723.1) * mm});
            skLineSegment(sketch, "E2864", {"start": v(-1683.8, 728.2) * mm, "end": v(-1674.62, 724.39) * mm});
            skLineSegment(sketch, "E2865", {"start": v(-1691.7, 734.25) * mm, "end": v(-1683.8, 728.2) * mm});
            skLineSegment(sketch, "E2866", {"start": v(-1175.81, 794.19) * mm, "end": v(-1183.7, 788.13) * mm});
            skLineSegment(sketch, "E2867", {"start": v(-1627.96, 751.33) * mm, "end": v(-1626.66, 761.2) * mm});
            skLineSegment(sketch, "E2868", {"start": v(-1654.9, 724.39) * mm, "end": v(-1645.7, 728.2) * mm});
            skLineSegment(sketch, "E2869", {"start": v(-1664.76, 723.1) * mm, "end": v(-1654.9, 724.39) * mm});
            skLineSegment(sketch, "E2870", {"start": v(-1536.9, 1050.37) * mm, "end": v(-1537.76, 1037.1) * mm});
            skLineSegment(sketch, "E2871", {"start": v(-1516.76, 1098.96) * mm, "end": v(-1524.15, 1087.9) * mm});
            skLineSegment(sketch, "E2872", {"start": v(-1674.62, 798) * mm, "end": v(-1683.8, 794.19) * mm});
            skLineSegment(sketch, "E2873", {"start": v(-1166.62, 724.39) * mm, "end": v(-1156.76, 723.1) * mm});
            skLineSegment(sketch, "E2874", {"start": v(-1122.1, 776.23) * mm, "end": v(-1123.76, 780.24) * mm});
            skLineSegment(sketch, "E2875", {"start": v(-1122.43, 745.36) * mm, "end": v(-1119.96, 751.33) * mm});
            skLineSegment(sketch, "E2876", {"start": v(-1645.7, 728.2) * mm, "end": v(-1637.82, 734.25) * mm});
            skLineSegment(sketch, "E2877", {"start": v(-1119.96, 771.05) * mm, "end": v(-1122.1, 776.23) * mm});
            skLineSegment(sketch, "E2878", {"start": v(-1175.81, 728.2) * mm, "end": v(-1166.62, 724.39) * mm});
            skLineSegment(sketch, "E2879", {"start": v(-1129.82, 734.25) * mm, "end": v(-1123.76, 742.14) * mm});
            skLineSegment(sketch, "E2880", {"start": v(-1697.76, 780.24) * mm, "end": v(-1701.56, 771.05) * mm});
            skLineSegment(sketch, "E2881", {"start": v(-1137.71, 728.2) * mm, "end": v(-1129.82, 734.25) * mm});
            skLineSegment(sketch, "E2882", {"start": v(-1146.9, 724.39) * mm, "end": v(-1137.71, 728.2) * mm});
            skLineSegment(sketch, "E2883", {"start": v(-1449.42, 1137.84) * mm, "end": v(-1462.46, 1135.25) * mm});
            skLineSegment(sketch, "E2884", {"start": v(-1436.16, 1138.7) * mm, "end": v(-1449.42, 1137.84) * mm});
            skLineSegment(sketch, "E2885", {"start": v(-1436.16, 1138.7) * mm, "end": v(-1385.36, 1138.7) * mm});
            skLineSegment(sketch, "E2886", {"start": v(-1537.76, 452.9) * mm, "end": v(-1537.76, 1037.1) * mm});
            skLineSegment(sketch, "E2887", {"start": v(-1702.86, 761.2) * mm, "end": v(-1701.56, 751.33) * mm});
            skLineSegment(sketch, "E2888", {"start": v(-1524.15, 402.1) * mm, "end": v(-1516.76, 391.06) * mm});
            skLineSegment(sketch, "E2889", {"start": v(-1534.3, 1063.4) * mm, "end": v(-1536.9, 1050.37) * mm});
            skLineSegment(sketch, "E2890", {"start": v(-1530.03, 1075.99) * mm, "end": v(-1534.3, 1063.4) * mm});
            skLineSegment(sketch, "E2891", {"start": v(-1524.15, 1087.9) * mm, "end": v(-1530.03, 1075.99) * mm});
            skLineSegment(sketch, "E2892", {"start": v(-1701.56, 771.05) * mm, "end": v(-1702.86, 761.2) * mm});
            skLineSegment(sketch, "E2893", {"start": v(-1193.56, 771.05) * mm, "end": v(-1194.86, 761.2) * mm});
            skLineSegment(sketch, "E2894", {"start": v(-1323.5, 1117.71) * mm, "end": v(-1334.56, 1125.1) * mm});
            skLineSegment(sketch, "E2895", {"start": v(-1334.56, 1125.1) * mm, "end": v(-1346.48, 1130.97) * mm});
            skLineSegment(sketch, "E2896", {"start": v(-1346.48, 1130.97) * mm, "end": v(-1359.06, 1135.25) * mm});
            skLineSegment(sketch, "E2897", {"start": v(-1291.5, 1075.99) * mm, "end": v(-1297.37, 1087.9) * mm});
            skLineSegment(sketch, "E2898", {"start": v(-1129.82, 788.13) * mm, "end": v(-1137.71, 794.19) * mm});
            skLineSegment(sketch, "E2899", {"start": v(-1508, 381.07) * mm, "end": v(-1498.01, 372.3) * mm});
            skLineSegment(sketch, "E2900", {"start": v(-1297.37, 1087.9) * mm, "end": v(-1304.76, 1098.96) * mm});
            skLineSegment(sketch, "E2901", {"start": v(-1304.76, 1098.96) * mm, "end": v(-1313.52, 1108.95) * mm});
            skLineSegment(sketch, "E2902", {"start": v(-1313.52, 1108.95) * mm, "end": v(-1323.5, 1117.71) * mm});
            skLineSegment(sketch, "E2903", {"start": v(-1123.76, 780.24) * mm, "end": v(-1129.82, 788.13) * mm});
            skLineSegment(sketch, "E2904", {"start": v(-1304.76, 391.06) * mm, "end": v(-1297.37, 402.1) * mm});
            skLineSegment(sketch, "E2905", {"start": v(-1486.96, 1125.1) * mm, "end": v(-1498.01, 1117.71) * mm});
            skLineSegment(sketch, "E2906", {"start": v(-1530.03, 414.03) * mm, "end": v(-1524.15, 402.1) * mm});
            skLineSegment(sketch, "E2907", {"start": v(-1297.37, 402.1) * mm, "end": v(-1291.5, 414.03) * mm});
            skLineSegment(sketch, "E2908", {"start": v(-1291.5, 414.03) * mm, "end": v(-1287.22, 426.61) * mm});
            skLineSegment(sketch, "E2909", {"start": v(-1287.22, 426.61) * mm, "end": v(-1284.63, 439.65) * mm});
            skLineSegment(sketch, "E2910", {"start": v(-1637.82, 788.13) * mm, "end": v(-1645.7, 794.19) * mm});
            skLineSegment(sketch, "E2911", {"start": v(-1683.8, 794.19) * mm, "end": v(-1691.7, 788.13) * mm});
            skLineSegment(sketch, "E2912", {"start": v(-1654.9, 798) * mm, "end": v(-1664.76, 799.3) * mm});
            skLineSegment(sketch, "E2913", {"start": v(-1183.7, 734.25) * mm, "end": v(-1175.81, 728.2) * mm});
            skLineSegment(sketch, "E2914", {"start": v(-1631.76, 780.24) * mm, "end": v(-1637.82, 788.13) * mm});
            skLineSegment(sketch, "E2915", {"start": v(-1691.7, 788.13) * mm, "end": v(-1697.76, 780.24) * mm});
            skLineSegment(sketch, "E2916", {"start": v(-1166.62, 798) * mm, "end": v(-1175.81, 794.19) * mm});
            skLineSegment(sketch, "E2917", {"start": v(-1313.52, 381.07) * mm, "end": v(-1304.76, 391.06) * mm});
            skLineSegment(sketch, "E2918", {"start": v(-1334.56, 364.92) * mm, "end": v(-1323.5, 372.3) * mm});
            skLineSegment(sketch, "E2919", {"start": v(-1346.48, 359.04) * mm, "end": v(-1334.56, 364.92) * mm});
            skLineSegment(sketch, "E2920", {"start": v(-1137.71, 794.19) * mm, "end": v(-1146.9, 798) * mm});
            skLineSegment(sketch, "E2921", {"start": v(-1486.96, 364.92) * mm, "end": v(-1475.04, 359.04) * mm});
            skLineSegment(sketch, "E2922", {"start": v(-1498.01, 372.3) * mm, "end": v(-1486.96, 364.92) * mm});
            skLineSegment(sketch, "E2923", {"start": v(-1156.76, 799.3) * mm, "end": v(-1166.62, 798) * mm});
            skLineSegment(sketch, "E2924", {"start": v(-3580.66, 1313) * mm, "end": v(-3591.69, 1308.43) * mm});
            skLineSegment(sketch, "E2925", {"start": v(-3536.5, 1301.17) * mm, "end": v(-3545.97, 1308.44) * mm});
            skLineSegment(sketch, "E2926", {"start": v(-3614.54, 1268.83) * mm, "end": v(-3612.98, 1257) * mm});
            skLineSegment(sketch, "E2927", {"start": v(-3591.69, 1308.43) * mm, "end": v(-3601.15, 1301.16) * mm});
            skLineSegment(sketch, "E2928", {"start": v(-3568.83, 1314.56) * mm, "end": v(-3569.76, 1314.44) * mm});
            skLineSegment(sketch, "E2929", {"start": v(-3612.98, 239.78) * mm, "end": v(-3614.54, 227.95) * mm});
            skLineSegment(sketch, "E2930", {"start": v(-3529.22, 205.1) * mm, "end": v(-3524.66, 216.13) * mm});
            skLineSegment(sketch, "E2931", {"start": v(-3536.49, 195.63) * mm, "end": v(-3529.22, 205.1) * mm});
            skLineSegment(sketch, "E2932", {"start": v(-3580.65, 183.8) * mm, "end": v(-3569.76, 182.36) * mm});
            skLineSegment(sketch, "E2933", {"start": v(-3529.23, 250.82) * mm, "end": v(-3536.5, 260.29) * mm});
            skLineSegment(sketch, "E2934", {"start": v(-3569.76, 1223.25) * mm, "end": v(-3568.81, 1223.12) * mm});
            skLineSegment(sketch, "E2935", {"start": v(-3591.69, 267.55) * mm, "end": v(-3601.15, 260.28) * mm});
            skLineSegment(sketch, "E2936", {"start": v(-3608.41, 205.09) * mm, "end": v(-3601.14, 195.62) * mm});
            skLineSegment(sketch, "E2937", {"start": v(-3614.54, 227.95) * mm, "end": v(-3612.98, 216.11) * mm});
            skLineSegment(sketch, "E2938", {"start": v(-3536.49, 1236.52) * mm, "end": v(-3529.22, 1245.99) * mm});
            skLineSegment(sketch, "E2939", {"start": v(-3545.95, 1229.25) * mm, "end": v(-3536.49, 1236.52) * mm});
            skLineSegment(sketch, "E2940", {"start": v(-3556.98, 1224.68) * mm, "end": v(-3545.95, 1229.25) * mm});
            skLineSegment(sketch, "E2941", {"start": v(-3568.81, 1223.12) * mm, "end": v(-3556.98, 1224.68) * mm});
            skLineSegment(sketch, "E2942", {"start": v(-3591.67, 1229.24) * mm, "end": v(-3580.65, 1224.68) * mm});
            skLineSegment(sketch, "E2943", {"start": v(-3601.14, 1236.5) * mm, "end": v(-3591.67, 1229.24) * mm});
            skLineSegment(sketch, "E2944", {"start": v(-3529.23, 1291.7) * mm, "end": v(-3536.5, 1301.17) * mm});
            skLineSegment(sketch, "E2945", {"start": v(-3524.66, 1280.68) * mm, "end": v(-3529.23, 1291.7) * mm});
            skLineSegment(sketch, "E2946", {"start": v(-3523.1, 1268.85) * mm, "end": v(-3524.66, 1280.68) * mm});
            skLineSegment(sketch, "E2947", {"start": v(-3545.97, 1308.44) * mm, "end": v(-3557, 1313) * mm});
            skLineSegment(sketch, "E2948", {"start": v(-3529.22, 1245.99) * mm, "end": v(-3524.66, 1257.01) * mm});
            skLineSegment(sketch, "E2949", {"start": v(-3569.76, 273.55) * mm, "end": v(-3580.66, 272.11) * mm});
            skLineSegment(sketch, "E2950", {"start": v(-3612.98, 1280.67) * mm, "end": v(-3614.54, 1268.83) * mm});
            skLineSegment(sketch, "E2951", {"start": v(-3612.98, 1257) * mm, "end": v(-3608.41, 1245.98) * mm});
            skLineSegment(sketch, "E2952", {"start": v(-5484.62, 1687) * mm, "end": v(-5493.8, 1683.19) * mm});
            skLineSegment(sketch, "E2953", {"start": v(-5493.8, 1683.19) * mm, "end": v(-5501.7, 1677.13) * mm});
            skLineSegment(sketch, "E2954", {"start": v(-5602.63, 1357.7) * mm, "end": v(-5601.76, 1370.97) * mm});
            skLineSegment(sketch, "E2955", {"start": v(-5511.56, 1640.33) * mm, "end": v(-5507.76, 1631.14) * mm});
            skLineSegment(sketch, "E2956", {"start": v(-6001.8, 1683.19) * mm, "end": v(-6009.7, 1677.13) * mm});
            skLineSegment(sketch, "E2957", {"start": v(-5605.22, 1344.67) * mm, "end": v(-5602.63, 1357.7) * mm});
            skLineSegment(sketch, "E2958", {"start": v(-5944.66, 1650.2) * mm, "end": v(-5945.96, 1660.05) * mm});
            skLineSegment(sketch, "E2959", {"start": v(-5945.96, 1660.05) * mm, "end": v(-5949.76, 1669.24) * mm});
            skLineSegment(sketch, "E2960", {"start": v(-5464.9, 1687) * mm, "end": v(-5474.76, 1688.3) * mm});
            skLineSegment(sketch, "E2961", {"start": v(-6009.7, 1677.13) * mm, "end": v(-6015.76, 1669.24) * mm});
            skLineSegment(sketch, "E2962", {"start": v(-5992.62, 1687) * mm, "end": v(-6001.8, 1683.19) * mm});
            skLineSegment(sketch, "E2963", {"start": v(-5447.82, 1677.13) * mm, "end": v(-5455.7, 1683.19) * mm});
            skLineSegment(sketch, "E2964", {"start": v(-6001.8, 1617.2) * mm, "end": v(-5992.62, 1613.39) * mm});
            skLineSegment(sketch, "E2965", {"start": v(-5690.1, 1270.24) * mm, "end": v(-5677.06, 1272.83) * mm});
            skLineSegment(sketch, "E2966", {"start": v(-5507.76, 1631.14) * mm, "end": v(-5501.7, 1623.25) * mm});
            skLineSegment(sketch, "E2967", {"start": v(-5464.9, 1613.39) * mm, "end": v(-5455.7, 1617.2) * mm});
            skLineSegment(sketch, "E2968", {"start": v(-5652.56, 1282.98) * mm, "end": v(-5641.5, 1290.37) * mm});
            skLineSegment(sketch, "E2969", {"start": v(-5641.5, 1290.37) * mm, "end": v(-5631.52, 1299.13) * mm});
            skLineSegment(sketch, "E2970", {"start": v(-5631.52, 1299.13) * mm, "end": v(-5622.75, 1309.12) * mm});
            skLineSegment(sketch, "E2971", {"start": v(-5474.76, 1688.3) * mm, "end": v(-5484.62, 1687) * mm});
            skLineSegment(sketch, "E2972", {"start": v(-5609.5, 1332.09) * mm, "end": v(-5605.22, 1344.67) * mm});
            skLineSegment(sketch, "E2973", {"start": v(-5622.75, 1309.12) * mm, "end": v(-5615.37, 1320.17) * mm});
            skLineSegment(sketch, "E2974", {"start": v(-5615.37, 1320.17) * mm, "end": v(-5609.5, 1332.09) * mm});
            skLineSegment(sketch, "E2975", {"start": v(-5474.76, 1612.1) * mm, "end": v(-5464.9, 1613.39) * mm});
            skLineSegment(sketch, "E2976", {"start": v(-5804.96, 2043.16) * mm, "end": v(-5816, 2035.77) * mm});
            skLineSegment(sketch, "E2977", {"start": v(-5816, 2035.77) * mm, "end": v(-5826, 2027.01) * mm});
            skLineSegment(sketch, "E2978", {"start": v(-5826, 2027.01) * mm, "end": v(-5834.76, 2017.02) * mm});
            skLineSegment(sketch, "E2979", {"start": v(-5834.76, 2017.02) * mm, "end": v(-5842.15, 2005.97) * mm});
            skLineSegment(sketch, "E2980", {"start": v(-5842.15, 2005.97) * mm, "end": v(-5848.03, 1994.05) * mm});
            skLineSegment(sketch, "E2981", {"start": v(-5848.03, 1994.05) * mm, "end": v(-5852.3, 1981.47) * mm});
            skLineSegment(sketch, "E2982", {"start": v(-5852.3, 1981.47) * mm, "end": v(-5854.9, 1968.43) * mm});
            skLineSegment(sketch, "E2983", {"start": v(-5854.9, 1968.43) * mm, "end": v(-5855.76, 1955.17) * mm});
            skLineSegment(sketch, "E2984", {"start": v(-5602.63, 1968.43) * mm, "end": v(-5605.22, 1981.47) * mm});
            skLineSegment(sketch, "E2985", {"start": v(-5605.22, 1981.47) * mm, "end": v(-5609.5, 1994.05) * mm});
            skLineSegment(sketch, "E2986", {"start": v(-5609.5, 1994.05) * mm, "end": v(-5615.37, 2005.97) * mm});
            skLineSegment(sketch, "E2987", {"start": v(-5622.75, 2017.02) * mm, "end": v(-5631.52, 2027.01) * mm});
            skLineSegment(sketch, "E2988", {"start": v(-5793.04, 1277.1) * mm, "end": v(-5780.46, 1272.83) * mm});
            skLineSegment(sketch, "E2989", {"start": v(-5780.46, 1272.83) * mm, "end": v(-5767.42, 1270.24) * mm});
            skLineSegment(sketch, "E2990", {"start": v(-5767.42, 1270.24) * mm, "end": v(-5754.16, 1269.37) * mm});
            skLineSegment(sketch, "E2991", {"start": v(-5601.76, 1955.17) * mm, "end": v(-5602.63, 1968.43) * mm});
            skLineSegment(sketch, "E2992", {"start": v(-5767.42, 2055.9) * mm, "end": v(-5780.46, 2053.3) * mm});
            skLineSegment(sketch, "E2993", {"start": v(-5955.82, 1623.25) * mm, "end": v(-5949.76, 1631.14) * mm});
            skLineSegment(sketch, "E2994", {"start": v(-6019.56, 1660.05) * mm, "end": v(-6020.86, 1650.2) * mm});
            skLineSegment(sketch, "E2995", {"start": v(-6015.76, 1631.14) * mm, "end": v(-6009.7, 1623.25) * mm});
            skLineSegment(sketch, "E2996", {"start": v(-5436.66, 1650.2) * mm, "end": v(-5437.96, 1660.05) * mm});
            skLineSegment(sketch, "E2997", {"start": v(-5949.76, 1631.14) * mm, "end": v(-5945.96, 1640.33) * mm});
            skLineSegment(sketch, "E2998", {"start": v(-5854.9, 1357.7) * mm, "end": v(-5852.3, 1344.67) * mm});
            skLineSegment(sketch, "E2999", {"start": v(-5963.7, 1683.19) * mm, "end": v(-5972.9, 1687) * mm});
            skLineSegment(sketch, "E3000", {"start": v(-5955.82, 1677.13) * mm, "end": v(-5963.7, 1683.19) * mm});
            skLineSegment(sketch, "E3001", {"start": v(-6009.7, 1623.25) * mm, "end": v(-6001.8, 1617.2) * mm});
            skLineSegment(sketch, "E3002", {"start": v(-6015.76, 1669.24) * mm, "end": v(-6019.56, 1660.05) * mm});
            skLineSegment(sketch, "E3003", {"start": v(-5677.06, 1272.83) * mm, "end": v(-5664.48, 1277.1) * mm});
            skLineSegment(sketch, "E3004", {"start": v(-5754.16, 2056.77) * mm, "end": v(-5703.36, 2056.77) * mm});
            skLineSegment(sketch, "E3005", {"start": v(-5945.96, 1640.33) * mm, "end": v(-5944.66, 1650.2) * mm});
            skLineSegment(sketch, "E3006", {"start": v(-5652.56, 2043.16) * mm, "end": v(-5664.48, 2049.04) * mm});
            skLineSegment(sketch, "E3007", {"start": v(-5703.36, 1269.37) * mm, "end": v(-5690.1, 1270.24) * mm});
            skLineSegment(sketch, "E3008", {"start": v(-5793.04, 2049.04) * mm, "end": v(-5804.96, 2043.16) * mm});
            skLineSegment(sketch, "E3009", {"start": v(-5793.04, -501.07) * mm, "end": v(-5780.46, -505.35) * mm});
            skLineSegment(sketch, "E3010", {"start": v(-5804.96, -495.2) * mm, "end": v(-5793.04, -501.07) * mm});
            skLineSegment(sketch, "E3011", {"start": v(-5816, -487.81) * mm, "end": v(-5804.96, -495.2) * mm});
            skLineSegment(sketch, "E3012", {"start": v(-5826, -479.05) * mm, "end": v(-5816, -487.81) * mm});
            skLineSegment(sketch, "E3013", {"start": v(-5703.36, -508.8) * mm, "end": v(-5754.16, -508.8) * mm});
            skLineSegment(sketch, "E3014", {"start": v(-6019.56, -117.95) * mm, "end": v(-6020.86, -127.8) * mm});
            skLineSegment(sketch, "E3015", {"start": v(-6015.76, -108.76) * mm, "end": v(-6019.56, -117.95) * mm});
            skLineSegment(sketch, "E3016", {"start": v(-5605.22, 203.29) * mm, "end": v(-5609.5, 215.87) * mm});
            skLineSegment(sketch, "E3017", {"start": v(-5602.63, 190.25) * mm, "end": v(-5605.22, 203.29) * mm});
            skLineSegment(sketch, "E3018", {"start": v(-5601.76, 177) * mm, "end": v(-5602.63, 190.25) * mm});
            skLineSegment(sketch, "E3019", {"start": v(-5437.96, -137.67) * mm, "end": v(-5436.66, -127.8) * mm});
            skLineSegment(sketch, "E3020", {"start": v(-6009.7, -100.87) * mm, "end": v(-6015.76, -108.76) * mm});
            skLineSegment(sketch, "E3021", {"start": v(-6001.8, -94.81) * mm, "end": v(-6009.7, -100.87) * mm});
            skLineSegment(sketch, "E3022", {"start": v(-5690.1, -507.94) * mm, "end": v(-5677.06, -505.35) * mm});
            skLineSegment(sketch, "E3023", {"start": v(-5474.76, -89.7) * mm, "end": v(-5484.62, -91) * mm});
            skLineSegment(sketch, "E3024", {"start": v(-5848.03, -446.09) * mm, "end": v(-5842.15, -458) * mm});
            skLineSegment(sketch, "E3025", {"start": v(-5842.15, -458) * mm, "end": v(-5834.76, -469.06) * mm});
            skLineSegment(sketch, "E3026", {"start": v(-5834.76, -469.06) * mm, "end": v(-5826, -479.05) * mm});
            skLineSegment(sketch, "E3027", {"start": v(-5441.76, -108.76) * mm, "end": v(-5447.82, -100.87) * mm});
            skLineSegment(sketch, "E3028", {"start": v(-5949.76, -108.76) * mm, "end": v(-5955.82, -100.87) * mm});
            skLineSegment(sketch, "E3029", {"start": v(-5501.7, -100.87) * mm, "end": v(-5507.76, -108.76) * mm});
            skLineSegment(sketch, "E3030", {"start": v(-6015.76, -146.86) * mm, "end": v(-6009.7, -154.75) * mm});
            skLineSegment(sketch, "E3031", {"start": v(-5601.76, 177) * mm, "end": v(-5601.76, -407.2) * mm});
            skLineSegment(sketch, "E3032", {"start": v(-5972.9, -164.61) * mm, "end": v(-5963.7, -160.8) * mm});
            skLineSegment(sketch, "E3033", {"start": v(-5945.96, -117.95) * mm, "end": v(-5949.76, -108.76) * mm});
            skLineSegment(sketch, "E3034", {"start": v(-5507.76, -146.86) * mm, "end": v(-5501.7, -154.75) * mm});
            skLineSegment(sketch, "E3035", {"start": v(-5455.7, -94.81) * mm, "end": v(-5464.9, -91) * mm});
            skLineSegment(sketch, "E3036", {"start": v(-5842.15, 227.8) * mm, "end": v(-5848.03, 215.87) * mm});
            skLineSegment(sketch, "E3037", {"start": v(-6019.56, -137.67) * mm, "end": v(-6015.76, -146.86) * mm});
            skLineSegment(sketch, "E3038", {"start": v(-6256.65, 3383.43) * mm, "end": v(-6247.18, 3376.16) * mm});
            skLineSegment(sketch, "E3039", {"start": v(-6192, 3383.43) * mm, "end": v(-6184.73, 3392.9) * mm});
            skLineSegment(sketch, "E3040", {"start": v(-6236.16, 3459.92) * mm, "end": v(-6247.18, 3455.35) * mm});
            skLineSegment(sketch, "E3041", {"start": v(-6224.32, 3461.47) * mm, "end": v(-6234.97, 3459.94) * mm});
            skLineSegment(sketch, "E3042", {"start": v(-6212.5, 3459.92) * mm, "end": v(-6224.32, 3461.47) * mm});
            skLineSegment(sketch, "E3043", {"start": v(-6201.46, 3455.35) * mm, "end": v(-6212.5, 3459.92) * mm});
            skLineSegment(sketch, "E3044", {"start": v(-6192, 3448.08) * mm, "end": v(-6201.46, 3455.35) * mm});
            skLineSegment(sketch, "E3045", {"start": v(-6184.73, 3438.61) * mm, "end": v(-6192, 3448.08) * mm});
            skLineSegment(sketch, "E3046", {"start": v(-6180.16, 3427.59) * mm, "end": v(-6184.73, 3438.61) * mm});
            skLineSegment(sketch, "E3047", {"start": v(-6178.6, 3415.75) * mm, "end": v(-6180.16, 3427.59) * mm});
            skLineSegment(sketch, "E3048", {"start": v(-6180.16, 3403.92) * mm, "end": v(-6178.6, 3415.75) * mm});
            skLineSegment(sketch, "E3049", {"start": v(-6184.73, 3392.9) * mm, "end": v(-6180.16, 3403.92) * mm});
            skLineSegment(sketch, "E3050", {"start": v(-6266.02, 3433.55) * mm, "end": v(-6268.49, 3427.59) * mm});
            skLineSegment(sketch, "E3051", {"start": v(-6224.32, 3370.03) * mm, "end": v(-6212.5, 3371.6) * mm});
            skLineSegment(sketch, "E3052", {"start": v(-6212.5, 3371.6) * mm, "end": v(-6201.46, 3376.16) * mm});
            skLineSegment(sketch, "E3053", {"start": v(-6236.16, 3371.6) * mm, "end": v(-6224.32, 3370.03) * mm});
            skLineSegment(sketch, "E3054", {"start": v(-6201.46, 3376.16) * mm, "end": v(-6192, 3383.43) * mm});
            skLineSegment(sketch, "E3055", {"start": v(-6247.18, 3455.35) * mm, "end": v(-6256.65, 3448.08) * mm});
            skLineSegment(sketch, "E3056", {"start": v(-6263.92, 3438.61) * mm, "end": v(-6266.02, 3433.55) * mm});
            skLineSegment(sketch, "E3057", {"start": v(-6256.65, 3448.08) * mm, "end": v(-6263.92, 3438.61) * mm});
            skLineSegment(sketch, "E3058", {"start": v(-6270.04, 3415.75) * mm, "end": v(-6268.49, 3403.92) * mm});
            skLineSegment(sketch, "E3059", {"start": v(-6268.49, 3427.59) * mm, "end": v(-6270.04, 3415.75) * mm});
            skLineSegment(sketch, "E3060", {"start": v(-938.06, 3376.16) * mm, "end": v(-927.03, 3371.6) * mm});
            skLineSegment(sketch, "E3061", {"start": v(-875.6, 3392.9) * mm, "end": v(-871.03, 3403.92) * mm});
            skLineSegment(sketch, "E3062", {"start": v(-915.2, 3370.03) * mm, "end": v(-903.36, 3371.6) * mm});
            skLineSegment(sketch, "E3063", {"start": v(-882.87, 3448.08) * mm, "end": v(-892.34, 3455.35) * mm});
            skLineSegment(sketch, "E3064", {"start": v(-960.92, 3415.75) * mm, "end": v(-959.36, 3403.92) * mm});
            skLineSegment(sketch, "E3065", {"start": v(-954.8, 3392.9) * mm, "end": v(-947.53, 3383.43) * mm});
            skLineSegment(sketch, "E3066", {"start": v(-959.36, 3427.59) * mm, "end": v(-960.92, 3415.75) * mm});
            skLineSegment(sketch, "E3067", {"start": v(-915.2, 3461.47) * mm, "end": v(-927.03, 3459.92) * mm});
            skLineSegment(sketch, "E3068", {"start": v(-892.34, 3376.16) * mm, "end": v(-882.87, 3383.43) * mm});
            skLineSegment(sketch, "E3069", {"start": v(-947.53, 3448.08) * mm, "end": v(-954.8, 3438.61) * mm});
            skLineSegment(sketch, "E3070", {"start": v(-927.03, 3459.92) * mm, "end": v(-938.06, 3455.35) * mm});
            skLineSegment(sketch, "E3071", {"start": v(-947.53, 3383.43) * mm, "end": v(-938.06, 3376.16) * mm});
            skLineSegment(sketch, "E3072", {"start": v(-938.06, 3455.35) * mm, "end": v(-947.53, 3448.08) * mm});
            skLineSegment(sketch, "E3073", {"start": v(-903.36, 3371.6) * mm, "end": v(-892.34, 3376.16) * mm});
            skLineSegment(sketch, "E3074", {"start": v(-892.34, -1932.97) * mm, "end": v(-882.87, -1925.7) * mm});
            skLineSegment(sketch, "E3075", {"start": v(-915.2, -1939.1) * mm, "end": v(-903.36, -1937.53) * mm});
            skLineSegment(sketch, "E3076", {"start": v(-927.03, -1937.53) * mm, "end": v(-915.2, -1939.1) * mm});
            skLineSegment(sketch, "E3077", {"start": v(-938.06, -1932.97) * mm, "end": v(-927.03, -1937.53) * mm});
            skLineSegment(sketch, "E3078", {"start": v(-959.36, -1905.2) * mm, "end": v(-954.8, -1916.23) * mm});
            skLineSegment(sketch, "E3079", {"start": v(-960.92, -1893.37) * mm, "end": v(-959.36, -1905.2) * mm});
            skLineSegment(sketch, "E3080", {"start": v(-959.36, -1881.54) * mm, "end": v(-960.92, -1893.37) * mm});
            skLineSegment(sketch, "E3081", {"start": v(-954.8, -1870.51) * mm, "end": v(-959.36, -1881.54) * mm});
            skLineSegment(sketch, "E3082", {"start": v(-947.53, -1861.04) * mm, "end": v(-954.8, -1870.51) * mm});
            skLineSegment(sketch, "E3083", {"start": v(-927.03, -1849.21) * mm, "end": v(-938.06, -1853.78) * mm});
            skLineSegment(sketch, "E3084", {"start": v(-938.06, -1853.78) * mm, "end": v(-947.53, -1861.04) * mm});
            skLineSegment(sketch, "E3085", {"start": v(-892.34, -1853.78) * mm, "end": v(-903.36, -1849.21) * mm});
            skLineSegment(sketch, "E3086", {"start": v(-882.87, -1861.04) * mm, "end": v(-892.34, -1853.78) * mm});
            skLineSegment(sketch, "E3087", {"start": v(-875.6, -1870.51) * mm, "end": v(-882.87, -1861.04) * mm});
            skLineSegment(sketch, "E3088", {"start": v(-871.03, -1881.54) * mm, "end": v(-875.6, -1870.51) * mm});
            skLineSegment(sketch, "E3089", {"start": v(-869.48, -1893.37) * mm, "end": v(-871.03, -1881.54) * mm});
            skLineSegment(sketch, "E3090", {"start": v(-915.2, -1847.65) * mm, "end": v(-927.03, -1849.21) * mm});
            skLineSegment(sketch, "E3091", {"start": v(-903.36, -1849.21) * mm, "end": v(-915.2, -1847.65) * mm});
            skLineSegment(sketch, "E3092", {"start": v(-871.03, -1905.2) * mm, "end": v(-869.48, -1893.37) * mm});
            skLineSegment(sketch, "E3093", {"start": v(-875.6, -1916.23) * mm, "end": v(-871.03, -1905.2) * mm});
            skLineSegment(sketch, "E3094", {"start": v(-882.87, -1925.7) * mm, "end": v(-875.6, -1916.23) * mm});
            skLineSegment(sketch, "E3095", {"start": v(-6270.04, -1892.33) * mm, "end": v(-6268.62, -1904.18) * mm});
            skLineSegment(sketch, "E3096", {"start": v(-6257.01, -1924.81) * mm, "end": v(-6247.62, -1932.18) * mm});
            skLineSegment(sketch, "E3097", {"start": v(-6184.48, -1870.43) * mm, "end": v(-6191.63, -1860.88) * mm});
            skLineSegment(sketch, "E3098", {"start": v(-6178.6, -1893.36) * mm, "end": v(-6180.03, -1881.5) * mm});
            skLineSegment(sketch, "E3099", {"start": v(-6184.99, -1916.15) * mm, "end": v(-6180.3, -1905.17) * mm});
            skLineSegment(sketch, "E3100", {"start": v(-6268.35, -1880.52) * mm, "end": v(-6270.04, -1892.33) * mm});
            skLineSegment(sketch, "E3101", {"start": v(-6212.98, -1937.14) * mm, "end": v(-6201.9, -1932.7) * mm});
            skLineSegment(sketch, "E3102", {"start": v(-6268.62, -1904.18) * mm, "end": v(-6264.17, -1915.26) * mm});
            skLineSegment(sketch, "E3103", {"start": v(-6246.74, -1853) * mm, "end": v(-6256.29, -1860.16) * mm});
            skLineSegment(sketch, "E3104", {"start": v(-6192.36, -1925.53) * mm, "end": v(-6184.99, -1916.15) * mm});
            skLineSegment(sketch, "E3105", {"start": v(-6264.17, -1915.26) * mm, "end": v(-6257.01, -1924.81) * mm});
            skLineSegment(sketch, "E3106", {"start": v(-6235.66, -1848.55) * mm, "end": v(-6246.74, -1853) * mm});
            skLineSegment(sketch, "E3107", {"start": v(-6223.81, -1847.13) * mm, "end": v(-6235.66, -1848.55) * mm});
            skLineSegment(sketch, "E3108", {"start": v(-6247.62, -1932.18) * mm, "end": v(-6236.65, -1936.87) * mm});
            skLineSegment(sketch, "E3109", {"start": v(-6212, -1848.82) * mm, "end": v(-6223.81, -1847.13) * mm});
            skLineSegment(sketch, "E3110", {"start": v(-6201.02, -1853.5) * mm, "end": v(-6212, -1848.82) * mm});
            skLineSegment(sketch, "E3111", {"start": v(-6191.63, -1860.88) * mm, "end": v(-6201.02, -1853.5) * mm});
            skLineSegment(sketch, "E3112", {"start": v(-6224.83, -1938.56) * mm, "end": v(-6212.98, -1937.14) * mm});
            skLineSegment(sketch, "E3113", {"start": v(-6236.65, -1936.87) * mm, "end": v(-6224.83, -1938.56) * mm});
            skLineSegment(sketch, "E3114", {"start": v(-6201.9, -1932.7) * mm, "end": v(-6192.36, -1925.53) * mm});
            skLineSegment(sketch, "E3115", {"start": v(-6263.66, -1869.54) * mm, "end": v(-6268.35, -1880.52) * mm});
            skLineSegment(sketch, "E3116", {"start": v(-4865.42, 4166.26) * mm, "end": v(-4749.4, 4137.9) * mm});
            skLineSegment(sketch, "E3117", {"start": v(-4749.4, 4137.9) * mm, "end": v(-4717.18, 4118.56) * mm});
            skLineSegment(sketch, "E3118", {"start": v(-4717.18, 4118.56) * mm, "end": v(-4708.15, 4092.78) * mm});
            skLineSegment(sketch, "E3119", {"start": v(-4708.15, 4092.78) * mm, "end": v(-4709.44, 4063.14) * mm});
            skLineSegment(sketch, "E3120", {"start": v(-4709.44, 4063.14) * mm, "end": v(-4730.07, 4036.07) * mm});
            skLineSegment(sketch, "E3121", {"start": v(-4730.07, 4036.07) * mm, "end": v(-4761, 4018.02) * mm});
            skLineSegment(sketch, "E3122", {"start": v(-4761, 4018.02) * mm, "end": v(-4802.26, 4014.15) * mm});
            skLineSegment(sketch, "E3123", {"start": v(-4802.26, 4014.15) * mm, "end": v(-4851.24, 4023.17) * mm});
            skLineSegment(sketch, "E3124", {"start": v(-4851.24, 4023.17) * mm, "end": v(-4888.62, 4046.38) * mm});
            skLineSegment(sketch, "E3125", {"start": v(-4888.62, 4046.38) * mm, "end": v(-4911.82, 4086.34) * mm});
            skLineSegment(sketch, "E3126", {"start": v(-4911.82, 4086.34) * mm, "end": v(-4916.98, 4108.25) * mm});
            skLineSegment(sketch, "E3127", {"start": v(-4916.98, 4108.25) * mm, "end": v(-5016.24, 4099.23) * mm});
            skLineSegment(sketch, "E3128", {"start": v(-5706.65, 4428.95) * mm, "end": v(-5729.51, 4436.57) * mm});
            skLineSegment(sketch, "E3129", {"start": v(-5729.51, 4436.57) * mm, "end": v(-5767.61, 4441.65) * mm});
            skLineSegment(sketch, "E3130", {"start": v(-5767.61, 4441.65) * mm, "end": v(-5803.17, 4444.2) * mm});
            skLineSegment(sketch, "E3131", {"start": v(-5803.17, 4444.2) * mm, "end": v(-6016.53, 4444.2) * mm});
            skLineSegment(sketch, "E3132", {"start": v(-6016.53, 4444.2) * mm, "end": v(-6016.53, 3936.2) * mm});
            skLineSegment(sketch, "E3133", {"start": v(-6016.53, 3936.2) * mm, "end": v(-5914.93, 3936.2) * mm});
            skLineSegment(sketch, "E3134", {"start": v(-5914.93, 3936.2) * mm, "end": v(-5914.93, 4357.83) * mm});
            skLineSegment(sketch, "E3135", {"start": v(-5914.93, 4357.83) * mm, "end": v(-5805.71, 4357.83) * mm});
            skLineSegment(sketch, "E3136", {"start": v(-5805.71, 4357.83) * mm, "end": v(-5780.31, 4352.75) * mm});
            skLineSegment(sketch, "E3137", {"start": v(-5780.31, 4352.75) * mm, "end": v(-5760, 4342.6) * mm});
            skLineSegment(sketch, "E3138", {"start": v(-5760, 4342.6) * mm, "end": v(-5744.75, 4327.35) * mm});
            skLineSegment(sketch, "E3139", {"start": v(-5744.75, 4327.35) * mm, "end": v(-5737.13, 4312.11) * mm});
            skLineSegment(sketch, "E3140", {"start": v(-5682.89, 3936.29) * mm, "end": v(-5816.03, 4129.23) * mm});
            skLineSegment(sketch, "E3141", {"start": v(-5201.1, 4140.63) * mm, "end": v(-5204.22, 4097.12) * mm});
            skLineSegment(sketch, "E3142", {"start": v(-5204.22, 4097.12) * mm, "end": v(-5213.54, 4052.98) * mm});
            skLineSegment(sketch, "E3143", {"start": v(-5213.54, 4052.98) * mm, "end": v(-5236.54, 4030.6) * mm});
            skLineSegment(sketch, "E3144", {"start": v(-5236.54, 4030.6) * mm, "end": v(-5267, 4017.55) * mm});
            skLineSegment(sketch, "E3145", {"start": v(-5267, 4017.55) * mm, "end": v(-5303.68, 4015.06) * mm});
            skLineSegment(sketch, "E3146", {"start": v(-5303.68, 4015.06) * mm, "end": v(-5341.6, 4021.28) * mm});
            skLineSegment(sketch, "E3147", {"start": v(-5341.6, 4021.28) * mm, "end": v(-5372.68, 4039.93) * mm});
            skLineSegment(sketch, "E3148", {"start": v(-5372.68, 4039.93) * mm, "end": v(-5393.2, 4071) * mm});
            skLineSegment(sketch, "E3149", {"start": v(-5393.2, 4071) * mm, "end": v(-5401.28, 4119.5) * mm});
            skLineSegment(sketch, "E3150", {"start": v(-5401.28, 4119.5) * mm, "end": v(-5400.66, 4321.53) * mm});
            skLineSegment(sketch, "E3151", {"start": v(-5400.66, 4321.53) * mm, "end": v(-5400.66, 4444) * mm});
            skLineSegment(sketch, "E3152", {"start": v(-5400.66, 4444) * mm, "end": v(-5503.45, 4444.2) * mm});
            skLineSegment(sketch, "E3153", {"start": v(-4570.23, 3935.52) * mm, "end": v(-4370.42, 4442.12) * mm});
            skLineSegment(sketch, "E3154", {"start": v(-4740.38, 4238.45) * mm, "end": v(-4830.61, 4261.65) * mm});
            skLineSegment(sketch, "E3155", {"start": v(-4830.61, 4261.65) * mm, "end": v(-4889.91, 4287.43) * mm});
            skLineSegment(sketch, "E3156", {"start": v(-4889.91, 4287.43) * mm, "end": v(-4897.64, 4310.63) * mm});
            skLineSegment(sketch, "E3157", {"start": v(-4897.64, 4310.63) * mm, "end": v(-4897.5, 4329.97) * mm});
            skLineSegment(sketch, "E3158", {"start": v(-4897.5, 4329.97) * mm, "end": v(-4885.57, 4347.87) * mm});
            skLineSegment(sketch, "E3159", {"start": v(-4885.57, 4347.87) * mm, "end": v(-4863.94, 4360.55) * mm});
            skLineSegment(sketch, "E3160", {"start": v(-4863.94, 4360.55) * mm, "end": v(-4837.83, 4367.27) * mm});
            skLineSegment(sketch, "E3161", {"start": v(-4837.83, 4367.27) * mm, "end": v(-4802.77, 4368.76) * mm});
            skLineSegment(sketch, "E3162", {"start": v(-4802.77, 4368.76) * mm, "end": v(-4769.95, 4363.54) * mm});
            skLineSegment(sketch, "E3163", {"start": v(-4769.95, 4363.54) * mm, "end": v(-4740.85, 4347.13) * mm});
            skLineSegment(sketch, "E3164", {"start": v(-4740.85, 4347.13) * mm, "end": v(-4727.42, 4325.5) * mm});
            skLineSegment(sketch, "E3165", {"start": v(-4727.42, 4325.5) * mm, "end": v(-4719.97, 4292.67) * mm});
            skLineSegment(sketch, "E3166", {"start": v(-4719.97, 4292.67) * mm, "end": v(-4616.63, 4299.03) * mm});
            skLineSegment(sketch, "E3167", {"start": v(-4655.3, 4399.58) * mm, "end": v(-4695.26, 4427.94) * mm});
            skLineSegment(sketch, "E3168", {"start": v(-4695.26, 4427.94) * mm, "end": v(-4746.83, 4447.27) * mm});
            skLineSegment(sketch, "E3169", {"start": v(-4746.83, 4447.27) * mm, "end": v(-4800.97, 4451.14) * mm});
            skLineSegment(sketch, "E3170", {"start": v(-4800.97, 4451.14) * mm, "end": v(-4843.5, 4451.14) * mm});
            skLineSegment(sketch, "E3171", {"start": v(-4843.5, 4451.14) * mm, "end": v(-4910.54, 4435.67) * mm});
            skLineSegment(sketch, "E3172", {"start": v(-4910.54, 4435.67) * mm, "end": v(-4958.23, 4406.02) * mm});
            skLineSegment(sketch, "E3173", {"start": v(-4958.23, 4406.02) * mm, "end": v(-4989.17, 4359.62) * mm});
            skLineSegment(sketch, "E3174", {"start": v(-4989.17, 4359.62) * mm, "end": v(-4999.48, 4326.1) * mm});
            skLineSegment(sketch, "E3175", {"start": v(-4999.48, 4326.1) * mm, "end": v(-4994.32, 4275.83) * mm});
            skLineSegment(sketch, "E3176", {"start": v(-4994.32, 4275.83) * mm, "end": v(-4973.7, 4230.71) * mm});
            skLineSegment(sketch, "E3177", {"start": v(-4973.7, 4230.71) * mm, "end": v(-4937.6, 4198.49) * mm});
            skLineSegment(sketch, "E3178", {"start": v(-4937.6, 4198.49) * mm, "end": v(-4865.42, 4166.26) * mm});
            skLineSegment(sketch, "E3179", {"start": v(-5418.68, 3951.29) * mm, "end": v(-5374.55, 3935.12) * mm});
            skLineSegment(sketch, "E3180", {"start": v(-5374.55, 3935.12) * mm, "end": v(-5308.03, 3926.42) * mm});
            skLineSegment(sketch, "E3181", {"start": v(-5308.03, 3926.42) * mm, "end": v(-5241.52, 3931.4) * mm});
            skLineSegment(sketch, "E3182", {"start": v(-5241.52, 3931.4) * mm, "end": v(-5188.05, 3948.18) * mm});
            skLineSegment(sketch, "E3183", {"start": v(-5188.05, 3948.18) * mm, "end": v(-5154.48, 3969.94) * mm});
            skLineSegment(sketch, "E3184", {"start": v(-5154.48, 3969.94) * mm, "end": v(-5125.27, 3998.53) * mm});
            skLineSegment(sketch, "E3185", {"start": v(-5125.27, 3998.53) * mm, "end": v(-5106.62, 4050.5) * mm});
            skLineSegment(sketch, "E3186", {"start": v(-5106.62, 4050.5) * mm, "end": v(-5097.91, 4120.74) * mm});
            skLineSegment(sketch, "E3187", {"start": v(-5097.91, 4120.74) * mm, "end": v(-5097.91, 4220.2) * mm});
            skLineSegment(sketch, "E3188", {"start": v(-5097.91, 4220.2) * mm, "end": v(-5098.54, 4444) * mm});
            skLineSegment(sketch, "E3189", {"start": v(-5098.54, 4444) * mm, "end": v(-5201.73, 4444) * mm});
            skLineSegment(sketch, "E3190", {"start": v(-5201.73, 4444) * mm, "end": v(-5201.1, 4140.63) * mm});
            skLineSegment(sketch, "E3191", {"start": v(-6252.75, 4352.75) * mm, "end": v(-6232.43, 4342.6) * mm});
            skLineSegment(sketch, "E3192", {"start": v(-6232.43, 4342.6) * mm, "end": v(-6217.2, 4327.35) * mm});
            skLineSegment(sketch, "E3193", {"start": v(-6217.2, 4327.35) * mm, "end": v(-6209.57, 4312.11) * mm});
            skLineSegment(sketch, "E3194", {"start": v(-6209.57, 4312.11) * mm, "end": v(-6204.5, 4291.8) * mm});
            skLineSegment(sketch, "E3195", {"start": v(-6204.5, 4291.8) * mm, "end": v(-6207.03, 4268.93) * mm});
            skLineSegment(sketch, "E3196", {"start": v(-6207.03, 4268.93) * mm, "end": v(-6217.2, 4248.61) * mm});
            skLineSegment(sketch, "E3197", {"start": v(-6217.2, 4248.61) * mm, "end": v(-6229.9, 4233.37) * mm});
            skLineSegment(sketch, "E3198", {"start": v(-6229.9, 4233.37) * mm, "end": v(-6252.75, 4220.67) * mm});
            skLineSegment(sketch, "E3199", {"start": v(-6252.75, 4220.67) * mm, "end": v(-6275.61, 4215.6) * mm});
            skLineSegment(sketch, "E3200", {"start": v(-6275.61, 4215.6) * mm, "end": v(-6308.63, 4215.6) * mm});
            skLineSegment(sketch, "E3201", {"start": v(-6308.63, 4215.6) * mm, "end": v(-6349.27, 4215.6) * mm});
            skLineSegment(sketch, "E3202", {"start": v(-6146.07, 4406.1) * mm, "end": v(-6179.1, 4428.95) * mm});
            skLineSegment(sketch, "E3203", {"start": v(-6179.1, 4428.95) * mm, "end": v(-6201.95, 4436.57) * mm});
            skLineSegment(sketch, "E3204", {"start": v(-6201.95, 4436.57) * mm, "end": v(-6240.05, 4441.65) * mm});
            skLineSegment(sketch, "E3205", {"start": v(-6240.05, 4441.65) * mm, "end": v(-6275.61, 4444.2) * mm});
            skLineSegment(sketch, "E3206", {"start": v(-6275.61, 4444.2) * mm, "end": v(-6488.97, 4444.2) * mm});
            skLineSegment(sketch, "E3207", {"start": v(-5737.13, 4312.11) * mm, "end": v(-5732.05, 4291.8) * mm});
            skLineSegment(sketch, "E3208", {"start": v(-5732.05, 4291.8) * mm, "end": v(-5734.6, 4268.93) * mm});
            skLineSegment(sketch, "E3209", {"start": v(-5734.6, 4268.93) * mm, "end": v(-5744.75, 4248.61) * mm});
            skLineSegment(sketch, "E3210", {"start": v(-5744.75, 4248.61) * mm, "end": v(-5757.45, 4233.37) * mm});
            skLineSegment(sketch, "E3211", {"start": v(-5757.45, 4233.37) * mm, "end": v(-5780.31, 4220.67) * mm});
            skLineSegment(sketch, "E3212", {"start": v(-5780.31, 4220.67) * mm, "end": v(-5803.17, 4215.6) * mm});
            skLineSegment(sketch, "E3213", {"start": v(-5803.17, 4215.6) * mm, "end": v(-5836.2, 4215.6) * mm});
            skLineSegment(sketch, "E3214", {"start": v(-4370.42, 4442.12) * mm, "end": v(-4262.14, 4442.12) * mm});
            skLineSegment(sketch, "E3215", {"start": v(-4262.14, 4442.12) * mm, "end": v(-4061.05, 3936.8) * mm});
            skLineSegment(sketch, "E3216", {"start": v(-4061.05, 3936.8) * mm, "end": v(-4170.62, 3938.1) * mm});
            skLineSegment(sketch, "E3217", {"start": v(-4570.23, 3935.52) * mm, "end": v(-4459.37, 3935.52) * mm});
            skLineSegment(sketch, "E3218", {"start": v(-4459.37, 3935.52) * mm, "end": v(-4318.86, 4323.52) * mm});
            skLineSegment(sketch, "E3219", {"start": v(-4318.86, 4323.52) * mm, "end": v(-4247.96, 4137.9) * mm});
            skLineSegment(sketch, "E3220", {"start": v(-4247.96, 4137.9) * mm, "end": v(-4358.82, 4136.61) * mm});
            skLineSegment(sketch, "E3221", {"start": v(-4358.82, 4136.61) * mm, "end": v(-4388.47, 4052.82) * mm});
            skLineSegment(sketch, "E3222", {"start": v(-4388.47, 4052.82) * mm, "end": v(-4214.45, 4052.82) * mm});
            skLineSegment(sketch, "E3223", {"start": v(-4214.45, 4052.82) * mm, "end": v(-4170.62, 3938.1) * mm});
            skLineSegment(sketch, "E3224", {"start": v(-4616.63, 4299.03) * mm, "end": v(-4626.94, 4349.3) * mm});
            skLineSegment(sketch, "E3225", {"start": v(-4626.94, 4349.3) * mm, "end": v(-4655.3, 4399.58) * mm});
            skLineSegment(sketch, "E3226", {"start": v(-5016.24, 4099.23) * mm, "end": v(-5000.77, 4041.22) * mm});
            skLineSegment(sketch, "E3227", {"start": v(-5000.77, 4041.22) * mm, "end": v(-4963.39, 3980.64) * mm});
            skLineSegment(sketch, "E3228", {"start": v(-4963.39, 3980.64) * mm, "end": v(-4900.22, 3941.96) * mm});
            skLineSegment(sketch, "E3229", {"start": v(-4900.22, 3941.96) * mm, "end": v(-4833.2, 3927.79) * mm});
            skLineSegment(sketch, "E3230", {"start": v(-4833.2, 3927.79) * mm, "end": v(-4768.74, 3930.36) * mm});
            skLineSegment(sketch, "E3231", {"start": v(-4768.74, 3930.36) * mm, "end": v(-4684.95, 3950.99) * mm});
            skLineSegment(sketch, "E3232", {"start": v(-4684.95, 3950.99) * mm, "end": v(-4630.81, 3998.68) * mm});
            skLineSegment(sketch, "E3233", {"start": v(-4630.81, 3998.68) * mm, "end": v(-4605.03, 4047.67) * mm});
            skLineSegment(sketch, "E3234", {"start": v(-4605.03, 4047.67) * mm, "end": v(-4605.03, 4112.12) * mm});
            skLineSegment(sketch, "E3235", {"start": v(-4605.03, 4112.12) * mm, "end": v(-4623.08, 4163.68) * mm});
            skLineSegment(sketch, "E3236", {"start": v(-4623.08, 4163.68) * mm, "end": v(-4664.33, 4208.8) * mm});
            skLineSegment(sketch, "E3237", {"start": v(-4664.33, 4208.8) * mm, "end": v(-4740.38, 4238.45) * mm});
            skLineSegment(sketch, "E3238", {"start": v(-6349.27, 4215.6) * mm, "end": v(-6349.27, 4129.23) * mm});
            skLineSegment(sketch, "E3239", {"start": v(-6349.27, 4129.23) * mm, "end": v(-6275.61, 4129.23) * mm});
            skLineSegment(sketch, "E3240", {"start": v(-6275.61, 4129.23) * mm, "end": v(-6232.43, 4131.77) * mm});
            skLineSegment(sketch, "E3241", {"start": v(-6232.43, 4131.77) * mm, "end": v(-6181.63, 4147.01) * mm});
            skLineSegment(sketch, "E3242", {"start": v(-6181.63, 4147.01) * mm, "end": v(-6143.53, 4172.41) * mm});
            skLineSegment(sketch, "E3243", {"start": v(-6143.53, 4172.41) * mm, "end": v(-6120.67, 4200.35) * mm});
            skLineSegment(sketch, "E3244", {"start": v(-6120.67, 4200.35) * mm, "end": v(-6105.43, 4233.37) * mm});
            skLineSegment(sketch, "E3245", {"start": v(-6105.43, 4233.37) * mm, "end": v(-6100.35, 4266.4) * mm});
            skLineSegment(sketch, "E3246", {"start": v(-6100.35, 4266.4) * mm, "end": v(-6100.35, 4309.57) * mm});
            skLineSegment(sketch, "E3247", {"start": v(-6100.35, 4309.57) * mm, "end": v(-6107.97, 4347.67) * mm});
            skLineSegment(sketch, "E3248", {"start": v(-6107.97, 4347.67) * mm, "end": v(-6125.75, 4380.7) * mm});
            skLineSegment(sketch, "E3249", {"start": v(-6125.75, 4380.7) * mm, "end": v(-6146.07, 4406.1) * mm});
            skLineSegment(sketch, "E3250", {"start": v(-5682.89, 3936.29) * mm, "end": v(-5559.08, 3936.29) * mm});
            skLineSegment(sketch, "E3251", {"start": v(-5559.08, 3936.29) * mm, "end": v(-5665.28, 4105.17) * mm});
            skLineSegment(sketch, "E3252", {"start": v(-5665.28, 4105.17) * mm, "end": v(-5689.62, 4129.52) * mm});
            skLineSegment(sketch, "E3253", {"start": v(-5689.62, 4129.52) * mm, "end": v(-5709.2, 4147.01) * mm});
            skLineSegment(sketch, "E3254", {"start": v(-5876.83, 4129.23) * mm, "end": v(-5816.03, 4129.23) * mm});
            skLineSegment(sketch, "E3255", {"start": v(-5503.45, 4444.2) * mm, "end": v(-5504.47, 4165.13) * mm});
            skLineSegment(sketch, "E3256", {"start": v(-5504.47, 4165.13) * mm, "end": v(-5498.88, 4073.13) * mm});
            skLineSegment(sketch, "E3257", {"start": v(-5498.88, 4073.13) * mm, "end": v(-5488.93, 4030.86) * mm});
            skLineSegment(sketch, "E3258", {"start": v(-5488.93, 4030.86) * mm, "end": v(-5474.01, 4000.4) * mm});
            skLineSegment(sketch, "E3259", {"start": v(-5474.01, 4000.4) * mm, "end": v(-5450.39, 3972.42) * mm});
            skLineSegment(sketch, "E3260", {"start": v(-5450.39, 3972.42) * mm, "end": v(-5418.68, 3951.29) * mm});
            skLineSegment(sketch, "E3261", {"start": v(-5836.2, 4215.6) * mm, "end": v(-5876.83, 4215.6) * mm});
            skLineSegment(sketch, "E3262", {"start": v(-5876.83, 4215.6) * mm, "end": v(-5876.83, 4129.23) * mm});
            skLineSegment(sketch, "E3263", {"start": v(-5709.2, 4147.01) * mm, "end": v(-5671.1, 4172.41) * mm});
            skLineSegment(sketch, "E3264", {"start": v(-5671.1, 4172.41) * mm, "end": v(-5648.23, 4200.35) * mm});
            skLineSegment(sketch, "E3265", {"start": v(-5648.23, 4200.35) * mm, "end": v(-5633, 4233.37) * mm});
            skLineSegment(sketch, "E3266", {"start": v(-5633, 4233.37) * mm, "end": v(-5627.91, 4266.4) * mm});
            skLineSegment(sketch, "E3267", {"start": v(-5627.91, 4266.4) * mm, "end": v(-5627.91, 4309.57) * mm});
            skLineSegment(sketch, "E3268", {"start": v(-5627.91, 4309.57) * mm, "end": v(-5635.53, 4347.67) * mm});
            skLineSegment(sketch, "E3269", {"start": v(-5635.53, 4347.67) * mm, "end": v(-5653.31, 4380.7) * mm});
            skLineSegment(sketch, "E3270", {"start": v(-5653.31, 4380.7) * mm, "end": v(-5673.63, 4406.1) * mm});
            skLineSegment(sketch, "E3271", {"start": v(-5673.63, 4406.1) * mm, "end": v(-5706.65, 4428.95) * mm});
            skLineSegment(sketch, "E3272", {"start": v(-6488.97, 4444.2) * mm, "end": v(-6488.97, 3936.2) * mm});
            skLineSegment(sketch, "E3273", {"start": v(-6488.97, 3936.2) * mm, "end": v(-6387.37, 3936.2) * mm});
            skLineSegment(sketch, "E3274", {"start": v(-6387.37, 3936.2) * mm, "end": v(-6387.37, 4357.83) * mm});
            skLineSegment(sketch, "E3275", {"start": v(-6387.37, 4357.83) * mm, "end": v(-6278.15, 4357.83) * mm});
            skLineSegment(sketch, "E3276", {"start": v(-6278.15, 4357.83) * mm, "end": v(-6252.75, 4352.75) * mm});
            skLineSegment(sketch, "E3277", {"start": v(-5472.97, -3836.2) * mm, "end": v(-5472.97, -4193.47) * mm});
            skLineSegment(sketch, "E3278", {"start": v(-5472.97, -4193.47) * mm, "end": v(-5468.86, -4224.74) * mm});
            skLineSegment(sketch, "E3279", {"start": v(-5468.86, -4224.74) * mm, "end": v(-5456.15, -4255.42) * mm});
            skLineSegment(sketch, "E3280", {"start": v(-5456.15, -4255.42) * mm, "end": v(-5435.93, -4281.77) * mm});
            skLineSegment(sketch, "E3281", {"start": v(-5435.93, -4281.77) * mm, "end": v(-5409.58, -4301.98) * mm});
            skLineSegment(sketch, "E3282", {"start": v(-5409.58, -4301.98) * mm, "end": v(-5378.9, -4314.7) * mm});
            skLineSegment(sketch, "E3283", {"start": v(-5378.9, -4314.7) * mm, "end": v(-5345.97, -4319.03) * mm});
            skLineSegment(sketch, "E3284", {"start": v(-5345.97, -4319.03) * mm, "end": v(-5313.05, -4314.7) * mm});
            skLineSegment(sketch, "E3285", {"start": v(-5313.05, -4314.7) * mm, "end": v(-5282.36, -4301.98) * mm});
            skLineSegment(sketch, "E3286", {"start": v(-5282.36, -4301.98) * mm, "end": v(-5256.02, -4281.77) * mm});
            skLineSegment(sketch, "E3287", {"start": v(-5256.02, -4281.77) * mm, "end": v(-5235.8, -4255.42) * mm});
            skLineSegment(sketch, "E3288", {"start": v(-5235.8, -4255.42) * mm, "end": v(-5223.09, -4224.74) * mm});
            skLineSegment(sketch, "E3289", {"start": v(-5223.09, -4224.74) * mm, "end": v(-5218.97, -4193.47) * mm});
            skLineSegment(sketch, "E3290", {"start": v(-5218.97, -4193.47) * mm, "end": v(-5218.97, -3836.2) * mm});
            skLineSegment(sketch, "E3291", {"start": v(-5472.97, -3836.2) * mm, "end": v(-5472.97, -3810.8) * mm});
            skLineSegment(sketch, "E3292", {"start": v(-5218.97, -3810.8) * mm, "end": v(-5091.97, -3683.8) * mm});
            skLineSegment(sketch, "E3293", {"start": v(-5218.97, -3836.2) * mm, "end": v(-5218.97, -3810.8) * mm});
            skLineSegment(sketch, "E3294", {"start": v(-1154.97, -3836.2) * mm, "end": v(-1154.97, -4193.47) * mm});
            skLineSegment(sketch, "E3295", {"start": v(-1154.97, -4193.47) * mm, "end": v(-1150.86, -4224.74) * mm});
            skLineSegment(sketch, "E3296", {"start": v(-1150.86, -4224.74) * mm, "end": v(-1138.15, -4255.42) * mm});
            skLineSegment(sketch, "E3297", {"start": v(-1138.15, -4255.42) * mm, "end": v(-1117.93, -4281.77) * mm});
            skLineSegment(sketch, "E3298", {"start": v(-1117.93, -4281.77) * mm, "end": v(-1091.58, -4301.98) * mm});
            skLineSegment(sketch, "E3299", {"start": v(-1091.58, -4301.98) * mm, "end": v(-1060.9, -4314.7) * mm});
            skLineSegment(sketch, "E3300", {"start": v(-1060.9, -4314.7) * mm, "end": v(-1027.97, -4319.03) * mm});
            skLineSegment(sketch, "E3301", {"start": v(-1027.97, -4319.03) * mm, "end": v(-995.05, -4314.7) * mm});
            skLineSegment(sketch, "E3302", {"start": v(-995.05, -4314.7) * mm, "end": v(-964.36, -4301.98) * mm});
            skLineSegment(sketch, "E3303", {"start": v(-964.36, -4301.98) * mm, "end": v(-938.02, -4281.77) * mm});
            skLineSegment(sketch, "E3304", {"start": v(-938.02, -4281.77) * mm, "end": v(-917.8, -4255.42) * mm});
            skLineSegment(sketch, "E3305", {"start": v(-917.8, -4255.42) * mm, "end": v(-905.09, -4224.74) * mm});
            skLineSegment(sketch, "E3306", {"start": v(-905.09, -4224.74) * mm, "end": v(-900.97, -4193.47) * mm});
            skLineSegment(sketch, "E3307", {"start": v(-900.97, -4193.47) * mm, "end": v(-900.97, -3836.2) * mm});
            skLineSegment(sketch, "E3308", {"start": v(-1154.97, -3810.8) * mm, "end": v(-1281.97, -3683.8) * mm});
            skLineSegment(sketch, "E3309", {"start": v(-1154.97, -3836.2) * mm, "end": v(-1154.97, -3810.8) * mm});
            skLineSegment(sketch, "E3310", {"start": v(-900.97, -3836.2) * mm, "end": v(-900.97, -3810.8) * mm});
            skLineSegment(sketch, "E3311", {"start": v(-5853.97, -3683.8) * mm, "end": v(-5599.97, -3683.8) * mm});
            skLineSegment(sketch, "E3312", {"start": v(-5599.97, -3683.8) * mm, "end": v(-5472.97, -3810.8) * mm});
            skLineSegment(sketch, "E3313", {"start": v(-519.97, -3683.8) * mm, "end": v(-773.97, -3683.8) * mm});
            skLineSegment(sketch, "E3314", {"start": v(-900.97, -3810.8) * mm, "end": v(-773.97, -3683.8) * mm});
            skSolve(sketch);
        }
        {
            var Q0;
            Q0=makeQuery(id+"F0.imprint","IMPRINT",FACE,{"disambiguationData":[TD([[makeQuery(id+"F0.imprint","IMPRINT",EDGE,{"derivedFrom":sQuery(id+"F0.wireOp",EDGE,"E8")}),-1.0]])]});
            extrude(context, id + "F1", {"entities" : qUnion([Q0]), "depth" : 6 * mm, "offsetDistance" : 25.4 * mm});
        }
    });
